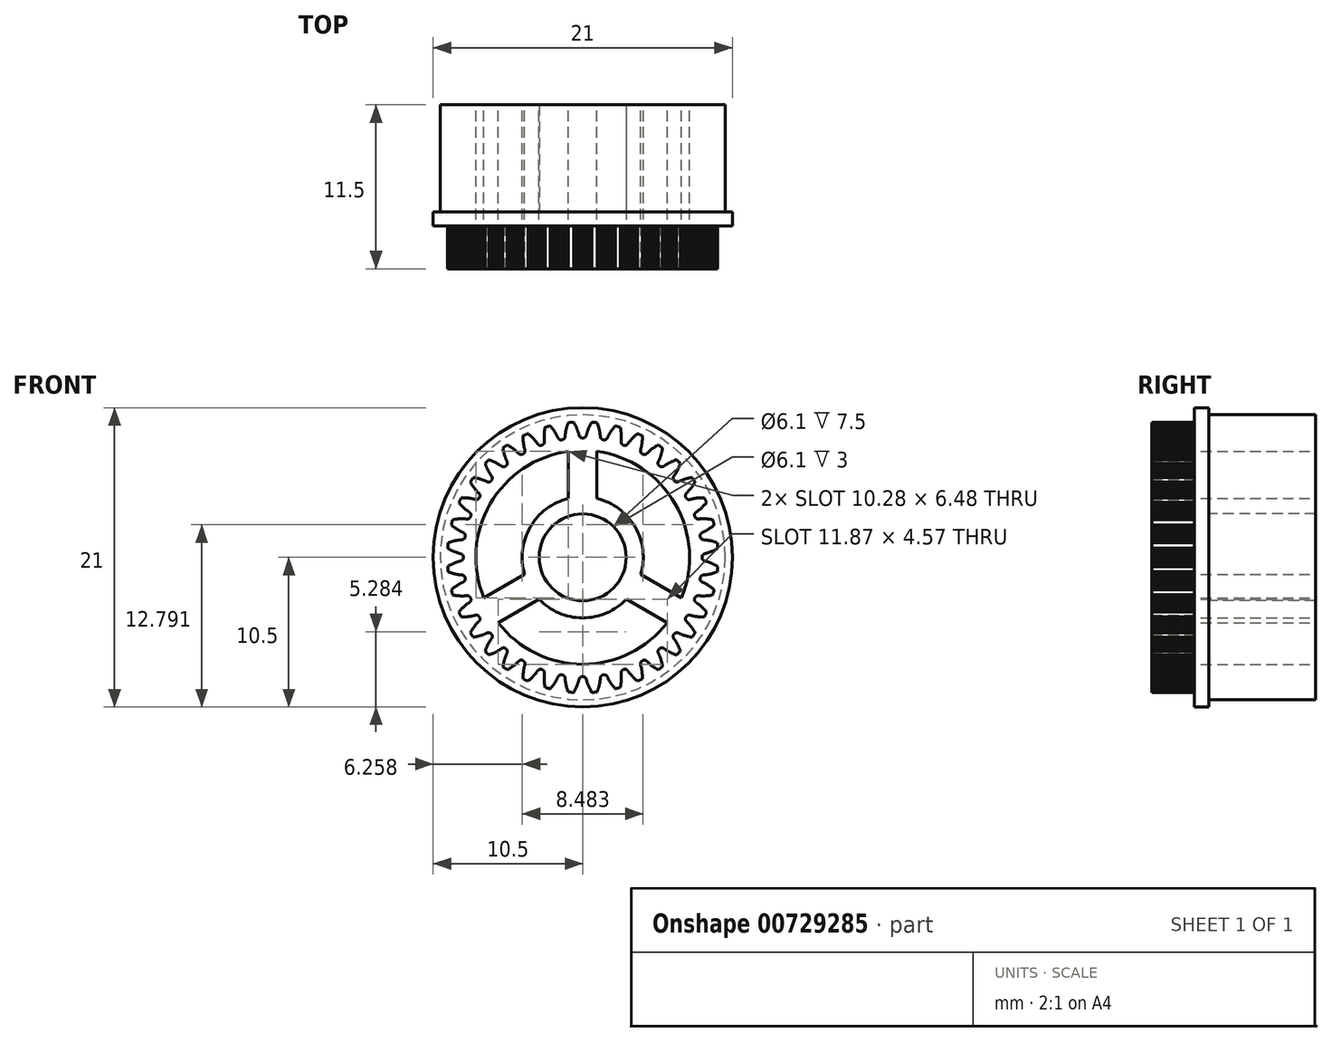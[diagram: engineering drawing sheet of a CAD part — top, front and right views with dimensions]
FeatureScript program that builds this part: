
annotation { "Feature Type Name" : "Feature", "Feature Type Description" : "" }
export const myFeature = defineFeature(function(context is Context, id is Id, definition is map)
    precondition{}
    {
        {
            var Q0;
            Q0=qCreatedBy(makeId("Front.planeOp"),FACE);
            var sketch = newSketch(context, id + "F0", { "sketchPlane" : qUnion([Q0])});
            skLineSegment(sketch, "E0", {"start": v(8.38, 0) * mm, "end": v(8.37, 0) * mm});
            skLineSegment(sketch, "E1", {"start": v(8.37, 0) * mm, "end": v(8.37, 0.01) * mm});
            skLineSegment(sketch, "E2", {"start": v(8.37, 0.01) * mm, "end": v(8.37, 0.02) * mm});
            skLineSegment(sketch, "E3", {"start": v(8.37, 0.02) * mm, "end": v(8.37, 0.02) * mm});
            skLineSegment(sketch, "E4", {"start": v(8.37, 0.02) * mm, "end": v(8.37, 0.03) * mm});
            skLineSegment(sketch, "E5", {"start": v(8.37, 0.03) * mm, "end": v(8.38, 0.06) * mm});
            skLineSegment(sketch, "E6", {"start": v(8.38, 0.06) * mm, "end": v(8.38, 0.08) * mm});
            skLineSegment(sketch, "E7", {"start": v(8.38, 0.08) * mm, "end": v(8.39, 0.1) * mm});
            skLineSegment(sketch, "E8", {"start": v(8.39, 0.1) * mm, "end": v(8.4, 0.11) * mm});
            skLineSegment(sketch, "E9", {"start": v(8.4, 0.11) * mm, "end": v(8.4, 0.13) * mm});
            skLineSegment(sketch, "E10", {"start": v(8.4, 0.13) * mm, "end": v(8.4, 0.14) * mm});
            skLineSegment(sketch, "E11", {"start": v(8.4, 0.14) * mm, "end": v(8.42, 0.16) * mm});
            skLineSegment(sketch, "E12", {"start": v(8.42, 0.16) * mm, "end": v(8.43, 0.17) * mm});
            skLineSegment(sketch, "E13", {"start": v(8.43, 0.17) * mm, "end": v(8.44, 0.18) * mm});
            skLineSegment(sketch, "E14", {"start": v(8.44, 0.18) * mm, "end": v(8.45, 0.2) * mm});
            skLineSegment(sketch, "E15", {"start": v(8.45, 0.2) * mm, "end": v(8.46, 0.2) * mm});
            skLineSegment(sketch, "E16", {"start": v(8.46, 0.2) * mm, "end": v(8.48, 0.21) * mm});
            skLineSegment(sketch, "E17", {"start": v(8.48, 0.21) * mm, "end": v(8.5, 0.22) * mm});
            skLineSegment(sketch, "E18", {"start": v(8.5, 0.22) * mm, "end": v(8.5, 0.23) * mm});
            skLineSegment(sketch, "E19", {"start": v(8.5, 0.23) * mm, "end": v(8.52, 0.24) * mm});
            skLineSegment(sketch, "E20", {"start": v(8.52, 0.24) * mm, "end": v(8.54, 0.25) * mm});
            skLineSegment(sketch, "E21", {"start": v(8.54, 0.25) * mm, "end": v(8.55, 0.25) * mm});
            skLineSegment(sketch, "E22", {"start": v(8.55, 0.25) * mm, "end": v(8.57, 0.26) * mm});
            skLineSegment(sketch, "E23", {"start": v(8.57, 0.26) * mm, "end": v(8.59, 0.26) * mm});
            skLineSegment(sketch, "E24", {"start": v(8.59, 0.26) * mm, "end": v(8.6, 0.27) * mm});
            skLineSegment(sketch, "E25", {"start": v(8.6, 0.27) * mm, "end": v(8.65, 0.28) * mm});
            skLineSegment(sketch, "E26", {"start": v(8.65, 0.28) * mm, "end": v(8.7, 0.29) * mm});
            skLineSegment(sketch, "E27", {"start": v(8.7, 0.29) * mm, "end": v(8.74, 0.3) * mm});
            skLineSegment(sketch, "E28", {"start": v(8.74, 0.3) * mm, "end": v(8.78, 0.32) * mm});
            skLineSegment(sketch, "E29", {"start": v(8.78, 0.32) * mm, "end": v(8.83, 0.33) * mm});
            skLineSegment(sketch, "E30", {"start": v(8.83, 0.33) * mm, "end": v(8.87, 0.35) * mm});
            skLineSegment(sketch, "E31", {"start": v(8.87, 0.35) * mm, "end": v(8.91, 0.36) * mm});
            skLineSegment(sketch, "E32", {"start": v(8.91, 0.36) * mm, "end": v(8.96, 0.38) * mm});
            skLineSegment(sketch, "E33", {"start": v(8.96, 0.38) * mm, "end": v(9, 0.4) * mm});
            skLineSegment(sketch, "E34", {"start": v(9, 0.4) * mm, "end": v(9.05, 0.42) * mm});
            skLineSegment(sketch, "E35", {"start": v(9.05, 0.42) * mm, "end": v(9.09, 0.44) * mm});
            skLineSegment(sketch, "E36", {"start": v(9.09, 0.44) * mm, "end": v(9.13, 0.46) * mm});
            skLineSegment(sketch, "E37", {"start": v(9.13, 0.46) * mm, "end": v(9.18, 0.48) * mm});
            skLineSegment(sketch, "E38", {"start": v(9.18, 0.48) * mm, "end": v(9.22, 0.5) * mm});
            skLineSegment(sketch, "E39", {"start": v(9.22, 0.5) * mm, "end": v(9.26, 0.52) * mm});
            skLineSegment(sketch, "E40", {"start": v(9.26, 0.52) * mm, "end": v(9.3, 0.54) * mm});
            skLineSegment(sketch, "E41", {"start": v(9.3, 0.54) * mm, "end": v(9.35, 0.57) * mm});
            skLineSegment(sketch, "E42", {"start": v(9.35, 0.57) * mm, "end": v(9.4, 0.6) * mm});
            skLineSegment(sketch, "E43", {"start": v(9.4, 0.6) * mm, "end": v(9.44, 0.61) * mm});
            skLineSegment(sketch, "E44", {"start": v(9.44, 0.61) * mm, "end": v(9.48, 0.64) * mm});
            skLineSegment(sketch, "E45", {"start": v(9.48, 0.64) * mm, "end": v(9.48, 0.68) * mm});
            skLineSegment(sketch, "E46", {"start": v(9.48, 0.68) * mm, "end": v(9.47, 0.72) * mm});
            skLineSegment(sketch, "E47", {"start": v(9.47, 0.72) * mm, "end": v(9.47, 0.75) * mm});
            skLineSegment(sketch, "E48", {"start": v(9.47, 0.75) * mm, "end": v(9.47, 0.8) * mm});
            skLineSegment(sketch, "E49", {"start": v(9.47, 0.8) * mm, "end": v(9.46, 0.83) * mm});
            skLineSegment(sketch, "E50.MirrorCS", {"start": v(8.37, -0.02) * mm, "end": v(8.37, -0.03) * mm});
            skLineSegment(sketch, "E51.MirrorCS", {"start": v(8.37, 0) * mm, "end": v(8.37, -0.01) * mm});
            skLineSegment(sketch, "E52.MirrorCS", {"start": v(8.37, -0.02) * mm, "end": v(8.37, -0.02) * mm});
            skLineSegment(sketch, "E53.MirrorCS", {"start": v(8.37, -0.03) * mm, "end": v(8.38, -0.06) * mm});
            skLineSegment(sketch, "E54.MirrorCS", {"start": v(8.37, -0.01) * mm, "end": v(8.37, -0.02) * mm});
            skLineSegment(sketch, "E55.MirrorCS", {"start": v(8.38, -0.06) * mm, "end": v(8.38, -0.08) * mm});
            skLineSegment(sketch, "E56.MirrorCS", {"start": v(8.43, -0.17) * mm, "end": v(8.44, -0.18) * mm});
            skLineSegment(sketch, "E57.MirrorCS", {"start": v(8.52, -0.24) * mm, "end": v(8.54, -0.25) * mm});
            skLineSegment(sketch, "E58.MirrorCS", {"start": v(8.42, -0.16) * mm, "end": v(8.43, -0.17) * mm});
            skLineSegment(sketch, "E59.MirrorCS", {"start": v(8.5, -0.23) * mm, "end": v(8.52, -0.24) * mm});
            skLineSegment(sketch, "E60.MirrorCS", {"start": v(8.5, -0.22) * mm, "end": v(8.5, -0.23) * mm});
            skLineSegment(sketch, "E61.MirrorCS", {"start": v(9.47, -0.72) * mm, "end": v(9.47, -0.75) * mm});
            skLineSegment(sketch, "E62.MirrorCS", {"start": v(9.48, -0.68) * mm, "end": v(9.47, -0.72) * mm});
            skLineSegment(sketch, "E63.MirrorCS", {"start": v(8.46, -0.2) * mm, "end": v(8.48, -0.21) * mm});
            skLineSegment(sketch, "E64.MirrorCS", {"start": v(8.48, -0.21) * mm, "end": v(8.5, -0.22) * mm});
            skLineSegment(sketch, "E65.MirrorCS", {"start": v(8.4, -0.14) * mm, "end": v(8.42, -0.16) * mm});
            skLineSegment(sketch, "E66.MirrorCS", {"start": v(8.4, -0.13) * mm, "end": v(8.4, -0.14) * mm});
            skLineSegment(sketch, "E67.MirrorCS", {"start": v(8.4, -0.11) * mm, "end": v(8.4, -0.13) * mm});
            skLineSegment(sketch, "E68.MirrorCS", {"start": v(8.45, -0.2) * mm, "end": v(8.46, -0.2) * mm});
            skLineSegment(sketch, "E69.MirrorCS", {"start": v(8.44, -0.18) * mm, "end": v(8.45, -0.2) * mm});
            skLineSegment(sketch, "E70.MirrorCS", {"start": v(8.54, -0.25) * mm, "end": v(8.55, -0.25) * mm});
            skLineSegment(sketch, "E71.MirrorCS", {"start": v(8.55, -0.25) * mm, "end": v(8.57, -0.26) * mm});
            skLineSegment(sketch, "E72.MirrorCS", {"start": v(9.47, -0.75) * mm, "end": v(9.47, -0.8) * mm});
            skLineSegment(sketch, "E73.MirrorCS", {"start": v(8.57, -0.26) * mm, "end": v(8.59, -0.26) * mm});
            skLineSegment(sketch, "E74.MirrorCS", {"start": v(9.48, -0.64) * mm, "end": v(9.48, -0.68) * mm});
            skLineSegment(sketch, "E75.MirrorCS", {"start": v(8.38, -0.08) * mm, "end": v(8.39, -0.1) * mm});
            skLineSegment(sketch, "E76.MirrorCS", {"start": v(9.26, -0.52) * mm, "end": v(9.3, -0.54) * mm});
            skLineSegment(sketch, "E77.MirrorCS", {"start": v(8.74, -0.3) * mm, "end": v(8.78, -0.32) * mm});
            skLineSegment(sketch, "E78.MirrorCS", {"start": v(9.44, -0.61) * mm, "end": v(9.48, -0.64) * mm});
            skLineSegment(sketch, "E79.MirrorCS", {"start": v(8.78, -0.32) * mm, "end": v(8.83, -0.33) * mm});
            skLineSegment(sketch, "E80.MirrorCS", {"start": v(8.65, -0.28) * mm, "end": v(8.7, -0.29) * mm});
            skLineSegment(sketch, "E81.MirrorCS", {"start": v(9.13, -0.46) * mm, "end": v(9.18, -0.48) * mm});
            skLineSegment(sketch, "E82.MirrorCS", {"start": v(8.83, -0.33) * mm, "end": v(8.87, -0.35) * mm});
            skLineSegment(sketch, "E83.MirrorCS", {"start": v(8.91, -0.36) * mm, "end": v(8.96, -0.38) * mm});
            skLineSegment(sketch, "E84.MirrorCS", {"start": v(9.09, -0.44) * mm, "end": v(9.13, -0.46) * mm});
            skLineSegment(sketch, "E85.MirrorCS", {"start": v(9.22, -0.5) * mm, "end": v(9.26, -0.52) * mm});
            skLineSegment(sketch, "E86.MirrorCS", {"start": v(9.4, -0.6) * mm, "end": v(9.44, -0.61) * mm});
            skLineSegment(sketch, "E87.MirrorCS", {"start": v(8.96, -0.38) * mm, "end": v(9, -0.4) * mm});
            skLineSegment(sketch, "E88.MirrorCS", {"start": v(9.47, -0.8) * mm, "end": v(9.46, -0.83) * mm});
            skLineSegment(sketch, "E89.MirrorCS", {"start": v(9.05, -0.42) * mm, "end": v(9.09, -0.44) * mm});
            skLineSegment(sketch, "E90.MirrorCS", {"start": v(9, -0.4) * mm, "end": v(9.05, -0.42) * mm});
            skLineSegment(sketch, "E91.MirrorCS", {"start": v(9.35, -0.57) * mm, "end": v(9.4, -0.6) * mm});
            skLineSegment(sketch, "E92.MirrorCS", {"start": v(8.87, -0.35) * mm, "end": v(8.91, -0.36) * mm});
            skLineSegment(sketch, "E93.MirrorCS", {"start": v(9.18, -0.48) * mm, "end": v(9.22, -0.5) * mm});
            skLineSegment(sketch, "E94.MirrorCS", {"start": v(8.6, -0.27) * mm, "end": v(8.65, -0.28) * mm});
            skLineSegment(sketch, "E95.MirrorCS", {"start": v(8.7, -0.29) * mm, "end": v(8.74, -0.3) * mm});
            skLineSegment(sketch, "E96.MirrorCS", {"start": v(9.3, -0.54) * mm, "end": v(9.35, -0.57) * mm});
            skLineSegment(sketch, "E97.MirrorCS", {"start": v(8.39, -0.1) * mm, "end": v(8.4, -0.11) * mm});
            skLineSegment(sketch, "E98.MirrorCS", {"start": v(8.59, -0.26) * mm, "end": v(8.6, -0.27) * mm});
            skLineSegment(sketch, "E99.1.0", {"start": v(9.26, 1.08) * mm, "end": v(9.3, 1.07) * mm});
            skLineSegment(sketch, "E99.1.1", {"start": v(9.07, 2.15) * mm, "end": v(9.1, 2.18) * mm});
            skLineSegment(sketch, "E99.1.2", {"start": v(9.46, 0.87) * mm, "end": v(9.46, 0.83) * mm});
            skLineSegment(sketch, "E99.1.3", {"start": v(9.46, 0.9) * mm, "end": v(9.46, 0.87) * mm});
            skLineSegment(sketch, "E99.1.4", {"start": v(9.07, 1.14) * mm, "end": v(9.12, 1.12) * mm});
            skLineSegment(sketch, "E99.1.5", {"start": v(8.72, 1.9) * mm, "end": v(8.76, 1.93) * mm});
            skLineSegment(sketch, "E99.1.6", {"start": v(8.98, 1.16) * mm, "end": v(9.03, 1.15) * mm});
            skLineSegment(sketch, "E99.1.7", {"start": v(8.66, 1.22) * mm, "end": v(8.7, 1.21) * mm});
            skLineSegment(sketch, "E99.1.8", {"start": v(9.03, 1.15) * mm, "end": v(9.07, 1.14) * mm});
            skLineSegment(sketch, "E99.1.9", {"start": v(8.75, 1.2) * mm, "end": v(8.8, 1.2) * mm});
            skLineSegment(sketch, "E99.1.10", {"start": v(8.8, 1.95) * mm, "end": v(8.84, 1.98) * mm});
            skLineSegment(sketch, "E99.1.11", {"start": v(8.6, 1.84) * mm, "end": v(8.64, 1.86) * mm});
            skLineSegment(sketch, "E99.1.12", {"start": v(8.88, 2) * mm, "end": v(8.92, 2.03) * mm});
            skLineSegment(sketch, "E99.1.13", {"start": v(8.89, 1.18) * mm, "end": v(8.93, 1.17) * mm});
            skLineSegment(sketch, "E99.1.14", {"start": v(9.3, 1.07) * mm, "end": v(9.35, 1.05) * mm});
            skLineSegment(sketch, "E99.1.15", {"start": v(8.84, 1.2) * mm, "end": v(8.89, 1.18) * mm});
            skLineSegment(sketch, "E99.1.16", {"start": v(9.21, 1.1) * mm, "end": v(9.26, 1.08) * mm});
            skLineSegment(sketch, "E99.1.17", {"start": v(8.93, 1.17) * mm, "end": v(8.98, 1.16) * mm});
            skLineSegment(sketch, "E99.1.18", {"start": v(9.03, 2.12) * mm, "end": v(9.07, 2.15) * mm});
            skLineSegment(sketch, "E99.1.19", {"start": v(9.35, 1.05) * mm, "end": v(9.4, 1.03) * mm});
            skLineSegment(sketch, "E99.1.20", {"start": v(9.45, 0.94) * mm, "end": v(9.46, 0.9) * mm});
            skLineSegment(sketch, "E99.1.21", {"start": v(8.55, 1.81) * mm, "end": v(8.6, 1.84) * mm});
            skLineSegment(sketch, "E99.1.22", {"start": v(8.68, 1.88) * mm, "end": v(8.72, 1.9) * mm});
            skLineSegment(sketch, "E99.1.23", {"start": v(8.95, 2.06) * mm, "end": v(9, 2.1) * mm});
            skLineSegment(sketch, "E99.1.24", {"start": v(9.12, 1.12) * mm, "end": v(9.17, 1.11) * mm});
            skLineSegment(sketch, "E99.1.25", {"start": v(8.7, 1.21) * mm, "end": v(8.75, 1.2) * mm});
            skLineSegment(sketch, "E99.1.26", {"start": v(9.4, 1.03) * mm, "end": v(9.45, 1.02) * mm});
            skLineSegment(sketch, "E99.1.27", {"start": v(9.45, 0.98) * mm, "end": v(9.45, 0.94) * mm});
            skLineSegment(sketch, "E99.1.28", {"start": v(9.17, 1.11) * mm, "end": v(9.21, 1.1) * mm});
            skLineSegment(sketch, "E99.1.29", {"start": v(8.76, 1.93) * mm, "end": v(8.8, 1.95) * mm});
            skLineSegment(sketch, "E99.1.30", {"start": v(9, 2.1) * mm, "end": v(9.03, 2.12) * mm});
            skLineSegment(sketch, "E99.1.31", {"start": v(8.8, 1.2) * mm, "end": v(8.84, 1.2) * mm});
            skLineSegment(sketch, "E99.1.32", {"start": v(8.92, 2.03) * mm, "end": v(8.95, 2.06) * mm});
            skLineSegment(sketch, "E99.1.33", {"start": v(8.64, 1.86) * mm, "end": v(8.68, 1.88) * mm});
            skLineSegment(sketch, "E99.1.34", {"start": v(9.1, 2.18) * mm, "end": v(9.15, 2.21) * mm});
            skLineSegment(sketch, "E99.1.35", {"start": v(9.19, 2.42) * mm, "end": v(9.18, 2.46) * mm});
            skLineSegment(sketch, "E99.1.36", {"start": v(8.84, 1.98) * mm, "end": v(8.88, 2) * mm});
            skLineSegment(sketch, "E99.1.37", {"start": v(9.2, 2.39) * mm, "end": v(9.19, 2.42) * mm});
            skLineSegment(sketch, "E99.1.38", {"start": v(9.15, 2.21) * mm, "end": v(9.19, 2.24) * mm});
            skLineSegment(sketch, "E99.1.39", {"start": v(9.45, 1.02) * mm, "end": v(9.45, 0.98) * mm});
            skLineSegment(sketch, "E99.1.40", {"start": v(9.19, 2.24) * mm, "end": v(9.22, 2.28) * mm});
            skLineSegment(sketch, "E99.1.41", {"start": v(9.2, 2.35) * mm, "end": v(9.2, 2.39) * mm});
            skLineSegment(sketch, "E99.1.42", {"start": v(9.21, 2.31) * mm, "end": v(9.2, 2.35) * mm});
            skLineSegment(sketch, "E99.1.43", {"start": v(8.51, 1.8) * mm, "end": v(8.55, 1.81) * mm});
            skLineSegment(sketch, "E99.1.44", {"start": v(9.22, 2.28) * mm, "end": v(9.21, 2.31) * mm});
            skLineSegment(sketch, "E99.1.45", {"start": v(8.61, 1.23) * mm, "end": v(8.66, 1.22) * mm});
            skLineSegment(sketch, "E99.1.46", {"start": v(8.32, 1.7) * mm, "end": v(8.34, 1.7) * mm});
            skLineSegment(sketch, "E99.1.47", {"start": v(8.43, 1.76) * mm, "end": v(8.47, 1.78) * mm});
            skLineSegment(sketch, "E99.1.48", {"start": v(8.47, 1.78) * mm, "end": v(8.51, 1.8) * mm});
            skLineSegment(sketch, "E99.1.49", {"start": v(8.43, 1.24) * mm, "end": v(8.45, 1.24) * mm});
            skLineSegment(sketch, "E99.1.50", {"start": v(8.35, 1.71) * mm, "end": v(8.36, 1.72) * mm});
            skLineSegment(sketch, "E99.1.51", {"start": v(8.38, 1.26) * mm, "end": v(8.4, 1.25) * mm});
            skLineSegment(sketch, "E99.1.52", {"start": v(8.57, 1.23) * mm, "end": v(8.61, 1.23) * mm});
            skLineSegment(sketch, "E99.1.53", {"start": v(8.47, 1.24) * mm, "end": v(8.48, 1.23) * mm});
            skLineSegment(sketch, "E99.1.54", {"start": v(8.5, 1.23) * mm, "end": v(8.52, 1.23) * mm});
            skLineSegment(sketch, "E99.1.55", {"start": v(8.36, 1.72) * mm, "end": v(8.38, 1.73) * mm});
            skLineSegment(sketch, "E99.1.56", {"start": v(8.41, 1.75) * mm, "end": v(8.43, 1.76) * mm});
            skLineSegment(sketch, "E99.1.57", {"start": v(8.45, 1.24) * mm, "end": v(8.47, 1.24) * mm});
            skLineSegment(sketch, "E99.1.58", {"start": v(8.31, 1.68) * mm, "end": v(8.32, 1.7) * mm});
            skLineSegment(sketch, "E99.1.59", {"start": v(8.52, 1.23) * mm, "end": v(8.57, 1.23) * mm});
            skLineSegment(sketch, "E99.1.60", {"start": v(8.4, 1.74) * mm, "end": v(8.41, 1.75) * mm});
            skLineSegment(sketch, "E99.1.61", {"start": v(8.34, 1.7) * mm, "end": v(8.35, 1.71) * mm});
            skLineSegment(sketch, "E99.1.62", {"start": v(8.48, 1.23) * mm, "end": v(8.5, 1.23) * mm});
            skLineSegment(sketch, "E99.1.63", {"start": v(8.38, 1.73) * mm, "end": v(8.4, 1.74) * mm});
            skLineSegment(sketch, "E99.1.64", {"start": v(8.3, 1.67) * mm, "end": v(8.31, 1.68) * mm});
            skLineSegment(sketch, "E99.1.65", {"start": v(8.37, 1.27) * mm, "end": v(8.38, 1.26) * mm});
            skLineSegment(sketch, "E99.1.66", {"start": v(8.4, 1.25) * mm, "end": v(8.42, 1.25) * mm});
            skLineSegment(sketch, "E99.1.67", {"start": v(8.29, 1.66) * mm, "end": v(8.3, 1.67) * mm});
            skLineSegment(sketch, "E99.1.68", {"start": v(8.42, 1.25) * mm, "end": v(8.43, 1.24) * mm});
            skLineSegment(sketch, "E99.1.69", {"start": v(8.36, 1.28) * mm, "end": v(8.37, 1.27) * mm});
            skLineSegment(sketch, "E99.1.70", {"start": v(8.32, 1.3) * mm, "end": v(8.33, 1.3) * mm});
            skLineSegment(sketch, "E99.1.71", {"start": v(8.34, 1.29) * mm, "end": v(8.36, 1.28) * mm});
            skLineSegment(sketch, "E99.1.72", {"start": v(8.33, 1.3) * mm, "end": v(8.34, 1.29) * mm});
            skLineSegment(sketch, "E99.1.73", {"start": v(8.3, 1.33) * mm, "end": v(8.3, 1.32) * mm});
            skLineSegment(sketch, "E99.1.74", {"start": v(8.28, 1.65) * mm, "end": v(8.29, 1.66) * mm});
            skLineSegment(sketch, "E99.1.75", {"start": v(8.3, 1.32) * mm, "end": v(8.32, 1.3) * mm});
            skLineSegment(sketch, "E99.1.76", {"start": v(8.25, 1.45) * mm, "end": v(8.25, 1.45) * mm});
            skLineSegment(sketch, "E99.1.77", {"start": v(8.26, 1.4) * mm, "end": v(8.27, 1.38) * mm});
            skLineSegment(sketch, "E99.1.78", {"start": v(8.25, 1.42) * mm, "end": v(8.26, 1.4) * mm});
            skLineSegment(sketch, "E99.1.79", {"start": v(8.24, 1.48) * mm, "end": v(8.24, 1.51) * mm});
            skLineSegment(sketch, "E99.1.80", {"start": v(8.25, 1.59) * mm, "end": v(8.26, 1.6) * mm});
            skLineSegment(sketch, "E99.1.81", {"start": v(8.26, 1.62) * mm, "end": v(8.27, 1.63) * mm});
            skLineSegment(sketch, "E99.1.82", {"start": v(8.28, 1.34) * mm, "end": v(8.3, 1.33) * mm});
            skLineSegment(sketch, "E99.1.83", {"start": v(8.24, 1.53) * mm, "end": v(8.24, 1.55) * mm});
            skLineSegment(sketch, "E99.1.84", {"start": v(8.27, 1.63) * mm, "end": v(8.28, 1.65) * mm});
            skLineSegment(sketch, "E99.1.85", {"start": v(8.27, 1.38) * mm, "end": v(8.28, 1.36) * mm});
            skLineSegment(sketch, "E99.1.86", {"start": v(8.26, 1.6) * mm, "end": v(8.26, 1.62) * mm});
            skLineSegment(sketch, "E99.1.87", {"start": v(8.24, 1.51) * mm, "end": v(8.24, 1.53) * mm});
            skLineSegment(sketch, "E99.1.88", {"start": v(8.24, 1.57) * mm, "end": v(8.25, 1.59) * mm});
            skLineSegment(sketch, "E99.1.89", {"start": v(8.25, 1.44) * mm, "end": v(8.25, 1.44) * mm});
            skLineSegment(sketch, "E99.1.90", {"start": v(8.25, 1.43) * mm, "end": v(8.25, 1.42) * mm});
            skLineSegment(sketch, "E99.1.91", {"start": v(8.28, 1.36) * mm, "end": v(8.28, 1.34) * mm});
            skLineSegment(sketch, "E99.1.92", {"start": v(8.24, 1.55) * mm, "end": v(8.24, 1.57) * mm});
            skLineSegment(sketch, "E99.1.93", {"start": v(8.24, 1.48) * mm, "end": v(8.24, 1.48) * mm});
            skLineSegment(sketch, "E99.1.94", {"start": v(8.24, 1.47) * mm, "end": v(8.24, 1.48) * mm});
            skLineSegment(sketch, "E99.1.95", {"start": v(8.25, 1.47) * mm, "end": v(8.24, 1.47) * mm});
            skLineSegment(sketch, "E99.1.96", {"start": v(8.25, 1.46) * mm, "end": v(8.25, 1.47) * mm});
            skLineSegment(sketch, "E99.1.97", {"start": v(8.25, 1.45) * mm, "end": v(8.25, 1.46) * mm});
            skLineSegment(sketch, "E99.1.98", {"start": v(8.25, 1.44) * mm, "end": v(8.25, 1.43) * mm});
            skLineSegment(sketch, "E99.1.99", {"start": v(8.25, 1.45) * mm, "end": v(8.25, 1.44) * mm});
            skLineSegment(sketch, "E99.2.0", {"start": v(8.93, 2.67) * mm, "end": v(8.98, 2.67) * mm});
            skLineSegment(sketch, "E99.2.1", {"start": v(8.56, 3.7) * mm, "end": v(8.6, 3.73) * mm});
            skLineSegment(sketch, "E99.2.2", {"start": v(9.17, 2.5) * mm, "end": v(9.18, 2.46) * mm});
            skLineSegment(sketch, "E99.2.3", {"start": v(9.16, 2.53) * mm, "end": v(9.17, 2.5) * mm});
            skLineSegment(sketch, "E99.2.4", {"start": v(8.74, 2.7) * mm, "end": v(8.79, 2.7) * mm});
            skLineSegment(sketch, "E99.2.5", {"start": v(8.25, 3.39) * mm, "end": v(8.29, 3.42) * mm});
            skLineSegment(sketch, "E99.2.6", {"start": v(8.64, 2.7) * mm, "end": v(8.69, 2.7) * mm});
            skLineSegment(sketch, "E99.2.7", {"start": v(8.31, 2.7) * mm, "end": v(8.36, 2.7) * mm});
            skLineSegment(sketch, "E99.2.8", {"start": v(8.69, 2.7) * mm, "end": v(8.74, 2.7) * mm});
            skLineSegment(sketch, "E99.2.9", {"start": v(8.4, 2.7) * mm, "end": v(8.45, 2.7) * mm});
            skLineSegment(sketch, "E99.2.10", {"start": v(8.32, 3.45) * mm, "end": v(8.36, 3.48) * mm});
            skLineSegment(sketch, "E99.2.11", {"start": v(8.15, 3.3) * mm, "end": v(8.18, 3.33) * mm});
            skLineSegment(sketch, "E99.2.12", {"start": v(8.4, 3.52) * mm, "end": v(8.43, 3.55) * mm});
            skLineSegment(sketch, "E99.2.13", {"start": v(8.55, 2.7) * mm, "end": v(8.6, 2.7) * mm});
            skLineSegment(sketch, "E99.2.14", {"start": v(8.98, 2.67) * mm, "end": v(9.03, 2.66) * mm});
            skLineSegment(sketch, "E99.2.15", {"start": v(8.5, 2.7) * mm, "end": v(8.55, 2.7) * mm});
            skLineSegment(sketch, "E99.2.16", {"start": v(8.88, 2.68) * mm, "end": v(8.93, 2.67) * mm});
            skLineSegment(sketch, "E99.2.17", {"start": v(8.6, 2.7) * mm, "end": v(8.64, 2.7) * mm});
            skLineSegment(sketch, "E99.2.18", {"start": v(8.53, 3.66) * mm, "end": v(8.56, 3.7) * mm});
            skLineSegment(sketch, "E99.2.19", {"start": v(9.03, 2.66) * mm, "end": v(9.08, 2.65) * mm});
            skLineSegment(sketch, "E99.2.20", {"start": v(9.15, 2.57) * mm, "end": v(9.16, 2.53) * mm});
            skLineSegment(sketch, "E99.2.21", {"start": v(8.1, 3.27) * mm, "end": v(8.15, 3.3) * mm});
            skLineSegment(sketch, "E99.2.22", {"start": v(8.22, 3.36) * mm, "end": v(8.25, 3.39) * mm});
            skLineSegment(sketch, "E99.2.23", {"start": v(8.46, 3.59) * mm, "end": v(8.5, 3.62) * mm});
            skLineSegment(sketch, "E99.2.24", {"start": v(8.79, 2.7) * mm, "end": v(8.83, 2.69) * mm});
            skLineSegment(sketch, "E99.2.25", {"start": v(8.36, 2.7) * mm, "end": v(8.4, 2.7) * mm});
            skLineSegment(sketch, "E99.2.26", {"start": v(9.08, 2.65) * mm, "end": v(9.13, 2.64) * mm});
            skLineSegment(sketch, "E99.2.27", {"start": v(9.14, 2.6) * mm, "end": v(9.15, 2.57) * mm});
            skLineSegment(sketch, "E99.2.28", {"start": v(8.83, 2.69) * mm, "end": v(8.88, 2.68) * mm});
            skLineSegment(sketch, "E99.2.29", {"start": v(8.29, 3.42) * mm, "end": v(8.32, 3.45) * mm});
            skLineSegment(sketch, "E99.2.30", {"start": v(8.5, 3.62) * mm, "end": v(8.53, 3.66) * mm});
            skLineSegment(sketch, "E99.2.31", {"start": v(8.45, 2.7) * mm, "end": v(8.5, 2.7) * mm});
            skLineSegment(sketch, "E99.2.32", {"start": v(8.43, 3.55) * mm, "end": v(8.46, 3.59) * mm});
            skLineSegment(sketch, "E99.2.33", {"start": v(8.18, 3.33) * mm, "end": v(8.22, 3.36) * mm});
            skLineSegment(sketch, "E99.2.34", {"start": v(8.6, 3.73) * mm, "end": v(8.62, 3.77) * mm});
            skLineSegment(sketch, "E99.2.35", {"start": v(8.63, 3.98) * mm, "end": v(8.6, 4.01) * mm});
            skLineSegment(sketch, "E99.2.36", {"start": v(8.36, 3.48) * mm, "end": v(8.4, 3.52) * mm});
            skLineSegment(sketch, "E99.2.37", {"start": v(8.64, 3.95) * mm, "end": v(8.63, 3.98) * mm});
            skLineSegment(sketch, "E99.2.38", {"start": v(8.62, 3.77) * mm, "end": v(8.66, 3.8) * mm});
            skLineSegment(sketch, "E99.2.39", {"start": v(9.13, 2.64) * mm, "end": v(9.14, 2.6) * mm});
            skLineSegment(sketch, "E99.2.40", {"start": v(8.66, 3.8) * mm, "end": v(8.69, 3.84) * mm});
            skLineSegment(sketch, "E99.2.41", {"start": v(8.66, 3.91) * mm, "end": v(8.64, 3.95) * mm});
            skLineSegment(sketch, "E99.2.42", {"start": v(8.67, 3.88) * mm, "end": v(8.66, 3.91) * mm});
            skLineSegment(sketch, "E99.2.43", {"start": v(8.07, 3.25) * mm, "end": v(8.1, 3.27) * mm});
            skLineSegment(sketch, "E99.2.44", {"start": v(8.69, 3.84) * mm, "end": v(8.67, 3.88) * mm});
            skLineSegment(sketch, "E99.2.45", {"start": v(8.27, 2.7) * mm, "end": v(8.31, 2.7) * mm});
            skLineSegment(sketch, "E99.2.46", {"start": v(7.9, 3.11) * mm, "end": v(7.91, 3.13) * mm});
            skLineSegment(sketch, "E99.2.47", {"start": v(8, 3.2) * mm, "end": v(8.03, 3.22) * mm});
            skLineSegment(sketch, "E99.2.48", {"start": v(8.03, 3.22) * mm, "end": v(8.07, 3.25) * mm});
            skLineSegment(sketch, "E99.2.49", {"start": v(8.09, 2.69) * mm, "end": v(8.1, 2.69) * mm});
            skLineSegment(sketch, "E99.2.50", {"start": v(7.92, 3.14) * mm, "end": v(7.94, 3.15) * mm});
            skLineSegment(sketch, "E99.2.51", {"start": v(8.04, 2.7) * mm, "end": v(8.05, 2.7) * mm});
            skLineSegment(sketch, "E99.2.52", {"start": v(8.22, 2.7) * mm, "end": v(8.27, 2.7) * mm});
            skLineSegment(sketch, "E99.2.53", {"start": v(8.12, 2.69) * mm, "end": v(8.14, 2.69) * mm});
            skLineSegment(sketch, "E99.2.54", {"start": v(8.16, 2.7) * mm, "end": v(8.18, 2.7) * mm});
            skLineSegment(sketch, "E99.2.55", {"start": v(7.94, 3.15) * mm, "end": v(7.95, 3.16) * mm});
            skLineSegment(sketch, "E99.2.56", {"start": v(7.98, 3.18) * mm, "end": v(8, 3.2) * mm});
            skLineSegment(sketch, "E99.2.57", {"start": v(8.1, 2.69) * mm, "end": v(8.12, 2.69) * mm});
            skLineSegment(sketch, "E99.2.58", {"start": v(7.9, 3.1) * mm, "end": v(7.9, 3.11) * mm});
            skLineSegment(sketch, "E99.2.59", {"start": v(8.18, 2.7) * mm, "end": v(8.22, 2.7) * mm});
            skLineSegment(sketch, "E99.2.60", {"start": v(7.97, 3.17) * mm, "end": v(7.98, 3.18) * mm});
            skLineSegment(sketch, "E99.2.61", {"start": v(7.91, 3.13) * mm, "end": v(7.92, 3.14) * mm});
            skLineSegment(sketch, "E99.2.62", {"start": v(8.14, 2.69) * mm, "end": v(8.16, 2.7) * mm});
            skLineSegment(sketch, "E99.2.63", {"start": v(7.95, 3.16) * mm, "end": v(7.97, 3.17) * mm});
            skLineSegment(sketch, "E99.2.64", {"start": v(7.88, 3.09) * mm, "end": v(7.9, 3.1) * mm});
            skLineSegment(sketch, "E99.2.65", {"start": v(8.02, 2.7) * mm, "end": v(8.04, 2.7) * mm});
            skLineSegment(sketch, "E99.2.66", {"start": v(8.05, 2.7) * mm, "end": v(8.07, 2.7) * mm});
            skLineSegment(sketch, "E99.2.67", {"start": v(7.87, 3.07) * mm, "end": v(7.88, 3.09) * mm});
            skLineSegment(sketch, "E99.2.68", {"start": v(8.07, 2.7) * mm, "end": v(8.09, 2.69) * mm});
            skLineSegment(sketch, "E99.2.69", {"start": v(8, 2.7) * mm, "end": v(8.02, 2.7) * mm});
            skLineSegment(sketch, "E99.2.70", {"start": v(7.96, 2.73) * mm, "end": v(7.98, 2.72) * mm});
            skLineSegment(sketch, "E99.2.71", {"start": v(8, 2.71) * mm, "end": v(8, 2.7) * mm});
            skLineSegment(sketch, "E99.2.72", {"start": v(7.98, 2.72) * mm, "end": v(8, 2.71) * mm});
            skLineSegment(sketch, "E99.2.73", {"start": v(7.94, 2.75) * mm, "end": v(7.95, 2.74) * mm});
            skLineSegment(sketch, "E99.2.74", {"start": v(7.87, 3.06) * mm, "end": v(7.87, 3.07) * mm});
            skLineSegment(sketch, "E99.2.75", {"start": v(7.95, 2.74) * mm, "end": v(7.96, 2.73) * mm});
            skLineSegment(sketch, "E99.2.76", {"start": v(7.87, 2.86) * mm, "end": v(7.87, 2.86) * mm});
            skLineSegment(sketch, "E99.2.77", {"start": v(7.9, 2.81) * mm, "end": v(7.9, 2.8) * mm});
            skLineSegment(sketch, "E99.2.78", {"start": v(7.88, 2.84) * mm, "end": v(7.9, 2.81) * mm});
            skLineSegment(sketch, "E99.2.79", {"start": v(7.86, 2.9) * mm, "end": v(7.85, 2.92) * mm});
            skLineSegment(sketch, "E99.2.80", {"start": v(7.85, 3) * mm, "end": v(7.85, 3.01) * mm});
            skLineSegment(sketch, "E99.2.81", {"start": v(7.86, 3.03) * mm, "end": v(7.86, 3.04) * mm});
            skLineSegment(sketch, "E99.2.82", {"start": v(7.93, 2.76) * mm, "end": v(7.94, 2.75) * mm});
            skLineSegment(sketch, "E99.2.83", {"start": v(7.85, 2.94) * mm, "end": v(7.85, 2.96) * mm});
            skLineSegment(sketch, "E99.2.84", {"start": v(7.86, 3.04) * mm, "end": v(7.87, 3.06) * mm});
            skLineSegment(sketch, "E99.2.85", {"start": v(7.9, 2.8) * mm, "end": v(7.91, 2.78) * mm});
            skLineSegment(sketch, "E99.2.86", {"start": v(7.85, 3.01) * mm, "end": v(7.86, 3.03) * mm});
            skLineSegment(sketch, "E99.2.87", {"start": v(7.85, 2.92) * mm, "end": v(7.85, 2.94) * mm});
            skLineSegment(sketch, "E99.2.88", {"start": v(7.85, 2.98) * mm, "end": v(7.85, 3) * mm});
            skLineSegment(sketch, "E99.2.89", {"start": v(7.87, 2.85) * mm, "end": v(7.88, 2.85) * mm});
            skLineSegment(sketch, "E99.2.90", {"start": v(7.88, 2.84) * mm, "end": v(7.88, 2.84) * mm});
            skLineSegment(sketch, "E99.2.91", {"start": v(7.91, 2.78) * mm, "end": v(7.93, 2.76) * mm});
            skLineSegment(sketch, "E99.2.92", {"start": v(7.85, 2.96) * mm, "end": v(7.85, 2.98) * mm});
            skLineSegment(sketch, "E99.2.93", {"start": v(7.86, 2.89) * mm, "end": v(7.86, 2.9) * mm});
            skLineSegment(sketch, "E99.2.94", {"start": v(7.86, 2.88) * mm, "end": v(7.86, 2.89) * mm});
            skLineSegment(sketch, "E99.2.95", {"start": v(7.87, 2.88) * mm, "end": v(7.86, 2.88) * mm});
            skLineSegment(sketch, "E99.2.96", {"start": v(7.87, 2.87) * mm, "end": v(7.87, 2.88) * mm});
            skLineSegment(sketch, "E99.2.97", {"start": v(7.87, 2.86) * mm, "end": v(7.87, 2.87) * mm});
            skLineSegment(sketch, "E99.2.98", {"start": v(7.88, 2.85) * mm, "end": v(7.88, 2.84) * mm});
            skLineSegment(sketch, "E99.2.99", {"start": v(7.87, 2.86) * mm, "end": v(7.87, 2.85) * mm});
            skLineSegment(sketch, "E99.3.0", {"start": v(8.33, 4.18) * mm, "end": v(8.38, 4.18) * mm});
            skLineSegment(sketch, "E99.3.1", {"start": v(7.79, 5.12) * mm, "end": v(7.81, 5.16) * mm});
            skLineSegment(sketch, "E99.3.2", {"start": v(8.6, 4.05) * mm, "end": v(8.6, 4.01) * mm});
            skLineSegment(sketch, "E99.3.3", {"start": v(8.58, 4.08) * mm, "end": v(8.6, 4.05) * mm});
            skLineSegment(sketch, "E99.3.4", {"start": v(8.14, 4.17) * mm, "end": v(8.18, 4.18) * mm});
            skLineSegment(sketch, "E99.3.5", {"start": v(7.54, 4.77) * mm, "end": v(7.57, 4.8) * mm});
            skLineSegment(sketch, "E99.3.6", {"start": v(8.04, 4.16) * mm, "end": v(8.09, 4.17) * mm});
            skLineSegment(sketch, "E99.3.7", {"start": v(7.72, 4.1) * mm, "end": v(7.76, 4.12) * mm});
            skLineSegment(sketch, "E99.3.8", {"start": v(8.09, 4.17) * mm, "end": v(8.14, 4.17) * mm});
            skLineSegment(sketch, "E99.3.9", {"start": v(7.8, 4.13) * mm, "end": v(7.85, 4.14) * mm});
            skLineSegment(sketch, "E99.3.10", {"start": v(7.6, 4.84) * mm, "end": v(7.63, 4.88) * mm});
            skLineSegment(sketch, "E99.3.11", {"start": v(7.45, 4.66) * mm, "end": v(7.48, 4.7) * mm});
            skLineSegment(sketch, "E99.3.12", {"start": v(7.65, 4.92) * mm, "end": v(7.68, 4.96) * mm});
            skLineSegment(sketch, "E99.3.13", {"start": v(7.95, 4.15) * mm, "end": v(8, 4.16) * mm});
            skLineSegment(sketch, "E99.3.14", {"start": v(8.38, 4.18) * mm, "end": v(8.43, 4.19) * mm});
            skLineSegment(sketch, "E99.3.15", {"start": v(7.9, 4.14) * mm, "end": v(7.95, 4.15) * mm});
            skLineSegment(sketch, "E99.3.16", {"start": v(8.28, 4.18) * mm, "end": v(8.33, 4.18) * mm});
            skLineSegment(sketch, "E99.3.17", {"start": v(8, 4.16) * mm, "end": v(8.04, 4.16) * mm});
            skLineSegment(sketch, "E99.3.18", {"start": v(7.76, 5.08) * mm, "end": v(7.79, 5.12) * mm});
            skLineSegment(sketch, "E99.3.19", {"start": v(8.43, 4.19) * mm, "end": v(8.48, 4.19) * mm});
            skLineSegment(sketch, "E99.3.20", {"start": v(8.56, 4.12) * mm, "end": v(8.58, 4.08) * mm});
            skLineSegment(sketch, "E99.3.21", {"start": v(7.42, 4.63) * mm, "end": v(7.45, 4.66) * mm});
            skLineSegment(sketch, "E99.3.22", {"start": v(7.5, 4.73) * mm, "end": v(7.54, 4.77) * mm});
            skLineSegment(sketch, "E99.3.23", {"start": v(7.7, 5) * mm, "end": v(7.74, 5.04) * mm});
            skLineSegment(sketch, "E99.3.24", {"start": v(8.18, 4.18) * mm, "end": v(8.23, 4.18) * mm});
            skLineSegment(sketch, "E99.3.25", {"start": v(7.76, 4.12) * mm, "end": v(7.8, 4.13) * mm});
            skLineSegment(sketch, "E99.3.26", {"start": v(8.48, 4.19) * mm, "end": v(8.53, 4.18) * mm});
            skLineSegment(sketch, "E99.3.27", {"start": v(8.55, 4.15) * mm, "end": v(8.56, 4.12) * mm});
            skLineSegment(sketch, "E99.3.28", {"start": v(8.23, 4.18) * mm, "end": v(8.28, 4.18) * mm});
            skLineSegment(sketch, "E99.3.29", {"start": v(7.57, 4.8) * mm, "end": v(7.6, 4.84) * mm});
            skLineSegment(sketch, "E99.3.30", {"start": v(7.74, 5.04) * mm, "end": v(7.76, 5.08) * mm});
            skLineSegment(sketch, "E99.3.31", {"start": v(7.85, 4.14) * mm, "end": v(7.9, 4.14) * mm});
            skLineSegment(sketch, "E99.3.32", {"start": v(7.68, 4.96) * mm, "end": v(7.7, 5) * mm});
            skLineSegment(sketch, "E99.3.33", {"start": v(7.48, 4.7) * mm, "end": v(7.5, 4.73) * mm});
            skLineSegment(sketch, "E99.3.34", {"start": v(7.81, 5.16) * mm, "end": v(7.84, 5.2) * mm});
            skLineSegment(sketch, "E99.3.35", {"start": v(7.8, 5.42) * mm, "end": v(7.78, 5.45) * mm});
            skLineSegment(sketch, "E99.3.36", {"start": v(7.63, 4.88) * mm, "end": v(7.65, 4.92) * mm});
            skLineSegment(sketch, "E99.3.37", {"start": v(7.82, 5.39) * mm, "end": v(7.8, 5.42) * mm});
            skLineSegment(sketch, "E99.3.38", {"start": v(7.84, 5.2) * mm, "end": v(7.86, 5.25) * mm});
            skLineSegment(sketch, "E99.3.39", {"start": v(8.53, 4.18) * mm, "end": v(8.55, 4.15) * mm});
            skLineSegment(sketch, "E99.3.40", {"start": v(7.86, 5.25) * mm, "end": v(7.89, 5.3) * mm});
            skLineSegment(sketch, "E99.3.41", {"start": v(7.85, 5.36) * mm, "end": v(7.82, 5.39) * mm});
            skLineSegment(sketch, "E99.3.42", {"start": v(7.87, 5.32) * mm, "end": v(7.85, 5.36) * mm});
            skLineSegment(sketch, "E99.3.43", {"start": v(7.39, 4.6) * mm, "end": v(7.42, 4.63) * mm});
            skLineSegment(sketch, "E99.3.44", {"start": v(7.89, 5.3) * mm, "end": v(7.87, 5.32) * mm});
            skLineSegment(sketch, "E99.3.45", {"start": v(7.67, 4.1) * mm, "end": v(7.72, 4.1) * mm});
            skLineSegment(sketch, "E99.3.46", {"start": v(7.24, 4.44) * mm, "end": v(7.25, 4.45) * mm});
            skLineSegment(sketch, "E99.3.47", {"start": v(7.32, 4.53) * mm, "end": v(7.35, 4.57) * mm});
            skLineSegment(sketch, "E99.3.48", {"start": v(7.35, 4.57) * mm, "end": v(7.39, 4.6) * mm});
            skLineSegment(sketch, "E99.3.49", {"start": v(7.5, 4.05) * mm, "end": v(7.52, 4.06) * mm});
            skLineSegment(sketch, "E99.3.50", {"start": v(7.26, 4.47) * mm, "end": v(7.27, 4.48) * mm});
            skLineSegment(sketch, "E99.3.51", {"start": v(7.45, 4.05) * mm, "end": v(7.46, 4.05) * mm});
            skLineSegment(sketch, "E99.3.52", {"start": v(7.63, 4.08) * mm, "end": v(7.67, 4.1) * mm});
            skLineSegment(sketch, "E99.3.53", {"start": v(7.53, 4.06) * mm, "end": v(7.55, 4.06) * mm});
            skLineSegment(sketch, "E99.3.54", {"start": v(7.57, 4.07) * mm, "end": v(7.59, 4.07) * mm});
            skLineSegment(sketch, "E99.3.55", {"start": v(7.27, 4.48) * mm, "end": v(7.28, 4.5) * mm});
            skLineSegment(sketch, "E99.3.56", {"start": v(7.3, 4.52) * mm, "end": v(7.32, 4.53) * mm});
            skLineSegment(sketch, "E99.3.57", {"start": v(7.52, 4.06) * mm, "end": v(7.53, 4.06) * mm});
            skLineSegment(sketch, "E99.3.58", {"start": v(7.23, 4.42) * mm, "end": v(7.24, 4.44) * mm});
            skLineSegment(sketch, "E99.3.59", {"start": v(7.59, 4.07) * mm, "end": v(7.63, 4.08) * mm});
            skLineSegment(sketch, "E99.3.60", {"start": v(7.3, 4.5) * mm, "end": v(7.3, 4.52) * mm});
            skLineSegment(sketch, "E99.3.61", {"start": v(7.25, 4.45) * mm, "end": v(7.26, 4.47) * mm});
            skLineSegment(sketch, "E99.3.62", {"start": v(7.55, 4.06) * mm, "end": v(7.57, 4.07) * mm});
            skLineSegment(sketch, "E99.3.63", {"start": v(7.28, 4.5) * mm, "end": v(7.3, 4.5) * mm});
            skLineSegment(sketch, "E99.3.64", {"start": v(7.23, 4.4) * mm, "end": v(7.23, 4.42) * mm});
            skLineSegment(sketch, "E99.3.65", {"start": v(7.43, 4.05) * mm, "end": v(7.45, 4.05) * mm});
            skLineSegment(sketch, "E99.3.66", {"start": v(7.46, 4.05) * mm, "end": v(7.48, 4.05) * mm});
            skLineSegment(sketch, "E99.3.67", {"start": v(7.22, 4.4) * mm, "end": v(7.23, 4.4) * mm});
            skLineSegment(sketch, "E99.3.68", {"start": v(7.48, 4.05) * mm, "end": v(7.5, 4.05) * mm});
            skLineSegment(sketch, "E99.3.69", {"start": v(7.42, 4.06) * mm, "end": v(7.43, 4.05) * mm});
            skLineSegment(sketch, "E99.3.70", {"start": v(7.37, 4.07) * mm, "end": v(7.38, 4.07) * mm});
            skLineSegment(sketch, "E99.3.71", {"start": v(7.4, 4.06) * mm, "end": v(7.42, 4.06) * mm});
            skLineSegment(sketch, "E99.3.72", {"start": v(7.38, 4.07) * mm, "end": v(7.4, 4.06) * mm});
            skLineSegment(sketch, "E99.3.73", {"start": v(7.34, 4.09) * mm, "end": v(7.35, 4.08) * mm});
            skLineSegment(sketch, "E99.3.74", {"start": v(7.22, 4.38) * mm, "end": v(7.22, 4.4) * mm});
            skLineSegment(sketch, "E99.3.75", {"start": v(7.35, 4.08) * mm, "end": v(7.37, 4.07) * mm});
            skLineSegment(sketch, "E99.3.76", {"start": v(7.25, 4.19) * mm, "end": v(7.26, 4.18) * mm});
            skLineSegment(sketch, "E99.3.77", {"start": v(7.28, 4.14) * mm, "end": v(7.3, 4.12) * mm});
            skLineSegment(sketch, "E99.3.78", {"start": v(7.27, 4.16) * mm, "end": v(7.28, 4.14) * mm});
            skLineSegment(sketch, "E99.3.79", {"start": v(7.24, 4.21) * mm, "end": v(7.23, 4.24) * mm});
            skLineSegment(sketch, "E99.3.80", {"start": v(7.2, 4.31) * mm, "end": v(7.2, 4.33) * mm});
            skLineSegment(sketch, "E99.3.81", {"start": v(7.21, 4.35) * mm, "end": v(7.21, 4.36) * mm});
            skLineSegment(sketch, "E99.3.82", {"start": v(7.32, 4.1) * mm, "end": v(7.34, 4.09) * mm});
            skLineSegment(sketch, "E99.3.83", {"start": v(7.22, 4.26) * mm, "end": v(7.21, 4.28) * mm});
            skLineSegment(sketch, "E99.3.84", {"start": v(7.21, 4.36) * mm, "end": v(7.22, 4.38) * mm});
            skLineSegment(sketch, "E99.3.85", {"start": v(7.3, 4.12) * mm, "end": v(7.31, 4.1) * mm});
            skLineSegment(sketch, "E99.3.86", {"start": v(7.2, 4.33) * mm, "end": v(7.21, 4.35) * mm});
            skLineSegment(sketch, "E99.3.87", {"start": v(7.23, 4.24) * mm, "end": v(7.22, 4.26) * mm});
            skLineSegment(sketch, "E99.3.88", {"start": v(7.21, 4.3) * mm, "end": v(7.2, 4.31) * mm});
            skLineSegment(sketch, "E99.3.89", {"start": v(7.26, 4.18) * mm, "end": v(7.26, 4.17) * mm});
            skLineSegment(sketch, "E99.3.90", {"start": v(7.26, 4.17) * mm, "end": v(7.27, 4.16) * mm});
            skLineSegment(sketch, "E99.3.91", {"start": v(7.31, 4.1) * mm, "end": v(7.32, 4.1) * mm});
            skLineSegment(sketch, "E99.3.92", {"start": v(7.21, 4.28) * mm, "end": v(7.21, 4.3) * mm});
            skLineSegment(sketch, "E99.3.93", {"start": v(7.24, 4.2) * mm, "end": v(7.24, 4.21) * mm});
            skLineSegment(sketch, "E99.3.94", {"start": v(7.24, 4.2) * mm, "end": v(7.24, 4.2) * mm});
            skLineSegment(sketch, "E99.3.95", {"start": v(7.25, 4.2) * mm, "end": v(7.24, 4.2) * mm});
            skLineSegment(sketch, "E99.3.96", {"start": v(7.25, 4.2) * mm, "end": v(7.25, 4.2) * mm});
            skLineSegment(sketch, "E99.3.97", {"start": v(7.25, 4.19) * mm, "end": v(7.25, 4.2) * mm});
            skLineSegment(sketch, "E99.3.98", {"start": v(7.26, 4.17) * mm, "end": v(7.26, 4.17) * mm});
            skLineSegment(sketch, "E99.3.99", {"start": v(7.26, 4.18) * mm, "end": v(7.26, 4.18) * mm});
            skLineSegment(sketch, "E99.4.0", {"start": v(7.48, 5.57) * mm, "end": v(7.53, 5.58) * mm});
            skLineSegment(sketch, "E99.4.1", {"start": v(6.78, 6.4) * mm, "end": v(6.8, 6.44) * mm});
            skLineSegment(sketch, "E99.4.2", {"start": v(7.76, 5.48) * mm, "end": v(7.78, 5.45) * mm});
            skLineSegment(sketch, "E99.4.3", {"start": v(7.74, 5.51) * mm, "end": v(7.76, 5.48) * mm});
            skLineSegment(sketch, "E99.4.4", {"start": v(7.29, 5.52) * mm, "end": v(7.34, 5.53) * mm});
            skLineSegment(sketch, "E99.4.5", {"start": v(6.6, 6) * mm, "end": v(6.62, 6.05) * mm});
            skLineSegment(sketch, "E99.4.6", {"start": v(7.2, 5.5) * mm, "end": v(7.24, 5.5) * mm});
            skLineSegment(sketch, "E99.4.7", {"start": v(6.89, 5.39) * mm, "end": v(6.93, 5.4) * mm});
            skLineSegment(sketch, "E99.4.8", {"start": v(7.24, 5.5) * mm, "end": v(7.29, 5.52) * mm});
            skLineSegment(sketch, "E99.4.9", {"start": v(6.97, 5.42) * mm, "end": v(7.02, 5.44) * mm});
            skLineSegment(sketch, "E99.4.10", {"start": v(6.64, 6.1) * mm, "end": v(6.66, 6.13) * mm});
            skLineSegment(sketch, "E99.4.11", {"start": v(6.53, 5.89) * mm, "end": v(6.55, 5.93) * mm});
            skLineSegment(sketch, "E99.4.12", {"start": v(6.68, 6.18) * mm, "end": v(6.7, 6.22) * mm});
            skLineSegment(sketch, "E99.4.13", {"start": v(7.1, 5.47) * mm, "end": v(7.15, 5.48) * mm});
            skLineSegment(sketch, "E99.4.14", {"start": v(7.53, 5.58) * mm, "end": v(7.57, 5.59) * mm});
            skLineSegment(sketch, "E99.4.15", {"start": v(7.06, 5.45) * mm, "end": v(7.1, 5.47) * mm});
            skLineSegment(sketch, "E99.4.16", {"start": v(7.43, 5.56) * mm, "end": v(7.48, 5.57) * mm});
            skLineSegment(sketch, "E99.4.17", {"start": v(7.15, 5.48) * mm, "end": v(7.2, 5.5) * mm});
            skLineSegment(sketch, "E99.4.18", {"start": v(6.76, 6.35) * mm, "end": v(6.78, 6.4) * mm});
            skLineSegment(sketch, "E99.4.19", {"start": v(7.57, 5.59) * mm, "end": v(7.62, 5.6) * mm});
            skLineSegment(sketch, "E99.4.20", {"start": v(7.72, 5.54) * mm, "end": v(7.74, 5.51) * mm});
            skLineSegment(sketch, "E99.4.21", {"start": v(6.5, 5.85) * mm, "end": v(6.53, 5.89) * mm});
            skLineSegment(sketch, "E99.4.22", {"start": v(6.57, 5.97) * mm, "end": v(6.6, 6) * mm});
            skLineSegment(sketch, "E99.4.23", {"start": v(6.72, 6.26) * mm, "end": v(6.74, 6.3) * mm});
            skLineSegment(sketch, "E99.4.24", {"start": v(7.34, 5.53) * mm, "end": v(7.38, 5.55) * mm});
            skLineSegment(sketch, "E99.4.25", {"start": v(6.93, 5.4) * mm, "end": v(6.97, 5.42) * mm});
            skLineSegment(sketch, "E99.4.26", {"start": v(7.62, 5.6) * mm, "end": v(7.67, 5.6) * mm});
            skLineSegment(sketch, "E99.4.27", {"start": v(7.7, 5.57) * mm, "end": v(7.72, 5.54) * mm});
            skLineSegment(sketch, "E99.4.28", {"start": v(7.38, 5.55) * mm, "end": v(7.43, 5.56) * mm});
            skLineSegment(sketch, "E99.4.29", {"start": v(6.62, 6.05) * mm, "end": v(6.64, 6.1) * mm});
            skLineSegment(sketch, "E99.4.30", {"start": v(6.74, 6.3) * mm, "end": v(6.76, 6.35) * mm});
            skLineSegment(sketch, "E99.4.31", {"start": v(7.02, 5.44) * mm, "end": v(7.06, 5.45) * mm});
            skLineSegment(sketch, "E99.4.32", {"start": v(6.7, 6.22) * mm, "end": v(6.72, 6.26) * mm});
            skLineSegment(sketch, "E99.4.33", {"start": v(6.55, 5.93) * mm, "end": v(6.57, 5.97) * mm});
            skLineSegment(sketch, "E99.4.34", {"start": v(6.8, 6.44) * mm, "end": v(6.82, 6.49) * mm});
            skLineSegment(sketch, "E99.4.35", {"start": v(6.74, 6.7) * mm, "end": v(6.72, 6.72) * mm});
            skLineSegment(sketch, "E99.4.36", {"start": v(6.66, 6.13) * mm, "end": v(6.68, 6.18) * mm});
            skLineSegment(sketch, "E99.4.37", {"start": v(6.77, 6.66) * mm, "end": v(6.74, 6.7) * mm});
            skLineSegment(sketch, "E99.4.38", {"start": v(6.82, 6.49) * mm, "end": v(6.83, 6.54) * mm});
            skLineSegment(sketch, "E99.4.39", {"start": v(7.67, 5.6) * mm, "end": v(7.7, 5.57) * mm});
            skLineSegment(sketch, "E99.4.40", {"start": v(6.83, 6.54) * mm, "end": v(6.85, 6.58) * mm});
            skLineSegment(sketch, "E99.4.41", {"start": v(6.8, 6.64) * mm, "end": v(6.77, 6.66) * mm});
            skLineSegment(sketch, "E99.4.42", {"start": v(6.82, 6.61) * mm, "end": v(6.8, 6.64) * mm});
            skLineSegment(sketch, "E99.4.43", {"start": v(6.47, 5.81) * mm, "end": v(6.5, 5.85) * mm});
            skLineSegment(sketch, "E99.4.44", {"start": v(6.85, 6.58) * mm, "end": v(6.82, 6.61) * mm});
            skLineSegment(sketch, "E99.4.45", {"start": v(6.85, 5.37) * mm, "end": v(6.89, 5.39) * mm});
            skLineSegment(sketch, "E99.4.46", {"start": v(6.36, 5.63) * mm, "end": v(6.37, 5.64) * mm});
            skLineSegment(sketch, "E99.4.47", {"start": v(6.42, 5.74) * mm, "end": v(6.45, 5.77) * mm});
            skLineSegment(sketch, "E99.4.48", {"start": v(6.45, 5.77) * mm, "end": v(6.47, 5.81) * mm});
            skLineSegment(sketch, "E99.4.49", {"start": v(6.68, 5.3) * mm, "end": v(6.7, 5.3) * mm});
            skLineSegment(sketch, "E99.4.50", {"start": v(6.37, 5.66) * mm, "end": v(6.38, 5.68) * mm});
            skLineSegment(sketch, "E99.4.51", {"start": v(6.63, 5.28) * mm, "end": v(6.65, 5.29) * mm});
            skLineSegment(sketch, "E99.4.52", {"start": v(6.8, 5.35) * mm, "end": v(6.85, 5.37) * mm});
            skLineSegment(sketch, "E99.4.53", {"start": v(6.71, 5.3) * mm, "end": v(6.73, 5.31) * mm});
            skLineSegment(sketch, "E99.4.54", {"start": v(6.75, 5.32) * mm, "end": v(6.76, 5.33) * mm});
            skLineSegment(sketch, "E99.4.55", {"start": v(6.38, 5.68) * mm, "end": v(6.39, 5.7) * mm});
            skLineSegment(sketch, "E99.4.56", {"start": v(6.4, 5.72) * mm, "end": v(6.42, 5.74) * mm});
            skLineSegment(sketch, "E99.4.57", {"start": v(6.7, 5.3) * mm, "end": v(6.71, 5.3) * mm});
            skLineSegment(sketch, "E99.4.58", {"start": v(6.36, 5.61) * mm, "end": v(6.36, 5.63) * mm});
            skLineSegment(sketch, "E99.4.59", {"start": v(6.76, 5.33) * mm, "end": v(6.8, 5.35) * mm});
            skLineSegment(sketch, "E99.4.60", {"start": v(6.4, 5.7) * mm, "end": v(6.4, 5.72) * mm});
            skLineSegment(sketch, "E99.4.61", {"start": v(6.37, 5.64) * mm, "end": v(6.37, 5.66) * mm});
            skLineSegment(sketch, "E99.4.62", {"start": v(6.73, 5.31) * mm, "end": v(6.75, 5.32) * mm});
            skLineSegment(sketch, "E99.4.63", {"start": v(6.39, 5.7) * mm, "end": v(6.4, 5.7) * mm});
            skLineSegment(sketch, "E99.4.64", {"start": v(6.35, 5.6) * mm, "end": v(6.36, 5.61) * mm});
            skLineSegment(sketch, "E99.4.65", {"start": v(6.61, 5.28) * mm, "end": v(6.63, 5.28) * mm});
            skLineSegment(sketch, "E99.4.66", {"start": v(6.65, 5.29) * mm, "end": v(6.66, 5.29) * mm});
            skLineSegment(sketch, "E99.4.67", {"start": v(6.35, 5.58) * mm, "end": v(6.35, 5.6) * mm});
            skLineSegment(sketch, "E99.4.68", {"start": v(6.66, 5.29) * mm, "end": v(6.68, 5.3) * mm});
            skLineSegment(sketch, "E99.4.69", {"start": v(6.6, 5.28) * mm, "end": v(6.61, 5.28) * mm});
            skLineSegment(sketch, "E99.4.70", {"start": v(6.55, 5.29) * mm, "end": v(6.57, 5.29) * mm});
            skLineSegment(sketch, "E99.4.71", {"start": v(6.58, 5.28) * mm, "end": v(6.6, 5.28) * mm});
            skLineSegment(sketch, "E99.4.72", {"start": v(6.57, 5.29) * mm, "end": v(6.58, 5.28) * mm});
            skLineSegment(sketch, "E99.4.73", {"start": v(6.52, 5.3) * mm, "end": v(6.53, 5.3) * mm});
            skLineSegment(sketch, "E99.4.74", {"start": v(6.35, 5.56) * mm, "end": v(6.35, 5.58) * mm});
            skLineSegment(sketch, "E99.4.75", {"start": v(6.53, 5.3) * mm, "end": v(6.55, 5.29) * mm});
            skLineSegment(sketch, "E99.4.76", {"start": v(6.42, 5.38) * mm, "end": v(6.42, 5.38) * mm});
            skLineSegment(sketch, "E99.4.77", {"start": v(6.45, 5.34) * mm, "end": v(6.47, 5.33) * mm});
            skLineSegment(sketch, "E99.4.78", {"start": v(6.43, 5.36) * mm, "end": v(6.45, 5.34) * mm});
            skLineSegment(sketch, "E99.4.79", {"start": v(6.4, 5.4) * mm, "end": v(6.38, 5.43) * mm});
            skLineSegment(sketch, "E99.4.80", {"start": v(6.35, 5.5) * mm, "end": v(6.35, 5.52) * mm});
            skLineSegment(sketch, "E99.4.81", {"start": v(6.35, 5.53) * mm, "end": v(6.35, 5.55) * mm});
            skLineSegment(sketch, "E99.4.82", {"start": v(6.5, 5.3) * mm, "end": v(6.52, 5.3) * mm});
            skLineSegment(sketch, "E99.4.83", {"start": v(6.37, 5.45) * mm, "end": v(6.36, 5.46) * mm});
            skLineSegment(sketch, "E99.4.84", {"start": v(6.35, 5.55) * mm, "end": v(6.35, 5.56) * mm});
            skLineSegment(sketch, "E99.4.85", {"start": v(6.47, 5.33) * mm, "end": v(6.49, 5.32) * mm});
            skLineSegment(sketch, "E99.4.86", {"start": v(6.35, 5.52) * mm, "end": v(6.35, 5.53) * mm});
            skLineSegment(sketch, "E99.4.87", {"start": v(6.38, 5.43) * mm, "end": v(6.37, 5.45) * mm});
            skLineSegment(sketch, "E99.4.88", {"start": v(6.36, 5.48) * mm, "end": v(6.35, 5.5) * mm});
            skLineSegment(sketch, "E99.4.89", {"start": v(6.42, 5.37) * mm, "end": v(6.43, 5.37) * mm});
            skLineSegment(sketch, "E99.4.90", {"start": v(6.43, 5.36) * mm, "end": v(6.43, 5.36) * mm});
            skLineSegment(sketch, "E99.4.91", {"start": v(6.49, 5.32) * mm, "end": v(6.5, 5.3) * mm});
            skLineSegment(sketch, "E99.4.92", {"start": v(6.36, 5.46) * mm, "end": v(6.36, 5.48) * mm});
            skLineSegment(sketch, "E99.4.93", {"start": v(6.4, 5.4) * mm, "end": v(6.4, 5.4) * mm});
            skLineSegment(sketch, "E99.4.94", {"start": v(6.4, 5.4) * mm, "end": v(6.4, 5.4) * mm});
            skLineSegment(sketch, "E99.4.95", {"start": v(6.4, 5.4) * mm, "end": v(6.4, 5.4) * mm});
            skLineSegment(sketch, "E99.4.96", {"start": v(6.41, 5.39) * mm, "end": v(6.4, 5.4) * mm});
            skLineSegment(sketch, "E99.4.97", {"start": v(6.42, 5.38) * mm, "end": v(6.41, 5.39) * mm});
            skLineSegment(sketch, "E99.4.98", {"start": v(6.43, 5.37) * mm, "end": v(6.43, 5.36) * mm});
            skLineSegment(sketch, "E99.4.99", {"start": v(6.42, 5.38) * mm, "end": v(6.42, 5.37) * mm});
            skLineSegment(sketch, "E99.5.0", {"start": v(6.4, 6.78) * mm, "end": v(6.44, 6.8) * mm});
            skLineSegment(sketch, "E99.5.1", {"start": v(5.57, 7.48) * mm, "end": v(5.58, 7.53) * mm});
            skLineSegment(sketch, "E99.5.2", {"start": v(6.7, 6.74) * mm, "end": v(6.72, 6.72) * mm});
            skLineSegment(sketch, "E99.5.3", {"start": v(6.66, 6.77) * mm, "end": v(6.7, 6.74) * mm});
            skLineSegment(sketch, "E99.5.4", {"start": v(6.22, 6.7) * mm, "end": v(6.26, 6.72) * mm});
            skLineSegment(sketch, "E99.5.5", {"start": v(5.45, 7.06) * mm, "end": v(5.47, 7.1) * mm});
            skLineSegment(sketch, "E99.5.6", {"start": v(6.13, 6.66) * mm, "end": v(6.18, 6.68) * mm});
            skLineSegment(sketch, "E99.5.7", {"start": v(5.85, 6.5) * mm, "end": v(5.89, 6.53) * mm});
            skLineSegment(sketch, "E99.5.8", {"start": v(6.18, 6.68) * mm, "end": v(6.22, 6.7) * mm});
            skLineSegment(sketch, "E99.5.9", {"start": v(5.93, 6.55) * mm, "end": v(5.97, 6.57) * mm});
            skLineSegment(sketch, "E99.5.10", {"start": v(5.48, 7.15) * mm, "end": v(5.5, 7.2) * mm});
            skLineSegment(sketch, "E99.5.11", {"start": v(5.4, 6.93) * mm, "end": v(5.42, 6.97) * mm});
            skLineSegment(sketch, "E99.5.12", {"start": v(5.5, 7.24) * mm, "end": v(5.52, 7.29) * mm});
            skLineSegment(sketch, "E99.5.13", {"start": v(6.05, 6.62) * mm, "end": v(6.1, 6.64) * mm});
            skLineSegment(sketch, "E99.5.14", {"start": v(6.44, 6.8) * mm, "end": v(6.49, 6.82) * mm});
            skLineSegment(sketch, "E99.5.15", {"start": v(6, 6.6) * mm, "end": v(6.05, 6.62) * mm});
            skLineSegment(sketch, "E99.5.16", {"start": v(6.35, 6.76) * mm, "end": v(6.4, 6.78) * mm});
            skLineSegment(sketch, "E99.5.17", {"start": v(6.1, 6.64) * mm, "end": v(6.13, 6.66) * mm});
            skLineSegment(sketch, "E99.5.18", {"start": v(5.56, 7.43) * mm, "end": v(5.57, 7.48) * mm});
            skLineSegment(sketch, "E99.5.19", {"start": v(6.49, 6.82) * mm, "end": v(6.54, 6.83) * mm});
            skLineSegment(sketch, "E99.5.20", {"start": v(6.64, 6.8) * mm, "end": v(6.66, 6.77) * mm});
            skLineSegment(sketch, "E99.5.21", {"start": v(5.39, 6.89) * mm, "end": v(5.4, 6.93) * mm});
            skLineSegment(sketch, "E99.5.22", {"start": v(5.44, 7.02) * mm, "end": v(5.45, 7.06) * mm});
            skLineSegment(sketch, "E99.5.23", {"start": v(5.53, 7.34) * mm, "end": v(5.55, 7.38) * mm});
            skLineSegment(sketch, "E99.5.24", {"start": v(6.26, 6.72) * mm, "end": v(6.3, 6.74) * mm});
            skLineSegment(sketch, "E99.5.25", {"start": v(5.89, 6.53) * mm, "end": v(5.93, 6.55) * mm});
            skLineSegment(sketch, "E99.5.26", {"start": v(6.54, 6.83) * mm, "end": v(6.58, 6.85) * mm});
            skLineSegment(sketch, "E99.5.27", {"start": v(6.61, 6.82) * mm, "end": v(6.64, 6.8) * mm});
            skLineSegment(sketch, "E99.5.28", {"start": v(6.3, 6.74) * mm, "end": v(6.35, 6.76) * mm});
            skLineSegment(sketch, "E99.5.29", {"start": v(5.47, 7.1) * mm, "end": v(5.48, 7.15) * mm});
            skLineSegment(sketch, "E99.5.30", {"start": v(5.55, 7.38) * mm, "end": v(5.56, 7.43) * mm});
            skLineSegment(sketch, "E99.5.31", {"start": v(5.97, 6.57) * mm, "end": v(6, 6.6) * mm});
            skLineSegment(sketch, "E99.5.32", {"start": v(5.52, 7.29) * mm, "end": v(5.53, 7.34) * mm});
            skLineSegment(sketch, "E99.5.33", {"start": v(5.42, 6.97) * mm, "end": v(5.44, 7.02) * mm});
            skLineSegment(sketch, "E99.5.34", {"start": v(5.58, 7.53) * mm, "end": v(5.59, 7.57) * mm});
            skLineSegment(sketch, "E99.5.35", {"start": v(5.48, 7.76) * mm, "end": v(5.45, 7.78) * mm});
            skLineSegment(sketch, "E99.5.36", {"start": v(5.5, 7.2) * mm, "end": v(5.5, 7.24) * mm});
            skLineSegment(sketch, "E99.5.37", {"start": v(5.51, 7.74) * mm, "end": v(5.48, 7.76) * mm});
            skLineSegment(sketch, "E99.5.38", {"start": v(5.59, 7.57) * mm, "end": v(5.6, 7.62) * mm});
            skLineSegment(sketch, "E99.5.39", {"start": v(6.58, 6.85) * mm, "end": v(6.61, 6.82) * mm});
            skLineSegment(sketch, "E99.5.40", {"start": v(5.6, 7.62) * mm, "end": v(5.6, 7.67) * mm});
            skLineSegment(sketch, "E99.5.41", {"start": v(5.54, 7.72) * mm, "end": v(5.51, 7.74) * mm});
            skLineSegment(sketch, "E99.5.42", {"start": v(5.57, 7.7) * mm, "end": v(5.54, 7.72) * mm});
            skLineSegment(sketch, "E99.5.43", {"start": v(5.37, 6.85) * mm, "end": v(5.39, 6.89) * mm});
            skLineSegment(sketch, "E99.5.44", {"start": v(5.6, 7.67) * mm, "end": v(5.57, 7.7) * mm});
            skLineSegment(sketch, "E99.5.45", {"start": v(5.81, 6.47) * mm, "end": v(5.85, 6.5) * mm});
            skLineSegment(sketch, "E99.5.46", {"start": v(5.29, 6.65) * mm, "end": v(5.29, 6.66) * mm});
            skLineSegment(sketch, "E99.5.47", {"start": v(5.33, 6.76) * mm, "end": v(5.35, 6.8) * mm});
            skLineSegment(sketch, "E99.5.48", {"start": v(5.35, 6.8) * mm, "end": v(5.37, 6.85) * mm});
            skLineSegment(sketch, "E99.5.49", {"start": v(5.66, 6.37) * mm, "end": v(5.68, 6.38) * mm});
            skLineSegment(sketch, "E99.5.50", {"start": v(5.3, 6.68) * mm, "end": v(5.3, 6.7) * mm});
            skLineSegment(sketch, "E99.5.51", {"start": v(5.61, 6.36) * mm, "end": v(5.63, 6.36) * mm});
            skLineSegment(sketch, "E99.5.52", {"start": v(5.77, 6.45) * mm, "end": v(5.81, 6.47) * mm});
            skLineSegment(sketch, "E99.5.53", {"start": v(5.7, 6.39) * mm, "end": v(5.7, 6.4) * mm});
            skLineSegment(sketch, "E99.5.54", {"start": v(5.72, 6.4) * mm, "end": v(5.74, 6.42) * mm});
            skLineSegment(sketch, "E99.5.55", {"start": v(5.3, 6.7) * mm, "end": v(5.3, 6.71) * mm});
            skLineSegment(sketch, "E99.5.56", {"start": v(5.32, 6.75) * mm, "end": v(5.33, 6.76) * mm});
            skLineSegment(sketch, "E99.5.57", {"start": v(5.68, 6.38) * mm, "end": v(5.7, 6.39) * mm});
            skLineSegment(sketch, "E99.5.58", {"start": v(5.28, 6.63) * mm, "end": v(5.29, 6.65) * mm});
            skLineSegment(sketch, "E99.5.59", {"start": v(5.74, 6.42) * mm, "end": v(5.77, 6.45) * mm});
            skLineSegment(sketch, "E99.5.60", {"start": v(5.31, 6.73) * mm, "end": v(5.32, 6.75) * mm});
            skLineSegment(sketch, "E99.5.61", {"start": v(5.29, 6.66) * mm, "end": v(5.3, 6.68) * mm});
            skLineSegment(sketch, "E99.5.62", {"start": v(5.7, 6.4) * mm, "end": v(5.72, 6.4) * mm});
            skLineSegment(sketch, "E99.5.63", {"start": v(5.3, 6.71) * mm, "end": v(5.31, 6.73) * mm});
            skLineSegment(sketch, "E99.5.64", {"start": v(5.28, 6.61) * mm, "end": v(5.28, 6.63) * mm});
            skLineSegment(sketch, "E99.5.65", {"start": v(5.6, 6.35) * mm, "end": v(5.61, 6.36) * mm});
            skLineSegment(sketch, "E99.5.66", {"start": v(5.63, 6.36) * mm, "end": v(5.64, 6.37) * mm});
            skLineSegment(sketch, "E99.5.67", {"start": v(5.28, 6.6) * mm, "end": v(5.28, 6.61) * mm});
            skLineSegment(sketch, "E99.5.68", {"start": v(5.64, 6.37) * mm, "end": v(5.66, 6.37) * mm});
            skLineSegment(sketch, "E99.5.69", {"start": v(5.58, 6.35) * mm, "end": v(5.6, 6.35) * mm});
            skLineSegment(sketch, "E99.5.70", {"start": v(5.53, 6.35) * mm, "end": v(5.55, 6.35) * mm});
            skLineSegment(sketch, "E99.5.71", {"start": v(5.56, 6.35) * mm, "end": v(5.58, 6.35) * mm});
            skLineSegment(sketch, "E99.5.72", {"start": v(5.55, 6.35) * mm, "end": v(5.56, 6.35) * mm});
            skLineSegment(sketch, "E99.5.73", {"start": v(5.5, 6.35) * mm, "end": v(5.52, 6.35) * mm});
            skLineSegment(sketch, "E99.5.74", {"start": v(5.28, 6.58) * mm, "end": v(5.28, 6.6) * mm});
            skLineSegment(sketch, "E99.5.75", {"start": v(5.52, 6.35) * mm, "end": v(5.53, 6.35) * mm});
            skLineSegment(sketch, "E99.5.76", {"start": v(5.38, 6.42) * mm, "end": v(5.39, 6.41) * mm});
            skLineSegment(sketch, "E99.5.77", {"start": v(5.43, 6.38) * mm, "end": v(5.45, 6.37) * mm});
            skLineSegment(sketch, "E99.5.78", {"start": v(5.4, 6.4) * mm, "end": v(5.43, 6.38) * mm});
            skLineSegment(sketch, "E99.5.79", {"start": v(5.36, 6.43) * mm, "end": v(5.34, 6.45) * mm});
            skLineSegment(sketch, "E99.5.80", {"start": v(5.3, 6.52) * mm, "end": v(5.3, 6.53) * mm});
            skLineSegment(sketch, "E99.5.81", {"start": v(5.29, 6.55) * mm, "end": v(5.29, 6.57) * mm});
            skLineSegment(sketch, "E99.5.82", {"start": v(5.48, 6.36) * mm, "end": v(5.5, 6.35) * mm});
            skLineSegment(sketch, "E99.5.83", {"start": v(5.33, 6.47) * mm, "end": v(5.32, 6.49) * mm});
            skLineSegment(sketch, "E99.5.84", {"start": v(5.29, 6.57) * mm, "end": v(5.28, 6.58) * mm});
            skLineSegment(sketch, "E99.5.85", {"start": v(5.45, 6.37) * mm, "end": v(5.46, 6.36) * mm});
            skLineSegment(sketch, "E99.5.86", {"start": v(5.3, 6.53) * mm, "end": v(5.29, 6.55) * mm});
            skLineSegment(sketch, "E99.5.87", {"start": v(5.34, 6.45) * mm, "end": v(5.33, 6.47) * mm});
            skLineSegment(sketch, "E99.5.88", {"start": v(5.3, 6.5) * mm, "end": v(5.3, 6.52) * mm});
            skLineSegment(sketch, "E99.5.89", {"start": v(5.4, 6.4) * mm, "end": v(5.4, 6.4) * mm});
            skLineSegment(sketch, "E99.5.90", {"start": v(5.4, 6.4) * mm, "end": v(5.4, 6.4) * mm});
            skLineSegment(sketch, "E99.5.91", {"start": v(5.46, 6.36) * mm, "end": v(5.48, 6.36) * mm});
            skLineSegment(sketch, "E99.5.92", {"start": v(5.32, 6.49) * mm, "end": v(5.3, 6.5) * mm});
            skLineSegment(sketch, "E99.5.93", {"start": v(5.36, 6.43) * mm, "end": v(5.36, 6.43) * mm});
            skLineSegment(sketch, "E99.5.94", {"start": v(5.37, 6.43) * mm, "end": v(5.36, 6.43) * mm});
            skLineSegment(sketch, "E99.5.95", {"start": v(5.37, 6.42) * mm, "end": v(5.37, 6.43) * mm});
            skLineSegment(sketch, "E99.5.96", {"start": v(5.38, 6.42) * mm, "end": v(5.37, 6.42) * mm});
            skLineSegment(sketch, "E99.5.97", {"start": v(5.38, 6.42) * mm, "end": v(5.38, 6.42) * mm});
            skLineSegment(sketch, "E99.5.98", {"start": v(5.4, 6.4) * mm, "end": v(5.4, 6.4) * mm});
            skLineSegment(sketch, "E99.5.99", {"start": v(5.39, 6.41) * mm, "end": v(5.4, 6.4) * mm});
            skLineSegment(sketch, "E99.6.0", {"start": v(5.12, 7.79) * mm, "end": v(5.16, 7.81) * mm});
            skLineSegment(sketch, "E99.6.1", {"start": v(4.18, 8.33) * mm, "end": v(4.18, 8.38) * mm});
            skLineSegment(sketch, "E99.6.2", {"start": v(5.42, 7.8) * mm, "end": v(5.45, 7.78) * mm});
            skLineSegment(sketch, "E99.6.3", {"start": v(5.39, 7.82) * mm, "end": v(5.42, 7.8) * mm});
            skLineSegment(sketch, "E99.6.4", {"start": v(4.96, 7.68) * mm, "end": v(5, 7.7) * mm});
            skLineSegment(sketch, "E99.6.5", {"start": v(4.14, 7.9) * mm, "end": v(4.15, 7.95) * mm});
            skLineSegment(sketch, "E99.6.6", {"start": v(4.88, 7.63) * mm, "end": v(4.92, 7.65) * mm});
            skLineSegment(sketch, "E99.6.7", {"start": v(4.63, 7.42) * mm, "end": v(4.66, 7.45) * mm});
            skLineSegment(sketch, "E99.6.8", {"start": v(4.92, 7.65) * mm, "end": v(4.96, 7.68) * mm});
            skLineSegment(sketch, "E99.6.9", {"start": v(4.7, 7.48) * mm, "end": v(4.73, 7.5) * mm});
            skLineSegment(sketch, "E99.6.10", {"start": v(4.16, 8) * mm, "end": v(4.16, 8.04) * mm});
            skLineSegment(sketch, "E99.6.11", {"start": v(4.12, 7.76) * mm, "end": v(4.13, 7.8) * mm});
            skLineSegment(sketch, "E99.6.12", {"start": v(4.17, 8.09) * mm, "end": v(4.17, 8.14) * mm});
            skLineSegment(sketch, "E99.6.13", {"start": v(4.8, 7.57) * mm, "end": v(4.84, 7.6) * mm});
            skLineSegment(sketch, "E99.6.14", {"start": v(5.16, 7.81) * mm, "end": v(5.2, 7.84) * mm});
            skLineSegment(sketch, "E99.6.15", {"start": v(4.77, 7.54) * mm, "end": v(4.8, 7.57) * mm});
            skLineSegment(sketch, "E99.6.16", {"start": v(5.08, 7.76) * mm, "end": v(5.12, 7.79) * mm});
            skLineSegment(sketch, "E99.6.17", {"start": v(4.84, 7.6) * mm, "end": v(4.88, 7.63) * mm});
            skLineSegment(sketch, "E99.6.18", {"start": v(4.18, 8.28) * mm, "end": v(4.18, 8.33) * mm});
            skLineSegment(sketch, "E99.6.19", {"start": v(5.2, 7.84) * mm, "end": v(5.25, 7.86) * mm});
            skLineSegment(sketch, "E99.6.20", {"start": v(5.36, 7.85) * mm, "end": v(5.39, 7.82) * mm});
            skLineSegment(sketch, "E99.6.21", {"start": v(4.1, 7.72) * mm, "end": v(4.12, 7.76) * mm});
            skLineSegment(sketch, "E99.6.22", {"start": v(4.14, 7.85) * mm, "end": v(4.14, 7.9) * mm});
            skLineSegment(sketch, "E99.6.23", {"start": v(4.18, 8.18) * mm, "end": v(4.18, 8.23) * mm});
            skLineSegment(sketch, "E99.6.24", {"start": v(5, 7.7) * mm, "end": v(5.04, 7.74) * mm});
            skLineSegment(sketch, "E99.6.25", {"start": v(4.66, 7.45) * mm, "end": v(4.7, 7.48) * mm});
            skLineSegment(sketch, "E99.6.26", {"start": v(5.25, 7.86) * mm, "end": v(5.3, 7.89) * mm});
            skLineSegment(sketch, "E99.6.27", {"start": v(5.32, 7.87) * mm, "end": v(5.36, 7.85) * mm});
            skLineSegment(sketch, "E99.6.28", {"start": v(5.04, 7.74) * mm, "end": v(5.08, 7.76) * mm});
            skLineSegment(sketch, "E99.6.29", {"start": v(4.15, 7.95) * mm, "end": v(4.16, 8) * mm});
            skLineSegment(sketch, "E99.6.30", {"start": v(4.18, 8.23) * mm, "end": v(4.18, 8.28) * mm});
            skLineSegment(sketch, "E99.6.31", {"start": v(4.73, 7.5) * mm, "end": v(4.77, 7.54) * mm});
            skLineSegment(sketch, "E99.6.32", {"start": v(4.17, 8.14) * mm, "end": v(4.18, 8.18) * mm});
            skLineSegment(sketch, "E99.6.33", {"start": v(4.13, 7.8) * mm, "end": v(4.14, 7.85) * mm});
            skLineSegment(sketch, "E99.6.34", {"start": v(4.18, 8.38) * mm, "end": v(4.19, 8.43) * mm});
            skLineSegment(sketch, "E99.6.35", {"start": v(4.05, 8.6) * mm, "end": v(4.01, 8.6) * mm});
            skLineSegment(sketch, "E99.6.36", {"start": v(4.16, 8.04) * mm, "end": v(4.17, 8.09) * mm});
            skLineSegment(sketch, "E99.6.37", {"start": v(4.08, 8.58) * mm, "end": v(4.05, 8.6) * mm});
            skLineSegment(sketch, "E99.6.38", {"start": v(4.19, 8.43) * mm, "end": v(4.19, 8.48) * mm});
            skLineSegment(sketch, "E99.6.39", {"start": v(5.3, 7.89) * mm, "end": v(5.32, 7.87) * mm});
            skLineSegment(sketch, "E99.6.40", {"start": v(4.19, 8.48) * mm, "end": v(4.18, 8.53) * mm});
            skLineSegment(sketch, "E99.6.41", {"start": v(4.12, 8.56) * mm, "end": v(4.08, 8.58) * mm});
            skLineSegment(sketch, "E99.6.42", {"start": v(4.15, 8.55) * mm, "end": v(4.12, 8.56) * mm});
            skLineSegment(sketch, "E99.6.43", {"start": v(4.1, 7.67) * mm, "end": v(4.1, 7.72) * mm});
            skLineSegment(sketch, "E99.6.44", {"start": v(4.18, 8.53) * mm, "end": v(4.15, 8.55) * mm});
            skLineSegment(sketch, "E99.6.45", {"start": v(4.6, 7.39) * mm, "end": v(4.63, 7.42) * mm});
            skLineSegment(sketch, "E99.6.46", {"start": v(4.05, 7.46) * mm, "end": v(4.05, 7.48) * mm});
            skLineSegment(sketch, "E99.6.47", {"start": v(4.07, 7.59) * mm, "end": v(4.08, 7.63) * mm});
            skLineSegment(sketch, "E99.6.48", {"start": v(4.08, 7.63) * mm, "end": v(4.1, 7.67) * mm});
            skLineSegment(sketch, "E99.6.49", {"start": v(4.47, 7.26) * mm, "end": v(4.48, 7.27) * mm});
            skLineSegment(sketch, "E99.6.50", {"start": v(4.05, 7.5) * mm, "end": v(4.06, 7.52) * mm});
            skLineSegment(sketch, "E99.6.51", {"start": v(4.42, 7.23) * mm, "end": v(4.44, 7.24) * mm});
            skLineSegment(sketch, "E99.6.52", {"start": v(4.57, 7.35) * mm, "end": v(4.6, 7.39) * mm});
            skLineSegment(sketch, "E99.6.53", {"start": v(4.5, 7.28) * mm, "end": v(4.5, 7.3) * mm});
            skLineSegment(sketch, "E99.6.54", {"start": v(4.52, 7.3) * mm, "end": v(4.53, 7.32) * mm});
            skLineSegment(sketch, "E99.6.55", {"start": v(4.06, 7.52) * mm, "end": v(4.06, 7.53) * mm});
            skLineSegment(sketch, "E99.6.56", {"start": v(4.07, 7.57) * mm, "end": v(4.07, 7.59) * mm});
            skLineSegment(sketch, "E99.6.57", {"start": v(4.48, 7.27) * mm, "end": v(4.5, 7.28) * mm});
            skLineSegment(sketch, "E99.6.58", {"start": v(4.05, 7.45) * mm, "end": v(4.05, 7.46) * mm});
            skLineSegment(sketch, "E99.6.59", {"start": v(4.53, 7.32) * mm, "end": v(4.57, 7.35) * mm});
            skLineSegment(sketch, "E99.6.60", {"start": v(4.06, 7.55) * mm, "end": v(4.07, 7.57) * mm});
            skLineSegment(sketch, "E99.6.61", {"start": v(4.05, 7.48) * mm, "end": v(4.05, 7.5) * mm});
            skLineSegment(sketch, "E99.6.62", {"start": v(4.5, 7.3) * mm, "end": v(4.52, 7.3) * mm});
            skLineSegment(sketch, "E99.6.63", {"start": v(4.06, 7.53) * mm, "end": v(4.06, 7.55) * mm});
            skLineSegment(sketch, "E99.6.64", {"start": v(4.05, 7.43) * mm, "end": v(4.05, 7.45) * mm});
            skLineSegment(sketch, "E99.6.65", {"start": v(4.4, 7.23) * mm, "end": v(4.42, 7.23) * mm});
            skLineSegment(sketch, "E99.6.66", {"start": v(4.44, 7.24) * mm, "end": v(4.45, 7.25) * mm});
            skLineSegment(sketch, "E99.6.67", {"start": v(4.06, 7.42) * mm, "end": v(4.05, 7.43) * mm});
            skLineSegment(sketch, "E99.6.68", {"start": v(4.45, 7.25) * mm, "end": v(4.47, 7.26) * mm});
            skLineSegment(sketch, "E99.6.69", {"start": v(4.4, 7.22) * mm, "end": v(4.4, 7.23) * mm});
            skLineSegment(sketch, "E99.6.70", {"start": v(4.35, 7.21) * mm, "end": v(4.36, 7.21) * mm});
            skLineSegment(sketch, "E99.6.71", {"start": v(4.38, 7.22) * mm, "end": v(4.4, 7.22) * mm});
            skLineSegment(sketch, "E99.6.72", {"start": v(4.36, 7.21) * mm, "end": v(4.38, 7.22) * mm});
            skLineSegment(sketch, "E99.6.73", {"start": v(4.31, 7.2) * mm, "end": v(4.33, 7.2) * mm});
            skLineSegment(sketch, "E99.6.74", {"start": v(4.06, 7.4) * mm, "end": v(4.06, 7.42) * mm});
            skLineSegment(sketch, "E99.6.75", {"start": v(4.33, 7.2) * mm, "end": v(4.35, 7.21) * mm});
            skLineSegment(sketch, "E99.6.76", {"start": v(4.19, 7.25) * mm, "end": v(4.2, 7.25) * mm});
            skLineSegment(sketch, "E99.6.77", {"start": v(4.24, 7.23) * mm, "end": v(4.26, 7.22) * mm});
            skLineSegment(sketch, "E99.6.78", {"start": v(4.21, 7.24) * mm, "end": v(4.24, 7.23) * mm});
            skLineSegment(sketch, "E99.6.79", {"start": v(4.16, 7.27) * mm, "end": v(4.14, 7.28) * mm});
            skLineSegment(sketch, "E99.6.80", {"start": v(4.09, 7.34) * mm, "end": v(4.08, 7.35) * mm});
            skLineSegment(sketch, "E99.6.81", {"start": v(4.07, 7.37) * mm, "end": v(4.07, 7.38) * mm});
            skLineSegment(sketch, "E99.6.82", {"start": v(4.3, 7.21) * mm, "end": v(4.31, 7.2) * mm});
            skLineSegment(sketch, "E99.6.83", {"start": v(4.12, 7.3) * mm, "end": v(4.1, 7.31) * mm});
            skLineSegment(sketch, "E99.6.84", {"start": v(4.07, 7.38) * mm, "end": v(4.06, 7.4) * mm});
            skLineSegment(sketch, "E99.6.85", {"start": v(4.26, 7.22) * mm, "end": v(4.28, 7.21) * mm});
            skLineSegment(sketch, "E99.6.86", {"start": v(4.08, 7.35) * mm, "end": v(4.07, 7.37) * mm});
            skLineSegment(sketch, "E99.6.87", {"start": v(4.14, 7.28) * mm, "end": v(4.12, 7.3) * mm});
            skLineSegment(sketch, "E99.6.88", {"start": v(4.1, 7.32) * mm, "end": v(4.09, 7.34) * mm});
            skLineSegment(sketch, "E99.6.89", {"start": v(4.2, 7.25) * mm, "end": v(4.2, 7.24) * mm});
            skLineSegment(sketch, "E99.6.90", {"start": v(4.2, 7.24) * mm, "end": v(4.21, 7.24) * mm});
            skLineSegment(sketch, "E99.6.91", {"start": v(4.28, 7.21) * mm, "end": v(4.3, 7.21) * mm});
            skLineSegment(sketch, "E99.6.92", {"start": v(4.1, 7.31) * mm, "end": v(4.1, 7.32) * mm});
            skLineSegment(sketch, "E99.6.93", {"start": v(4.17, 7.26) * mm, "end": v(4.16, 7.27) * mm});
            skLineSegment(sketch, "E99.6.94", {"start": v(4.17, 7.26) * mm, "end": v(4.17, 7.26) * mm});
            skLineSegment(sketch, "E99.6.95", {"start": v(4.18, 7.26) * mm, "end": v(4.17, 7.26) * mm});
            skLineSegment(sketch, "E99.6.96", {"start": v(4.18, 7.26) * mm, "end": v(4.18, 7.26) * mm});
            skLineSegment(sketch, "E99.6.97", {"start": v(4.19, 7.25) * mm, "end": v(4.18, 7.26) * mm});
            skLineSegment(sketch, "E99.6.98", {"start": v(4.2, 7.24) * mm, "end": v(4.2, 7.24) * mm});
            skLineSegment(sketch, "E99.6.99", {"start": v(4.2, 7.25) * mm, "end": v(4.2, 7.25) * mm});
            skLineSegment(sketch, "E99.7.0", {"start": v(3.7, 8.56) * mm, "end": v(3.73, 8.6) * mm});
            skLineSegment(sketch, "E99.7.1", {"start": v(2.67, 8.93) * mm, "end": v(2.67, 8.98) * mm});
            skLineSegment(sketch, "E99.7.2", {"start": v(3.98, 8.63) * mm, "end": v(4.01, 8.6) * mm});
            skLineSegment(sketch, "E99.7.3", {"start": v(3.95, 8.64) * mm, "end": v(3.98, 8.63) * mm});
            skLineSegment(sketch, "E99.7.4", {"start": v(3.55, 8.43) * mm, "end": v(3.59, 8.46) * mm});
            skLineSegment(sketch, "E99.7.5", {"start": v(2.7, 8.5) * mm, "end": v(2.7, 8.55) * mm});
            skLineSegment(sketch, "E99.7.6", {"start": v(3.48, 8.36) * mm, "end": v(3.52, 8.4) * mm});
            skLineSegment(sketch, "E99.7.7", {"start": v(3.27, 8.1) * mm, "end": v(3.3, 8.15) * mm});
            skLineSegment(sketch, "E99.7.8", {"start": v(3.52, 8.4) * mm, "end": v(3.55, 8.43) * mm});
            skLineSegment(sketch, "E99.7.9", {"start": v(3.33, 8.18) * mm, "end": v(3.36, 8.22) * mm});
            skLineSegment(sketch, "E99.7.10", {"start": v(2.7, 8.6) * mm, "end": v(2.7, 8.64) * mm});
            skLineSegment(sketch, "E99.7.11", {"start": v(2.7, 8.36) * mm, "end": v(2.7, 8.4) * mm});
            skLineSegment(sketch, "E99.7.12", {"start": v(2.7, 8.69) * mm, "end": v(2.7, 8.74) * mm});
            skLineSegment(sketch, "E99.7.13", {"start": v(3.42, 8.29) * mm, "end": v(3.45, 8.32) * mm});
            skLineSegment(sketch, "E99.7.14", {"start": v(3.73, 8.6) * mm, "end": v(3.77, 8.62) * mm});
            skLineSegment(sketch, "E99.7.15", {"start": v(3.39, 8.25) * mm, "end": v(3.42, 8.29) * mm});
            skLineSegment(sketch, "E99.7.16", {"start": v(3.66, 8.53) * mm, "end": v(3.7, 8.56) * mm});
            skLineSegment(sketch, "E99.7.17", {"start": v(3.45, 8.32) * mm, "end": v(3.48, 8.36) * mm});
            skLineSegment(sketch, "E99.7.18", {"start": v(2.68, 8.88) * mm, "end": v(2.67, 8.93) * mm});
            skLineSegment(sketch, "E99.7.19", {"start": v(3.77, 8.62) * mm, "end": v(3.8, 8.66) * mm});
            skLineSegment(sketch, "E99.7.20", {"start": v(3.91, 8.66) * mm, "end": v(3.95, 8.64) * mm});
            skLineSegment(sketch, "E99.7.21", {"start": v(2.7, 8.31) * mm, "end": v(2.7, 8.36) * mm});
            skLineSegment(sketch, "E99.7.22", {"start": v(2.7, 8.45) * mm, "end": v(2.7, 8.5) * mm});
            skLineSegment(sketch, "E99.7.23", {"start": v(2.7, 8.79) * mm, "end": v(2.69, 8.83) * mm});
            skLineSegment(sketch, "E99.7.24", {"start": v(3.59, 8.46) * mm, "end": v(3.62, 8.5) * mm});
            skLineSegment(sketch, "E99.7.25", {"start": v(3.3, 8.15) * mm, "end": v(3.33, 8.18) * mm});
            skLineSegment(sketch, "E99.7.26", {"start": v(3.8, 8.66) * mm, "end": v(3.84, 8.69) * mm});
            skLineSegment(sketch, "E99.7.27", {"start": v(3.88, 8.67) * mm, "end": v(3.91, 8.66) * mm});
            skLineSegment(sketch, "E99.7.28", {"start": v(3.62, 8.5) * mm, "end": v(3.66, 8.53) * mm});
            skLineSegment(sketch, "E99.7.29", {"start": v(2.7, 8.55) * mm, "end": v(2.7, 8.6) * mm});
            skLineSegment(sketch, "E99.7.30", {"start": v(2.69, 8.83) * mm, "end": v(2.68, 8.88) * mm});
            skLineSegment(sketch, "E99.7.31", {"start": v(3.36, 8.22) * mm, "end": v(3.39, 8.25) * mm});
            skLineSegment(sketch, "E99.7.32", {"start": v(2.7, 8.74) * mm, "end": v(2.7, 8.79) * mm});
            skLineSegment(sketch, "E99.7.33", {"start": v(2.7, 8.4) * mm, "end": v(2.7, 8.45) * mm});
            skLineSegment(sketch, "E99.7.34", {"start": v(2.67, 8.98) * mm, "end": v(2.66, 9.03) * mm});
            skLineSegment(sketch, "E99.7.35", {"start": v(2.5, 9.17) * mm, "end": v(2.46, 9.18) * mm});
            skLineSegment(sketch, "E99.7.36", {"start": v(2.7, 8.64) * mm, "end": v(2.7, 8.69) * mm});
            skLineSegment(sketch, "E99.7.37", {"start": v(2.53, 9.16) * mm, "end": v(2.5, 9.17) * mm});
            skLineSegment(sketch, "E99.7.38", {"start": v(2.66, 9.03) * mm, "end": v(2.65, 9.08) * mm});
            skLineSegment(sketch, "E99.7.39", {"start": v(3.84, 8.69) * mm, "end": v(3.88, 8.67) * mm});
            skLineSegment(sketch, "E99.7.40", {"start": v(2.65, 9.08) * mm, "end": v(2.64, 9.13) * mm});
            skLineSegment(sketch, "E99.7.41", {"start": v(2.57, 9.15) * mm, "end": v(2.53, 9.16) * mm});
            skLineSegment(sketch, "E99.7.42", {"start": v(2.6, 9.14) * mm, "end": v(2.57, 9.15) * mm});
            skLineSegment(sketch, "E99.7.43", {"start": v(2.7, 8.27) * mm, "end": v(2.7, 8.31) * mm});
            skLineSegment(sketch, "E99.7.44", {"start": v(2.64, 9.13) * mm, "end": v(2.6, 9.14) * mm});
            skLineSegment(sketch, "E99.7.45", {"start": v(3.25, 8.07) * mm, "end": v(3.27, 8.1) * mm});
            skLineSegment(sketch, "E99.7.46", {"start": v(2.7, 8.05) * mm, "end": v(2.7, 8.07) * mm});
            skLineSegment(sketch, "E99.7.47", {"start": v(2.7, 8.18) * mm, "end": v(2.7, 8.22) * mm});
            skLineSegment(sketch, "E99.7.48", {"start": v(2.7, 8.22) * mm, "end": v(2.7, 8.27) * mm});
            skLineSegment(sketch, "E99.7.49", {"start": v(3.14, 7.92) * mm, "end": v(3.15, 7.94) * mm});
            skLineSegment(sketch, "E99.7.50", {"start": v(2.69, 8.09) * mm, "end": v(2.69, 8.1) * mm});
            skLineSegment(sketch, "E99.7.51", {"start": v(3.1, 7.9) * mm, "end": v(3.11, 7.9) * mm});
            skLineSegment(sketch, "E99.7.52", {"start": v(3.22, 8.03) * mm, "end": v(3.25, 8.07) * mm});
            skLineSegment(sketch, "E99.7.53", {"start": v(3.16, 7.95) * mm, "end": v(3.17, 7.97) * mm});
            skLineSegment(sketch, "E99.7.54", {"start": v(3.18, 7.98) * mm, "end": v(3.2, 8) * mm});
            skLineSegment(sketch, "E99.7.55", {"start": v(2.69, 8.1) * mm, "end": v(2.69, 8.12) * mm});
            skLineSegment(sketch, "E99.7.56", {"start": v(2.7, 8.16) * mm, "end": v(2.7, 8.18) * mm});
            skLineSegment(sketch, "E99.7.57", {"start": v(3.15, 7.94) * mm, "end": v(3.16, 7.95) * mm});
            skLineSegment(sketch, "E99.7.58", {"start": v(2.7, 8.04) * mm, "end": v(2.7, 8.05) * mm});
            skLineSegment(sketch, "E99.7.59", {"start": v(3.2, 8) * mm, "end": v(3.22, 8.03) * mm});
            skLineSegment(sketch, "E99.7.60", {"start": v(2.69, 8.14) * mm, "end": v(2.7, 8.16) * mm});
            skLineSegment(sketch, "E99.7.61", {"start": v(2.7, 8.07) * mm, "end": v(2.69, 8.09) * mm});
            skLineSegment(sketch, "E99.7.62", {"start": v(3.17, 7.97) * mm, "end": v(3.18, 7.98) * mm});
            skLineSegment(sketch, "E99.7.63", {"start": v(2.69, 8.12) * mm, "end": v(2.69, 8.14) * mm});
            skLineSegment(sketch, "E99.7.64", {"start": v(2.7, 8.02) * mm, "end": v(2.7, 8.04) * mm});
            skLineSegment(sketch, "E99.7.65", {"start": v(3.09, 7.88) * mm, "end": v(3.1, 7.9) * mm});
            skLineSegment(sketch, "E99.7.66", {"start": v(3.11, 7.9) * mm, "end": v(3.13, 7.91) * mm});
            skLineSegment(sketch, "E99.7.67", {"start": v(2.7, 8) * mm, "end": v(2.7, 8.02) * mm});
            skLineSegment(sketch, "E99.7.68", {"start": v(3.13, 7.91) * mm, "end": v(3.14, 7.92) * mm});
            skLineSegment(sketch, "E99.7.69", {"start": v(3.07, 7.87) * mm, "end": v(3.09, 7.88) * mm});
            skLineSegment(sketch, "E99.7.70", {"start": v(3.03, 7.86) * mm, "end": v(3.04, 7.86) * mm});
            skLineSegment(sketch, "E99.7.71", {"start": v(3.06, 7.87) * mm, "end": v(3.07, 7.87) * mm});
            skLineSegment(sketch, "E99.7.72", {"start": v(3.04, 7.86) * mm, "end": v(3.06, 7.87) * mm});
            skLineSegment(sketch, "E99.7.73", {"start": v(3, 7.85) * mm, "end": v(3.01, 7.85) * mm});
            skLineSegment(sketch, "E99.7.74", {"start": v(2.71, 8) * mm, "end": v(2.7, 8) * mm});
            skLineSegment(sketch, "E99.7.75", {"start": v(3.01, 7.85) * mm, "end": v(3.03, 7.86) * mm});
            skLineSegment(sketch, "E99.7.76", {"start": v(2.86, 7.87) * mm, "end": v(2.87, 7.87) * mm});
            skLineSegment(sketch, "E99.7.77", {"start": v(2.92, 7.85) * mm, "end": v(2.94, 7.85) * mm});
            skLineSegment(sketch, "E99.7.78", {"start": v(2.9, 7.86) * mm, "end": v(2.92, 7.85) * mm});
            skLineSegment(sketch, "E99.7.79", {"start": v(2.84, 7.88) * mm, "end": v(2.81, 7.9) * mm});
            skLineSegment(sketch, "E99.7.80", {"start": v(2.75, 7.94) * mm, "end": v(2.74, 7.95) * mm});
            skLineSegment(sketch, "E99.7.81", {"start": v(2.73, 7.96) * mm, "end": v(2.72, 7.98) * mm});
            skLineSegment(sketch, "E99.7.82", {"start": v(2.98, 7.85) * mm, "end": v(3, 7.85) * mm});
            skLineSegment(sketch, "E99.7.83", {"start": v(2.8, 7.9) * mm, "end": v(2.78, 7.91) * mm});
            skLineSegment(sketch, "E99.7.84", {"start": v(2.72, 7.98) * mm, "end": v(2.71, 8) * mm});
            skLineSegment(sketch, "E99.7.85", {"start": v(2.94, 7.85) * mm, "end": v(2.96, 7.85) * mm});
            skLineSegment(sketch, "E99.7.86", {"start": v(2.74, 7.95) * mm, "end": v(2.73, 7.96) * mm});
            skLineSegment(sketch, "E99.7.87", {"start": v(2.81, 7.9) * mm, "end": v(2.8, 7.9) * mm});
            skLineSegment(sketch, "E99.7.88", {"start": v(2.76, 7.93) * mm, "end": v(2.75, 7.94) * mm});
            skLineSegment(sketch, "E99.7.89", {"start": v(2.88, 7.87) * mm, "end": v(2.88, 7.86) * mm});
            skLineSegment(sketch, "E99.7.90", {"start": v(2.89, 7.86) * mm, "end": v(2.9, 7.86) * mm});
            skLineSegment(sketch, "E99.7.91", {"start": v(2.96, 7.85) * mm, "end": v(2.98, 7.85) * mm});
            skLineSegment(sketch, "E99.7.92", {"start": v(2.78, 7.91) * mm, "end": v(2.76, 7.93) * mm});
            skLineSegment(sketch, "E99.7.93", {"start": v(2.84, 7.88) * mm, "end": v(2.84, 7.88) * mm});
            skLineSegment(sketch, "E99.7.94", {"start": v(2.85, 7.88) * mm, "end": v(2.84, 7.88) * mm});
            skLineSegment(sketch, "E99.7.95", {"start": v(2.85, 7.87) * mm, "end": v(2.85, 7.88) * mm});
            skLineSegment(sketch, "E99.7.96", {"start": v(2.86, 7.87) * mm, "end": v(2.85, 7.87) * mm});
            skLineSegment(sketch, "E99.7.97", {"start": v(2.86, 7.87) * mm, "end": v(2.86, 7.87) * mm});
            skLineSegment(sketch, "E99.7.98", {"start": v(2.88, 7.86) * mm, "end": v(2.89, 7.86) * mm});
            skLineSegment(sketch, "E99.7.99", {"start": v(2.87, 7.87) * mm, "end": v(2.88, 7.87) * mm});
            skLineSegment(sketch, "E99.8.0", {"start": v(2.15, 9.07) * mm, "end": v(2.18, 9.1) * mm});
            skLineSegment(sketch, "E99.8.1", {"start": v(1.08, 9.26) * mm, "end": v(1.07, 9.3) * mm});
            skLineSegment(sketch, "E99.8.2", {"start": v(2.42, 9.19) * mm, "end": v(2.46, 9.18) * mm});
            skLineSegment(sketch, "E99.8.3", {"start": v(2.39, 9.2) * mm, "end": v(2.42, 9.19) * mm});
            skLineSegment(sketch, "E99.8.4", {"start": v(2.03, 8.92) * mm, "end": v(2.06, 8.95) * mm});
            skLineSegment(sketch, "E99.8.5", {"start": v(1.2, 8.84) * mm, "end": v(1.18, 8.89) * mm});
            skLineSegment(sketch, "E99.8.6", {"start": v(1.98, 8.84) * mm, "end": v(2, 8.88) * mm});
            skLineSegment(sketch, "E99.8.7", {"start": v(1.81, 8.55) * mm, "end": v(1.84, 8.6) * mm});
            skLineSegment(sketch, "E99.8.8", {"start": v(2, 8.88) * mm, "end": v(2.03, 8.92) * mm});
            skLineSegment(sketch, "E99.8.9", {"start": v(1.86, 8.64) * mm, "end": v(1.88, 8.68) * mm});
            skLineSegment(sketch, "E99.8.10", {"start": v(1.17, 8.93) * mm, "end": v(1.16, 8.98) * mm});
            skLineSegment(sketch, "E99.8.11", {"start": v(1.21, 8.7) * mm, "end": v(1.2, 8.75) * mm});
            skLineSegment(sketch, "E99.8.12", {"start": v(1.15, 9.03) * mm, "end": v(1.14, 9.07) * mm});
            skLineSegment(sketch, "E99.8.13", {"start": v(1.93, 8.76) * mm, "end": v(1.95, 8.8) * mm});
            skLineSegment(sketch, "E99.8.14", {"start": v(2.18, 9.1) * mm, "end": v(2.21, 9.15) * mm});
            skLineSegment(sketch, "E99.8.15", {"start": v(1.9, 8.72) * mm, "end": v(1.93, 8.76) * mm});
            skLineSegment(sketch, "E99.8.16", {"start": v(2.12, 9.03) * mm, "end": v(2.15, 9.07) * mm});
            skLineSegment(sketch, "E99.8.17", {"start": v(1.95, 8.8) * mm, "end": v(1.98, 8.84) * mm});
            skLineSegment(sketch, "E99.8.18", {"start": v(1.1, 9.21) * mm, "end": v(1.08, 9.26) * mm});
            skLineSegment(sketch, "E99.8.19", {"start": v(2.21, 9.15) * mm, "end": v(2.24, 9.19) * mm});
            skLineSegment(sketch, "E99.8.20", {"start": v(2.35, 9.2) * mm, "end": v(2.39, 9.2) * mm});
            skLineSegment(sketch, "E99.8.21", {"start": v(1.22, 8.66) * mm, "end": v(1.21, 8.7) * mm});
            skLineSegment(sketch, "E99.8.22", {"start": v(1.2, 8.8) * mm, "end": v(1.2, 8.84) * mm});
            skLineSegment(sketch, "E99.8.23", {"start": v(1.12, 9.12) * mm, "end": v(1.11, 9.17) * mm});
            skLineSegment(sketch, "E99.8.24", {"start": v(2.06, 8.95) * mm, "end": v(2.1, 9) * mm});
            skLineSegment(sketch, "E99.8.25", {"start": v(1.84, 8.6) * mm, "end": v(1.86, 8.64) * mm});
            skLineSegment(sketch, "E99.8.26", {"start": v(2.24, 9.19) * mm, "end": v(2.28, 9.22) * mm});
            skLineSegment(sketch, "E99.8.27", {"start": v(2.31, 9.21) * mm, "end": v(2.35, 9.2) * mm});
            skLineSegment(sketch, "E99.8.28", {"start": v(2.1, 9) * mm, "end": v(2.12, 9.03) * mm});
            skLineSegment(sketch, "E99.8.29", {"start": v(1.18, 8.89) * mm, "end": v(1.17, 8.93) * mm});
            skLineSegment(sketch, "E99.8.30", {"start": v(1.11, 9.17) * mm, "end": v(1.1, 9.21) * mm});
            skLineSegment(sketch, "E99.8.31", {"start": v(1.88, 8.68) * mm, "end": v(1.9, 8.72) * mm});
            skLineSegment(sketch, "E99.8.32", {"start": v(1.14, 9.07) * mm, "end": v(1.12, 9.12) * mm});
            skLineSegment(sketch, "E99.8.33", {"start": v(1.2, 8.75) * mm, "end": v(1.2, 8.8) * mm});
            skLineSegment(sketch, "E99.8.34", {"start": v(1.07, 9.3) * mm, "end": v(1.05, 9.35) * mm});
            skLineSegment(sketch, "E99.8.35", {"start": v(0.87, 9.46) * mm, "end": v(0.83, 9.46) * mm});
            skLineSegment(sketch, "E99.8.36", {"start": v(1.16, 8.98) * mm, "end": v(1.15, 9.03) * mm});
            skLineSegment(sketch, "E99.8.37", {"start": v(0.9, 9.46) * mm, "end": v(0.87, 9.46) * mm});
            skLineSegment(sketch, "E99.8.38", {"start": v(1.05, 9.35) * mm, "end": v(1.03, 9.4) * mm});
            skLineSegment(sketch, "E99.8.39", {"start": v(2.28, 9.22) * mm, "end": v(2.31, 9.21) * mm});
            skLineSegment(sketch, "E99.8.40", {"start": v(1.03, 9.4) * mm, "end": v(1.02, 9.45) * mm});
            skLineSegment(sketch, "E99.8.41", {"start": v(0.94, 9.45) * mm, "end": v(0.9, 9.46) * mm});
            skLineSegment(sketch, "E99.8.42", {"start": v(0.98, 9.45) * mm, "end": v(0.94, 9.45) * mm});
            skLineSegment(sketch, "E99.8.43", {"start": v(1.23, 8.61) * mm, "end": v(1.22, 8.66) * mm});
            skLineSegment(sketch, "E99.8.44", {"start": v(1.02, 9.45) * mm, "end": v(0.98, 9.45) * mm});
            skLineSegment(sketch, "E99.8.45", {"start": v(1.8, 8.51) * mm, "end": v(1.81, 8.55) * mm});
            skLineSegment(sketch, "E99.8.46", {"start": v(1.25, 8.4) * mm, "end": v(1.25, 8.42) * mm});
            skLineSegment(sketch, "E99.8.47", {"start": v(1.23, 8.52) * mm, "end": v(1.23, 8.57) * mm});
            skLineSegment(sketch, "E99.8.48", {"start": v(1.23, 8.57) * mm, "end": v(1.23, 8.61) * mm});
            skLineSegment(sketch, "E99.8.49", {"start": v(1.71, 8.35) * mm, "end": v(1.72, 8.36) * mm});
            skLineSegment(sketch, "E99.8.50", {"start": v(1.24, 8.43) * mm, "end": v(1.24, 8.45) * mm});
            skLineSegment(sketch, "E99.8.51", {"start": v(1.68, 8.31) * mm, "end": v(1.7, 8.32) * mm});
            skLineSegment(sketch, "E99.8.52", {"start": v(1.78, 8.47) * mm, "end": v(1.8, 8.51) * mm});
            skLineSegment(sketch, "E99.8.53", {"start": v(1.73, 8.38) * mm, "end": v(1.74, 8.4) * mm});
            skLineSegment(sketch, "E99.8.54", {"start": v(1.75, 8.41) * mm, "end": v(1.76, 8.43) * mm});
            skLineSegment(sketch, "E99.8.55", {"start": v(1.24, 8.45) * mm, "end": v(1.24, 8.47) * mm});
            skLineSegment(sketch, "E99.8.56", {"start": v(1.23, 8.5) * mm, "end": v(1.23, 8.52) * mm});
            skLineSegment(sketch, "E99.8.57", {"start": v(1.72, 8.36) * mm, "end": v(1.73, 8.38) * mm});
            skLineSegment(sketch, "E99.8.58", {"start": v(1.26, 8.38) * mm, "end": v(1.25, 8.4) * mm});
            skLineSegment(sketch, "E99.8.59", {"start": v(1.76, 8.43) * mm, "end": v(1.78, 8.47) * mm});
            skLineSegment(sketch, "E99.8.60", {"start": v(1.23, 8.48) * mm, "end": v(1.23, 8.5) * mm});
            skLineSegment(sketch, "E99.8.61", {"start": v(1.25, 8.42) * mm, "end": v(1.24, 8.43) * mm});
            skLineSegment(sketch, "E99.8.62", {"start": v(1.74, 8.4) * mm, "end": v(1.75, 8.41) * mm});
            skLineSegment(sketch, "E99.8.63", {"start": v(1.24, 8.47) * mm, "end": v(1.23, 8.48) * mm});
            skLineSegment(sketch, "E99.8.64", {"start": v(1.27, 8.37) * mm, "end": v(1.26, 8.38) * mm});
            skLineSegment(sketch, "E99.8.65", {"start": v(1.67, 8.3) * mm, "end": v(1.68, 8.31) * mm});
            skLineSegment(sketch, "E99.8.66", {"start": v(1.7, 8.32) * mm, "end": v(1.7, 8.34) * mm});
            skLineSegment(sketch, "E99.8.67", {"start": v(1.28, 8.36) * mm, "end": v(1.27, 8.37) * mm});
            skLineSegment(sketch, "E99.8.68", {"start": v(1.7, 8.34) * mm, "end": v(1.71, 8.35) * mm});
            skLineSegment(sketch, "E99.8.69", {"start": v(1.66, 8.29) * mm, "end": v(1.67, 8.3) * mm});
            skLineSegment(sketch, "E99.8.70", {"start": v(1.62, 8.26) * mm, "end": v(1.63, 8.27) * mm});
            skLineSegment(sketch, "E99.8.71", {"start": v(1.65, 8.28) * mm, "end": v(1.66, 8.29) * mm});
            skLineSegment(sketch, "E99.8.72", {"start": v(1.63, 8.27) * mm, "end": v(1.65, 8.28) * mm});
            skLineSegment(sketch, "E99.8.73", {"start": v(1.59, 8.25) * mm, "end": v(1.6, 8.26) * mm});
            skLineSegment(sketch, "E99.8.74", {"start": v(1.29, 8.34) * mm, "end": v(1.28, 8.36) * mm});
            skLineSegment(sketch, "E99.8.75", {"start": v(1.6, 8.26) * mm, "end": v(1.62, 8.26) * mm});
            skLineSegment(sketch, "E99.8.76", {"start": v(1.45, 8.25) * mm, "end": v(1.46, 8.25) * mm});
            skLineSegment(sketch, "E99.8.77", {"start": v(1.51, 8.24) * mm, "end": v(1.53, 8.24) * mm});
            skLineSegment(sketch, "E99.8.78", {"start": v(1.48, 8.24) * mm, "end": v(1.51, 8.24) * mm});
            skLineSegment(sketch, "E99.8.79", {"start": v(1.42, 8.25) * mm, "end": v(1.4, 8.26) * mm});
            skLineSegment(sketch, "E99.8.80", {"start": v(1.33, 8.3) * mm, "end": v(1.32, 8.3) * mm});
            skLineSegment(sketch, "E99.8.81", {"start": v(1.3, 8.32) * mm, "end": v(1.3, 8.33) * mm});
            skLineSegment(sketch, "E99.8.82", {"start": v(1.57, 8.24) * mm, "end": v(1.59, 8.25) * mm});
            skLineSegment(sketch, "E99.8.83", {"start": v(1.38, 8.27) * mm, "end": v(1.36, 8.28) * mm});
            skLineSegment(sketch, "E99.8.84", {"start": v(1.3, 8.33) * mm, "end": v(1.29, 8.34) * mm});
            skLineSegment(sketch, "E99.8.85", {"start": v(1.53, 8.24) * mm, "end": v(1.55, 8.24) * mm});
            skLineSegment(sketch, "E99.8.86", {"start": v(1.32, 8.3) * mm, "end": v(1.3, 8.32) * mm});
            skLineSegment(sketch, "E99.8.87", {"start": v(1.4, 8.26) * mm, "end": v(1.38, 8.27) * mm});
            skLineSegment(sketch, "E99.8.88", {"start": v(1.34, 8.28) * mm, "end": v(1.33, 8.3) * mm});
            skLineSegment(sketch, "E99.8.89", {"start": v(1.47, 8.25) * mm, "end": v(1.47, 8.24) * mm});
            skLineSegment(sketch, "E99.8.90", {"start": v(1.48, 8.24) * mm, "end": v(1.48, 8.24) * mm});
            skLineSegment(sketch, "E99.8.91", {"start": v(1.55, 8.24) * mm, "end": v(1.57, 8.24) * mm});
            skLineSegment(sketch, "E99.8.92", {"start": v(1.36, 8.28) * mm, "end": v(1.34, 8.28) * mm});
            skLineSegment(sketch, "E99.8.93", {"start": v(1.43, 8.25) * mm, "end": v(1.42, 8.25) * mm});
            skLineSegment(sketch, "E99.8.94", {"start": v(1.44, 8.25) * mm, "end": v(1.43, 8.25) * mm});
            skLineSegment(sketch, "E99.8.95", {"start": v(1.44, 8.25) * mm, "end": v(1.44, 8.25) * mm});
            skLineSegment(sketch, "E99.8.96", {"start": v(1.45, 8.25) * mm, "end": v(1.44, 8.25) * mm});
            skLineSegment(sketch, "E99.8.97", {"start": v(1.45, 8.25) * mm, "end": v(1.45, 8.25) * mm});
            skLineSegment(sketch, "E99.8.98", {"start": v(1.47, 8.24) * mm, "end": v(1.48, 8.24) * mm});
            skLineSegment(sketch, "E99.8.99", {"start": v(1.46, 8.25) * mm, "end": v(1.47, 8.25) * mm});
            skLineSegment(sketch, "E99.9.0", {"start": v(0.54, 9.3) * mm, "end": v(0.57, 9.35) * mm});
            skLineSegment(sketch, "E99.9.1", {"start": v(-0.54, 9.3) * mm, "end": v(-0.57, 9.35) * mm});
            skLineSegment(sketch, "E99.9.2", {"start": v(0.8, 9.47) * mm, "end": v(0.83, 9.46) * mm});
            skLineSegment(sketch, "E99.9.3", {"start": v(0.75, 9.47) * mm, "end": v(0.8, 9.47) * mm});
            skLineSegment(sketch, "E99.9.4", {"start": v(0.46, 9.13) * mm, "end": v(0.48, 9.18) * mm});
            skLineSegment(sketch, "E99.9.5", {"start": v(-0.36, 8.91) * mm, "end": v(-0.38, 8.96) * mm});
            skLineSegment(sketch, "E99.9.6", {"start": v(0.42, 9.05) * mm, "end": v(0.44, 9.09) * mm});
            skLineSegment(sketch, "E99.9.7", {"start": v(0.3, 8.74) * mm, "end": v(0.32, 8.78) * mm});
            skLineSegment(sketch, "E99.9.8", {"start": v(0.44, 9.09) * mm, "end": v(0.46, 9.13) * mm});
            skLineSegment(sketch, "E99.9.9", {"start": v(0.33, 8.83) * mm, "end": v(0.35, 8.87) * mm});
            skLineSegment(sketch, "E99.9.10", {"start": v(-0.4, 9) * mm, "end": v(-0.42, 9.05) * mm});
            skLineSegment(sketch, "E99.9.11", {"start": v(-0.32, 8.78) * mm, "end": v(-0.33, 8.83) * mm});
            skLineSegment(sketch, "E99.9.12", {"start": v(-0.44, 9.09) * mm, "end": v(-0.46, 9.13) * mm});
            skLineSegment(sketch, "E99.9.13", {"start": v(0.38, 8.96) * mm, "end": v(0.4, 9) * mm});
            skLineSegment(sketch, "E99.9.14", {"start": v(0.57, 9.35) * mm, "end": v(0.6, 9.4) * mm});
            skLineSegment(sketch, "E99.9.15", {"start": v(0.36, 8.91) * mm, "end": v(0.38, 8.96) * mm});
            skLineSegment(sketch, "E99.9.16", {"start": v(0.52, 9.26) * mm, "end": v(0.54, 9.3) * mm});
            skLineSegment(sketch, "E99.9.17", {"start": v(0.4, 9) * mm, "end": v(0.42, 9.05) * mm});
            skLineSegment(sketch, "E99.9.18", {"start": v(-0.52, 9.26) * mm, "end": v(-0.54, 9.3) * mm});
            skLineSegment(sketch, "E99.9.19", {"start": v(0.6, 9.4) * mm, "end": v(0.61, 9.44) * mm});
            skLineSegment(sketch, "E99.9.20", {"start": v(0.72, 9.47) * mm, "end": v(0.75, 9.47) * mm});
            skLineSegment(sketch, "E99.9.21", {"start": v(-0.3, 8.74) * mm, "end": v(-0.32, 8.78) * mm});
            skLineSegment(sketch, "E99.9.22", {"start": v(-0.35, 8.87) * mm, "end": v(-0.36, 8.91) * mm});
            skLineSegment(sketch, "E99.9.23", {"start": v(-0.48, 9.18) * mm, "end": v(-0.5, 9.22) * mm});
            skLineSegment(sketch, "E99.9.24", {"start": v(0.48, 9.18) * mm, "end": v(0.5, 9.22) * mm});
            skLineSegment(sketch, "E99.9.25", {"start": v(0.32, 8.78) * mm, "end": v(0.33, 8.83) * mm});
            skLineSegment(sketch, "E99.9.26", {"start": v(0.61, 9.44) * mm, "end": v(0.64, 9.48) * mm});
            skLineSegment(sketch, "E99.9.27", {"start": v(0.68, 9.48) * mm, "end": v(0.72, 9.47) * mm});
            skLineSegment(sketch, "E99.9.28", {"start": v(0.5, 9.22) * mm, "end": v(0.52, 9.26) * mm});
            skLineSegment(sketch, "E99.9.29", {"start": v(-0.38, 8.96) * mm, "end": v(-0.4, 9) * mm});
            skLineSegment(sketch, "E99.9.30", {"start": v(-0.5, 9.22) * mm, "end": v(-0.52, 9.26) * mm});
            skLineSegment(sketch, "E99.9.31", {"start": v(0.35, 8.87) * mm, "end": v(0.36, 8.91) * mm});
            skLineSegment(sketch, "E99.9.32", {"start": v(-0.46, 9.13) * mm, "end": v(-0.48, 9.18) * mm});
            skLineSegment(sketch, "E99.9.33", {"start": v(-0.33, 8.83) * mm, "end": v(-0.35, 8.87) * mm});
            skLineSegment(sketch, "E99.9.34", {"start": v(-0.57, 9.35) * mm, "end": v(-0.6, 9.4) * mm});
            skLineSegment(sketch, "E99.9.35", {"start": v(-0.8, 9.47) * mm, "end": v(-0.83, 9.46) * mm});
            skLineSegment(sketch, "E99.9.36", {"start": v(-0.42, 9.05) * mm, "end": v(-0.44, 9.09) * mm});
            skLineSegment(sketch, "E99.9.37", {"start": v(-0.75, 9.47) * mm, "end": v(-0.8, 9.47) * mm});
            skLineSegment(sketch, "E99.9.38", {"start": v(-0.6, 9.4) * mm, "end": v(-0.61, 9.44) * mm});
            skLineSegment(sketch, "E99.9.39", {"start": v(0.64, 9.48) * mm, "end": v(0.68, 9.48) * mm});
            skLineSegment(sketch, "E99.9.40", {"start": v(-0.61, 9.44) * mm, "end": v(-0.64, 9.48) * mm});
            skLineSegment(sketch, "E99.9.41", {"start": v(-0.72, 9.47) * mm, "end": v(-0.75, 9.47) * mm});
            skLineSegment(sketch, "E99.9.42", {"start": v(-0.68, 9.48) * mm, "end": v(-0.72, 9.47) * mm});
            skLineSegment(sketch, "E99.9.43", {"start": v(-0.29, 8.7) * mm, "end": v(-0.3, 8.74) * mm});
            skLineSegment(sketch, "E99.9.44", {"start": v(-0.64, 9.48) * mm, "end": v(-0.68, 9.48) * mm});
            skLineSegment(sketch, "E99.9.45", {"start": v(0.29, 8.7) * mm, "end": v(0.3, 8.74) * mm});
            skLineSegment(sketch, "E99.9.46", {"start": v(-0.22, 8.5) * mm, "end": v(-0.23, 8.5) * mm});
            skLineSegment(sketch, "E99.9.47", {"start": v(-0.27, 8.6) * mm, "end": v(-0.28, 8.65) * mm});
            skLineSegment(sketch, "E99.9.48", {"start": v(-0.28, 8.65) * mm, "end": v(-0.29, 8.7) * mm});
            skLineSegment(sketch, "E99.9.49", {"start": v(0.24, 8.52) * mm, "end": v(0.25, 8.54) * mm});
            skLineSegment(sketch, "E99.9.50", {"start": v(-0.24, 8.52) * mm, "end": v(-0.25, 8.54) * mm});
            skLineSegment(sketch, "E99.9.51", {"start": v(0.21, 8.48) * mm, "end": v(0.22, 8.5) * mm});
            skLineSegment(sketch, "E99.9.52", {"start": v(0.28, 8.65) * mm, "end": v(0.29, 8.7) * mm});
            skLineSegment(sketch, "E99.9.53", {"start": v(0.25, 8.55) * mm, "end": v(0.26, 8.57) * mm});
            skLineSegment(sketch, "E99.9.54", {"start": v(0.26, 8.59) * mm, "end": v(0.27, 8.6) * mm});
            skLineSegment(sketch, "E99.9.55", {"start": v(-0.25, 8.54) * mm, "end": v(-0.25, 8.55) * mm});
            skLineSegment(sketch, "E99.9.56", {"start": v(-0.26, 8.59) * mm, "end": v(-0.27, 8.6) * mm});
            skLineSegment(sketch, "E99.9.57", {"start": v(0.25, 8.54) * mm, "end": v(0.25, 8.55) * mm});
            skLineSegment(sketch, "E99.9.58", {"start": v(-0.21, 8.48) * mm, "end": v(-0.22, 8.5) * mm});
            skLineSegment(sketch, "E99.9.59", {"start": v(0.27, 8.6) * mm, "end": v(0.28, 8.65) * mm});
            skLineSegment(sketch, "E99.9.60", {"start": v(-0.26, 8.57) * mm, "end": v(-0.26, 8.59) * mm});
            skLineSegment(sketch, "E99.9.61", {"start": v(-0.23, 8.5) * mm, "end": v(-0.24, 8.52) * mm});
            skLineSegment(sketch, "E99.9.62", {"start": v(0.26, 8.57) * mm, "end": v(0.26, 8.59) * mm});
            skLineSegment(sketch, "E99.9.63", {"start": v(-0.25, 8.55) * mm, "end": v(-0.26, 8.57) * mm});
            skLineSegment(sketch, "E99.9.64", {"start": v(-0.2, 8.46) * mm, "end": v(-0.21, 8.48) * mm});
            skLineSegment(sketch, "E99.9.65", {"start": v(0.2, 8.46) * mm, "end": v(0.21, 8.48) * mm});
            skLineSegment(sketch, "E99.9.66", {"start": v(0.22, 8.5) * mm, "end": v(0.23, 8.5) * mm});
            skLineSegment(sketch, "E99.9.67", {"start": v(-0.2, 8.45) * mm, "end": v(-0.2, 8.46) * mm});
            skLineSegment(sketch, "E99.9.68", {"start": v(0.23, 8.5) * mm, "end": v(0.24, 8.52) * mm});
            skLineSegment(sketch, "E99.9.69", {"start": v(0.2, 8.45) * mm, "end": v(0.2, 8.46) * mm});
            skLineSegment(sketch, "E99.9.70", {"start": v(0.16, 8.42) * mm, "end": v(0.17, 8.43) * mm});
            skLineSegment(sketch, "E99.9.71", {"start": v(0.18, 8.44) * mm, "end": v(0.2, 8.45) * mm});
            skLineSegment(sketch, "E99.9.72", {"start": v(0.17, 8.43) * mm, "end": v(0.18, 8.44) * mm});
            skLineSegment(sketch, "E99.9.73", {"start": v(0.13, 8.4) * mm, "end": v(0.14, 8.4) * mm});
            skLineSegment(sketch, "E99.9.74", {"start": v(-0.18, 8.44) * mm, "end": v(-0.2, 8.45) * mm});
            skLineSegment(sketch, "E99.9.75", {"start": v(0.14, 8.4) * mm, "end": v(0.16, 8.42) * mm});
            skLineSegment(sketch, "E99.9.76", {"start": v(0, 8.38) * mm, "end": v(0, 8.37) * mm});
            skLineSegment(sketch, "E99.9.77", {"start": v(0.06, 8.38) * mm, "end": v(0.08, 8.38) * mm});
            skLineSegment(sketch, "E99.9.78", {"start": v(0.03, 8.37) * mm, "end": v(0.06, 8.38) * mm});
            skLineSegment(sketch, "E99.9.79", {"start": v(-0.03, 8.37) * mm, "end": v(-0.06, 8.38) * mm});
            skLineSegment(sketch, "E99.9.80", {"start": v(-0.13, 8.4) * mm, "end": v(-0.14, 8.4) * mm});
            skLineSegment(sketch, "E99.9.81", {"start": v(-0.16, 8.42) * mm, "end": v(-0.17, 8.43) * mm});
            skLineSegment(sketch, "E99.9.82", {"start": v(0.11, 8.4) * mm, "end": v(0.13, 8.4) * mm});
            skLineSegment(sketch, "E99.9.83", {"start": v(-0.08, 8.38) * mm, "end": v(-0.1, 8.39) * mm});
            skLineSegment(sketch, "E99.9.84", {"start": v(-0.17, 8.43) * mm, "end": v(-0.18, 8.44) * mm});
            skLineSegment(sketch, "E99.9.85", {"start": v(0.08, 8.38) * mm, "end": v(0.1, 8.39) * mm});
            skLineSegment(sketch, "E99.9.86", {"start": v(-0.14, 8.4) * mm, "end": v(-0.16, 8.42) * mm});
            skLineSegment(sketch, "E99.9.87", {"start": v(-0.06, 8.38) * mm, "end": v(-0.08, 8.38) * mm});
            skLineSegment(sketch, "E99.9.88", {"start": v(-0.11, 8.4) * mm, "end": v(-0.13, 8.4) * mm});
            skLineSegment(sketch, "E99.9.89", {"start": v(0.01, 8.37) * mm, "end": v(0.02, 8.37) * mm});
            skLineSegment(sketch, "E99.9.90", {"start": v(0.02, 8.37) * mm, "end": v(0.03, 8.37) * mm});
            skLineSegment(sketch, "E99.9.91", {"start": v(0.1, 8.39) * mm, "end": v(0.11, 8.4) * mm});
            skLineSegment(sketch, "E99.9.92", {"start": v(-0.1, 8.39) * mm, "end": v(-0.11, 8.4) * mm});
            skLineSegment(sketch, "E99.9.93", {"start": v(-0.02, 8.37) * mm, "end": v(-0.03, 8.37) * mm});
            skLineSegment(sketch, "E99.9.94", {"start": v(-0.02, 8.37) * mm, "end": v(-0.02, 8.37) * mm});
            skLineSegment(sketch, "E99.9.95", {"start": v(-0.01, 8.37) * mm, "end": v(-0.02, 8.37) * mm});
            skLineSegment(sketch, "E99.9.96", {"start": v(0, 8.37) * mm, "end": v(-0.01, 8.37) * mm});
            skLineSegment(sketch, "E99.9.97", {"start": v(0, 8.38) * mm, "end": v(0, 8.37) * mm});
            skLineSegment(sketch, "E99.9.98", {"start": v(0.02, 8.37) * mm, "end": v(0.02, 8.37) * mm});
            skLineSegment(sketch, "E99.9.99", {"start": v(0, 8.37) * mm, "end": v(0.01, 8.37) * mm});
            skLineSegment(sketch, "E99.10.0", {"start": v(-1.08, 9.26) * mm, "end": v(-1.07, 9.3) * mm});
            skLineSegment(sketch, "E99.10.1", {"start": v(-2.15, 9.07) * mm, "end": v(-2.18, 9.1) * mm});
            skLineSegment(sketch, "E99.10.2", {"start": v(-0.87, 9.46) * mm, "end": v(-0.83, 9.46) * mm});
            skLineSegment(sketch, "E99.10.3", {"start": v(-0.9, 9.46) * mm, "end": v(-0.87, 9.46) * mm});
            skLineSegment(sketch, "E99.10.4", {"start": v(-1.14, 9.07) * mm, "end": v(-1.12, 9.12) * mm});
            skLineSegment(sketch, "E99.10.5", {"start": v(-1.9, 8.72) * mm, "end": v(-1.93, 8.76) * mm});
            skLineSegment(sketch, "E99.10.6", {"start": v(-1.16, 8.98) * mm, "end": v(-1.15, 9.03) * mm});
            skLineSegment(sketch, "E99.10.7", {"start": v(-1.22, 8.66) * mm, "end": v(-1.21, 8.7) * mm});
            skLineSegment(sketch, "E99.10.8", {"start": v(-1.15, 9.03) * mm, "end": v(-1.14, 9.07) * mm});
            skLineSegment(sketch, "E99.10.9", {"start": v(-1.2, 8.75) * mm, "end": v(-1.2, 8.8) * mm});
            skLineSegment(sketch, "E99.10.10", {"start": v(-1.95, 8.8) * mm, "end": v(-1.98, 8.84) * mm});
            skLineSegment(sketch, "E99.10.11", {"start": v(-1.84, 8.6) * mm, "end": v(-1.86, 8.64) * mm});
            skLineSegment(sketch, "E99.10.12", {"start": v(-2, 8.88) * mm, "end": v(-2.03, 8.92) * mm});
            skLineSegment(sketch, "E99.10.13", {"start": v(-1.18, 8.89) * mm, "end": v(-1.17, 8.93) * mm});
            skLineSegment(sketch, "E99.10.14", {"start": v(-1.07, 9.3) * mm, "end": v(-1.05, 9.35) * mm});
            skLineSegment(sketch, "E99.10.15", {"start": v(-1.2, 8.84) * mm, "end": v(-1.18, 8.89) * mm});
            skLineSegment(sketch, "E99.10.16", {"start": v(-1.1, 9.21) * mm, "end": v(-1.08, 9.26) * mm});
            skLineSegment(sketch, "E99.10.17", {"start": v(-1.17, 8.93) * mm, "end": v(-1.16, 8.98) * mm});
            skLineSegment(sketch, "E99.10.18", {"start": v(-2.12, 9.03) * mm, "end": v(-2.15, 9.07) * mm});
            skLineSegment(sketch, "E99.10.19", {"start": v(-1.05, 9.35) * mm, "end": v(-1.03, 9.4) * mm});
            skLineSegment(sketch, "E99.10.20", {"start": v(-0.94, 9.45) * mm, "end": v(-0.9, 9.46) * mm});
            skLineSegment(sketch, "E99.10.21", {"start": v(-1.81, 8.55) * mm, "end": v(-1.84, 8.6) * mm});
            skLineSegment(sketch, "E99.10.22", {"start": v(-1.88, 8.68) * mm, "end": v(-1.9, 8.72) * mm});
            skLineSegment(sketch, "E99.10.23", {"start": v(-2.06, 8.95) * mm, "end": v(-2.1, 9) * mm});
            skLineSegment(sketch, "E99.10.24", {"start": v(-1.12, 9.12) * mm, "end": v(-1.11, 9.17) * mm});
            skLineSegment(sketch, "E99.10.25", {"start": v(-1.21, 8.7) * mm, "end": v(-1.2, 8.75) * mm});
            skLineSegment(sketch, "E99.10.26", {"start": v(-1.03, 9.4) * mm, "end": v(-1.02, 9.45) * mm});
            skLineSegment(sketch, "E99.10.27", {"start": v(-0.98, 9.45) * mm, "end": v(-0.94, 9.45) * mm});
            skLineSegment(sketch, "E99.10.28", {"start": v(-1.11, 9.17) * mm, "end": v(-1.1, 9.21) * mm});
            skLineSegment(sketch, "E99.10.29", {"start": v(-1.93, 8.76) * mm, "end": v(-1.95, 8.8) * mm});
            skLineSegment(sketch, "E99.10.30", {"start": v(-2.1, 9) * mm, "end": v(-2.12, 9.03) * mm});
            skLineSegment(sketch, "E99.10.31", {"start": v(-1.2, 8.8) * mm, "end": v(-1.2, 8.84) * mm});
            skLineSegment(sketch, "E99.10.32", {"start": v(-2.03, 8.92) * mm, "end": v(-2.06, 8.95) * mm});
            skLineSegment(sketch, "E99.10.33", {"start": v(-1.86, 8.64) * mm, "end": v(-1.88, 8.68) * mm});
            skLineSegment(sketch, "E99.10.34", {"start": v(-2.18, 9.1) * mm, "end": v(-2.21, 9.15) * mm});
            skLineSegment(sketch, "E99.10.35", {"start": v(-2.42, 9.19) * mm, "end": v(-2.46, 9.18) * mm});
            skLineSegment(sketch, "E99.10.36", {"start": v(-1.98, 8.84) * mm, "end": v(-2, 8.88) * mm});
            skLineSegment(sketch, "E99.10.37", {"start": v(-2.39, 9.2) * mm, "end": v(-2.42, 9.19) * mm});
            skLineSegment(sketch, "E99.10.38", {"start": v(-2.21, 9.15) * mm, "end": v(-2.24, 9.19) * mm});
            skLineSegment(sketch, "E99.10.39", {"start": v(-1.02, 9.45) * mm, "end": v(-0.98, 9.45) * mm});
            skLineSegment(sketch, "E99.10.40", {"start": v(-2.24, 9.19) * mm, "end": v(-2.28, 9.22) * mm});
            skLineSegment(sketch, "E99.10.41", {"start": v(-2.35, 9.2) * mm, "end": v(-2.39, 9.2) * mm});
            skLineSegment(sketch, "E99.10.42", {"start": v(-2.31, 9.21) * mm, "end": v(-2.35, 9.2) * mm});
            skLineSegment(sketch, "E99.10.43", {"start": v(-1.8, 8.51) * mm, "end": v(-1.81, 8.55) * mm});
            skLineSegment(sketch, "E99.10.44", {"start": v(-2.28, 9.22) * mm, "end": v(-2.31, 9.21) * mm});
            skLineSegment(sketch, "E99.10.45", {"start": v(-1.23, 8.61) * mm, "end": v(-1.22, 8.66) * mm});
            skLineSegment(sketch, "E99.10.46", {"start": v(-1.7, 8.32) * mm, "end": v(-1.7, 8.34) * mm});
            skLineSegment(sketch, "E99.10.47", {"start": v(-1.76, 8.43) * mm, "end": v(-1.78, 8.47) * mm});
            skLineSegment(sketch, "E99.10.48", {"start": v(-1.78, 8.47) * mm, "end": v(-1.8, 8.51) * mm});
            skLineSegment(sketch, "E99.10.49", {"start": v(-1.24, 8.43) * mm, "end": v(-1.24, 8.45) * mm});
            skLineSegment(sketch, "E99.10.50", {"start": v(-1.71, 8.35) * mm, "end": v(-1.72, 8.36) * mm});
            skLineSegment(sketch, "E99.10.51", {"start": v(-1.26, 8.38) * mm, "end": v(-1.25, 8.4) * mm});
            skLineSegment(sketch, "E99.10.52", {"start": v(-1.23, 8.57) * mm, "end": v(-1.23, 8.61) * mm});
            skLineSegment(sketch, "E99.10.53", {"start": v(-1.24, 8.47) * mm, "end": v(-1.23, 8.48) * mm});
            skLineSegment(sketch, "E99.10.54", {"start": v(-1.23, 8.5) * mm, "end": v(-1.23, 8.52) * mm});
            skLineSegment(sketch, "E99.10.55", {"start": v(-1.72, 8.36) * mm, "end": v(-1.73, 8.38) * mm});
            skLineSegment(sketch, "E99.10.56", {"start": v(-1.75, 8.41) * mm, "end": v(-1.76, 8.43) * mm});
            skLineSegment(sketch, "E99.10.57", {"start": v(-1.24, 8.45) * mm, "end": v(-1.24, 8.47) * mm});
            skLineSegment(sketch, "E99.10.58", {"start": v(-1.68, 8.31) * mm, "end": v(-1.7, 8.32) * mm});
            skLineSegment(sketch, "E99.10.59", {"start": v(-1.23, 8.52) * mm, "end": v(-1.23, 8.57) * mm});
            skLineSegment(sketch, "E99.10.60", {"start": v(-1.74, 8.4) * mm, "end": v(-1.75, 8.41) * mm});
            skLineSegment(sketch, "E99.10.61", {"start": v(-1.7, 8.34) * mm, "end": v(-1.71, 8.35) * mm});
            skLineSegment(sketch, "E99.10.62", {"start": v(-1.23, 8.48) * mm, "end": v(-1.23, 8.5) * mm});
            skLineSegment(sketch, "E99.10.63", {"start": v(-1.73, 8.38) * mm, "end": v(-1.74, 8.4) * mm});
            skLineSegment(sketch, "E99.10.64", {"start": v(-1.67, 8.3) * mm, "end": v(-1.68, 8.31) * mm});
            skLineSegment(sketch, "E99.10.65", {"start": v(-1.27, 8.37) * mm, "end": v(-1.26, 8.38) * mm});
            skLineSegment(sketch, "E99.10.66", {"start": v(-1.25, 8.4) * mm, "end": v(-1.25, 8.42) * mm});
            skLineSegment(sketch, "E99.10.67", {"start": v(-1.66, 8.29) * mm, "end": v(-1.67, 8.3) * mm});
            skLineSegment(sketch, "E99.10.68", {"start": v(-1.25, 8.42) * mm, "end": v(-1.24, 8.43) * mm});
            skLineSegment(sketch, "E99.10.69", {"start": v(-1.28, 8.36) * mm, "end": v(-1.27, 8.37) * mm});
            skLineSegment(sketch, "E99.10.70", {"start": v(-1.3, 8.32) * mm, "end": v(-1.3, 8.33) * mm});
            skLineSegment(sketch, "E99.10.71", {"start": v(-1.29, 8.34) * mm, "end": v(-1.28, 8.36) * mm});
            skLineSegment(sketch, "E99.10.72", {"start": v(-1.3, 8.33) * mm, "end": v(-1.29, 8.34) * mm});
            skLineSegment(sketch, "E99.10.73", {"start": v(-1.33, 8.3) * mm, "end": v(-1.32, 8.3) * mm});
            skLineSegment(sketch, "E99.10.74", {"start": v(-1.65, 8.28) * mm, "end": v(-1.66, 8.29) * mm});
            skLineSegment(sketch, "E99.10.75", {"start": v(-1.32, 8.3) * mm, "end": v(-1.3, 8.32) * mm});
            skLineSegment(sketch, "E99.10.76", {"start": v(-1.45, 8.25) * mm, "end": v(-1.45, 8.25) * mm});
            skLineSegment(sketch, "E99.10.77", {"start": v(-1.4, 8.26) * mm, "end": v(-1.38, 8.27) * mm});
            skLineSegment(sketch, "E99.10.78", {"start": v(-1.42, 8.25) * mm, "end": v(-1.4, 8.26) * mm});
            skLineSegment(sketch, "E99.10.79", {"start": v(-1.48, 8.24) * mm, "end": v(-1.51, 8.24) * mm});
            skLineSegment(sketch, "E99.10.80", {"start": v(-1.59, 8.25) * mm, "end": v(-1.6, 8.26) * mm});
            skLineSegment(sketch, "E99.10.81", {"start": v(-1.62, 8.26) * mm, "end": v(-1.63, 8.27) * mm});
            skLineSegment(sketch, "E99.10.82", {"start": v(-1.34, 8.28) * mm, "end": v(-1.33, 8.3) * mm});
            skLineSegment(sketch, "E99.10.83", {"start": v(-1.53, 8.24) * mm, "end": v(-1.55, 8.24) * mm});
            skLineSegment(sketch, "E99.10.84", {"start": v(-1.63, 8.27) * mm, "end": v(-1.65, 8.28) * mm});
            skLineSegment(sketch, "E99.10.85", {"start": v(-1.38, 8.27) * mm, "end": v(-1.36, 8.28) * mm});
            skLineSegment(sketch, "E99.10.86", {"start": v(-1.6, 8.26) * mm, "end": v(-1.62, 8.26) * mm});
            skLineSegment(sketch, "E99.10.87", {"start": v(-1.51, 8.24) * mm, "end": v(-1.53, 8.24) * mm});
            skLineSegment(sketch, "E99.10.88", {"start": v(-1.57, 8.24) * mm, "end": v(-1.59, 8.25) * mm});
            skLineSegment(sketch, "E99.10.89", {"start": v(-1.44, 8.25) * mm, "end": v(-1.44, 8.25) * mm});
            skLineSegment(sketch, "E99.10.90", {"start": v(-1.43, 8.25) * mm, "end": v(-1.42, 8.25) * mm});
            skLineSegment(sketch, "E99.10.91", {"start": v(-1.36, 8.28) * mm, "end": v(-1.34, 8.28) * mm});
            skLineSegment(sketch, "E99.10.92", {"start": v(-1.55, 8.24) * mm, "end": v(-1.57, 8.24) * mm});
            skLineSegment(sketch, "E99.10.93", {"start": v(-1.48, 8.24) * mm, "end": v(-1.48, 8.24) * mm});
            skLineSegment(sketch, "E99.10.94", {"start": v(-1.47, 8.24) * mm, "end": v(-1.48, 8.24) * mm});
            skLineSegment(sketch, "E99.10.95", {"start": v(-1.47, 8.25) * mm, "end": v(-1.47, 8.24) * mm});
            skLineSegment(sketch, "E99.10.96", {"start": v(-1.46, 8.25) * mm, "end": v(-1.47, 8.25) * mm});
            skLineSegment(sketch, "E99.10.97", {"start": v(-1.45, 8.25) * mm, "end": v(-1.46, 8.25) * mm});
            skLineSegment(sketch, "E99.10.98", {"start": v(-1.44, 8.25) * mm, "end": v(-1.43, 8.25) * mm});
            skLineSegment(sketch, "E99.10.99", {"start": v(-1.45, 8.25) * mm, "end": v(-1.44, 8.25) * mm});
            skLineSegment(sketch, "E99.11.0", {"start": v(-2.67, 8.93) * mm, "end": v(-2.67, 8.98) * mm});
            skLineSegment(sketch, "E99.11.1", {"start": v(-3.7, 8.56) * mm, "end": v(-3.73, 8.6) * mm});
            skLineSegment(sketch, "E99.11.2", {"start": v(-2.5, 9.17) * mm, "end": v(-2.46, 9.18) * mm});
            skLineSegment(sketch, "E99.11.3", {"start": v(-2.53, 9.16) * mm, "end": v(-2.5, 9.17) * mm});
            skLineSegment(sketch, "E99.11.4", {"start": v(-2.7, 8.74) * mm, "end": v(-2.7, 8.79) * mm});
            skLineSegment(sketch, "E99.11.5", {"start": v(-3.39, 8.25) * mm, "end": v(-3.42, 8.29) * mm});
            skLineSegment(sketch, "E99.11.6", {"start": v(-2.7, 8.64) * mm, "end": v(-2.7, 8.69) * mm});
            skLineSegment(sketch, "E99.11.7", {"start": v(-2.7, 8.31) * mm, "end": v(-2.7, 8.36) * mm});
            skLineSegment(sketch, "E99.11.8", {"start": v(-2.7, 8.69) * mm, "end": v(-2.7, 8.74) * mm});
            skLineSegment(sketch, "E99.11.9", {"start": v(-2.7, 8.4) * mm, "end": v(-2.7, 8.45) * mm});
            skLineSegment(sketch, "E99.11.10", {"start": v(-3.45, 8.32) * mm, "end": v(-3.48, 8.36) * mm});
            skLineSegment(sketch, "E99.11.11", {"start": v(-3.3, 8.15) * mm, "end": v(-3.33, 8.18) * mm});
            skLineSegment(sketch, "E99.11.12", {"start": v(-3.52, 8.4) * mm, "end": v(-3.55, 8.43) * mm});
            skLineSegment(sketch, "E99.11.13", {"start": v(-2.7, 8.55) * mm, "end": v(-2.7, 8.6) * mm});
            skLineSegment(sketch, "E99.11.14", {"start": v(-2.67, 8.98) * mm, "end": v(-2.66, 9.03) * mm});
            skLineSegment(sketch, "E99.11.15", {"start": v(-2.7, 8.5) * mm, "end": v(-2.7, 8.55) * mm});
            skLineSegment(sketch, "E99.11.16", {"start": v(-2.68, 8.88) * mm, "end": v(-2.67, 8.93) * mm});
            skLineSegment(sketch, "E99.11.17", {"start": v(-2.7, 8.6) * mm, "end": v(-2.7, 8.64) * mm});
            skLineSegment(sketch, "E99.11.18", {"start": v(-3.66, 8.53) * mm, "end": v(-3.7, 8.56) * mm});
            skLineSegment(sketch, "E99.11.19", {"start": v(-2.66, 9.03) * mm, "end": v(-2.65, 9.08) * mm});
            skLineSegment(sketch, "E99.11.20", {"start": v(-2.57, 9.15) * mm, "end": v(-2.53, 9.16) * mm});
            skLineSegment(sketch, "E99.11.21", {"start": v(-3.27, 8.1) * mm, "end": v(-3.3, 8.15) * mm});
            skLineSegment(sketch, "E99.11.22", {"start": v(-3.36, 8.22) * mm, "end": v(-3.39, 8.25) * mm});
            skLineSegment(sketch, "E99.11.23", {"start": v(-3.59, 8.46) * mm, "end": v(-3.62, 8.5) * mm});
            skLineSegment(sketch, "E99.11.24", {"start": v(-2.7, 8.79) * mm, "end": v(-2.69, 8.83) * mm});
            skLineSegment(sketch, "E99.11.25", {"start": v(-2.7, 8.36) * mm, "end": v(-2.7, 8.4) * mm});
            skLineSegment(sketch, "E99.11.26", {"start": v(-2.65, 9.08) * mm, "end": v(-2.64, 9.13) * mm});
            skLineSegment(sketch, "E99.11.27", {"start": v(-2.6, 9.14) * mm, "end": v(-2.57, 9.15) * mm});
            skLineSegment(sketch, "E99.11.28", {"start": v(-2.69, 8.83) * mm, "end": v(-2.68, 8.88) * mm});
            skLineSegment(sketch, "E99.11.29", {"start": v(-3.42, 8.29) * mm, "end": v(-3.45, 8.32) * mm});
            skLineSegment(sketch, "E99.11.30", {"start": v(-3.62, 8.5) * mm, "end": v(-3.66, 8.53) * mm});
            skLineSegment(sketch, "E99.11.31", {"start": v(-2.7, 8.45) * mm, "end": v(-2.7, 8.5) * mm});
            skLineSegment(sketch, "E99.11.32", {"start": v(-3.55, 8.43) * mm, "end": v(-3.59, 8.46) * mm});
            skLineSegment(sketch, "E99.11.33", {"start": v(-3.33, 8.18) * mm, "end": v(-3.36, 8.22) * mm});
            skLineSegment(sketch, "E99.11.34", {"start": v(-3.73, 8.6) * mm, "end": v(-3.77, 8.62) * mm});
            skLineSegment(sketch, "E99.11.35", {"start": v(-3.98, 8.63) * mm, "end": v(-4.01, 8.6) * mm});
            skLineSegment(sketch, "E99.11.36", {"start": v(-3.48, 8.36) * mm, "end": v(-3.52, 8.4) * mm});
            skLineSegment(sketch, "E99.11.37", {"start": v(-3.95, 8.64) * mm, "end": v(-3.98, 8.63) * mm});
            skLineSegment(sketch, "E99.11.38", {"start": v(-3.77, 8.62) * mm, "end": v(-3.8, 8.66) * mm});
            skLineSegment(sketch, "E99.11.39", {"start": v(-2.64, 9.13) * mm, "end": v(-2.6, 9.14) * mm});
            skLineSegment(sketch, "E99.11.40", {"start": v(-3.8, 8.66) * mm, "end": v(-3.84, 8.69) * mm});
            skLineSegment(sketch, "E99.11.41", {"start": v(-3.91, 8.66) * mm, "end": v(-3.95, 8.64) * mm});
            skLineSegment(sketch, "E99.11.42", {"start": v(-3.88, 8.67) * mm, "end": v(-3.91, 8.66) * mm});
            skLineSegment(sketch, "E99.11.43", {"start": v(-3.25, 8.07) * mm, "end": v(-3.27, 8.1) * mm});
            skLineSegment(sketch, "E99.11.44", {"start": v(-3.84, 8.69) * mm, "end": v(-3.88, 8.67) * mm});
            skLineSegment(sketch, "E99.11.45", {"start": v(-2.7, 8.27) * mm, "end": v(-2.7, 8.31) * mm});
            skLineSegment(sketch, "E99.11.46", {"start": v(-3.11, 7.9) * mm, "end": v(-3.13, 7.91) * mm});
            skLineSegment(sketch, "E99.11.47", {"start": v(-3.2, 8) * mm, "end": v(-3.22, 8.03) * mm});
            skLineSegment(sketch, "E99.11.48", {"start": v(-3.22, 8.03) * mm, "end": v(-3.25, 8.07) * mm});
            skLineSegment(sketch, "E99.11.49", {"start": v(-2.69, 8.09) * mm, "end": v(-2.69, 8.1) * mm});
            skLineSegment(sketch, "E99.11.50", {"start": v(-3.14, 7.92) * mm, "end": v(-3.15, 7.94) * mm});
            skLineSegment(sketch, "E99.11.51", {"start": v(-2.7, 8.04) * mm, "end": v(-2.7, 8.05) * mm});
            skLineSegment(sketch, "E99.11.52", {"start": v(-2.7, 8.22) * mm, "end": v(-2.7, 8.27) * mm});
            skLineSegment(sketch, "E99.11.53", {"start": v(-2.69, 8.12) * mm, "end": v(-2.69, 8.14) * mm});
            skLineSegment(sketch, "E99.11.54", {"start": v(-2.7, 8.16) * mm, "end": v(-2.7, 8.18) * mm});
            skLineSegment(sketch, "E99.11.55", {"start": v(-3.15, 7.94) * mm, "end": v(-3.16, 7.95) * mm});
            skLineSegment(sketch, "E99.11.56", {"start": v(-3.18, 7.98) * mm, "end": v(-3.2, 8) * mm});
            skLineSegment(sketch, "E99.11.57", {"start": v(-2.69, 8.1) * mm, "end": v(-2.69, 8.12) * mm});
            skLineSegment(sketch, "E99.11.58", {"start": v(-3.1, 7.9) * mm, "end": v(-3.11, 7.9) * mm});
            skLineSegment(sketch, "E99.11.59", {"start": v(-2.7, 8.18) * mm, "end": v(-2.7, 8.22) * mm});
            skLineSegment(sketch, "E99.11.60", {"start": v(-3.17, 7.97) * mm, "end": v(-3.18, 7.98) * mm});
            skLineSegment(sketch, "E99.11.61", {"start": v(-3.13, 7.91) * mm, "end": v(-3.14, 7.92) * mm});
            skLineSegment(sketch, "E99.11.62", {"start": v(-2.69, 8.14) * mm, "end": v(-2.7, 8.16) * mm});
            skLineSegment(sketch, "E99.11.63", {"start": v(-3.16, 7.95) * mm, "end": v(-3.17, 7.97) * mm});
            skLineSegment(sketch, "E99.11.64", {"start": v(-3.09, 7.88) * mm, "end": v(-3.1, 7.9) * mm});
            skLineSegment(sketch, "E99.11.65", {"start": v(-2.7, 8.02) * mm, "end": v(-2.7, 8.04) * mm});
            skLineSegment(sketch, "E99.11.66", {"start": v(-2.7, 8.05) * mm, "end": v(-2.7, 8.07) * mm});
            skLineSegment(sketch, "E99.11.67", {"start": v(-3.07, 7.87) * mm, "end": v(-3.09, 7.88) * mm});
            skLineSegment(sketch, "E99.11.68", {"start": v(-2.7, 8.07) * mm, "end": v(-2.69, 8.09) * mm});
            skLineSegment(sketch, "E99.11.69", {"start": v(-2.7, 8) * mm, "end": v(-2.7, 8.02) * mm});
            skLineSegment(sketch, "E99.11.70", {"start": v(-2.73, 7.96) * mm, "end": v(-2.72, 7.98) * mm});
            skLineSegment(sketch, "E99.11.71", {"start": v(-2.71, 8) * mm, "end": v(-2.7, 8) * mm});
            skLineSegment(sketch, "E99.11.72", {"start": v(-2.72, 7.98) * mm, "end": v(-2.71, 8) * mm});
            skLineSegment(sketch, "E99.11.73", {"start": v(-2.75, 7.94) * mm, "end": v(-2.74, 7.95) * mm});
            skLineSegment(sketch, "E99.11.74", {"start": v(-3.06, 7.87) * mm, "end": v(-3.07, 7.87) * mm});
            skLineSegment(sketch, "E99.11.75", {"start": v(-2.74, 7.95) * mm, "end": v(-2.73, 7.96) * mm});
            skLineSegment(sketch, "E99.11.76", {"start": v(-2.86, 7.87) * mm, "end": v(-2.86, 7.87) * mm});
            skLineSegment(sketch, "E99.11.77", {"start": v(-2.81, 7.9) * mm, "end": v(-2.8, 7.9) * mm});
            skLineSegment(sketch, "E99.11.78", {"start": v(-2.84, 7.88) * mm, "end": v(-2.81, 7.9) * mm});
            skLineSegment(sketch, "E99.11.79", {"start": v(-2.9, 7.86) * mm, "end": v(-2.92, 7.85) * mm});
            skLineSegment(sketch, "E99.11.80", {"start": v(-3, 7.85) * mm, "end": v(-3.01, 7.85) * mm});
            skLineSegment(sketch, "E99.11.81", {"start": v(-3.03, 7.86) * mm, "end": v(-3.04, 7.86) * mm});
            skLineSegment(sketch, "E99.11.82", {"start": v(-2.76, 7.93) * mm, "end": v(-2.75, 7.94) * mm});
            skLineSegment(sketch, "E99.11.83", {"start": v(-2.94, 7.85) * mm, "end": v(-2.96, 7.85) * mm});
            skLineSegment(sketch, "E99.11.84", {"start": v(-3.04, 7.86) * mm, "end": v(-3.06, 7.87) * mm});
            skLineSegment(sketch, "E99.11.85", {"start": v(-2.8, 7.9) * mm, "end": v(-2.78, 7.91) * mm});
            skLineSegment(sketch, "E99.11.86", {"start": v(-3.01, 7.85) * mm, "end": v(-3.03, 7.86) * mm});
            skLineSegment(sketch, "E99.11.87", {"start": v(-2.92, 7.85) * mm, "end": v(-2.94, 7.85) * mm});
            skLineSegment(sketch, "E99.11.88", {"start": v(-2.98, 7.85) * mm, "end": v(-3, 7.85) * mm});
            skLineSegment(sketch, "E99.11.89", {"start": v(-2.85, 7.87) * mm, "end": v(-2.85, 7.88) * mm});
            skLineSegment(sketch, "E99.11.90", {"start": v(-2.84, 7.88) * mm, "end": v(-2.84, 7.88) * mm});
            skLineSegment(sketch, "E99.11.91", {"start": v(-2.78, 7.91) * mm, "end": v(-2.76, 7.93) * mm});
            skLineSegment(sketch, "E99.11.92", {"start": v(-2.96, 7.85) * mm, "end": v(-2.98, 7.85) * mm});
            skLineSegment(sketch, "E99.11.93", {"start": v(-2.89, 7.86) * mm, "end": v(-2.9, 7.86) * mm});
            skLineSegment(sketch, "E99.11.94", {"start": v(-2.88, 7.86) * mm, "end": v(-2.89, 7.86) * mm});
            skLineSegment(sketch, "E99.11.95", {"start": v(-2.88, 7.87) * mm, "end": v(-2.88, 7.86) * mm});
            skLineSegment(sketch, "E99.11.96", {"start": v(-2.87, 7.87) * mm, "end": v(-2.88, 7.87) * mm});
            skLineSegment(sketch, "E99.11.97", {"start": v(-2.86, 7.87) * mm, "end": v(-2.87, 7.87) * mm});
            skLineSegment(sketch, "E99.11.98", {"start": v(-2.85, 7.88) * mm, "end": v(-2.84, 7.88) * mm});
            skLineSegment(sketch, "E99.11.99", {"start": v(-2.86, 7.87) * mm, "end": v(-2.85, 7.87) * mm});
            skLineSegment(sketch, "E99.12.0", {"start": v(-4.18, 8.33) * mm, "end": v(-4.18, 8.38) * mm});
            skLineSegment(sketch, "E99.12.1", {"start": v(-5.12, 7.79) * mm, "end": v(-5.16, 7.81) * mm});
            skLineSegment(sketch, "E99.12.2", {"start": v(-4.05, 8.6) * mm, "end": v(-4.01, 8.6) * mm});
            skLineSegment(sketch, "E99.12.3", {"start": v(-4.08, 8.58) * mm, "end": v(-4.05, 8.6) * mm});
            skLineSegment(sketch, "E99.12.4", {"start": v(-4.17, 8.14) * mm, "end": v(-4.18, 8.18) * mm});
            skLineSegment(sketch, "E99.12.5", {"start": v(-4.77, 7.54) * mm, "end": v(-4.8, 7.57) * mm});
            skLineSegment(sketch, "E99.12.6", {"start": v(-4.16, 8.04) * mm, "end": v(-4.17, 8.09) * mm});
            skLineSegment(sketch, "E99.12.7", {"start": v(-4.1, 7.72) * mm, "end": v(-4.12, 7.76) * mm});
            skLineSegment(sketch, "E99.12.8", {"start": v(-4.17, 8.09) * mm, "end": v(-4.17, 8.14) * mm});
            skLineSegment(sketch, "E99.12.9", {"start": v(-4.13, 7.8) * mm, "end": v(-4.14, 7.85) * mm});
            skLineSegment(sketch, "E99.12.10", {"start": v(-4.84, 7.6) * mm, "end": v(-4.88, 7.63) * mm});
            skLineSegment(sketch, "E99.12.11", {"start": v(-4.66, 7.45) * mm, "end": v(-4.7, 7.48) * mm});
            skLineSegment(sketch, "E99.12.12", {"start": v(-4.92, 7.65) * mm, "end": v(-4.96, 7.68) * mm});
            skLineSegment(sketch, "E99.12.13", {"start": v(-4.15, 7.95) * mm, "end": v(-4.16, 8) * mm});
            skLineSegment(sketch, "E99.12.14", {"start": v(-4.18, 8.38) * mm, "end": v(-4.19, 8.43) * mm});
            skLineSegment(sketch, "E99.12.15", {"start": v(-4.14, 7.9) * mm, "end": v(-4.15, 7.95) * mm});
            skLineSegment(sketch, "E99.12.16", {"start": v(-4.18, 8.28) * mm, "end": v(-4.18, 8.33) * mm});
            skLineSegment(sketch, "E99.12.17", {"start": v(-4.16, 8) * mm, "end": v(-4.16, 8.04) * mm});
            skLineSegment(sketch, "E99.12.18", {"start": v(-5.08, 7.76) * mm, "end": v(-5.12, 7.79) * mm});
            skLineSegment(sketch, "E99.12.19", {"start": v(-4.19, 8.43) * mm, "end": v(-4.19, 8.48) * mm});
            skLineSegment(sketch, "E99.12.20", {"start": v(-4.12, 8.56) * mm, "end": v(-4.08, 8.58) * mm});
            skLineSegment(sketch, "E99.12.21", {"start": v(-4.63, 7.42) * mm, "end": v(-4.66, 7.45) * mm});
            skLineSegment(sketch, "E99.12.22", {"start": v(-4.73, 7.5) * mm, "end": v(-4.77, 7.54) * mm});
            skLineSegment(sketch, "E99.12.23", {"start": v(-5, 7.7) * mm, "end": v(-5.04, 7.74) * mm});
            skLineSegment(sketch, "E99.12.24", {"start": v(-4.18, 8.18) * mm, "end": v(-4.18, 8.23) * mm});
            skLineSegment(sketch, "E99.12.25", {"start": v(-4.12, 7.76) * mm, "end": v(-4.13, 7.8) * mm});
            skLineSegment(sketch, "E99.12.26", {"start": v(-4.19, 8.48) * mm, "end": v(-4.18, 8.53) * mm});
            skLineSegment(sketch, "E99.12.27", {"start": v(-4.15, 8.55) * mm, "end": v(-4.12, 8.56) * mm});
            skLineSegment(sketch, "E99.12.28", {"start": v(-4.18, 8.23) * mm, "end": v(-4.18, 8.28) * mm});
            skLineSegment(sketch, "E99.12.29", {"start": v(-4.8, 7.57) * mm, "end": v(-4.84, 7.6) * mm});
            skLineSegment(sketch, "E99.12.30", {"start": v(-5.04, 7.74) * mm, "end": v(-5.08, 7.76) * mm});
            skLineSegment(sketch, "E99.12.31", {"start": v(-4.14, 7.85) * mm, "end": v(-4.14, 7.9) * mm});
            skLineSegment(sketch, "E99.12.32", {"start": v(-4.96, 7.68) * mm, "end": v(-5, 7.7) * mm});
            skLineSegment(sketch, "E99.12.33", {"start": v(-4.7, 7.48) * mm, "end": v(-4.73, 7.5) * mm});
            skLineSegment(sketch, "E99.12.34", {"start": v(-5.16, 7.81) * mm, "end": v(-5.2, 7.84) * mm});
            skLineSegment(sketch, "E99.12.35", {"start": v(-5.42, 7.8) * mm, "end": v(-5.45, 7.78) * mm});
            skLineSegment(sketch, "E99.12.36", {"start": v(-4.88, 7.63) * mm, "end": v(-4.92, 7.65) * mm});
            skLineSegment(sketch, "E99.12.37", {"start": v(-5.39, 7.82) * mm, "end": v(-5.42, 7.8) * mm});
            skLineSegment(sketch, "E99.12.38", {"start": v(-5.2, 7.84) * mm, "end": v(-5.25, 7.86) * mm});
            skLineSegment(sketch, "E99.12.39", {"start": v(-4.18, 8.53) * mm, "end": v(-4.15, 8.55) * mm});
            skLineSegment(sketch, "E99.12.40", {"start": v(-5.25, 7.86) * mm, "end": v(-5.3, 7.89) * mm});
            skLineSegment(sketch, "E99.12.41", {"start": v(-5.36, 7.85) * mm, "end": v(-5.39, 7.82) * mm});
            skLineSegment(sketch, "E99.12.42", {"start": v(-5.32, 7.87) * mm, "end": v(-5.36, 7.85) * mm});
            skLineSegment(sketch, "E99.12.43", {"start": v(-4.6, 7.39) * mm, "end": v(-4.63, 7.42) * mm});
            skLineSegment(sketch, "E99.12.44", {"start": v(-5.3, 7.89) * mm, "end": v(-5.32, 7.87) * mm});
            skLineSegment(sketch, "E99.12.45", {"start": v(-4.1, 7.67) * mm, "end": v(-4.1, 7.72) * mm});
            skLineSegment(sketch, "E99.12.46", {"start": v(-4.44, 7.24) * mm, "end": v(-4.45, 7.25) * mm});
            skLineSegment(sketch, "E99.12.47", {"start": v(-4.53, 7.32) * mm, "end": v(-4.57, 7.35) * mm});
            skLineSegment(sketch, "E99.12.48", {"start": v(-4.57, 7.35) * mm, "end": v(-4.6, 7.39) * mm});
            skLineSegment(sketch, "E99.12.49", {"start": v(-4.05, 7.5) * mm, "end": v(-4.06, 7.52) * mm});
            skLineSegment(sketch, "E99.12.50", {"start": v(-4.47, 7.26) * mm, "end": v(-4.48, 7.27) * mm});
            skLineSegment(sketch, "E99.12.51", {"start": v(-4.05, 7.45) * mm, "end": v(-4.05, 7.46) * mm});
            skLineSegment(sketch, "E99.12.52", {"start": v(-4.08, 7.63) * mm, "end": v(-4.1, 7.67) * mm});
            skLineSegment(sketch, "E99.12.53", {"start": v(-4.06, 7.53) * mm, "end": v(-4.06, 7.55) * mm});
            skLineSegment(sketch, "E99.12.54", {"start": v(-4.07, 7.57) * mm, "end": v(-4.07, 7.59) * mm});
            skLineSegment(sketch, "E99.12.55", {"start": v(-4.48, 7.27) * mm, "end": v(-4.5, 7.28) * mm});
            skLineSegment(sketch, "E99.12.56", {"start": v(-4.52, 7.3) * mm, "end": v(-4.53, 7.32) * mm});
            skLineSegment(sketch, "E99.12.57", {"start": v(-4.06, 7.52) * mm, "end": v(-4.06, 7.53) * mm});
            skLineSegment(sketch, "E99.12.58", {"start": v(-4.42, 7.23) * mm, "end": v(-4.44, 7.24) * mm});
            skLineSegment(sketch, "E99.12.59", {"start": v(-4.07, 7.59) * mm, "end": v(-4.08, 7.63) * mm});
            skLineSegment(sketch, "E99.12.60", {"start": v(-4.5, 7.3) * mm, "end": v(-4.52, 7.3) * mm});
            skLineSegment(sketch, "E99.12.61", {"start": v(-4.45, 7.25) * mm, "end": v(-4.47, 7.26) * mm});
            skLineSegment(sketch, "E99.12.62", {"start": v(-4.06, 7.55) * mm, "end": v(-4.07, 7.57) * mm});
            skLineSegment(sketch, "E99.12.63", {"start": v(-4.5, 7.28) * mm, "end": v(-4.5, 7.3) * mm});
            skLineSegment(sketch, "E99.12.64", {"start": v(-4.4, 7.23) * mm, "end": v(-4.42, 7.23) * mm});
            skLineSegment(sketch, "E99.12.65", {"start": v(-4.05, 7.43) * mm, "end": v(-4.05, 7.45) * mm});
            skLineSegment(sketch, "E99.12.66", {"start": v(-4.05, 7.46) * mm, "end": v(-4.05, 7.48) * mm});
            skLineSegment(sketch, "E99.12.67", {"start": v(-4.4, 7.22) * mm, "end": v(-4.4, 7.23) * mm});
            skLineSegment(sketch, "E99.12.68", {"start": v(-4.05, 7.48) * mm, "end": v(-4.05, 7.5) * mm});
            skLineSegment(sketch, "E99.12.69", {"start": v(-4.06, 7.42) * mm, "end": v(-4.05, 7.43) * mm});
            skLineSegment(sketch, "E99.12.70", {"start": v(-4.07, 7.37) * mm, "end": v(-4.07, 7.38) * mm});
            skLineSegment(sketch, "E99.12.71", {"start": v(-4.06, 7.4) * mm, "end": v(-4.06, 7.42) * mm});
            skLineSegment(sketch, "E99.12.72", {"start": v(-4.07, 7.38) * mm, "end": v(-4.06, 7.4) * mm});
            skLineSegment(sketch, "E99.12.73", {"start": v(-4.09, 7.34) * mm, "end": v(-4.08, 7.35) * mm});
            skLineSegment(sketch, "E99.12.74", {"start": v(-4.38, 7.22) * mm, "end": v(-4.4, 7.22) * mm});
            skLineSegment(sketch, "E99.12.75", {"start": v(-4.08, 7.35) * mm, "end": v(-4.07, 7.37) * mm});
            skLineSegment(sketch, "E99.12.76", {"start": v(-4.19, 7.25) * mm, "end": v(-4.18, 7.26) * mm});
            skLineSegment(sketch, "E99.12.77", {"start": v(-4.14, 7.28) * mm, "end": v(-4.12, 7.3) * mm});
            skLineSegment(sketch, "E99.12.78", {"start": v(-4.16, 7.27) * mm, "end": v(-4.14, 7.28) * mm});
            skLineSegment(sketch, "E99.12.79", {"start": v(-4.21, 7.24) * mm, "end": v(-4.24, 7.23) * mm});
            skLineSegment(sketch, "E99.12.80", {"start": v(-4.31, 7.2) * mm, "end": v(-4.33, 7.2) * mm});
            skLineSegment(sketch, "E99.12.81", {"start": v(-4.35, 7.21) * mm, "end": v(-4.36, 7.21) * mm});
            skLineSegment(sketch, "E99.12.82", {"start": v(-4.1, 7.32) * mm, "end": v(-4.09, 7.34) * mm});
            skLineSegment(sketch, "E99.12.83", {"start": v(-4.26, 7.22) * mm, "end": v(-4.28, 7.21) * mm});
            skLineSegment(sketch, "E99.12.84", {"start": v(-4.36, 7.21) * mm, "end": v(-4.38, 7.22) * mm});
            skLineSegment(sketch, "E99.12.85", {"start": v(-4.12, 7.3) * mm, "end": v(-4.1, 7.31) * mm});
            skLineSegment(sketch, "E99.12.86", {"start": v(-4.33, 7.2) * mm, "end": v(-4.35, 7.21) * mm});
            skLineSegment(sketch, "E99.12.87", {"start": v(-4.24, 7.23) * mm, "end": v(-4.26, 7.22) * mm});
            skLineSegment(sketch, "E99.12.88", {"start": v(-4.3, 7.21) * mm, "end": v(-4.31, 7.2) * mm});
            skLineSegment(sketch, "E99.12.89", {"start": v(-4.18, 7.26) * mm, "end": v(-4.17, 7.26) * mm});
            skLineSegment(sketch, "E99.12.90", {"start": v(-4.17, 7.26) * mm, "end": v(-4.16, 7.27) * mm});
            skLineSegment(sketch, "E99.12.91", {"start": v(-4.1, 7.31) * mm, "end": v(-4.1, 7.32) * mm});
            skLineSegment(sketch, "E99.12.92", {"start": v(-4.28, 7.21) * mm, "end": v(-4.3, 7.21) * mm});
            skLineSegment(sketch, "E99.12.93", {"start": v(-4.2, 7.24) * mm, "end": v(-4.21, 7.24) * mm});
            skLineSegment(sketch, "E99.12.94", {"start": v(-4.2, 7.24) * mm, "end": v(-4.2, 7.24) * mm});
            skLineSegment(sketch, "E99.12.95", {"start": v(-4.2, 7.25) * mm, "end": v(-4.2, 7.24) * mm});
            skLineSegment(sketch, "E99.12.96", {"start": v(-4.2, 7.25) * mm, "end": v(-4.2, 7.25) * mm});
            skLineSegment(sketch, "E99.12.97", {"start": v(-4.19, 7.25) * mm, "end": v(-4.2, 7.25) * mm});
            skLineSegment(sketch, "E99.12.98", {"start": v(-4.17, 7.26) * mm, "end": v(-4.17, 7.26) * mm});
            skLineSegment(sketch, "E99.12.99", {"start": v(-4.18, 7.26) * mm, "end": v(-4.18, 7.26) * mm});
            skLineSegment(sketch, "E99.13.0", {"start": v(-5.57, 7.48) * mm, "end": v(-5.58, 7.53) * mm});
            skLineSegment(sketch, "E99.13.1", {"start": v(-6.4, 6.78) * mm, "end": v(-6.44, 6.8) * mm});
            skLineSegment(sketch, "E99.13.2", {"start": v(-5.48, 7.76) * mm, "end": v(-5.45, 7.78) * mm});
            skLineSegment(sketch, "E99.13.3", {"start": v(-5.51, 7.74) * mm, "end": v(-5.48, 7.76) * mm});
            skLineSegment(sketch, "E99.13.4", {"start": v(-5.52, 7.29) * mm, "end": v(-5.53, 7.34) * mm});
            skLineSegment(sketch, "E99.13.5", {"start": v(-6, 6.6) * mm, "end": v(-6.05, 6.62) * mm});
            skLineSegment(sketch, "E99.13.6", {"start": v(-5.5, 7.2) * mm, "end": v(-5.5, 7.24) * mm});
            skLineSegment(sketch, "E99.13.7", {"start": v(-5.39, 6.89) * mm, "end": v(-5.4, 6.93) * mm});
            skLineSegment(sketch, "E99.13.8", {"start": v(-5.5, 7.24) * mm, "end": v(-5.52, 7.29) * mm});
            skLineSegment(sketch, "E99.13.9", {"start": v(-5.42, 6.97) * mm, "end": v(-5.44, 7.02) * mm});
            skLineSegment(sketch, "E99.13.10", {"start": v(-6.1, 6.64) * mm, "end": v(-6.13, 6.66) * mm});
            skLineSegment(sketch, "E99.13.11", {"start": v(-5.89, 6.53) * mm, "end": v(-5.93, 6.55) * mm});
            skLineSegment(sketch, "E99.13.12", {"start": v(-6.18, 6.68) * mm, "end": v(-6.22, 6.7) * mm});
            skLineSegment(sketch, "E99.13.13", {"start": v(-5.47, 7.1) * mm, "end": v(-5.48, 7.15) * mm});
            skLineSegment(sketch, "E99.13.14", {"start": v(-5.58, 7.53) * mm, "end": v(-5.59, 7.57) * mm});
            skLineSegment(sketch, "E99.13.15", {"start": v(-5.45, 7.06) * mm, "end": v(-5.47, 7.1) * mm});
            skLineSegment(sketch, "E99.13.16", {"start": v(-5.56, 7.43) * mm, "end": v(-5.57, 7.48) * mm});
            skLineSegment(sketch, "E99.13.17", {"start": v(-5.48, 7.15) * mm, "end": v(-5.5, 7.2) * mm});
            skLineSegment(sketch, "E99.13.18", {"start": v(-6.35, 6.76) * mm, "end": v(-6.4, 6.78) * mm});
            skLineSegment(sketch, "E99.13.19", {"start": v(-5.59, 7.57) * mm, "end": v(-5.6, 7.62) * mm});
            skLineSegment(sketch, "E99.13.20", {"start": v(-5.54, 7.72) * mm, "end": v(-5.51, 7.74) * mm});
            skLineSegment(sketch, "E99.13.21", {"start": v(-5.85, 6.5) * mm, "end": v(-5.89, 6.53) * mm});
            skLineSegment(sketch, "E99.13.22", {"start": v(-5.97, 6.57) * mm, "end": v(-6, 6.6) * mm});
            skLineSegment(sketch, "E99.13.23", {"start": v(-6.26, 6.72) * mm, "end": v(-6.3, 6.74) * mm});
            skLineSegment(sketch, "E99.13.24", {"start": v(-5.53, 7.34) * mm, "end": v(-5.55, 7.38) * mm});
            skLineSegment(sketch, "E99.13.25", {"start": v(-5.4, 6.93) * mm, "end": v(-5.42, 6.97) * mm});
            skLineSegment(sketch, "E99.13.26", {"start": v(-5.6, 7.62) * mm, "end": v(-5.6, 7.67) * mm});
            skLineSegment(sketch, "E99.13.27", {"start": v(-5.57, 7.7) * mm, "end": v(-5.54, 7.72) * mm});
            skLineSegment(sketch, "E99.13.28", {"start": v(-5.55, 7.38) * mm, "end": v(-5.56, 7.43) * mm});
            skLineSegment(sketch, "E99.13.29", {"start": v(-6.05, 6.62) * mm, "end": v(-6.1, 6.64) * mm});
            skLineSegment(sketch, "E99.13.30", {"start": v(-6.3, 6.74) * mm, "end": v(-6.35, 6.76) * mm});
            skLineSegment(sketch, "E99.13.31", {"start": v(-5.44, 7.02) * mm, "end": v(-5.45, 7.06) * mm});
            skLineSegment(sketch, "E99.13.32", {"start": v(-6.22, 6.7) * mm, "end": v(-6.26, 6.72) * mm});
            skLineSegment(sketch, "E99.13.33", {"start": v(-5.93, 6.55) * mm, "end": v(-5.97, 6.57) * mm});
            skLineSegment(sketch, "E99.13.34", {"start": v(-6.44, 6.8) * mm, "end": v(-6.49, 6.82) * mm});
            skLineSegment(sketch, "E99.13.35", {"start": v(-6.7, 6.74) * mm, "end": v(-6.72, 6.72) * mm});
            skLineSegment(sketch, "E99.13.36", {"start": v(-6.13, 6.66) * mm, "end": v(-6.18, 6.68) * mm});
            skLineSegment(sketch, "E99.13.37", {"start": v(-6.66, 6.77) * mm, "end": v(-6.7, 6.74) * mm});
            skLineSegment(sketch, "E99.13.38", {"start": v(-6.49, 6.82) * mm, "end": v(-6.54, 6.83) * mm});
            skLineSegment(sketch, "E99.13.39", {"start": v(-5.6, 7.67) * mm, "end": v(-5.57, 7.7) * mm});
            skLineSegment(sketch, "E99.13.40", {"start": v(-6.54, 6.83) * mm, "end": v(-6.58, 6.85) * mm});
            skLineSegment(sketch, "E99.13.41", {"start": v(-6.64, 6.8) * mm, "end": v(-6.66, 6.77) * mm});
            skLineSegment(sketch, "E99.13.42", {"start": v(-6.61, 6.82) * mm, "end": v(-6.64, 6.8) * mm});
            skLineSegment(sketch, "E99.13.43", {"start": v(-5.81, 6.47) * mm, "end": v(-5.85, 6.5) * mm});
            skLineSegment(sketch, "E99.13.44", {"start": v(-6.58, 6.85) * mm, "end": v(-6.61, 6.82) * mm});
            skLineSegment(sketch, "E99.13.45", {"start": v(-5.37, 6.85) * mm, "end": v(-5.39, 6.89) * mm});
            skLineSegment(sketch, "E99.13.46", {"start": v(-5.63, 6.36) * mm, "end": v(-5.64, 6.37) * mm});
            skLineSegment(sketch, "E99.13.47", {"start": v(-5.74, 6.42) * mm, "end": v(-5.77, 6.45) * mm});
            skLineSegment(sketch, "E99.13.48", {"start": v(-5.77, 6.45) * mm, "end": v(-5.81, 6.47) * mm});
            skLineSegment(sketch, "E99.13.49", {"start": v(-5.3, 6.68) * mm, "end": v(-5.3, 6.7) * mm});
            skLineSegment(sketch, "E99.13.50", {"start": v(-5.66, 6.37) * mm, "end": v(-5.68, 6.38) * mm});
            skLineSegment(sketch, "E99.13.51", {"start": v(-5.28, 6.63) * mm, "end": v(-5.29, 6.65) * mm});
            skLineSegment(sketch, "E99.13.52", {"start": v(-5.35, 6.8) * mm, "end": v(-5.37, 6.85) * mm});
            skLineSegment(sketch, "E99.13.53", {"start": v(-5.3, 6.71) * mm, "end": v(-5.31, 6.73) * mm});
            skLineSegment(sketch, "E99.13.54", {"start": v(-5.32, 6.75) * mm, "end": v(-5.33, 6.76) * mm});
            skLineSegment(sketch, "E99.13.55", {"start": v(-5.68, 6.38) * mm, "end": v(-5.7, 6.39) * mm});
            skLineSegment(sketch, "E99.13.56", {"start": v(-5.72, 6.4) * mm, "end": v(-5.74, 6.42) * mm});
            skLineSegment(sketch, "E99.13.57", {"start": v(-5.3, 6.7) * mm, "end": v(-5.3, 6.71) * mm});
            skLineSegment(sketch, "E99.13.58", {"start": v(-5.61, 6.36) * mm, "end": v(-5.63, 6.36) * mm});
            skLineSegment(sketch, "E99.13.59", {"start": v(-5.33, 6.76) * mm, "end": v(-5.35, 6.8) * mm});
            skLineSegment(sketch, "E99.13.60", {"start": v(-5.7, 6.4) * mm, "end": v(-5.72, 6.4) * mm});
            skLineSegment(sketch, "E99.13.61", {"start": v(-5.64, 6.37) * mm, "end": v(-5.66, 6.37) * mm});
            skLineSegment(sketch, "E99.13.62", {"start": v(-5.31, 6.73) * mm, "end": v(-5.32, 6.75) * mm});
            skLineSegment(sketch, "E99.13.63", {"start": v(-5.7, 6.39) * mm, "end": v(-5.7, 6.4) * mm});
            skLineSegment(sketch, "E99.13.64", {"start": v(-5.6, 6.35) * mm, "end": v(-5.61, 6.36) * mm});
            skLineSegment(sketch, "E99.13.65", {"start": v(-5.28, 6.61) * mm, "end": v(-5.28, 6.63) * mm});
            skLineSegment(sketch, "E99.13.66", {"start": v(-5.29, 6.65) * mm, "end": v(-5.29, 6.66) * mm});
            skLineSegment(sketch, "E99.13.67", {"start": v(-5.58, 6.35) * mm, "end": v(-5.6, 6.35) * mm});
            skLineSegment(sketch, "E99.13.68", {"start": v(-5.29, 6.66) * mm, "end": v(-5.3, 6.68) * mm});
            skLineSegment(sketch, "E99.13.69", {"start": v(-5.28, 6.6) * mm, "end": v(-5.28, 6.61) * mm});
            skLineSegment(sketch, "E99.13.70", {"start": v(-5.29, 6.55) * mm, "end": v(-5.29, 6.57) * mm});
            skLineSegment(sketch, "E99.13.71", {"start": v(-5.28, 6.58) * mm, "end": v(-5.28, 6.6) * mm});
            skLineSegment(sketch, "E99.13.72", {"start": v(-5.29, 6.57) * mm, "end": v(-5.28, 6.58) * mm});
            skLineSegment(sketch, "E99.13.73", {"start": v(-5.3, 6.52) * mm, "end": v(-5.3, 6.53) * mm});
            skLineSegment(sketch, "E99.13.74", {"start": v(-5.56, 6.35) * mm, "end": v(-5.58, 6.35) * mm});
            skLineSegment(sketch, "E99.13.75", {"start": v(-5.3, 6.53) * mm, "end": v(-5.29, 6.55) * mm});
            skLineSegment(sketch, "E99.13.76", {"start": v(-5.38, 6.42) * mm, "end": v(-5.38, 6.42) * mm});
            skLineSegment(sketch, "E99.13.77", {"start": v(-5.34, 6.45) * mm, "end": v(-5.33, 6.47) * mm});
            skLineSegment(sketch, "E99.13.78", {"start": v(-5.36, 6.43) * mm, "end": v(-5.34, 6.45) * mm});
            skLineSegment(sketch, "E99.13.79", {"start": v(-5.4, 6.4) * mm, "end": v(-5.43, 6.38) * mm});
            skLineSegment(sketch, "E99.13.80", {"start": v(-5.5, 6.35) * mm, "end": v(-5.52, 6.35) * mm});
            skLineSegment(sketch, "E99.13.81", {"start": v(-5.53, 6.35) * mm, "end": v(-5.55, 6.35) * mm});
            skLineSegment(sketch, "E99.13.82", {"start": v(-5.3, 6.5) * mm, "end": v(-5.3, 6.52) * mm});
            skLineSegment(sketch, "E99.13.83", {"start": v(-5.45, 6.37) * mm, "end": v(-5.46, 6.36) * mm});
            skLineSegment(sketch, "E99.13.84", {"start": v(-5.55, 6.35) * mm, "end": v(-5.56, 6.35) * mm});
            skLineSegment(sketch, "E99.13.85", {"start": v(-5.33, 6.47) * mm, "end": v(-5.32, 6.49) * mm});
            skLineSegment(sketch, "E99.13.86", {"start": v(-5.52, 6.35) * mm, "end": v(-5.53, 6.35) * mm});
            skLineSegment(sketch, "E99.13.87", {"start": v(-5.43, 6.38) * mm, "end": v(-5.45, 6.37) * mm});
            skLineSegment(sketch, "E99.13.88", {"start": v(-5.48, 6.36) * mm, "end": v(-5.5, 6.35) * mm});
            skLineSegment(sketch, "E99.13.89", {"start": v(-5.37, 6.42) * mm, "end": v(-5.37, 6.43) * mm});
            skLineSegment(sketch, "E99.13.90", {"start": v(-5.36, 6.43) * mm, "end": v(-5.36, 6.43) * mm});
            skLineSegment(sketch, "E99.13.91", {"start": v(-5.32, 6.49) * mm, "end": v(-5.3, 6.5) * mm});
            skLineSegment(sketch, "E99.13.92", {"start": v(-5.46, 6.36) * mm, "end": v(-5.48, 6.36) * mm});
            skLineSegment(sketch, "E99.13.93", {"start": v(-5.4, 6.4) * mm, "end": v(-5.4, 6.4) * mm});
            skLineSegment(sketch, "E99.13.94", {"start": v(-5.4, 6.4) * mm, "end": v(-5.4, 6.4) * mm});
            skLineSegment(sketch, "E99.13.95", {"start": v(-5.4, 6.4) * mm, "end": v(-5.4, 6.4) * mm});
            skLineSegment(sketch, "E99.13.96", {"start": v(-5.39, 6.41) * mm, "end": v(-5.4, 6.4) * mm});
            skLineSegment(sketch, "E99.13.97", {"start": v(-5.38, 6.42) * mm, "end": v(-5.39, 6.41) * mm});
            skLineSegment(sketch, "E99.13.98", {"start": v(-5.37, 6.43) * mm, "end": v(-5.36, 6.43) * mm});
            skLineSegment(sketch, "E99.13.99", {"start": v(-5.38, 6.42) * mm, "end": v(-5.37, 6.42) * mm});
            skLineSegment(sketch, "E99.14.0", {"start": v(-6.78, 6.4) * mm, "end": v(-6.8, 6.44) * mm});
            skLineSegment(sketch, "E99.14.1", {"start": v(-7.48, 5.57) * mm, "end": v(-7.53, 5.58) * mm});
            skLineSegment(sketch, "E99.14.2", {"start": v(-6.74, 6.7) * mm, "end": v(-6.72, 6.72) * mm});
            skLineSegment(sketch, "E99.14.3", {"start": v(-6.77, 6.66) * mm, "end": v(-6.74, 6.7) * mm});
            skLineSegment(sketch, "E99.14.4", {"start": v(-6.7, 6.22) * mm, "end": v(-6.72, 6.26) * mm});
            skLineSegment(sketch, "E99.14.5", {"start": v(-7.06, 5.45) * mm, "end": v(-7.1, 5.47) * mm});
            skLineSegment(sketch, "E99.14.6", {"start": v(-6.66, 6.13) * mm, "end": v(-6.68, 6.18) * mm});
            skLineSegment(sketch, "E99.14.7", {"start": v(-6.5, 5.85) * mm, "end": v(-6.53, 5.89) * mm});
            skLineSegment(sketch, "E99.14.8", {"start": v(-6.68, 6.18) * mm, "end": v(-6.7, 6.22) * mm});
            skLineSegment(sketch, "E99.14.9", {"start": v(-6.55, 5.93) * mm, "end": v(-6.57, 5.97) * mm});
            skLineSegment(sketch, "E99.14.10", {"start": v(-7.15, 5.48) * mm, "end": v(-7.2, 5.5) * mm});
            skLineSegment(sketch, "E99.14.11", {"start": v(-6.93, 5.4) * mm, "end": v(-6.97, 5.42) * mm});
            skLineSegment(sketch, "E99.14.12", {"start": v(-7.24, 5.5) * mm, "end": v(-7.29, 5.52) * mm});
            skLineSegment(sketch, "E99.14.13", {"start": v(-6.62, 6.05) * mm, "end": v(-6.64, 6.1) * mm});
            skLineSegment(sketch, "E99.14.14", {"start": v(-6.8, 6.44) * mm, "end": v(-6.82, 6.49) * mm});
            skLineSegment(sketch, "E99.14.15", {"start": v(-6.6, 6) * mm, "end": v(-6.62, 6.05) * mm});
            skLineSegment(sketch, "E99.14.16", {"start": v(-6.76, 6.35) * mm, "end": v(-6.78, 6.4) * mm});
            skLineSegment(sketch, "E99.14.17", {"start": v(-6.64, 6.1) * mm, "end": v(-6.66, 6.13) * mm});
            skLineSegment(sketch, "E99.14.18", {"start": v(-7.43, 5.56) * mm, "end": v(-7.48, 5.57) * mm});
            skLineSegment(sketch, "E99.14.19", {"start": v(-6.82, 6.49) * mm, "end": v(-6.83, 6.54) * mm});
            skLineSegment(sketch, "E99.14.20", {"start": v(-6.8, 6.64) * mm, "end": v(-6.77, 6.66) * mm});
            skLineSegment(sketch, "E99.14.21", {"start": v(-6.89, 5.39) * mm, "end": v(-6.93, 5.4) * mm});
            skLineSegment(sketch, "E99.14.22", {"start": v(-7.02, 5.44) * mm, "end": v(-7.06, 5.45) * mm});
            skLineSegment(sketch, "E99.14.23", {"start": v(-7.34, 5.53) * mm, "end": v(-7.38, 5.55) * mm});
            skLineSegment(sketch, "E99.14.24", {"start": v(-6.72, 6.26) * mm, "end": v(-6.74, 6.3) * mm});
            skLineSegment(sketch, "E99.14.25", {"start": v(-6.53, 5.89) * mm, "end": v(-6.55, 5.93) * mm});
            skLineSegment(sketch, "E99.14.26", {"start": v(-6.83, 6.54) * mm, "end": v(-6.85, 6.58) * mm});
            skLineSegment(sketch, "E99.14.27", {"start": v(-6.82, 6.61) * mm, "end": v(-6.8, 6.64) * mm});
            skLineSegment(sketch, "E99.14.28", {"start": v(-6.74, 6.3) * mm, "end": v(-6.76, 6.35) * mm});
            skLineSegment(sketch, "E99.14.29", {"start": v(-7.1, 5.47) * mm, "end": v(-7.15, 5.48) * mm});
            skLineSegment(sketch, "E99.14.30", {"start": v(-7.38, 5.55) * mm, "end": v(-7.43, 5.56) * mm});
            skLineSegment(sketch, "E99.14.31", {"start": v(-6.57, 5.97) * mm, "end": v(-6.6, 6) * mm});
            skLineSegment(sketch, "E99.14.32", {"start": v(-7.29, 5.52) * mm, "end": v(-7.34, 5.53) * mm});
            skLineSegment(sketch, "E99.14.33", {"start": v(-6.97, 5.42) * mm, "end": v(-7.02, 5.44) * mm});
            skLineSegment(sketch, "E99.14.34", {"start": v(-7.53, 5.58) * mm, "end": v(-7.57, 5.59) * mm});
            skLineSegment(sketch, "E99.14.35", {"start": v(-7.76, 5.48) * mm, "end": v(-7.78, 5.45) * mm});
            skLineSegment(sketch, "E99.14.36", {"start": v(-7.2, 5.5) * mm, "end": v(-7.24, 5.5) * mm});
            skLineSegment(sketch, "E99.14.37", {"start": v(-7.74, 5.51) * mm, "end": v(-7.76, 5.48) * mm});
            skLineSegment(sketch, "E99.14.38", {"start": v(-7.57, 5.59) * mm, "end": v(-7.62, 5.6) * mm});
            skLineSegment(sketch, "E99.14.39", {"start": v(-6.85, 6.58) * mm, "end": v(-6.82, 6.61) * mm});
            skLineSegment(sketch, "E99.14.40", {"start": v(-7.62, 5.6) * mm, "end": v(-7.67, 5.6) * mm});
            skLineSegment(sketch, "E99.14.41", {"start": v(-7.72, 5.54) * mm, "end": v(-7.74, 5.51) * mm});
            skLineSegment(sketch, "E99.14.42", {"start": v(-7.7, 5.57) * mm, "end": v(-7.72, 5.54) * mm});
            skLineSegment(sketch, "E99.14.43", {"start": v(-6.85, 5.37) * mm, "end": v(-6.89, 5.39) * mm});
            skLineSegment(sketch, "E99.14.44", {"start": v(-7.67, 5.6) * mm, "end": v(-7.7, 5.57) * mm});
            skLineSegment(sketch, "E99.14.45", {"start": v(-6.47, 5.81) * mm, "end": v(-6.5, 5.85) * mm});
            skLineSegment(sketch, "E99.14.46", {"start": v(-6.65, 5.29) * mm, "end": v(-6.66, 5.29) * mm});
            skLineSegment(sketch, "E99.14.47", {"start": v(-6.76, 5.33) * mm, "end": v(-6.8, 5.35) * mm});
            skLineSegment(sketch, "E99.14.48", {"start": v(-6.8, 5.35) * mm, "end": v(-6.85, 5.37) * mm});
            skLineSegment(sketch, "E99.14.49", {"start": v(-6.37, 5.66) * mm, "end": v(-6.38, 5.68) * mm});
            skLineSegment(sketch, "E99.14.50", {"start": v(-6.68, 5.3) * mm, "end": v(-6.7, 5.3) * mm});
            skLineSegment(sketch, "E99.14.51", {"start": v(-6.36, 5.61) * mm, "end": v(-6.36, 5.63) * mm});
            skLineSegment(sketch, "E99.14.52", {"start": v(-6.45, 5.77) * mm, "end": v(-6.47, 5.81) * mm});
            skLineSegment(sketch, "E99.14.53", {"start": v(-6.39, 5.7) * mm, "end": v(-6.4, 5.7) * mm});
            skLineSegment(sketch, "E99.14.54", {"start": v(-6.4, 5.72) * mm, "end": v(-6.42, 5.74) * mm});
            skLineSegment(sketch, "E99.14.55", {"start": v(-6.7, 5.3) * mm, "end": v(-6.71, 5.3) * mm});
            skLineSegment(sketch, "E99.14.56", {"start": v(-6.75, 5.32) * mm, "end": v(-6.76, 5.33) * mm});
            skLineSegment(sketch, "E99.14.57", {"start": v(-6.38, 5.68) * mm, "end": v(-6.39, 5.7) * mm});
            skLineSegment(sketch, "E99.14.58", {"start": v(-6.63, 5.28) * mm, "end": v(-6.65, 5.29) * mm});
            skLineSegment(sketch, "E99.14.59", {"start": v(-6.42, 5.74) * mm, "end": v(-6.45, 5.77) * mm});
            skLineSegment(sketch, "E99.14.60", {"start": v(-6.73, 5.31) * mm, "end": v(-6.75, 5.32) * mm});
            skLineSegment(sketch, "E99.14.61", {"start": v(-6.66, 5.29) * mm, "end": v(-6.68, 5.3) * mm});
            skLineSegment(sketch, "E99.14.62", {"start": v(-6.4, 5.7) * mm, "end": v(-6.4, 5.72) * mm});
            skLineSegment(sketch, "E99.14.63", {"start": v(-6.71, 5.3) * mm, "end": v(-6.73, 5.31) * mm});
            skLineSegment(sketch, "E99.14.64", {"start": v(-6.61, 5.28) * mm, "end": v(-6.63, 5.28) * mm});
            skLineSegment(sketch, "E99.14.65", {"start": v(-6.35, 5.6) * mm, "end": v(-6.36, 5.61) * mm});
            skLineSegment(sketch, "E99.14.66", {"start": v(-6.36, 5.63) * mm, "end": v(-6.37, 5.64) * mm});
            skLineSegment(sketch, "E99.14.67", {"start": v(-6.6, 5.28) * mm, "end": v(-6.61, 5.28) * mm});
            skLineSegment(sketch, "E99.14.68", {"start": v(-6.37, 5.64) * mm, "end": v(-6.37, 5.66) * mm});
            skLineSegment(sketch, "E99.14.69", {"start": v(-6.35, 5.58) * mm, "end": v(-6.35, 5.6) * mm});
            skLineSegment(sketch, "E99.14.70", {"start": v(-6.35, 5.53) * mm, "end": v(-6.35, 5.55) * mm});
            skLineSegment(sketch, "E99.14.71", {"start": v(-6.35, 5.56) * mm, "end": v(-6.35, 5.58) * mm});
            skLineSegment(sketch, "E99.14.72", {"start": v(-6.35, 5.55) * mm, "end": v(-6.35, 5.56) * mm});
            skLineSegment(sketch, "E99.14.73", {"start": v(-6.35, 5.5) * mm, "end": v(-6.35, 5.52) * mm});
            skLineSegment(sketch, "E99.14.74", {"start": v(-6.58, 5.28) * mm, "end": v(-6.6, 5.28) * mm});
            skLineSegment(sketch, "E99.14.75", {"start": v(-6.35, 5.52) * mm, "end": v(-6.35, 5.53) * mm});
            skLineSegment(sketch, "E99.14.76", {"start": v(-6.42, 5.38) * mm, "end": v(-6.41, 5.39) * mm});
            skLineSegment(sketch, "E99.14.77", {"start": v(-6.38, 5.43) * mm, "end": v(-6.37, 5.45) * mm});
            skLineSegment(sketch, "E99.14.78", {"start": v(-6.4, 5.4) * mm, "end": v(-6.38, 5.43) * mm});
            skLineSegment(sketch, "E99.14.79", {"start": v(-6.43, 5.36) * mm, "end": v(-6.45, 5.34) * mm});
            skLineSegment(sketch, "E99.14.80", {"start": v(-6.52, 5.3) * mm, "end": v(-6.53, 5.3) * mm});
            skLineSegment(sketch, "E99.14.81", {"start": v(-6.55, 5.29) * mm, "end": v(-6.57, 5.29) * mm});
            skLineSegment(sketch, "E99.14.82", {"start": v(-6.36, 5.48) * mm, "end": v(-6.35, 5.5) * mm});
            skLineSegment(sketch, "E99.14.83", {"start": v(-6.47, 5.33) * mm, "end": v(-6.49, 5.32) * mm});
            skLineSegment(sketch, "E99.14.84", {"start": v(-6.57, 5.29) * mm, "end": v(-6.58, 5.28) * mm});
            skLineSegment(sketch, "E99.14.85", {"start": v(-6.37, 5.45) * mm, "end": v(-6.36, 5.46) * mm});
            skLineSegment(sketch, "E99.14.86", {"start": v(-6.53, 5.3) * mm, "end": v(-6.55, 5.29) * mm});
            skLineSegment(sketch, "E99.14.87", {"start": v(-6.45, 5.34) * mm, "end": v(-6.47, 5.33) * mm});
            skLineSegment(sketch, "E99.14.88", {"start": v(-6.5, 5.3) * mm, "end": v(-6.52, 5.3) * mm});
            skLineSegment(sketch, "E99.14.89", {"start": v(-6.4, 5.4) * mm, "end": v(-6.4, 5.4) * mm});
            skLineSegment(sketch, "E99.14.90", {"start": v(-6.4, 5.4) * mm, "end": v(-6.4, 5.4) * mm});
            skLineSegment(sketch, "E99.14.91", {"start": v(-6.36, 5.46) * mm, "end": v(-6.36, 5.48) * mm});
            skLineSegment(sketch, "E99.14.92", {"start": v(-6.49, 5.32) * mm, "end": v(-6.5, 5.3) * mm});
            skLineSegment(sketch, "E99.14.93", {"start": v(-6.43, 5.36) * mm, "end": v(-6.43, 5.36) * mm});
            skLineSegment(sketch, "E99.14.94", {"start": v(-6.43, 5.37) * mm, "end": v(-6.43, 5.36) * mm});
            skLineSegment(sketch, "E99.14.95", {"start": v(-6.42, 5.37) * mm, "end": v(-6.43, 5.37) * mm});
            skLineSegment(sketch, "E99.14.96", {"start": v(-6.42, 5.38) * mm, "end": v(-6.42, 5.37) * mm});
            skLineSegment(sketch, "E99.14.97", {"start": v(-6.42, 5.38) * mm, "end": v(-6.42, 5.38) * mm});
            skLineSegment(sketch, "E99.14.98", {"start": v(-6.4, 5.4) * mm, "end": v(-6.4, 5.4) * mm});
            skLineSegment(sketch, "E99.14.99", {"start": v(-6.41, 5.39) * mm, "end": v(-6.4, 5.4) * mm});
            skLineSegment(sketch, "E99.15.0", {"start": v(-7.79, 5.12) * mm, "end": v(-7.81, 5.16) * mm});
            skLineSegment(sketch, "E99.15.1", {"start": v(-8.33, 4.18) * mm, "end": v(-8.38, 4.18) * mm});
            skLineSegment(sketch, "E99.15.2", {"start": v(-7.8, 5.42) * mm, "end": v(-7.78, 5.45) * mm});
            skLineSegment(sketch, "E99.15.3", {"start": v(-7.82, 5.39) * mm, "end": v(-7.8, 5.42) * mm});
            skLineSegment(sketch, "E99.15.4", {"start": v(-7.68, 4.96) * mm, "end": v(-7.7, 5) * mm});
            skLineSegment(sketch, "E99.15.5", {"start": v(-7.9, 4.14) * mm, "end": v(-7.95, 4.15) * mm});
            skLineSegment(sketch, "E99.15.6", {"start": v(-7.63, 4.88) * mm, "end": v(-7.65, 4.92) * mm});
            skLineSegment(sketch, "E99.15.7", {"start": v(-7.42, 4.63) * mm, "end": v(-7.45, 4.66) * mm});
            skLineSegment(sketch, "E99.15.8", {"start": v(-7.65, 4.92) * mm, "end": v(-7.68, 4.96) * mm});
            skLineSegment(sketch, "E99.15.9", {"start": v(-7.48, 4.7) * mm, "end": v(-7.5, 4.73) * mm});
            skLineSegment(sketch, "E99.15.10", {"start": v(-8, 4.16) * mm, "end": v(-8.04, 4.16) * mm});
            skLineSegment(sketch, "E99.15.11", {"start": v(-7.76, 4.12) * mm, "end": v(-7.8, 4.13) * mm});
            skLineSegment(sketch, "E99.15.12", {"start": v(-8.09, 4.17) * mm, "end": v(-8.14, 4.17) * mm});
            skLineSegment(sketch, "E99.15.13", {"start": v(-7.57, 4.8) * mm, "end": v(-7.6, 4.84) * mm});
            skLineSegment(sketch, "E99.15.14", {"start": v(-7.81, 5.16) * mm, "end": v(-7.84, 5.2) * mm});
            skLineSegment(sketch, "E99.15.15", {"start": v(-7.54, 4.77) * mm, "end": v(-7.57, 4.8) * mm});
            skLineSegment(sketch, "E99.15.16", {"start": v(-7.76, 5.08) * mm, "end": v(-7.79, 5.12) * mm});
            skLineSegment(sketch, "E99.15.17", {"start": v(-7.6, 4.84) * mm, "end": v(-7.63, 4.88) * mm});
            skLineSegment(sketch, "E99.15.18", {"start": v(-8.28, 4.18) * mm, "end": v(-8.33, 4.18) * mm});
            skLineSegment(sketch, "E99.15.19", {"start": v(-7.84, 5.2) * mm, "end": v(-7.86, 5.25) * mm});
            skLineSegment(sketch, "E99.15.20", {"start": v(-7.85, 5.36) * mm, "end": v(-7.82, 5.39) * mm});
            skLineSegment(sketch, "E99.15.21", {"start": v(-7.72, 4.1) * mm, "end": v(-7.76, 4.12) * mm});
            skLineSegment(sketch, "E99.15.22", {"start": v(-7.85, 4.14) * mm, "end": v(-7.9, 4.14) * mm});
            skLineSegment(sketch, "E99.15.23", {"start": v(-8.18, 4.18) * mm, "end": v(-8.23, 4.18) * mm});
            skLineSegment(sketch, "E99.15.24", {"start": v(-7.7, 5) * mm, "end": v(-7.74, 5.04) * mm});
            skLineSegment(sketch, "E99.15.25", {"start": v(-7.45, 4.66) * mm, "end": v(-7.48, 4.7) * mm});
            skLineSegment(sketch, "E99.15.26", {"start": v(-7.86, 5.25) * mm, "end": v(-7.89, 5.3) * mm});
            skLineSegment(sketch, "E99.15.27", {"start": v(-7.87, 5.32) * mm, "end": v(-7.85, 5.36) * mm});
            skLineSegment(sketch, "E99.15.28", {"start": v(-7.74, 5.04) * mm, "end": v(-7.76, 5.08) * mm});
            skLineSegment(sketch, "E99.15.29", {"start": v(-7.95, 4.15) * mm, "end": v(-8, 4.16) * mm});
            skLineSegment(sketch, "E99.15.30", {"start": v(-8.23, 4.18) * mm, "end": v(-8.28, 4.18) * mm});
            skLineSegment(sketch, "E99.15.31", {"start": v(-7.5, 4.73) * mm, "end": v(-7.54, 4.77) * mm});
            skLineSegment(sketch, "E99.15.32", {"start": v(-8.14, 4.17) * mm, "end": v(-8.18, 4.18) * mm});
            skLineSegment(sketch, "E99.15.33", {"start": v(-7.8, 4.13) * mm, "end": v(-7.85, 4.14) * mm});
            skLineSegment(sketch, "E99.15.34", {"start": v(-8.38, 4.18) * mm, "end": v(-8.43, 4.19) * mm});
            skLineSegment(sketch, "E99.15.35", {"start": v(-8.6, 4.05) * mm, "end": v(-8.6, 4.01) * mm});
            skLineSegment(sketch, "E99.15.36", {"start": v(-8.04, 4.16) * mm, "end": v(-8.09, 4.17) * mm});
            skLineSegment(sketch, "E99.15.37", {"start": v(-8.58, 4.08) * mm, "end": v(-8.6, 4.05) * mm});
            skLineSegment(sketch, "E99.15.38", {"start": v(-8.43, 4.19) * mm, "end": v(-8.48, 4.19) * mm});
            skLineSegment(sketch, "E99.15.39", {"start": v(-7.89, 5.3) * mm, "end": v(-7.87, 5.32) * mm});
            skLineSegment(sketch, "E99.15.40", {"start": v(-8.48, 4.19) * mm, "end": v(-8.53, 4.18) * mm});
            skLineSegment(sketch, "E99.15.41", {"start": v(-8.56, 4.12) * mm, "end": v(-8.58, 4.08) * mm});
            skLineSegment(sketch, "E99.15.42", {"start": v(-8.55, 4.15) * mm, "end": v(-8.56, 4.12) * mm});
            skLineSegment(sketch, "E99.15.43", {"start": v(-7.67, 4.1) * mm, "end": v(-7.72, 4.1) * mm});
            skLineSegment(sketch, "E99.15.44", {"start": v(-8.53, 4.18) * mm, "end": v(-8.55, 4.15) * mm});
            skLineSegment(sketch, "E99.15.45", {"start": v(-7.39, 4.6) * mm, "end": v(-7.42, 4.63) * mm});
            skLineSegment(sketch, "E99.15.46", {"start": v(-7.46, 4.05) * mm, "end": v(-7.48, 4.05) * mm});
            skLineSegment(sketch, "E99.15.47", {"start": v(-7.59, 4.07) * mm, "end": v(-7.63, 4.08) * mm});
            skLineSegment(sketch, "E99.15.48", {"start": v(-7.63, 4.08) * mm, "end": v(-7.67, 4.1) * mm});
            skLineSegment(sketch, "E99.15.49", {"start": v(-7.26, 4.47) * mm, "end": v(-7.27, 4.48) * mm});
            skLineSegment(sketch, "E99.15.50", {"start": v(-7.5, 4.05) * mm, "end": v(-7.52, 4.06) * mm});
            skLineSegment(sketch, "E99.15.51", {"start": v(-7.23, 4.42) * mm, "end": v(-7.24, 4.44) * mm});
            skLineSegment(sketch, "E99.15.52", {"start": v(-7.35, 4.57) * mm, "end": v(-7.39, 4.6) * mm});
            skLineSegment(sketch, "E99.15.53", {"start": v(-7.28, 4.5) * mm, "end": v(-7.3, 4.5) * mm});
            skLineSegment(sketch, "E99.15.54", {"start": v(-7.3, 4.52) * mm, "end": v(-7.32, 4.53) * mm});
            skLineSegment(sketch, "E99.15.55", {"start": v(-7.52, 4.06) * mm, "end": v(-7.53, 4.06) * mm});
            skLineSegment(sketch, "E99.15.56", {"start": v(-7.57, 4.07) * mm, "end": v(-7.59, 4.07) * mm});
            skLineSegment(sketch, "E99.15.57", {"start": v(-7.27, 4.48) * mm, "end": v(-7.28, 4.5) * mm});
            skLineSegment(sketch, "E99.15.58", {"start": v(-7.45, 4.05) * mm, "end": v(-7.46, 4.05) * mm});
            skLineSegment(sketch, "E99.15.59", {"start": v(-7.32, 4.53) * mm, "end": v(-7.35, 4.57) * mm});
            skLineSegment(sketch, "E99.15.60", {"start": v(-7.55, 4.06) * mm, "end": v(-7.57, 4.07) * mm});
            skLineSegment(sketch, "E99.15.61", {"start": v(-7.48, 4.05) * mm, "end": v(-7.5, 4.05) * mm});
            skLineSegment(sketch, "E99.15.62", {"start": v(-7.3, 4.5) * mm, "end": v(-7.3, 4.52) * mm});
            skLineSegment(sketch, "E99.15.63", {"start": v(-7.53, 4.06) * mm, "end": v(-7.55, 4.06) * mm});
            skLineSegment(sketch, "E99.15.64", {"start": v(-7.43, 4.05) * mm, "end": v(-7.45, 4.05) * mm});
            skLineSegment(sketch, "E99.15.65", {"start": v(-7.23, 4.4) * mm, "end": v(-7.23, 4.42) * mm});
            skLineSegment(sketch, "E99.15.66", {"start": v(-7.24, 4.44) * mm, "end": v(-7.25, 4.45) * mm});
            skLineSegment(sketch, "E99.15.67", {"start": v(-7.42, 4.06) * mm, "end": v(-7.43, 4.05) * mm});
            skLineSegment(sketch, "E99.15.68", {"start": v(-7.25, 4.45) * mm, "end": v(-7.26, 4.47) * mm});
            skLineSegment(sketch, "E99.15.69", {"start": v(-7.22, 4.4) * mm, "end": v(-7.23, 4.4) * mm});
            skLineSegment(sketch, "E99.15.70", {"start": v(-7.21, 4.35) * mm, "end": v(-7.21, 4.36) * mm});
            skLineSegment(sketch, "E99.15.71", {"start": v(-7.22, 4.38) * mm, "end": v(-7.22, 4.4) * mm});
            skLineSegment(sketch, "E99.15.72", {"start": v(-7.21, 4.36) * mm, "end": v(-7.22, 4.38) * mm});
            skLineSegment(sketch, "E99.15.73", {"start": v(-7.2, 4.31) * mm, "end": v(-7.2, 4.33) * mm});
            skLineSegment(sketch, "E99.15.74", {"start": v(-7.4, 4.06) * mm, "end": v(-7.42, 4.06) * mm});
            skLineSegment(sketch, "E99.15.75", {"start": v(-7.2, 4.33) * mm, "end": v(-7.21, 4.35) * mm});
            skLineSegment(sketch, "E99.15.76", {"start": v(-7.25, 4.19) * mm, "end": v(-7.25, 4.2) * mm});
            skLineSegment(sketch, "E99.15.77", {"start": v(-7.23, 4.24) * mm, "end": v(-7.22, 4.26) * mm});
            skLineSegment(sketch, "E99.15.78", {"start": v(-7.24, 4.21) * mm, "end": v(-7.23, 4.24) * mm});
            skLineSegment(sketch, "E99.15.79", {"start": v(-7.27, 4.16) * mm, "end": v(-7.28, 4.14) * mm});
            skLineSegment(sketch, "E99.15.80", {"start": v(-7.34, 4.09) * mm, "end": v(-7.35, 4.08) * mm});
            skLineSegment(sketch, "E99.15.81", {"start": v(-7.37, 4.07) * mm, "end": v(-7.38, 4.07) * mm});
            skLineSegment(sketch, "E99.15.82", {"start": v(-7.21, 4.3) * mm, "end": v(-7.2, 4.31) * mm});
            skLineSegment(sketch, "E99.15.83", {"start": v(-7.3, 4.12) * mm, "end": v(-7.31, 4.1) * mm});
            skLineSegment(sketch, "E99.15.84", {"start": v(-7.38, 4.07) * mm, "end": v(-7.4, 4.06) * mm});
            skLineSegment(sketch, "E99.15.85", {"start": v(-7.22, 4.26) * mm, "end": v(-7.21, 4.28) * mm});
            skLineSegment(sketch, "E99.15.86", {"start": v(-7.35, 4.08) * mm, "end": v(-7.37, 4.07) * mm});
            skLineSegment(sketch, "E99.15.87", {"start": v(-7.28, 4.14) * mm, "end": v(-7.3, 4.12) * mm});
            skLineSegment(sketch, "E99.15.88", {"start": v(-7.32, 4.1) * mm, "end": v(-7.34, 4.09) * mm});
            skLineSegment(sketch, "E99.15.89", {"start": v(-7.25, 4.2) * mm, "end": v(-7.24, 4.2) * mm});
            skLineSegment(sketch, "E99.15.90", {"start": v(-7.24, 4.2) * mm, "end": v(-7.24, 4.21) * mm});
            skLineSegment(sketch, "E99.15.91", {"start": v(-7.21, 4.28) * mm, "end": v(-7.21, 4.3) * mm});
            skLineSegment(sketch, "E99.15.92", {"start": v(-7.31, 4.1) * mm, "end": v(-7.32, 4.1) * mm});
            skLineSegment(sketch, "E99.15.93", {"start": v(-7.26, 4.17) * mm, "end": v(-7.27, 4.16) * mm});
            skLineSegment(sketch, "E99.15.94", {"start": v(-7.26, 4.17) * mm, "end": v(-7.26, 4.17) * mm});
            skLineSegment(sketch, "E99.15.95", {"start": v(-7.26, 4.18) * mm, "end": v(-7.26, 4.17) * mm});
            skLineSegment(sketch, "E99.15.96", {"start": v(-7.26, 4.18) * mm, "end": v(-7.26, 4.18) * mm});
            skLineSegment(sketch, "E99.15.97", {"start": v(-7.25, 4.19) * mm, "end": v(-7.26, 4.18) * mm});
            skLineSegment(sketch, "E99.15.98", {"start": v(-7.24, 4.2) * mm, "end": v(-7.24, 4.2) * mm});
            skLineSegment(sketch, "E99.15.99", {"start": v(-7.25, 4.2) * mm, "end": v(-7.25, 4.2) * mm});
            skLineSegment(sketch, "E99.16.0", {"start": v(-8.56, 3.7) * mm, "end": v(-8.6, 3.73) * mm});
            skLineSegment(sketch, "E99.16.1", {"start": v(-8.93, 2.67) * mm, "end": v(-8.98, 2.67) * mm});
            skLineSegment(sketch, "E99.16.2", {"start": v(-8.63, 3.98) * mm, "end": v(-8.6, 4.01) * mm});
            skLineSegment(sketch, "E99.16.3", {"start": v(-8.64, 3.95) * mm, "end": v(-8.63, 3.98) * mm});
            skLineSegment(sketch, "E99.16.4", {"start": v(-8.43, 3.55) * mm, "end": v(-8.46, 3.59) * mm});
            skLineSegment(sketch, "E99.16.5", {"start": v(-8.5, 2.7) * mm, "end": v(-8.55, 2.7) * mm});
            skLineSegment(sketch, "E99.16.6", {"start": v(-8.36, 3.48) * mm, "end": v(-8.4, 3.52) * mm});
            skLineSegment(sketch, "E99.16.7", {"start": v(-8.1, 3.27) * mm, "end": v(-8.15, 3.3) * mm});
            skLineSegment(sketch, "E99.16.8", {"start": v(-8.4, 3.52) * mm, "end": v(-8.43, 3.55) * mm});
            skLineSegment(sketch, "E99.16.9", {"start": v(-8.18, 3.33) * mm, "end": v(-8.22, 3.36) * mm});
            skLineSegment(sketch, "E99.16.10", {"start": v(-8.6, 2.7) * mm, "end": v(-8.64, 2.7) * mm});
            skLineSegment(sketch, "E99.16.11", {"start": v(-8.36, 2.7) * mm, "end": v(-8.4, 2.7) * mm});
            skLineSegment(sketch, "E99.16.12", {"start": v(-8.69, 2.7) * mm, "end": v(-8.74, 2.7) * mm});
            skLineSegment(sketch, "E99.16.13", {"start": v(-8.29, 3.42) * mm, "end": v(-8.32, 3.45) * mm});
            skLineSegment(sketch, "E99.16.14", {"start": v(-8.6, 3.73) * mm, "end": v(-8.62, 3.77) * mm});
            skLineSegment(sketch, "E99.16.15", {"start": v(-8.25, 3.39) * mm, "end": v(-8.29, 3.42) * mm});
            skLineSegment(sketch, "E99.16.16", {"start": v(-8.53, 3.66) * mm, "end": v(-8.56, 3.7) * mm});
            skLineSegment(sketch, "E99.16.17", {"start": v(-8.32, 3.45) * mm, "end": v(-8.36, 3.48) * mm});
            skLineSegment(sketch, "E99.16.18", {"start": v(-8.88, 2.68) * mm, "end": v(-8.93, 2.67) * mm});
            skLineSegment(sketch, "E99.16.19", {"start": v(-8.62, 3.77) * mm, "end": v(-8.66, 3.8) * mm});
            skLineSegment(sketch, "E99.16.20", {"start": v(-8.66, 3.91) * mm, "end": v(-8.64, 3.95) * mm});
            skLineSegment(sketch, "E99.16.21", {"start": v(-8.31, 2.7) * mm, "end": v(-8.36, 2.7) * mm});
            skLineSegment(sketch, "E99.16.22", {"start": v(-8.45, 2.7) * mm, "end": v(-8.5, 2.7) * mm});
            skLineSegment(sketch, "E99.16.23", {"start": v(-8.79, 2.7) * mm, "end": v(-8.83, 2.69) * mm});
            skLineSegment(sketch, "E99.16.24", {"start": v(-8.46, 3.59) * mm, "end": v(-8.5, 3.62) * mm});
            skLineSegment(sketch, "E99.16.25", {"start": v(-8.15, 3.3) * mm, "end": v(-8.18, 3.33) * mm});
            skLineSegment(sketch, "E99.16.26", {"start": v(-8.66, 3.8) * mm, "end": v(-8.69, 3.84) * mm});
            skLineSegment(sketch, "E99.16.27", {"start": v(-8.67, 3.88) * mm, "end": v(-8.66, 3.91) * mm});
            skLineSegment(sketch, "E99.16.28", {"start": v(-8.5, 3.62) * mm, "end": v(-8.53, 3.66) * mm});
            skLineSegment(sketch, "E99.16.29", {"start": v(-8.55, 2.7) * mm, "end": v(-8.6, 2.7) * mm});
            skLineSegment(sketch, "E99.16.30", {"start": v(-8.83, 2.69) * mm, "end": v(-8.88, 2.68) * mm});
            skLineSegment(sketch, "E99.16.31", {"start": v(-8.22, 3.36) * mm, "end": v(-8.25, 3.39) * mm});
            skLineSegment(sketch, "E99.16.32", {"start": v(-8.74, 2.7) * mm, "end": v(-8.79, 2.7) * mm});
            skLineSegment(sketch, "E99.16.33", {"start": v(-8.4, 2.7) * mm, "end": v(-8.45, 2.7) * mm});
            skLineSegment(sketch, "E99.16.34", {"start": v(-8.98, 2.67) * mm, "end": v(-9.03, 2.66) * mm});
            skLineSegment(sketch, "E99.16.35", {"start": v(-9.17, 2.5) * mm, "end": v(-9.18, 2.46) * mm});
            skLineSegment(sketch, "E99.16.36", {"start": v(-8.64, 2.7) * mm, "end": v(-8.69, 2.7) * mm});
            skLineSegment(sketch, "E99.16.37", {"start": v(-9.16, 2.53) * mm, "end": v(-9.17, 2.5) * mm});
            skLineSegment(sketch, "E99.16.38", {"start": v(-9.03, 2.66) * mm, "end": v(-9.08, 2.65) * mm});
            skLineSegment(sketch, "E99.16.39", {"start": v(-8.69, 3.84) * mm, "end": v(-8.67, 3.88) * mm});
            skLineSegment(sketch, "E99.16.40", {"start": v(-9.08, 2.65) * mm, "end": v(-9.13, 2.64) * mm});
            skLineSegment(sketch, "E99.16.41", {"start": v(-9.15, 2.57) * mm, "end": v(-9.16, 2.53) * mm});
            skLineSegment(sketch, "E99.16.42", {"start": v(-9.14, 2.6) * mm, "end": v(-9.15, 2.57) * mm});
            skLineSegment(sketch, "E99.16.43", {"start": v(-8.27, 2.7) * mm, "end": v(-8.31, 2.7) * mm});
            skLineSegment(sketch, "E99.16.44", {"start": v(-9.13, 2.64) * mm, "end": v(-9.14, 2.6) * mm});
            skLineSegment(sketch, "E99.16.45", {"start": v(-8.07, 3.25) * mm, "end": v(-8.1, 3.27) * mm});
            skLineSegment(sketch, "E99.16.46", {"start": v(-8.05, 2.7) * mm, "end": v(-8.07, 2.7) * mm});
            skLineSegment(sketch, "E99.16.47", {"start": v(-8.18, 2.7) * mm, "end": v(-8.22, 2.7) * mm});
            skLineSegment(sketch, "E99.16.48", {"start": v(-8.22, 2.7) * mm, "end": v(-8.27, 2.7) * mm});
            skLineSegment(sketch, "E99.16.49", {"start": v(-7.92, 3.14) * mm, "end": v(-7.94, 3.15) * mm});
            skLineSegment(sketch, "E99.16.50", {"start": v(-8.09, 2.69) * mm, "end": v(-8.1, 2.69) * mm});
            skLineSegment(sketch, "E99.16.51", {"start": v(-7.9, 3.1) * mm, "end": v(-7.9, 3.11) * mm});
            skLineSegment(sketch, "E99.16.52", {"start": v(-8.03, 3.22) * mm, "end": v(-8.07, 3.25) * mm});
            skLineSegment(sketch, "E99.16.53", {"start": v(-7.95, 3.16) * mm, "end": v(-7.97, 3.17) * mm});
            skLineSegment(sketch, "E99.16.54", {"start": v(-7.98, 3.18) * mm, "end": v(-8, 3.2) * mm});
            skLineSegment(sketch, "E99.16.55", {"start": v(-8.1, 2.69) * mm, "end": v(-8.12, 2.69) * mm});
            skLineSegment(sketch, "E99.16.56", {"start": v(-8.16, 2.7) * mm, "end": v(-8.18, 2.7) * mm});
            skLineSegment(sketch, "E99.16.57", {"start": v(-7.94, 3.15) * mm, "end": v(-7.95, 3.16) * mm});
            skLineSegment(sketch, "E99.16.58", {"start": v(-8.04, 2.7) * mm, "end": v(-8.05, 2.7) * mm});
            skLineSegment(sketch, "E99.16.59", {"start": v(-8, 3.2) * mm, "end": v(-8.03, 3.22) * mm});
            skLineSegment(sketch, "E99.16.60", {"start": v(-8.14, 2.69) * mm, "end": v(-8.16, 2.7) * mm});
            skLineSegment(sketch, "E99.16.61", {"start": v(-8.07, 2.7) * mm, "end": v(-8.09, 2.69) * mm});
            skLineSegment(sketch, "E99.16.62", {"start": v(-7.97, 3.17) * mm, "end": v(-7.98, 3.18) * mm});
            skLineSegment(sketch, "E99.16.63", {"start": v(-8.12, 2.69) * mm, "end": v(-8.14, 2.69) * mm});
            skLineSegment(sketch, "E99.16.64", {"start": v(-8.02, 2.7) * mm, "end": v(-8.04, 2.7) * mm});
            skLineSegment(sketch, "E99.16.65", {"start": v(-7.88, 3.09) * mm, "end": v(-7.9, 3.1) * mm});
            skLineSegment(sketch, "E99.16.66", {"start": v(-7.9, 3.11) * mm, "end": v(-7.91, 3.13) * mm});
            skLineSegment(sketch, "E99.16.67", {"start": v(-8, 2.7) * mm, "end": v(-8.02, 2.7) * mm});
            skLineSegment(sketch, "E99.16.68", {"start": v(-7.91, 3.13) * mm, "end": v(-7.92, 3.14) * mm});
            skLineSegment(sketch, "E99.16.69", {"start": v(-7.87, 3.07) * mm, "end": v(-7.88, 3.09) * mm});
            skLineSegment(sketch, "E99.16.70", {"start": v(-7.86, 3.03) * mm, "end": v(-7.86, 3.04) * mm});
            skLineSegment(sketch, "E99.16.71", {"start": v(-7.87, 3.06) * mm, "end": v(-7.87, 3.07) * mm});
            skLineSegment(sketch, "E99.16.72", {"start": v(-7.86, 3.04) * mm, "end": v(-7.87, 3.06) * mm});
            skLineSegment(sketch, "E99.16.73", {"start": v(-7.85, 3) * mm, "end": v(-7.85, 3.01) * mm});
            skLineSegment(sketch, "E99.16.74", {"start": v(-8, 2.71) * mm, "end": v(-8, 2.7) * mm});
            skLineSegment(sketch, "E99.16.75", {"start": v(-7.85, 3.01) * mm, "end": v(-7.86, 3.03) * mm});
            skLineSegment(sketch, "E99.16.76", {"start": v(-7.87, 2.86) * mm, "end": v(-7.87, 2.87) * mm});
            skLineSegment(sketch, "E99.16.77", {"start": v(-7.85, 2.92) * mm, "end": v(-7.85, 2.94) * mm});
            skLineSegment(sketch, "E99.16.78", {"start": v(-7.86, 2.9) * mm, "end": v(-7.85, 2.92) * mm});
            skLineSegment(sketch, "E99.16.79", {"start": v(-7.88, 2.84) * mm, "end": v(-7.9, 2.81) * mm});
            skLineSegment(sketch, "E99.16.80", {"start": v(-7.94, 2.75) * mm, "end": v(-7.95, 2.74) * mm});
            skLineSegment(sketch, "E99.16.81", {"start": v(-7.96, 2.73) * mm, "end": v(-7.98, 2.72) * mm});
            skLineSegment(sketch, "E99.16.82", {"start": v(-7.85, 2.98) * mm, "end": v(-7.85, 3) * mm});
            skLineSegment(sketch, "E99.16.83", {"start": v(-7.9, 2.8) * mm, "end": v(-7.91, 2.78) * mm});
            skLineSegment(sketch, "E99.16.84", {"start": v(-7.98, 2.72) * mm, "end": v(-8, 2.71) * mm});
            skLineSegment(sketch, "E99.16.85", {"start": v(-7.85, 2.94) * mm, "end": v(-7.85, 2.96) * mm});
            skLineSegment(sketch, "E99.16.86", {"start": v(-7.95, 2.74) * mm, "end": v(-7.96, 2.73) * mm});
            skLineSegment(sketch, "E99.16.87", {"start": v(-7.9, 2.81) * mm, "end": v(-7.9, 2.8) * mm});
            skLineSegment(sketch, "E99.16.88", {"start": v(-7.93, 2.76) * mm, "end": v(-7.94, 2.75) * mm});
            skLineSegment(sketch, "E99.16.89", {"start": v(-7.87, 2.88) * mm, "end": v(-7.86, 2.88) * mm});
            skLineSegment(sketch, "E99.16.90", {"start": v(-7.86, 2.89) * mm, "end": v(-7.86, 2.9) * mm});
            skLineSegment(sketch, "E99.16.91", {"start": v(-7.85, 2.96) * mm, "end": v(-7.85, 2.98) * mm});
            skLineSegment(sketch, "E99.16.92", {"start": v(-7.91, 2.78) * mm, "end": v(-7.93, 2.76) * mm});
            skLineSegment(sketch, "E99.16.93", {"start": v(-7.88, 2.84) * mm, "end": v(-7.88, 2.84) * mm});
            skLineSegment(sketch, "E99.16.94", {"start": v(-7.88, 2.85) * mm, "end": v(-7.88, 2.84) * mm});
            skLineSegment(sketch, "E99.16.95", {"start": v(-7.87, 2.85) * mm, "end": v(-7.88, 2.85) * mm});
            skLineSegment(sketch, "E99.16.96", {"start": v(-7.87, 2.86) * mm, "end": v(-7.87, 2.85) * mm});
            skLineSegment(sketch, "E99.16.97", {"start": v(-7.87, 2.86) * mm, "end": v(-7.87, 2.86) * mm});
            skLineSegment(sketch, "E99.16.98", {"start": v(-7.86, 2.88) * mm, "end": v(-7.86, 2.89) * mm});
            skLineSegment(sketch, "E99.16.99", {"start": v(-7.87, 2.87) * mm, "end": v(-7.87, 2.88) * mm});
            skLineSegment(sketch, "E99.17.0", {"start": v(-9.07, 2.15) * mm, "end": v(-9.1, 2.18) * mm});
            skLineSegment(sketch, "E99.17.1", {"start": v(-9.26, 1.08) * mm, "end": v(-9.3, 1.07) * mm});
            skLineSegment(sketch, "E99.17.2", {"start": v(-9.19, 2.42) * mm, "end": v(-9.18, 2.46) * mm});
            skLineSegment(sketch, "E99.17.3", {"start": v(-9.2, 2.39) * mm, "end": v(-9.19, 2.42) * mm});
            skLineSegment(sketch, "E99.17.4", {"start": v(-8.92, 2.03) * mm, "end": v(-8.95, 2.06) * mm});
            skLineSegment(sketch, "E99.17.5", {"start": v(-8.84, 1.2) * mm, "end": v(-8.89, 1.18) * mm});
            skLineSegment(sketch, "E99.17.6", {"start": v(-8.84, 1.98) * mm, "end": v(-8.88, 2) * mm});
            skLineSegment(sketch, "E99.17.7", {"start": v(-8.55, 1.81) * mm, "end": v(-8.6, 1.84) * mm});
            skLineSegment(sketch, "E99.17.8", {"start": v(-8.88, 2) * mm, "end": v(-8.92, 2.03) * mm});
            skLineSegment(sketch, "E99.17.9", {"start": v(-8.64, 1.86) * mm, "end": v(-8.68, 1.88) * mm});
            skLineSegment(sketch, "E99.17.10", {"start": v(-8.93, 1.17) * mm, "end": v(-8.98, 1.16) * mm});
            skLineSegment(sketch, "E99.17.11", {"start": v(-8.7, 1.21) * mm, "end": v(-8.75, 1.2) * mm});
            skLineSegment(sketch, "E99.17.12", {"start": v(-9.03, 1.15) * mm, "end": v(-9.07, 1.14) * mm});
            skLineSegment(sketch, "E99.17.13", {"start": v(-8.76, 1.93) * mm, "end": v(-8.8, 1.95) * mm});
            skLineSegment(sketch, "E99.17.14", {"start": v(-9.1, 2.18) * mm, "end": v(-9.15, 2.21) * mm});
            skLineSegment(sketch, "E99.17.15", {"start": v(-8.72, 1.9) * mm, "end": v(-8.76, 1.93) * mm});
            skLineSegment(sketch, "E99.17.16", {"start": v(-9.03, 2.12) * mm, "end": v(-9.07, 2.15) * mm});
            skLineSegment(sketch, "E99.17.17", {"start": v(-8.8, 1.95) * mm, "end": v(-8.84, 1.98) * mm});
            skLineSegment(sketch, "E99.17.18", {"start": v(-9.21, 1.1) * mm, "end": v(-9.26, 1.08) * mm});
            skLineSegment(sketch, "E99.17.19", {"start": v(-9.15, 2.21) * mm, "end": v(-9.19, 2.24) * mm});
            skLineSegment(sketch, "E99.17.20", {"start": v(-9.2, 2.35) * mm, "end": v(-9.2, 2.39) * mm});
            skLineSegment(sketch, "E99.17.21", {"start": v(-8.66, 1.22) * mm, "end": v(-8.7, 1.21) * mm});
            skLineSegment(sketch, "E99.17.22", {"start": v(-8.8, 1.2) * mm, "end": v(-8.84, 1.2) * mm});
            skLineSegment(sketch, "E99.17.23", {"start": v(-9.12, 1.12) * mm, "end": v(-9.17, 1.11) * mm});
            skLineSegment(sketch, "E99.17.24", {"start": v(-8.95, 2.06) * mm, "end": v(-9, 2.1) * mm});
            skLineSegment(sketch, "E99.17.25", {"start": v(-8.6, 1.84) * mm, "end": v(-8.64, 1.86) * mm});
            skLineSegment(sketch, "E99.17.26", {"start": v(-9.19, 2.24) * mm, "end": v(-9.22, 2.28) * mm});
            skLineSegment(sketch, "E99.17.27", {"start": v(-9.21, 2.31) * mm, "end": v(-9.2, 2.35) * mm});
            skLineSegment(sketch, "E99.17.28", {"start": v(-9, 2.1) * mm, "end": v(-9.03, 2.12) * mm});
            skLineSegment(sketch, "E99.17.29", {"start": v(-8.89, 1.18) * mm, "end": v(-8.93, 1.17) * mm});
            skLineSegment(sketch, "E99.17.30", {"start": v(-9.17, 1.11) * mm, "end": v(-9.21, 1.1) * mm});
            skLineSegment(sketch, "E99.17.31", {"start": v(-8.68, 1.88) * mm, "end": v(-8.72, 1.9) * mm});
            skLineSegment(sketch, "E99.17.32", {"start": v(-9.07, 1.14) * mm, "end": v(-9.12, 1.12) * mm});
            skLineSegment(sketch, "E99.17.33", {"start": v(-8.75, 1.2) * mm, "end": v(-8.8, 1.2) * mm});
            skLineSegment(sketch, "E99.17.34", {"start": v(-9.3, 1.07) * mm, "end": v(-9.35, 1.05) * mm});
            skLineSegment(sketch, "E99.17.35", {"start": v(-9.46, 0.87) * mm, "end": v(-9.46, 0.83) * mm});
            skLineSegment(sketch, "E99.17.36", {"start": v(-8.98, 1.16) * mm, "end": v(-9.03, 1.15) * mm});
            skLineSegment(sketch, "E99.17.37", {"start": v(-9.46, 0.9) * mm, "end": v(-9.46, 0.87) * mm});
            skLineSegment(sketch, "E99.17.38", {"start": v(-9.35, 1.05) * mm, "end": v(-9.4, 1.03) * mm});
            skLineSegment(sketch, "E99.17.39", {"start": v(-9.22, 2.28) * mm, "end": v(-9.21, 2.31) * mm});
            skLineSegment(sketch, "E99.17.40", {"start": v(-9.4, 1.03) * mm, "end": v(-9.45, 1.02) * mm});
            skLineSegment(sketch, "E99.17.41", {"start": v(-9.45, 0.94) * mm, "end": v(-9.46, 0.9) * mm});
            skLineSegment(sketch, "E99.17.42", {"start": v(-9.45, 0.98) * mm, "end": v(-9.45, 0.94) * mm});
            skLineSegment(sketch, "E99.17.43", {"start": v(-8.61, 1.23) * mm, "end": v(-8.66, 1.22) * mm});
            skLineSegment(sketch, "E99.17.44", {"start": v(-9.45, 1.02) * mm, "end": v(-9.45, 0.98) * mm});
            skLineSegment(sketch, "E99.17.45", {"start": v(-8.51, 1.8) * mm, "end": v(-8.55, 1.81) * mm});
            skLineSegment(sketch, "E99.17.46", {"start": v(-8.4, 1.25) * mm, "end": v(-8.42, 1.25) * mm});
            skLineSegment(sketch, "E99.17.47", {"start": v(-8.52, 1.23) * mm, "end": v(-8.57, 1.23) * mm});
            skLineSegment(sketch, "E99.17.48", {"start": v(-8.57, 1.23) * mm, "end": v(-8.61, 1.23) * mm});
            skLineSegment(sketch, "E99.17.49", {"start": v(-8.35, 1.71) * mm, "end": v(-8.36, 1.72) * mm});
            skLineSegment(sketch, "E99.17.50", {"start": v(-8.43, 1.24) * mm, "end": v(-8.45, 1.24) * mm});
            skLineSegment(sketch, "E99.17.51", {"start": v(-8.31, 1.68) * mm, "end": v(-8.32, 1.7) * mm});
            skLineSegment(sketch, "E99.17.52", {"start": v(-8.47, 1.78) * mm, "end": v(-8.51, 1.8) * mm});
            skLineSegment(sketch, "E99.17.53", {"start": v(-8.38, 1.73) * mm, "end": v(-8.4, 1.74) * mm});
            skLineSegment(sketch, "E99.17.54", {"start": v(-8.41, 1.75) * mm, "end": v(-8.43, 1.76) * mm});
            skLineSegment(sketch, "E99.17.55", {"start": v(-8.45, 1.24) * mm, "end": v(-8.47, 1.24) * mm});
            skLineSegment(sketch, "E99.17.56", {"start": v(-8.5, 1.23) * mm, "end": v(-8.52, 1.23) * mm});
            skLineSegment(sketch, "E99.17.57", {"start": v(-8.36, 1.72) * mm, "end": v(-8.38, 1.73) * mm});
            skLineSegment(sketch, "E99.17.58", {"start": v(-8.38, 1.26) * mm, "end": v(-8.4, 1.25) * mm});
            skLineSegment(sketch, "E99.17.59", {"start": v(-8.43, 1.76) * mm, "end": v(-8.47, 1.78) * mm});
            skLineSegment(sketch, "E99.17.60", {"start": v(-8.48, 1.23) * mm, "end": v(-8.5, 1.23) * mm});
            skLineSegment(sketch, "E99.17.61", {"start": v(-8.42, 1.25) * mm, "end": v(-8.43, 1.24) * mm});
            skLineSegment(sketch, "E99.17.62", {"start": v(-8.4, 1.74) * mm, "end": v(-8.41, 1.75) * mm});
            skLineSegment(sketch, "E99.17.63", {"start": v(-8.47, 1.24) * mm, "end": v(-8.48, 1.23) * mm});
            skLineSegment(sketch, "E99.17.64", {"start": v(-8.37, 1.27) * mm, "end": v(-8.38, 1.26) * mm});
            skLineSegment(sketch, "E99.17.65", {"start": v(-8.3, 1.67) * mm, "end": v(-8.31, 1.68) * mm});
            skLineSegment(sketch, "E99.17.66", {"start": v(-8.32, 1.7) * mm, "end": v(-8.34, 1.7) * mm});
            skLineSegment(sketch, "E99.17.67", {"start": v(-8.36, 1.28) * mm, "end": v(-8.37, 1.27) * mm});
            skLineSegment(sketch, "E99.17.68", {"start": v(-8.34, 1.7) * mm, "end": v(-8.35, 1.71) * mm});
            skLineSegment(sketch, "E99.17.69", {"start": v(-8.29, 1.66) * mm, "end": v(-8.3, 1.67) * mm});
            skLineSegment(sketch, "E99.17.70", {"start": v(-8.26, 1.62) * mm, "end": v(-8.27, 1.63) * mm});
            skLineSegment(sketch, "E99.17.71", {"start": v(-8.28, 1.65) * mm, "end": v(-8.29, 1.66) * mm});
            skLineSegment(sketch, "E99.17.72", {"start": v(-8.27, 1.63) * mm, "end": v(-8.28, 1.65) * mm});
            skLineSegment(sketch, "E99.17.73", {"start": v(-8.25, 1.59) * mm, "end": v(-8.26, 1.6) * mm});
            skLineSegment(sketch, "E99.17.74", {"start": v(-8.34, 1.29) * mm, "end": v(-8.36, 1.28) * mm});
            skLineSegment(sketch, "E99.17.75", {"start": v(-8.26, 1.6) * mm, "end": v(-8.26, 1.62) * mm});
            skLineSegment(sketch, "E99.17.76", {"start": v(-8.25, 1.45) * mm, "end": v(-8.25, 1.46) * mm});
            skLineSegment(sketch, "E99.17.77", {"start": v(-8.24, 1.51) * mm, "end": v(-8.24, 1.53) * mm});
            skLineSegment(sketch, "E99.17.78", {"start": v(-8.24, 1.48) * mm, "end": v(-8.24, 1.51) * mm});
            skLineSegment(sketch, "E99.17.79", {"start": v(-8.25, 1.42) * mm, "end": v(-8.26, 1.4) * mm});
            skLineSegment(sketch, "E99.17.80", {"start": v(-8.3, 1.33) * mm, "end": v(-8.3, 1.32) * mm});
            skLineSegment(sketch, "E99.17.81", {"start": v(-8.32, 1.3) * mm, "end": v(-8.33, 1.3) * mm});
            skLineSegment(sketch, "E99.17.82", {"start": v(-8.24, 1.57) * mm, "end": v(-8.25, 1.59) * mm});
            skLineSegment(sketch, "E99.17.83", {"start": v(-8.27, 1.38) * mm, "end": v(-8.28, 1.36) * mm});
            skLineSegment(sketch, "E99.17.84", {"start": v(-8.33, 1.3) * mm, "end": v(-8.34, 1.29) * mm});
            skLineSegment(sketch, "E99.17.85", {"start": v(-8.24, 1.53) * mm, "end": v(-8.24, 1.55) * mm});
            skLineSegment(sketch, "E99.17.86", {"start": v(-8.3, 1.32) * mm, "end": v(-8.32, 1.3) * mm});
            skLineSegment(sketch, "E99.17.87", {"start": v(-8.26, 1.4) * mm, "end": v(-8.27, 1.38) * mm});
            skLineSegment(sketch, "E99.17.88", {"start": v(-8.28, 1.34) * mm, "end": v(-8.3, 1.33) * mm});
            skLineSegment(sketch, "E99.17.89", {"start": v(-8.25, 1.47) * mm, "end": v(-8.24, 1.47) * mm});
            skLineSegment(sketch, "E99.17.90", {"start": v(-8.24, 1.48) * mm, "end": v(-8.24, 1.48) * mm});
            skLineSegment(sketch, "E99.17.91", {"start": v(-8.24, 1.55) * mm, "end": v(-8.24, 1.57) * mm});
            skLineSegment(sketch, "E99.17.92", {"start": v(-8.28, 1.36) * mm, "end": v(-8.28, 1.34) * mm});
            skLineSegment(sketch, "E99.17.93", {"start": v(-8.25, 1.43) * mm, "end": v(-8.25, 1.42) * mm});
            skLineSegment(sketch, "E99.17.94", {"start": v(-8.25, 1.44) * mm, "end": v(-8.25, 1.43) * mm});
            skLineSegment(sketch, "E99.17.95", {"start": v(-8.25, 1.44) * mm, "end": v(-8.25, 1.44) * mm});
            skLineSegment(sketch, "E99.17.96", {"start": v(-8.25, 1.45) * mm, "end": v(-8.25, 1.44) * mm});
            skLineSegment(sketch, "E99.17.97", {"start": v(-8.25, 1.45) * mm, "end": v(-8.25, 1.45) * mm});
            skLineSegment(sketch, "E99.17.98", {"start": v(-8.24, 1.47) * mm, "end": v(-8.24, 1.48) * mm});
            skLineSegment(sketch, "E99.17.99", {"start": v(-8.25, 1.46) * mm, "end": v(-8.25, 1.47) * mm});
            skLineSegment(sketch, "E99.18.0", {"start": v(-9.3, 0.54) * mm, "end": v(-9.35, 0.57) * mm});
            skLineSegment(sketch, "E99.18.1", {"start": v(-9.3, -0.54) * mm, "end": v(-9.35, -0.57) * mm});
            skLineSegment(sketch, "E99.18.2", {"start": v(-9.47, 0.8) * mm, "end": v(-9.46, 0.83) * mm});
            skLineSegment(sketch, "E99.18.3", {"start": v(-9.47, 0.75) * mm, "end": v(-9.47, 0.8) * mm});
            skLineSegment(sketch, "E99.18.4", {"start": v(-9.13, 0.46) * mm, "end": v(-9.18, 0.48) * mm});
            skLineSegment(sketch, "E99.18.5", {"start": v(-8.91, -0.36) * mm, "end": v(-8.96, -0.38) * mm});
            skLineSegment(sketch, "E99.18.6", {"start": v(-9.05, 0.42) * mm, "end": v(-9.09, 0.44) * mm});
            skLineSegment(sketch, "E99.18.7", {"start": v(-8.74, 0.3) * mm, "end": v(-8.78, 0.32) * mm});
            skLineSegment(sketch, "E99.18.8", {"start": v(-9.09, 0.44) * mm, "end": v(-9.13, 0.46) * mm});
            skLineSegment(sketch, "E99.18.9", {"start": v(-8.83, 0.33) * mm, "end": v(-8.87, 0.35) * mm});
            skLineSegment(sketch, "E99.18.10", {"start": v(-9, -0.4) * mm, "end": v(-9.05, -0.42) * mm});
            skLineSegment(sketch, "E99.18.11", {"start": v(-8.78, -0.32) * mm, "end": v(-8.83, -0.33) * mm});
            skLineSegment(sketch, "E99.18.12", {"start": v(-9.09, -0.44) * mm, "end": v(-9.13, -0.46) * mm});
            skLineSegment(sketch, "E99.18.13", {"start": v(-8.96, 0.38) * mm, "end": v(-9, 0.4) * mm});
            skLineSegment(sketch, "E99.18.14", {"start": v(-9.35, 0.57) * mm, "end": v(-9.4, 0.6) * mm});
            skLineSegment(sketch, "E99.18.15", {"start": v(-8.91, 0.36) * mm, "end": v(-8.96, 0.38) * mm});
            skLineSegment(sketch, "E99.18.16", {"start": v(-9.26, 0.52) * mm, "end": v(-9.3, 0.54) * mm});
            skLineSegment(sketch, "E99.18.17", {"start": v(-9, 0.4) * mm, "end": v(-9.05, 0.42) * mm});
            skLineSegment(sketch, "E99.18.18", {"start": v(-9.26, -0.52) * mm, "end": v(-9.3, -0.54) * mm});
            skLineSegment(sketch, "E99.18.19", {"start": v(-9.4, 0.6) * mm, "end": v(-9.44, 0.61) * mm});
            skLineSegment(sketch, "E99.18.20", {"start": v(-9.47, 0.72) * mm, "end": v(-9.47, 0.75) * mm});
            skLineSegment(sketch, "E99.18.21", {"start": v(-8.74, -0.3) * mm, "end": v(-8.78, -0.32) * mm});
            skLineSegment(sketch, "E99.18.22", {"start": v(-8.87, -0.35) * mm, "end": v(-8.91, -0.36) * mm});
            skLineSegment(sketch, "E99.18.23", {"start": v(-9.18, -0.48) * mm, "end": v(-9.22, -0.5) * mm});
            skLineSegment(sketch, "E99.18.24", {"start": v(-9.18, 0.48) * mm, "end": v(-9.22, 0.5) * mm});
            skLineSegment(sketch, "E99.18.25", {"start": v(-8.78, 0.32) * mm, "end": v(-8.83, 0.33) * mm});
            skLineSegment(sketch, "E99.18.26", {"start": v(-9.44, 0.61) * mm, "end": v(-9.48, 0.64) * mm});
            skLineSegment(sketch, "E99.18.27", {"start": v(-9.48, 0.68) * mm, "end": v(-9.47, 0.72) * mm});
            skLineSegment(sketch, "E99.18.28", {"start": v(-9.22, 0.5) * mm, "end": v(-9.26, 0.52) * mm});
            skLineSegment(sketch, "E99.18.29", {"start": v(-8.96, -0.38) * mm, "end": v(-9, -0.4) * mm});
            skLineSegment(sketch, "E99.18.30", {"start": v(-9.22, -0.5) * mm, "end": v(-9.26, -0.52) * mm});
            skLineSegment(sketch, "E99.18.31", {"start": v(-8.87, 0.35) * mm, "end": v(-8.91, 0.36) * mm});
            skLineSegment(sketch, "E99.18.32", {"start": v(-9.13, -0.46) * mm, "end": v(-9.18, -0.48) * mm});
            skLineSegment(sketch, "E99.18.33", {"start": v(-8.83, -0.33) * mm, "end": v(-8.87, -0.35) * mm});
            skLineSegment(sketch, "E99.18.34", {"start": v(-9.35, -0.57) * mm, "end": v(-9.4, -0.6) * mm});
            skLineSegment(sketch, "E99.18.35", {"start": v(-9.47, -0.8) * mm, "end": v(-9.46, -0.83) * mm});
            skLineSegment(sketch, "E99.18.36", {"start": v(-9.05, -0.42) * mm, "end": v(-9.09, -0.44) * mm});
            skLineSegment(sketch, "E99.18.37", {"start": v(-9.47, -0.75) * mm, "end": v(-9.47, -0.8) * mm});
            skLineSegment(sketch, "E99.18.38", {"start": v(-9.4, -0.6) * mm, "end": v(-9.44, -0.61) * mm});
            skLineSegment(sketch, "E99.18.39", {"start": v(-9.48, 0.64) * mm, "end": v(-9.48, 0.68) * mm});
            skLineSegment(sketch, "E99.18.40", {"start": v(-9.44, -0.61) * mm, "end": v(-9.48, -0.64) * mm});
            skLineSegment(sketch, "E99.18.41", {"start": v(-9.47, -0.72) * mm, "end": v(-9.47, -0.75) * mm});
            skLineSegment(sketch, "E99.18.42", {"start": v(-9.48, -0.68) * mm, "end": v(-9.47, -0.72) * mm});
            skLineSegment(sketch, "E99.18.43", {"start": v(-8.7, -0.29) * mm, "end": v(-8.74, -0.3) * mm});
            skLineSegment(sketch, "E99.18.44", {"start": v(-9.48, -0.64) * mm, "end": v(-9.48, -0.68) * mm});
            skLineSegment(sketch, "E99.18.45", {"start": v(-8.7, 0.29) * mm, "end": v(-8.74, 0.3) * mm});
            skLineSegment(sketch, "E99.18.46", {"start": v(-8.5, -0.22) * mm, "end": v(-8.5, -0.23) * mm});
            skLineSegment(sketch, "E99.18.47", {"start": v(-8.6, -0.27) * mm, "end": v(-8.65, -0.28) * mm});
            skLineSegment(sketch, "E99.18.48", {"start": v(-8.65, -0.28) * mm, "end": v(-8.7, -0.29) * mm});
            skLineSegment(sketch, "E99.18.49", {"start": v(-8.52, 0.24) * mm, "end": v(-8.54, 0.25) * mm});
            skLineSegment(sketch, "E99.18.50", {"start": v(-8.52, -0.24) * mm, "end": v(-8.54, -0.25) * mm});
            skLineSegment(sketch, "E99.18.51", {"start": v(-8.48, 0.21) * mm, "end": v(-8.5, 0.22) * mm});
            skLineSegment(sketch, "E99.18.52", {"start": v(-8.65, 0.28) * mm, "end": v(-8.7, 0.29) * mm});
            skLineSegment(sketch, "E99.18.53", {"start": v(-8.55, 0.25) * mm, "end": v(-8.57, 0.26) * mm});
            skLineSegment(sketch, "E99.18.54", {"start": v(-8.59, 0.26) * mm, "end": v(-8.6, 0.27) * mm});
            skLineSegment(sketch, "E99.18.55", {"start": v(-8.54, -0.25) * mm, "end": v(-8.55, -0.25) * mm});
            skLineSegment(sketch, "E99.18.56", {"start": v(-8.59, -0.26) * mm, "end": v(-8.6, -0.27) * mm});
            skLineSegment(sketch, "E99.18.57", {"start": v(-8.54, 0.25) * mm, "end": v(-8.55, 0.25) * mm});
            skLineSegment(sketch, "E99.18.58", {"start": v(-8.48, -0.21) * mm, "end": v(-8.5, -0.22) * mm});
            skLineSegment(sketch, "E99.18.59", {"start": v(-8.6, 0.27) * mm, "end": v(-8.65, 0.28) * mm});
            skLineSegment(sketch, "E99.18.60", {"start": v(-8.57, -0.26) * mm, "end": v(-8.59, -0.26) * mm});
            skLineSegment(sketch, "E99.18.61", {"start": v(-8.5, -0.23) * mm, "end": v(-8.52, -0.24) * mm});
            skLineSegment(sketch, "E99.18.62", {"start": v(-8.57, 0.26) * mm, "end": v(-8.59, 0.26) * mm});
            skLineSegment(sketch, "E99.18.63", {"start": v(-8.55, -0.25) * mm, "end": v(-8.57, -0.26) * mm});
            skLineSegment(sketch, "E99.18.64", {"start": v(-8.46, -0.2) * mm, "end": v(-8.48, -0.21) * mm});
            skLineSegment(sketch, "E99.18.65", {"start": v(-8.46, 0.2) * mm, "end": v(-8.48, 0.21) * mm});
            skLineSegment(sketch, "E99.18.66", {"start": v(-8.5, 0.22) * mm, "end": v(-8.5, 0.23) * mm});
            skLineSegment(sketch, "E99.18.67", {"start": v(-8.45, -0.2) * mm, "end": v(-8.46, -0.2) * mm});
            skLineSegment(sketch, "E99.18.68", {"start": v(-8.5, 0.23) * mm, "end": v(-8.52, 0.24) * mm});
            skLineSegment(sketch, "E99.18.69", {"start": v(-8.45, 0.2) * mm, "end": v(-8.46, 0.2) * mm});
            skLineSegment(sketch, "E99.18.70", {"start": v(-8.42, 0.16) * mm, "end": v(-8.43, 0.17) * mm});
            skLineSegment(sketch, "E99.18.71", {"start": v(-8.44, 0.18) * mm, "end": v(-8.45, 0.2) * mm});
            skLineSegment(sketch, "E99.18.72", {"start": v(-8.43, 0.17) * mm, "end": v(-8.44, 0.18) * mm});
            skLineSegment(sketch, "E99.18.73", {"start": v(-8.4, 0.13) * mm, "end": v(-8.4, 0.14) * mm});
            skLineSegment(sketch, "E99.18.74", {"start": v(-8.44, -0.18) * mm, "end": v(-8.45, -0.2) * mm});
            skLineSegment(sketch, "E99.18.75", {"start": v(-8.4, 0.14) * mm, "end": v(-8.42, 0.16) * mm});
            skLineSegment(sketch, "E99.18.76", {"start": v(-8.38, 0) * mm, "end": v(-8.37, 0) * mm});
            skLineSegment(sketch, "E99.18.77", {"start": v(-8.38, 0.06) * mm, "end": v(-8.38, 0.08) * mm});
            skLineSegment(sketch, "E99.18.78", {"start": v(-8.37, 0.03) * mm, "end": v(-8.38, 0.06) * mm});
            skLineSegment(sketch, "E99.18.79", {"start": v(-8.37, -0.03) * mm, "end": v(-8.38, -0.06) * mm});
            skLineSegment(sketch, "E99.18.80", {"start": v(-8.4, -0.13) * mm, "end": v(-8.4, -0.14) * mm});
            skLineSegment(sketch, "E99.18.81", {"start": v(-8.42, -0.16) * mm, "end": v(-8.43, -0.17) * mm});
            skLineSegment(sketch, "E99.18.82", {"start": v(-8.4, 0.11) * mm, "end": v(-8.4, 0.13) * mm});
            skLineSegment(sketch, "E99.18.83", {"start": v(-8.38, -0.08) * mm, "end": v(-8.39, -0.1) * mm});
            skLineSegment(sketch, "E99.18.84", {"start": v(-8.43, -0.17) * mm, "end": v(-8.44, -0.18) * mm});
            skLineSegment(sketch, "E99.18.85", {"start": v(-8.38, 0.08) * mm, "end": v(-8.39, 0.1) * mm});
            skLineSegment(sketch, "E99.18.86", {"start": v(-8.4, -0.14) * mm, "end": v(-8.42, -0.16) * mm});
            skLineSegment(sketch, "E99.18.87", {"start": v(-8.38, -0.06) * mm, "end": v(-8.38, -0.08) * mm});
            skLineSegment(sketch, "E99.18.88", {"start": v(-8.4, -0.11) * mm, "end": v(-8.4, -0.13) * mm});
            skLineSegment(sketch, "E99.18.89", {"start": v(-8.37, 0.01) * mm, "end": v(-8.37, 0.02) * mm});
            skLineSegment(sketch, "E99.18.90", {"start": v(-8.37, 0.02) * mm, "end": v(-8.37, 0.03) * mm});
            skLineSegment(sketch, "E99.18.91", {"start": v(-8.39, 0.1) * mm, "end": v(-8.4, 0.11) * mm});
            skLineSegment(sketch, "E99.18.92", {"start": v(-8.39, -0.1) * mm, "end": v(-8.4, -0.11) * mm});
            skLineSegment(sketch, "E99.18.93", {"start": v(-8.37, -0.02) * mm, "end": v(-8.37, -0.03) * mm});
            skLineSegment(sketch, "E99.18.94", {"start": v(-8.37, -0.02) * mm, "end": v(-8.37, -0.02) * mm});
            skLineSegment(sketch, "E99.18.95", {"start": v(-8.37, -0.01) * mm, "end": v(-8.37, -0.02) * mm});
            skLineSegment(sketch, "E99.18.96", {"start": v(-8.37, 0) * mm, "end": v(-8.37, -0.01) * mm});
            skLineSegment(sketch, "E99.18.97", {"start": v(-8.38, 0) * mm, "end": v(-8.37, 0) * mm});
            skLineSegment(sketch, "E99.18.98", {"start": v(-8.37, 0.02) * mm, "end": v(-8.37, 0.02) * mm});
            skLineSegment(sketch, "E99.18.99", {"start": v(-8.37, 0) * mm, "end": v(-8.37, 0.01) * mm});
            skLineSegment(sketch, "E99.19.0", {"start": v(-9.26, -1.08) * mm, "end": v(-9.3, -1.07) * mm});
            skLineSegment(sketch, "E99.19.1", {"start": v(-9.07, -2.15) * mm, "end": v(-9.1, -2.18) * mm});
            skLineSegment(sketch, "E99.19.2", {"start": v(-9.46, -0.87) * mm, "end": v(-9.46, -0.83) * mm});
            skLineSegment(sketch, "E99.19.3", {"start": v(-9.46, -0.9) * mm, "end": v(-9.46, -0.87) * mm});
            skLineSegment(sketch, "E99.19.4", {"start": v(-9.07, -1.14) * mm, "end": v(-9.12, -1.12) * mm});
            skLineSegment(sketch, "E99.19.5", {"start": v(-8.72, -1.9) * mm, "end": v(-8.76, -1.93) * mm});
            skLineSegment(sketch, "E99.19.6", {"start": v(-8.98, -1.16) * mm, "end": v(-9.03, -1.15) * mm});
            skLineSegment(sketch, "E99.19.7", {"start": v(-8.66, -1.22) * mm, "end": v(-8.7, -1.21) * mm});
            skLineSegment(sketch, "E99.19.8", {"start": v(-9.03, -1.15) * mm, "end": v(-9.07, -1.14) * mm});
            skLineSegment(sketch, "E99.19.9", {"start": v(-8.75, -1.2) * mm, "end": v(-8.8, -1.2) * mm});
            skLineSegment(sketch, "E99.19.10", {"start": v(-8.8, -1.95) * mm, "end": v(-8.84, -1.98) * mm});
            skLineSegment(sketch, "E99.19.11", {"start": v(-8.6, -1.84) * mm, "end": v(-8.64, -1.86) * mm});
            skLineSegment(sketch, "E99.19.12", {"start": v(-8.88, -2) * mm, "end": v(-8.92, -2.03) * mm});
            skLineSegment(sketch, "E99.19.13", {"start": v(-8.89, -1.18) * mm, "end": v(-8.93, -1.17) * mm});
            skLineSegment(sketch, "E99.19.14", {"start": v(-9.3, -1.07) * mm, "end": v(-9.35, -1.05) * mm});
            skLineSegment(sketch, "E99.19.15", {"start": v(-8.84, -1.2) * mm, "end": v(-8.89, -1.18) * mm});
            skLineSegment(sketch, "E99.19.16", {"start": v(-9.21, -1.1) * mm, "end": v(-9.26, -1.08) * mm});
            skLineSegment(sketch, "E99.19.17", {"start": v(-8.93, -1.17) * mm, "end": v(-8.98, -1.16) * mm});
            skLineSegment(sketch, "E99.19.18", {"start": v(-9.03, -2.12) * mm, "end": v(-9.07, -2.15) * mm});
            skLineSegment(sketch, "E99.19.19", {"start": v(-9.35, -1.05) * mm, "end": v(-9.4, -1.03) * mm});
            skLineSegment(sketch, "E99.19.20", {"start": v(-9.45, -0.94) * mm, "end": v(-9.46, -0.9) * mm});
            skLineSegment(sketch, "E99.19.21", {"start": v(-8.55, -1.81) * mm, "end": v(-8.6, -1.84) * mm});
            skLineSegment(sketch, "E99.19.22", {"start": v(-8.68, -1.88) * mm, "end": v(-8.72, -1.9) * mm});
            skLineSegment(sketch, "E99.19.23", {"start": v(-8.95, -2.06) * mm, "end": v(-9, -2.1) * mm});
            skLineSegment(sketch, "E99.19.24", {"start": v(-9.12, -1.12) * mm, "end": v(-9.17, -1.11) * mm});
            skLineSegment(sketch, "E99.19.25", {"start": v(-8.7, -1.21) * mm, "end": v(-8.75, -1.2) * mm});
            skLineSegment(sketch, "E99.19.26", {"start": v(-9.4, -1.03) * mm, "end": v(-9.45, -1.02) * mm});
            skLineSegment(sketch, "E99.19.27", {"start": v(-9.45, -0.98) * mm, "end": v(-9.45, -0.94) * mm});
            skLineSegment(sketch, "E99.19.28", {"start": v(-9.17, -1.11) * mm, "end": v(-9.21, -1.1) * mm});
            skLineSegment(sketch, "E99.19.29", {"start": v(-8.76, -1.93) * mm, "end": v(-8.8, -1.95) * mm});
            skLineSegment(sketch, "E99.19.30", {"start": v(-9, -2.1) * mm, "end": v(-9.03, -2.12) * mm});
            skLineSegment(sketch, "E99.19.31", {"start": v(-8.8, -1.2) * mm, "end": v(-8.84, -1.2) * mm});
            skLineSegment(sketch, "E99.19.32", {"start": v(-8.92, -2.03) * mm, "end": v(-8.95, -2.06) * mm});
            skLineSegment(sketch, "E99.19.33", {"start": v(-8.64, -1.86) * mm, "end": v(-8.68, -1.88) * mm});
            skLineSegment(sketch, "E99.19.34", {"start": v(-9.1, -2.18) * mm, "end": v(-9.15, -2.21) * mm});
            skLineSegment(sketch, "E99.19.35", {"start": v(-9.19, -2.42) * mm, "end": v(-9.18, -2.46) * mm});
            skLineSegment(sketch, "E99.19.36", {"start": v(-8.84, -1.98) * mm, "end": v(-8.88, -2) * mm});
            skLineSegment(sketch, "E99.19.37", {"start": v(-9.2, -2.39) * mm, "end": v(-9.19, -2.42) * mm});
            skLineSegment(sketch, "E99.19.38", {"start": v(-9.15, -2.21) * mm, "end": v(-9.19, -2.24) * mm});
            skLineSegment(sketch, "E99.19.39", {"start": v(-9.45, -1.02) * mm, "end": v(-9.45, -0.98) * mm});
            skLineSegment(sketch, "E99.19.40", {"start": v(-9.19, -2.24) * mm, "end": v(-9.22, -2.28) * mm});
            skLineSegment(sketch, "E99.19.41", {"start": v(-9.2, -2.35) * mm, "end": v(-9.2, -2.39) * mm});
            skLineSegment(sketch, "E99.19.42", {"start": v(-9.21, -2.31) * mm, "end": v(-9.2, -2.35) * mm});
            skLineSegment(sketch, "E99.19.43", {"start": v(-8.51, -1.8) * mm, "end": v(-8.55, -1.81) * mm});
            skLineSegment(sketch, "E99.19.44", {"start": v(-9.22, -2.28) * mm, "end": v(-9.21, -2.31) * mm});
            skLineSegment(sketch, "E99.19.45", {"start": v(-8.61, -1.23) * mm, "end": v(-8.66, -1.22) * mm});
            skLineSegment(sketch, "E99.19.46", {"start": v(-8.32, -1.7) * mm, "end": v(-8.34, -1.7) * mm});
            skLineSegment(sketch, "E99.19.47", {"start": v(-8.43, -1.76) * mm, "end": v(-8.47, -1.78) * mm});
            skLineSegment(sketch, "E99.19.48", {"start": v(-8.47, -1.78) * mm, "end": v(-8.51, -1.8) * mm});
            skLineSegment(sketch, "E99.19.49", {"start": v(-8.43, -1.24) * mm, "end": v(-8.45, -1.24) * mm});
            skLineSegment(sketch, "E99.19.50", {"start": v(-8.35, -1.71) * mm, "end": v(-8.36, -1.72) * mm});
            skLineSegment(sketch, "E99.19.51", {"start": v(-8.38, -1.26) * mm, "end": v(-8.4, -1.25) * mm});
            skLineSegment(sketch, "E99.19.52", {"start": v(-8.57, -1.23) * mm, "end": v(-8.61, -1.23) * mm});
            skLineSegment(sketch, "E99.19.53", {"start": v(-8.47, -1.24) * mm, "end": v(-8.48, -1.23) * mm});
            skLineSegment(sketch, "E99.19.54", {"start": v(-8.5, -1.23) * mm, "end": v(-8.52, -1.23) * mm});
            skLineSegment(sketch, "E99.19.55", {"start": v(-8.36, -1.72) * mm, "end": v(-8.38, -1.73) * mm});
            skLineSegment(sketch, "E99.19.56", {"start": v(-8.41, -1.75) * mm, "end": v(-8.43, -1.76) * mm});
            skLineSegment(sketch, "E99.19.57", {"start": v(-8.45, -1.24) * mm, "end": v(-8.47, -1.24) * mm});
            skLineSegment(sketch, "E99.19.58", {"start": v(-8.31, -1.68) * mm, "end": v(-8.32, -1.7) * mm});
            skLineSegment(sketch, "E99.19.59", {"start": v(-8.52, -1.23) * mm, "end": v(-8.57, -1.23) * mm});
            skLineSegment(sketch, "E99.19.60", {"start": v(-8.4, -1.74) * mm, "end": v(-8.41, -1.75) * mm});
            skLineSegment(sketch, "E99.19.61", {"start": v(-8.34, -1.7) * mm, "end": v(-8.35, -1.71) * mm});
            skLineSegment(sketch, "E99.19.62", {"start": v(-8.48, -1.23) * mm, "end": v(-8.5, -1.23) * mm});
            skLineSegment(sketch, "E99.19.63", {"start": v(-8.38, -1.73) * mm, "end": v(-8.4, -1.74) * mm});
            skLineSegment(sketch, "E99.19.64", {"start": v(-8.3, -1.67) * mm, "end": v(-8.31, -1.68) * mm});
            skLineSegment(sketch, "E99.19.65", {"start": v(-8.37, -1.27) * mm, "end": v(-8.38, -1.26) * mm});
            skLineSegment(sketch, "E99.19.66", {"start": v(-8.4, -1.25) * mm, "end": v(-8.42, -1.25) * mm});
            skLineSegment(sketch, "E99.19.67", {"start": v(-8.29, -1.66) * mm, "end": v(-8.3, -1.67) * mm});
            skLineSegment(sketch, "E99.19.68", {"start": v(-8.42, -1.25) * mm, "end": v(-8.43, -1.24) * mm});
            skLineSegment(sketch, "E99.19.69", {"start": v(-8.36, -1.28) * mm, "end": v(-8.37, -1.27) * mm});
            skLineSegment(sketch, "E99.19.70", {"start": v(-8.32, -1.3) * mm, "end": v(-8.33, -1.3) * mm});
            skLineSegment(sketch, "E99.19.71", {"start": v(-8.34, -1.29) * mm, "end": v(-8.36, -1.28) * mm});
            skLineSegment(sketch, "E99.19.72", {"start": v(-8.33, -1.3) * mm, "end": v(-8.34, -1.29) * mm});
            skLineSegment(sketch, "E99.19.73", {"start": v(-8.3, -1.33) * mm, "end": v(-8.3, -1.32) * mm});
            skLineSegment(sketch, "E99.19.74", {"start": v(-8.28, -1.65) * mm, "end": v(-8.29, -1.66) * mm});
            skLineSegment(sketch, "E99.19.75", {"start": v(-8.3, -1.32) * mm, "end": v(-8.32, -1.3) * mm});
            skLineSegment(sketch, "E99.19.76", {"start": v(-8.25, -1.45) * mm, "end": v(-8.25, -1.45) * mm});
            skLineSegment(sketch, "E99.19.77", {"start": v(-8.26, -1.4) * mm, "end": v(-8.27, -1.38) * mm});
            skLineSegment(sketch, "E99.19.78", {"start": v(-8.25, -1.42) * mm, "end": v(-8.26, -1.4) * mm});
            skLineSegment(sketch, "E99.19.79", {"start": v(-8.24, -1.48) * mm, "end": v(-8.24, -1.51) * mm});
            skLineSegment(sketch, "E99.19.80", {"start": v(-8.25, -1.59) * mm, "end": v(-8.26, -1.6) * mm});
            skLineSegment(sketch, "E99.19.81", {"start": v(-8.26, -1.62) * mm, "end": v(-8.27, -1.63) * mm});
            skLineSegment(sketch, "E99.19.82", {"start": v(-8.28, -1.34) * mm, "end": v(-8.3, -1.33) * mm});
            skLineSegment(sketch, "E99.19.83", {"start": v(-8.24, -1.53) * mm, "end": v(-8.24, -1.55) * mm});
            skLineSegment(sketch, "E99.19.84", {"start": v(-8.27, -1.63) * mm, "end": v(-8.28, -1.65) * mm});
            skLineSegment(sketch, "E99.19.85", {"start": v(-8.27, -1.38) * mm, "end": v(-8.28, -1.36) * mm});
            skLineSegment(sketch, "E99.19.86", {"start": v(-8.26, -1.6) * mm, "end": v(-8.26, -1.62) * mm});
            skLineSegment(sketch, "E99.19.87", {"start": v(-8.24, -1.51) * mm, "end": v(-8.24, -1.53) * mm});
            skLineSegment(sketch, "E99.19.88", {"start": v(-8.24, -1.57) * mm, "end": v(-8.25, -1.59) * mm});
            skLineSegment(sketch, "E99.19.89", {"start": v(-8.25, -1.44) * mm, "end": v(-8.25, -1.44) * mm});
            skLineSegment(sketch, "E99.19.90", {"start": v(-8.25, -1.43) * mm, "end": v(-8.25, -1.42) * mm});
            skLineSegment(sketch, "E99.19.91", {"start": v(-8.28, -1.36) * mm, "end": v(-8.28, -1.34) * mm});
            skLineSegment(sketch, "E99.19.92", {"start": v(-8.24, -1.55) * mm, "end": v(-8.24, -1.57) * mm});
            skLineSegment(sketch, "E99.19.93", {"start": v(-8.24, -1.48) * mm, "end": v(-8.24, -1.48) * mm});
            skLineSegment(sketch, "E99.19.94", {"start": v(-8.24, -1.47) * mm, "end": v(-8.24, -1.48) * mm});
            skLineSegment(sketch, "E99.19.95", {"start": v(-8.25, -1.47) * mm, "end": v(-8.24, -1.47) * mm});
            skLineSegment(sketch, "E99.19.96", {"start": v(-8.25, -1.46) * mm, "end": v(-8.25, -1.47) * mm});
            skLineSegment(sketch, "E99.19.97", {"start": v(-8.25, -1.45) * mm, "end": v(-8.25, -1.46) * mm});
            skLineSegment(sketch, "E99.19.98", {"start": v(-8.25, -1.44) * mm, "end": v(-8.25, -1.43) * mm});
            skLineSegment(sketch, "E99.19.99", {"start": v(-8.25, -1.45) * mm, "end": v(-8.25, -1.44) * mm});
            skLineSegment(sketch, "E99.20.0", {"start": v(-8.93, -2.67) * mm, "end": v(-8.98, -2.67) * mm});
            skLineSegment(sketch, "E99.20.1", {"start": v(-8.56, -3.7) * mm, "end": v(-8.6, -3.73) * mm});
            skLineSegment(sketch, "E99.20.2", {"start": v(-9.17, -2.5) * mm, "end": v(-9.18, -2.46) * mm});
            skLineSegment(sketch, "E99.20.3", {"start": v(-9.16, -2.53) * mm, "end": v(-9.17, -2.5) * mm});
            skLineSegment(sketch, "E99.20.4", {"start": v(-8.74, -2.7) * mm, "end": v(-8.79, -2.7) * mm});
            skLineSegment(sketch, "E99.20.5", {"start": v(-8.25, -3.39) * mm, "end": v(-8.29, -3.42) * mm});
            skLineSegment(sketch, "E99.20.6", {"start": v(-8.64, -2.7) * mm, "end": v(-8.69, -2.7) * mm});
            skLineSegment(sketch, "E99.20.7", {"start": v(-8.31, -2.7) * mm, "end": v(-8.36, -2.7) * mm});
            skLineSegment(sketch, "E99.20.8", {"start": v(-8.69, -2.7) * mm, "end": v(-8.74, -2.7) * mm});
            skLineSegment(sketch, "E99.20.9", {"start": v(-8.4, -2.7) * mm, "end": v(-8.45, -2.7) * mm});
            skLineSegment(sketch, "E99.20.10", {"start": v(-8.32, -3.45) * mm, "end": v(-8.36, -3.48) * mm});
            skLineSegment(sketch, "E99.20.11", {"start": v(-8.15, -3.3) * mm, "end": v(-8.18, -3.33) * mm});
            skLineSegment(sketch, "E99.20.12", {"start": v(-8.4, -3.52) * mm, "end": v(-8.43, -3.55) * mm});
            skLineSegment(sketch, "E99.20.13", {"start": v(-8.55, -2.7) * mm, "end": v(-8.6, -2.7) * mm});
            skLineSegment(sketch, "E99.20.14", {"start": v(-8.98, -2.67) * mm, "end": v(-9.03, -2.66) * mm});
            skLineSegment(sketch, "E99.20.15", {"start": v(-8.5, -2.7) * mm, "end": v(-8.55, -2.7) * mm});
            skLineSegment(sketch, "E99.20.16", {"start": v(-8.88, -2.68) * mm, "end": v(-8.93, -2.67) * mm});
            skLineSegment(sketch, "E99.20.17", {"start": v(-8.6, -2.7) * mm, "end": v(-8.64, -2.7) * mm});
            skLineSegment(sketch, "E99.20.18", {"start": v(-8.53, -3.66) * mm, "end": v(-8.56, -3.7) * mm});
            skLineSegment(sketch, "E99.20.19", {"start": v(-9.03, -2.66) * mm, "end": v(-9.08, -2.65) * mm});
            skLineSegment(sketch, "E99.20.20", {"start": v(-9.15, -2.57) * mm, "end": v(-9.16, -2.53) * mm});
            skLineSegment(sketch, "E99.20.21", {"start": v(-8.1, -3.27) * mm, "end": v(-8.15, -3.3) * mm});
            skLineSegment(sketch, "E99.20.22", {"start": v(-8.22, -3.36) * mm, "end": v(-8.25, -3.39) * mm});
            skLineSegment(sketch, "E99.20.23", {"start": v(-8.46, -3.59) * mm, "end": v(-8.5, -3.62) * mm});
            skLineSegment(sketch, "E99.20.24", {"start": v(-8.79, -2.7) * mm, "end": v(-8.83, -2.69) * mm});
            skLineSegment(sketch, "E99.20.25", {"start": v(-8.36, -2.7) * mm, "end": v(-8.4, -2.7) * mm});
            skLineSegment(sketch, "E99.20.26", {"start": v(-9.08, -2.65) * mm, "end": v(-9.13, -2.64) * mm});
            skLineSegment(sketch, "E99.20.27", {"start": v(-9.14, -2.6) * mm, "end": v(-9.15, -2.57) * mm});
            skLineSegment(sketch, "E99.20.28", {"start": v(-8.83, -2.69) * mm, "end": v(-8.88, -2.68) * mm});
            skLineSegment(sketch, "E99.20.29", {"start": v(-8.29, -3.42) * mm, "end": v(-8.32, -3.45) * mm});
            skLineSegment(sketch, "E99.20.30", {"start": v(-8.5, -3.62) * mm, "end": v(-8.53, -3.66) * mm});
            skLineSegment(sketch, "E99.20.31", {"start": v(-8.45, -2.7) * mm, "end": v(-8.5, -2.7) * mm});
            skLineSegment(sketch, "E99.20.32", {"start": v(-8.43, -3.55) * mm, "end": v(-8.46, -3.59) * mm});
            skLineSegment(sketch, "E99.20.33", {"start": v(-8.18, -3.33) * mm, "end": v(-8.22, -3.36) * mm});
            skLineSegment(sketch, "E99.20.34", {"start": v(-8.6, -3.73) * mm, "end": v(-8.62, -3.77) * mm});
            skLineSegment(sketch, "E99.20.35", {"start": v(-8.63, -3.98) * mm, "end": v(-8.6, -4.01) * mm});
            skLineSegment(sketch, "E99.20.36", {"start": v(-8.36, -3.48) * mm, "end": v(-8.4, -3.52) * mm});
            skLineSegment(sketch, "E99.20.37", {"start": v(-8.64, -3.95) * mm, "end": v(-8.63, -3.98) * mm});
            skLineSegment(sketch, "E99.20.38", {"start": v(-8.62, -3.77) * mm, "end": v(-8.66, -3.8) * mm});
            skLineSegment(sketch, "E99.20.39", {"start": v(-9.13, -2.64) * mm, "end": v(-9.14, -2.6) * mm});
            skLineSegment(sketch, "E99.20.40", {"start": v(-8.66, -3.8) * mm, "end": v(-8.69, -3.84) * mm});
            skLineSegment(sketch, "E99.20.41", {"start": v(-8.66, -3.91) * mm, "end": v(-8.64, -3.95) * mm});
            skLineSegment(sketch, "E99.20.42", {"start": v(-8.67, -3.88) * mm, "end": v(-8.66, -3.91) * mm});
            skLineSegment(sketch, "E99.20.43", {"start": v(-8.07, -3.25) * mm, "end": v(-8.1, -3.27) * mm});
            skLineSegment(sketch, "E99.20.44", {"start": v(-8.69, -3.84) * mm, "end": v(-8.67, -3.88) * mm});
            skLineSegment(sketch, "E99.20.45", {"start": v(-8.27, -2.7) * mm, "end": v(-8.31, -2.7) * mm});
            skLineSegment(sketch, "E99.20.46", {"start": v(-7.9, -3.11) * mm, "end": v(-7.91, -3.13) * mm});
            skLineSegment(sketch, "E99.20.47", {"start": v(-8, -3.2) * mm, "end": v(-8.03, -3.22) * mm});
            skLineSegment(sketch, "E99.20.48", {"start": v(-8.03, -3.22) * mm, "end": v(-8.07, -3.25) * mm});
            skLineSegment(sketch, "E99.20.49", {"start": v(-8.09, -2.69) * mm, "end": v(-8.1, -2.69) * mm});
            skLineSegment(sketch, "E99.20.50", {"start": v(-7.92, -3.14) * mm, "end": v(-7.94, -3.15) * mm});
            skLineSegment(sketch, "E99.20.51", {"start": v(-8.04, -2.7) * mm, "end": v(-8.05, -2.7) * mm});
            skLineSegment(sketch, "E99.20.52", {"start": v(-8.22, -2.7) * mm, "end": v(-8.27, -2.7) * mm});
            skLineSegment(sketch, "E99.20.53", {"start": v(-8.12, -2.69) * mm, "end": v(-8.14, -2.69) * mm});
            skLineSegment(sketch, "E99.20.54", {"start": v(-8.16, -2.7) * mm, "end": v(-8.18, -2.7) * mm});
            skLineSegment(sketch, "E99.20.55", {"start": v(-7.94, -3.15) * mm, "end": v(-7.95, -3.16) * mm});
            skLineSegment(sketch, "E99.20.56", {"start": v(-7.98, -3.18) * mm, "end": v(-8, -3.2) * mm});
            skLineSegment(sketch, "E99.20.57", {"start": v(-8.1, -2.69) * mm, "end": v(-8.12, -2.69) * mm});
            skLineSegment(sketch, "E99.20.58", {"start": v(-7.9, -3.1) * mm, "end": v(-7.9, -3.11) * mm});
            skLineSegment(sketch, "E99.20.59", {"start": v(-8.18, -2.7) * mm, "end": v(-8.22, -2.7) * mm});
            skLineSegment(sketch, "E99.20.60", {"start": v(-7.97, -3.17) * mm, "end": v(-7.98, -3.18) * mm});
            skLineSegment(sketch, "E99.20.61", {"start": v(-7.91, -3.13) * mm, "end": v(-7.92, -3.14) * mm});
            skLineSegment(sketch, "E99.20.62", {"start": v(-8.14, -2.69) * mm, "end": v(-8.16, -2.7) * mm});
            skLineSegment(sketch, "E99.20.63", {"start": v(-7.95, -3.16) * mm, "end": v(-7.97, -3.17) * mm});
            skLineSegment(sketch, "E99.20.64", {"start": v(-7.88, -3.09) * mm, "end": v(-7.9, -3.1) * mm});
            skLineSegment(sketch, "E99.20.65", {"start": v(-8.02, -2.7) * mm, "end": v(-8.04, -2.7) * mm});
            skLineSegment(sketch, "E99.20.66", {"start": v(-8.05, -2.7) * mm, "end": v(-8.07, -2.7) * mm});
            skLineSegment(sketch, "E99.20.67", {"start": v(-7.87, -3.07) * mm, "end": v(-7.88, -3.09) * mm});
            skLineSegment(sketch, "E99.20.68", {"start": v(-8.07, -2.7) * mm, "end": v(-8.09, -2.69) * mm});
            skLineSegment(sketch, "E99.20.69", {"start": v(-8, -2.7) * mm, "end": v(-8.02, -2.7) * mm});
            skLineSegment(sketch, "E99.20.70", {"start": v(-7.96, -2.73) * mm, "end": v(-7.98, -2.72) * mm});
            skLineSegment(sketch, "E99.20.71", {"start": v(-8, -2.71) * mm, "end": v(-8, -2.7) * mm});
            skLineSegment(sketch, "E99.20.72", {"start": v(-7.98, -2.72) * mm, "end": v(-8, -2.71) * mm});
            skLineSegment(sketch, "E99.20.73", {"start": v(-7.94, -2.75) * mm, "end": v(-7.95, -2.74) * mm});
            skLineSegment(sketch, "E99.20.74", {"start": v(-7.87, -3.06) * mm, "end": v(-7.87, -3.07) * mm});
            skLineSegment(sketch, "E99.20.75", {"start": v(-7.95, -2.74) * mm, "end": v(-7.96, -2.73) * mm});
            skLineSegment(sketch, "E99.20.76", {"start": v(-7.87, -2.86) * mm, "end": v(-7.87, -2.86) * mm});
            skLineSegment(sketch, "E99.20.77", {"start": v(-7.9, -2.81) * mm, "end": v(-7.9, -2.8) * mm});
            skLineSegment(sketch, "E99.20.78", {"start": v(-7.88, -2.84) * mm, "end": v(-7.9, -2.81) * mm});
            skLineSegment(sketch, "E99.20.79", {"start": v(-7.86, -2.9) * mm, "end": v(-7.85, -2.92) * mm});
            skLineSegment(sketch, "E99.20.80", {"start": v(-7.85, -3) * mm, "end": v(-7.85, -3.01) * mm});
            skLineSegment(sketch, "E99.20.81", {"start": v(-7.86, -3.03) * mm, "end": v(-7.86, -3.04) * mm});
            skLineSegment(sketch, "E99.20.82", {"start": v(-7.93, -2.76) * mm, "end": v(-7.94, -2.75) * mm});
            skLineSegment(sketch, "E99.20.83", {"start": v(-7.85, -2.94) * mm, "end": v(-7.85, -2.96) * mm});
            skLineSegment(sketch, "E99.20.84", {"start": v(-7.86, -3.04) * mm, "end": v(-7.87, -3.06) * mm});
            skLineSegment(sketch, "E99.20.85", {"start": v(-7.9, -2.8) * mm, "end": v(-7.91, -2.78) * mm});
            skLineSegment(sketch, "E99.20.86", {"start": v(-7.85, -3.01) * mm, "end": v(-7.86, -3.03) * mm});
            skLineSegment(sketch, "E99.20.87", {"start": v(-7.85, -2.92) * mm, "end": v(-7.85, -2.94) * mm});
            skLineSegment(sketch, "E99.20.88", {"start": v(-7.85, -2.98) * mm, "end": v(-7.85, -3) * mm});
            skLineSegment(sketch, "E99.20.89", {"start": v(-7.87, -2.85) * mm, "end": v(-7.88, -2.85) * mm});
            skLineSegment(sketch, "E99.20.90", {"start": v(-7.88, -2.84) * mm, "end": v(-7.88, -2.84) * mm});
            skLineSegment(sketch, "E99.20.91", {"start": v(-7.91, -2.78) * mm, "end": v(-7.93, -2.76) * mm});
            skLineSegment(sketch, "E99.20.92", {"start": v(-7.85, -2.96) * mm, "end": v(-7.85, -2.98) * mm});
            skLineSegment(sketch, "E99.20.93", {"start": v(-7.86, -2.89) * mm, "end": v(-7.86, -2.9) * mm});
            skLineSegment(sketch, "E99.20.94", {"start": v(-7.86, -2.88) * mm, "end": v(-7.86, -2.89) * mm});
            skLineSegment(sketch, "E99.20.95", {"start": v(-7.87, -2.88) * mm, "end": v(-7.86, -2.88) * mm});
            skLineSegment(sketch, "E99.20.96", {"start": v(-7.87, -2.87) * mm, "end": v(-7.87, -2.88) * mm});
            skLineSegment(sketch, "E99.20.97", {"start": v(-7.87, -2.86) * mm, "end": v(-7.87, -2.87) * mm});
            skLineSegment(sketch, "E99.20.98", {"start": v(-7.88, -2.85) * mm, "end": v(-7.88, -2.84) * mm});
            skLineSegment(sketch, "E99.20.99", {"start": v(-7.87, -2.86) * mm, "end": v(-7.87, -2.85) * mm});
            skLineSegment(sketch, "E99.21.0", {"start": v(-8.33, -4.18) * mm, "end": v(-8.38, -4.18) * mm});
            skLineSegment(sketch, "E99.21.1", {"start": v(-7.79, -5.12) * mm, "end": v(-7.81, -5.16) * mm});
            skLineSegment(sketch, "E99.21.2", {"start": v(-8.6, -4.05) * mm, "end": v(-8.6, -4.01) * mm});
            skLineSegment(sketch, "E99.21.3", {"start": v(-8.58, -4.08) * mm, "end": v(-8.6, -4.05) * mm});
            skLineSegment(sketch, "E99.21.4", {"start": v(-8.14, -4.17) * mm, "end": v(-8.18, -4.18) * mm});
            skLineSegment(sketch, "E99.21.5", {"start": v(-7.54, -4.77) * mm, "end": v(-7.57, -4.8) * mm});
            skLineSegment(sketch, "E99.21.6", {"start": v(-8.04, -4.16) * mm, "end": v(-8.09, -4.17) * mm});
            skLineSegment(sketch, "E99.21.7", {"start": v(-7.72, -4.1) * mm, "end": v(-7.76, -4.12) * mm});
            skLineSegment(sketch, "E99.21.8", {"start": v(-8.09, -4.17) * mm, "end": v(-8.14, -4.17) * mm});
            skLineSegment(sketch, "E99.21.9", {"start": v(-7.8, -4.13) * mm, "end": v(-7.85, -4.14) * mm});
            skLineSegment(sketch, "E99.21.10", {"start": v(-7.6, -4.84) * mm, "end": v(-7.63, -4.88) * mm});
            skLineSegment(sketch, "E99.21.11", {"start": v(-7.45, -4.66) * mm, "end": v(-7.48, -4.7) * mm});
            skLineSegment(sketch, "E99.21.12", {"start": v(-7.65, -4.92) * mm, "end": v(-7.68, -4.96) * mm});
            skLineSegment(sketch, "E99.21.13", {"start": v(-7.95, -4.15) * mm, "end": v(-8, -4.16) * mm});
            skLineSegment(sketch, "E99.21.14", {"start": v(-8.38, -4.18) * mm, "end": v(-8.43, -4.19) * mm});
            skLineSegment(sketch, "E99.21.15", {"start": v(-7.9, -4.14) * mm, "end": v(-7.95, -4.15) * mm});
            skLineSegment(sketch, "E99.21.16", {"start": v(-8.28, -4.18) * mm, "end": v(-8.33, -4.18) * mm});
            skLineSegment(sketch, "E99.21.17", {"start": v(-8, -4.16) * mm, "end": v(-8.04, -4.16) * mm});
            skLineSegment(sketch, "E99.21.18", {"start": v(-7.76, -5.08) * mm, "end": v(-7.79, -5.12) * mm});
            skLineSegment(sketch, "E99.21.19", {"start": v(-8.43, -4.19) * mm, "end": v(-8.48, -4.19) * mm});
            skLineSegment(sketch, "E99.21.20", {"start": v(-8.56, -4.12) * mm, "end": v(-8.58, -4.08) * mm});
            skLineSegment(sketch, "E99.21.21", {"start": v(-7.42, -4.63) * mm, "end": v(-7.45, -4.66) * mm});
            skLineSegment(sketch, "E99.21.22", {"start": v(-7.5, -4.73) * mm, "end": v(-7.54, -4.77) * mm});
            skLineSegment(sketch, "E99.21.23", {"start": v(-7.7, -5) * mm, "end": v(-7.74, -5.04) * mm});
            skLineSegment(sketch, "E99.21.24", {"start": v(-8.18, -4.18) * mm, "end": v(-8.23, -4.18) * mm});
            skLineSegment(sketch, "E99.21.25", {"start": v(-7.76, -4.12) * mm, "end": v(-7.8, -4.13) * mm});
            skLineSegment(sketch, "E99.21.26", {"start": v(-8.48, -4.19) * mm, "end": v(-8.53, -4.18) * mm});
            skLineSegment(sketch, "E99.21.27", {"start": v(-8.55, -4.15) * mm, "end": v(-8.56, -4.12) * mm});
            skLineSegment(sketch, "E99.21.28", {"start": v(-8.23, -4.18) * mm, "end": v(-8.28, -4.18) * mm});
            skLineSegment(sketch, "E99.21.29", {"start": v(-7.57, -4.8) * mm, "end": v(-7.6, -4.84) * mm});
            skLineSegment(sketch, "E99.21.30", {"start": v(-7.74, -5.04) * mm, "end": v(-7.76, -5.08) * mm});
            skLineSegment(sketch, "E99.21.31", {"start": v(-7.85, -4.14) * mm, "end": v(-7.9, -4.14) * mm});
            skLineSegment(sketch, "E99.21.32", {"start": v(-7.68, -4.96) * mm, "end": v(-7.7, -5) * mm});
            skLineSegment(sketch, "E99.21.33", {"start": v(-7.48, -4.7) * mm, "end": v(-7.5, -4.73) * mm});
            skLineSegment(sketch, "E99.21.34", {"start": v(-7.81, -5.16) * mm, "end": v(-7.84, -5.2) * mm});
            skLineSegment(sketch, "E99.21.35", {"start": v(-7.8, -5.42) * mm, "end": v(-7.78, -5.45) * mm});
            skLineSegment(sketch, "E99.21.36", {"start": v(-7.63, -4.88) * mm, "end": v(-7.65, -4.92) * mm});
            skLineSegment(sketch, "E99.21.37", {"start": v(-7.82, -5.39) * mm, "end": v(-7.8, -5.42) * mm});
            skLineSegment(sketch, "E99.21.38", {"start": v(-7.84, -5.2) * mm, "end": v(-7.86, -5.25) * mm});
            skLineSegment(sketch, "E99.21.39", {"start": v(-8.53, -4.18) * mm, "end": v(-8.55, -4.15) * mm});
            skLineSegment(sketch, "E99.21.40", {"start": v(-7.86, -5.25) * mm, "end": v(-7.89, -5.3) * mm});
            skLineSegment(sketch, "E99.21.41", {"start": v(-7.85, -5.36) * mm, "end": v(-7.82, -5.39) * mm});
            skLineSegment(sketch, "E99.21.42", {"start": v(-7.87, -5.32) * mm, "end": v(-7.85, -5.36) * mm});
            skLineSegment(sketch, "E99.21.43", {"start": v(-7.39, -4.6) * mm, "end": v(-7.42, -4.63) * mm});
            skLineSegment(sketch, "E99.21.44", {"start": v(-7.89, -5.3) * mm, "end": v(-7.87, -5.32) * mm});
            skLineSegment(sketch, "E99.21.45", {"start": v(-7.67, -4.1) * mm, "end": v(-7.72, -4.1) * mm});
            skLineSegment(sketch, "E99.21.46", {"start": v(-7.24, -4.44) * mm, "end": v(-7.25, -4.45) * mm});
            skLineSegment(sketch, "E99.21.47", {"start": v(-7.32, -4.53) * mm, "end": v(-7.35, -4.57) * mm});
            skLineSegment(sketch, "E99.21.48", {"start": v(-7.35, -4.57) * mm, "end": v(-7.39, -4.6) * mm});
            skLineSegment(sketch, "E99.21.49", {"start": v(-7.5, -4.05) * mm, "end": v(-7.52, -4.06) * mm});
            skLineSegment(sketch, "E99.21.50", {"start": v(-7.26, -4.47) * mm, "end": v(-7.27, -4.48) * mm});
            skLineSegment(sketch, "E99.21.51", {"start": v(-7.45, -4.05) * mm, "end": v(-7.46, -4.05) * mm});
            skLineSegment(sketch, "E99.21.52", {"start": v(-7.63, -4.08) * mm, "end": v(-7.67, -4.1) * mm});
            skLineSegment(sketch, "E99.21.53", {"start": v(-7.53, -4.06) * mm, "end": v(-7.55, -4.06) * mm});
            skLineSegment(sketch, "E99.21.54", {"start": v(-7.57, -4.07) * mm, "end": v(-7.59, -4.07) * mm});
            skLineSegment(sketch, "E99.21.55", {"start": v(-7.27, -4.48) * mm, "end": v(-7.28, -4.5) * mm});
            skLineSegment(sketch, "E99.21.56", {"start": v(-7.3, -4.52) * mm, "end": v(-7.32, -4.53) * mm});
            skLineSegment(sketch, "E99.21.57", {"start": v(-7.52, -4.06) * mm, "end": v(-7.53, -4.06) * mm});
            skLineSegment(sketch, "E99.21.58", {"start": v(-7.23, -4.42) * mm, "end": v(-7.24, -4.44) * mm});
            skLineSegment(sketch, "E99.21.59", {"start": v(-7.59, -4.07) * mm, "end": v(-7.63, -4.08) * mm});
            skLineSegment(sketch, "E99.21.60", {"start": v(-7.3, -4.5) * mm, "end": v(-7.3, -4.52) * mm});
            skLineSegment(sketch, "E99.21.61", {"start": v(-7.25, -4.45) * mm, "end": v(-7.26, -4.47) * mm});
            skLineSegment(sketch, "E99.21.62", {"start": v(-7.55, -4.06) * mm, "end": v(-7.57, -4.07) * mm});
            skLineSegment(sketch, "E99.21.63", {"start": v(-7.28, -4.5) * mm, "end": v(-7.3, -4.5) * mm});
            skLineSegment(sketch, "E99.21.64", {"start": v(-7.23, -4.4) * mm, "end": v(-7.23, -4.42) * mm});
            skLineSegment(sketch, "E99.21.65", {"start": v(-7.43, -4.05) * mm, "end": v(-7.45, -4.05) * mm});
            skLineSegment(sketch, "E99.21.66", {"start": v(-7.46, -4.05) * mm, "end": v(-7.48, -4.05) * mm});
            skLineSegment(sketch, "E99.21.67", {"start": v(-7.22, -4.4) * mm, "end": v(-7.23, -4.4) * mm});
            skLineSegment(sketch, "E99.21.68", {"start": v(-7.48, -4.05) * mm, "end": v(-7.5, -4.05) * mm});
            skLineSegment(sketch, "E99.21.69", {"start": v(-7.42, -4.06) * mm, "end": v(-7.43, -4.05) * mm});
            skLineSegment(sketch, "E99.21.70", {"start": v(-7.37, -4.07) * mm, "end": v(-7.38, -4.07) * mm});
            skLineSegment(sketch, "E99.21.71", {"start": v(-7.4, -4.06) * mm, "end": v(-7.42, -4.06) * mm});
            skLineSegment(sketch, "E99.21.72", {"start": v(-7.38, -4.07) * mm, "end": v(-7.4, -4.06) * mm});
            skLineSegment(sketch, "E99.21.73", {"start": v(-7.34, -4.09) * mm, "end": v(-7.35, -4.08) * mm});
            skLineSegment(sketch, "E99.21.74", {"start": v(-7.22, -4.38) * mm, "end": v(-7.22, -4.4) * mm});
            skLineSegment(sketch, "E99.21.75", {"start": v(-7.35, -4.08) * mm, "end": v(-7.37, -4.07) * mm});
            skLineSegment(sketch, "E99.21.76", {"start": v(-7.25, -4.19) * mm, "end": v(-7.26, -4.18) * mm});
            skLineSegment(sketch, "E99.21.77", {"start": v(-7.28, -4.14) * mm, "end": v(-7.3, -4.12) * mm});
            skLineSegment(sketch, "E99.21.78", {"start": v(-7.27, -4.16) * mm, "end": v(-7.28, -4.14) * mm});
            skLineSegment(sketch, "E99.21.79", {"start": v(-7.24, -4.21) * mm, "end": v(-7.23, -4.24) * mm});
            skLineSegment(sketch, "E99.21.80", {"start": v(-7.2, -4.31) * mm, "end": v(-7.2, -4.33) * mm});
            skLineSegment(sketch, "E99.21.81", {"start": v(-7.21, -4.35) * mm, "end": v(-7.21, -4.36) * mm});
            skLineSegment(sketch, "E99.21.82", {"start": v(-7.32, -4.1) * mm, "end": v(-7.34, -4.09) * mm});
            skLineSegment(sketch, "E99.21.83", {"start": v(-7.22, -4.26) * mm, "end": v(-7.21, -4.28) * mm});
            skLineSegment(sketch, "E99.21.84", {"start": v(-7.21, -4.36) * mm, "end": v(-7.22, -4.38) * mm});
            skLineSegment(sketch, "E99.21.85", {"start": v(-7.3, -4.12) * mm, "end": v(-7.31, -4.1) * mm});
            skLineSegment(sketch, "E99.21.86", {"start": v(-7.2, -4.33) * mm, "end": v(-7.21, -4.35) * mm});
            skLineSegment(sketch, "E99.21.87", {"start": v(-7.23, -4.24) * mm, "end": v(-7.22, -4.26) * mm});
            skLineSegment(sketch, "E99.21.88", {"start": v(-7.21, -4.3) * mm, "end": v(-7.2, -4.31) * mm});
            skLineSegment(sketch, "E99.21.89", {"start": v(-7.26, -4.18) * mm, "end": v(-7.26, -4.17) * mm});
            skLineSegment(sketch, "E99.21.90", {"start": v(-7.26, -4.17) * mm, "end": v(-7.27, -4.16) * mm});
            skLineSegment(sketch, "E99.21.91", {"start": v(-7.31, -4.1) * mm, "end": v(-7.32, -4.1) * mm});
            skLineSegment(sketch, "E99.21.92", {"start": v(-7.21, -4.28) * mm, "end": v(-7.21, -4.3) * mm});
            skLineSegment(sketch, "E99.21.93", {"start": v(-7.24, -4.2) * mm, "end": v(-7.24, -4.21) * mm});
            skLineSegment(sketch, "E99.21.94", {"start": v(-7.24, -4.2) * mm, "end": v(-7.24, -4.2) * mm});
            skLineSegment(sketch, "E99.21.95", {"start": v(-7.25, -4.2) * mm, "end": v(-7.24, -4.2) * mm});
            skLineSegment(sketch, "E99.21.96", {"start": v(-7.25, -4.2) * mm, "end": v(-7.25, -4.2) * mm});
            skLineSegment(sketch, "E99.21.97", {"start": v(-7.25, -4.19) * mm, "end": v(-7.25, -4.2) * mm});
            skLineSegment(sketch, "E99.21.98", {"start": v(-7.26, -4.17) * mm, "end": v(-7.26, -4.17) * mm});
            skLineSegment(sketch, "E99.21.99", {"start": v(-7.26, -4.18) * mm, "end": v(-7.26, -4.18) * mm});
            skLineSegment(sketch, "E99.22.0", {"start": v(-7.48, -5.57) * mm, "end": v(-7.53, -5.58) * mm});
            skLineSegment(sketch, "E99.22.1", {"start": v(-6.78, -6.4) * mm, "end": v(-6.8, -6.44) * mm});
            skLineSegment(sketch, "E99.22.2", {"start": v(-7.76, -5.48) * mm, "end": v(-7.78, -5.45) * mm});
            skLineSegment(sketch, "E99.22.3", {"start": v(-7.74, -5.51) * mm, "end": v(-7.76, -5.48) * mm});
            skLineSegment(sketch, "E99.22.4", {"start": v(-7.29, -5.52) * mm, "end": v(-7.34, -5.53) * mm});
            skLineSegment(sketch, "E99.22.5", {"start": v(-6.6, -6) * mm, "end": v(-6.62, -6.05) * mm});
            skLineSegment(sketch, "E99.22.6", {"start": v(-7.2, -5.5) * mm, "end": v(-7.24, -5.5) * mm});
            skLineSegment(sketch, "E99.22.7", {"start": v(-6.89, -5.39) * mm, "end": v(-6.93, -5.4) * mm});
            skLineSegment(sketch, "E99.22.8", {"start": v(-7.24, -5.5) * mm, "end": v(-7.29, -5.52) * mm});
            skLineSegment(sketch, "E99.22.9", {"start": v(-6.97, -5.42) * mm, "end": v(-7.02, -5.44) * mm});
            skLineSegment(sketch, "E99.22.10", {"start": v(-6.64, -6.1) * mm, "end": v(-6.66, -6.13) * mm});
            skLineSegment(sketch, "E99.22.11", {"start": v(-6.53, -5.89) * mm, "end": v(-6.55, -5.93) * mm});
            skLineSegment(sketch, "E99.22.12", {"start": v(-6.68, -6.18) * mm, "end": v(-6.7, -6.22) * mm});
            skLineSegment(sketch, "E99.22.13", {"start": v(-7.1, -5.47) * mm, "end": v(-7.15, -5.48) * mm});
            skLineSegment(sketch, "E99.22.14", {"start": v(-7.53, -5.58) * mm, "end": v(-7.57, -5.59) * mm});
            skLineSegment(sketch, "E99.22.15", {"start": v(-7.06, -5.45) * mm, "end": v(-7.1, -5.47) * mm});
            skLineSegment(sketch, "E99.22.16", {"start": v(-7.43, -5.56) * mm, "end": v(-7.48, -5.57) * mm});
            skLineSegment(sketch, "E99.22.17", {"start": v(-7.15, -5.48) * mm, "end": v(-7.2, -5.5) * mm});
            skLineSegment(sketch, "E99.22.18", {"start": v(-6.76, -6.35) * mm, "end": v(-6.78, -6.4) * mm});
            skLineSegment(sketch, "E99.22.19", {"start": v(-7.57, -5.59) * mm, "end": v(-7.62, -5.6) * mm});
            skLineSegment(sketch, "E99.22.20", {"start": v(-7.72, -5.54) * mm, "end": v(-7.74, -5.51) * mm});
            skLineSegment(sketch, "E99.22.21", {"start": v(-6.5, -5.85) * mm, "end": v(-6.53, -5.89) * mm});
            skLineSegment(sketch, "E99.22.22", {"start": v(-6.57, -5.97) * mm, "end": v(-6.6, -6) * mm});
            skLineSegment(sketch, "E99.22.23", {"start": v(-6.72, -6.26) * mm, "end": v(-6.74, -6.3) * mm});
            skLineSegment(sketch, "E99.22.24", {"start": v(-7.34, -5.53) * mm, "end": v(-7.38, -5.55) * mm});
            skLineSegment(sketch, "E99.22.25", {"start": v(-6.93, -5.4) * mm, "end": v(-6.97, -5.42) * mm});
            skLineSegment(sketch, "E99.22.26", {"start": v(-7.62, -5.6) * mm, "end": v(-7.67, -5.6) * mm});
            skLineSegment(sketch, "E99.22.27", {"start": v(-7.7, -5.57) * mm, "end": v(-7.72, -5.54) * mm});
            skLineSegment(sketch, "E99.22.28", {"start": v(-7.38, -5.55) * mm, "end": v(-7.43, -5.56) * mm});
            skLineSegment(sketch, "E99.22.29", {"start": v(-6.62, -6.05) * mm, "end": v(-6.64, -6.1) * mm});
            skLineSegment(sketch, "E99.22.30", {"start": v(-6.74, -6.3) * mm, "end": v(-6.76, -6.35) * mm});
            skLineSegment(sketch, "E99.22.31", {"start": v(-7.02, -5.44) * mm, "end": v(-7.06, -5.45) * mm});
            skLineSegment(sketch, "E99.22.32", {"start": v(-6.7, -6.22) * mm, "end": v(-6.72, -6.26) * mm});
            skLineSegment(sketch, "E99.22.33", {"start": v(-6.55, -5.93) * mm, "end": v(-6.57, -5.97) * mm});
            skLineSegment(sketch, "E99.22.34", {"start": v(-6.8, -6.44) * mm, "end": v(-6.82, -6.49) * mm});
            skLineSegment(sketch, "E99.22.35", {"start": v(-6.74, -6.7) * mm, "end": v(-6.72, -6.72) * mm});
            skLineSegment(sketch, "E99.22.36", {"start": v(-6.66, -6.13) * mm, "end": v(-6.68, -6.18) * mm});
            skLineSegment(sketch, "E99.22.37", {"start": v(-6.77, -6.66) * mm, "end": v(-6.74, -6.7) * mm});
            skLineSegment(sketch, "E99.22.38", {"start": v(-6.82, -6.49) * mm, "end": v(-6.83, -6.54) * mm});
            skLineSegment(sketch, "E99.22.39", {"start": v(-7.67, -5.6) * mm, "end": v(-7.7, -5.57) * mm});
            skLineSegment(sketch, "E99.22.40", {"start": v(-6.83, -6.54) * mm, "end": v(-6.85, -6.58) * mm});
            skLineSegment(sketch, "E99.22.41", {"start": v(-6.8, -6.64) * mm, "end": v(-6.77, -6.66) * mm});
            skLineSegment(sketch, "E99.22.42", {"start": v(-6.82, -6.61) * mm, "end": v(-6.8, -6.64) * mm});
            skLineSegment(sketch, "E99.22.43", {"start": v(-6.47, -5.81) * mm, "end": v(-6.5, -5.85) * mm});
            skLineSegment(sketch, "E99.22.44", {"start": v(-6.85, -6.58) * mm, "end": v(-6.82, -6.61) * mm});
            skLineSegment(sketch, "E99.22.45", {"start": v(-6.85, -5.37) * mm, "end": v(-6.89, -5.39) * mm});
            skLineSegment(sketch, "E99.22.46", {"start": v(-6.36, -5.63) * mm, "end": v(-6.37, -5.64) * mm});
            skLineSegment(sketch, "E99.22.47", {"start": v(-6.42, -5.74) * mm, "end": v(-6.45, -5.77) * mm});
            skLineSegment(sketch, "E99.22.48", {"start": v(-6.45, -5.77) * mm, "end": v(-6.47, -5.81) * mm});
            skLineSegment(sketch, "E99.22.49", {"start": v(-6.68, -5.3) * mm, "end": v(-6.7, -5.3) * mm});
            skLineSegment(sketch, "E99.22.50", {"start": v(-6.37, -5.66) * mm, "end": v(-6.38, -5.68) * mm});
            skLineSegment(sketch, "E99.22.51", {"start": v(-6.63, -5.28) * mm, "end": v(-6.65, -5.29) * mm});
            skLineSegment(sketch, "E99.22.52", {"start": v(-6.8, -5.35) * mm, "end": v(-6.85, -5.37) * mm});
            skLineSegment(sketch, "E99.22.53", {"start": v(-6.71, -5.3) * mm, "end": v(-6.73, -5.31) * mm});
            skLineSegment(sketch, "E99.22.54", {"start": v(-6.75, -5.32) * mm, "end": v(-6.76, -5.33) * mm});
            skLineSegment(sketch, "E99.22.55", {"start": v(-6.38, -5.68) * mm, "end": v(-6.39, -5.7) * mm});
            skLineSegment(sketch, "E99.22.56", {"start": v(-6.4, -5.72) * mm, "end": v(-6.42, -5.74) * mm});
            skLineSegment(sketch, "E99.22.57", {"start": v(-6.7, -5.3) * mm, "end": v(-6.71, -5.3) * mm});
            skLineSegment(sketch, "E99.22.58", {"start": v(-6.36, -5.61) * mm, "end": v(-6.36, -5.63) * mm});
            skLineSegment(sketch, "E99.22.59", {"start": v(-6.76, -5.33) * mm, "end": v(-6.8, -5.35) * mm});
            skLineSegment(sketch, "E99.22.60", {"start": v(-6.4, -5.7) * mm, "end": v(-6.4, -5.72) * mm});
            skLineSegment(sketch, "E99.22.61", {"start": v(-6.37, -5.64) * mm, "end": v(-6.37, -5.66) * mm});
            skLineSegment(sketch, "E99.22.62", {"start": v(-6.73, -5.31) * mm, "end": v(-6.75, -5.32) * mm});
            skLineSegment(sketch, "E99.22.63", {"start": v(-6.39, -5.7) * mm, "end": v(-6.4, -5.7) * mm});
            skLineSegment(sketch, "E99.22.64", {"start": v(-6.35, -5.6) * mm, "end": v(-6.36, -5.61) * mm});
            skLineSegment(sketch, "E99.22.65", {"start": v(-6.61, -5.28) * mm, "end": v(-6.63, -5.28) * mm});
            skLineSegment(sketch, "E99.22.66", {"start": v(-6.65, -5.29) * mm, "end": v(-6.66, -5.29) * mm});
            skLineSegment(sketch, "E99.22.67", {"start": v(-6.35, -5.58) * mm, "end": v(-6.35, -5.6) * mm});
            skLineSegment(sketch, "E99.22.68", {"start": v(-6.66, -5.29) * mm, "end": v(-6.68, -5.3) * mm});
            skLineSegment(sketch, "E99.22.69", {"start": v(-6.6, -5.28) * mm, "end": v(-6.61, -5.28) * mm});
            skLineSegment(sketch, "E99.22.70", {"start": v(-6.55, -5.29) * mm, "end": v(-6.57, -5.29) * mm});
            skLineSegment(sketch, "E99.22.71", {"start": v(-6.58, -5.28) * mm, "end": v(-6.6, -5.28) * mm});
            skLineSegment(sketch, "E99.22.72", {"start": v(-6.57, -5.29) * mm, "end": v(-6.58, -5.28) * mm});
            skLineSegment(sketch, "E99.22.73", {"start": v(-6.52, -5.3) * mm, "end": v(-6.53, -5.3) * mm});
            skLineSegment(sketch, "E99.22.74", {"start": v(-6.35, -5.56) * mm, "end": v(-6.35, -5.58) * mm});
            skLineSegment(sketch, "E99.22.75", {"start": v(-6.53, -5.3) * mm, "end": v(-6.55, -5.29) * mm});
            skLineSegment(sketch, "E99.22.76", {"start": v(-6.42, -5.38) * mm, "end": v(-6.42, -5.38) * mm});
            skLineSegment(sketch, "E99.22.77", {"start": v(-6.45, -5.34) * mm, "end": v(-6.47, -5.33) * mm});
            skLineSegment(sketch, "E99.22.78", {"start": v(-6.43, -5.36) * mm, "end": v(-6.45, -5.34) * mm});
            skLineSegment(sketch, "E99.22.79", {"start": v(-6.4, -5.4) * mm, "end": v(-6.38, -5.43) * mm});
            skLineSegment(sketch, "E99.22.80", {"start": v(-6.35, -5.5) * mm, "end": v(-6.35, -5.52) * mm});
            skLineSegment(sketch, "E99.22.81", {"start": v(-6.35, -5.53) * mm, "end": v(-6.35, -5.55) * mm});
            skLineSegment(sketch, "E99.22.82", {"start": v(-6.5, -5.3) * mm, "end": v(-6.52, -5.3) * mm});
            skLineSegment(sketch, "E99.22.83", {"start": v(-6.37, -5.45) * mm, "end": v(-6.36, -5.46) * mm});
            skLineSegment(sketch, "E99.22.84", {"start": v(-6.35, -5.55) * mm, "end": v(-6.35, -5.56) * mm});
            skLineSegment(sketch, "E99.22.85", {"start": v(-6.47, -5.33) * mm, "end": v(-6.49, -5.32) * mm});
            skLineSegment(sketch, "E99.22.86", {"start": v(-6.35, -5.52) * mm, "end": v(-6.35, -5.53) * mm});
            skLineSegment(sketch, "E99.22.87", {"start": v(-6.38, -5.43) * mm, "end": v(-6.37, -5.45) * mm});
            skLineSegment(sketch, "E99.22.88", {"start": v(-6.36, -5.48) * mm, "end": v(-6.35, -5.5) * mm});
            skLineSegment(sketch, "E99.22.89", {"start": v(-6.42, -5.37) * mm, "end": v(-6.43, -5.37) * mm});
            skLineSegment(sketch, "E99.22.90", {"start": v(-6.43, -5.36) * mm, "end": v(-6.43, -5.36) * mm});
            skLineSegment(sketch, "E99.22.91", {"start": v(-6.49, -5.32) * mm, "end": v(-6.5, -5.3) * mm});
            skLineSegment(sketch, "E99.22.92", {"start": v(-6.36, -5.46) * mm, "end": v(-6.36, -5.48) * mm});
            skLineSegment(sketch, "E99.22.93", {"start": v(-6.4, -5.4) * mm, "end": v(-6.4, -5.4) * mm});
            skLineSegment(sketch, "E99.22.94", {"start": v(-6.4, -5.4) * mm, "end": v(-6.4, -5.4) * mm});
            skLineSegment(sketch, "E99.22.95", {"start": v(-6.4, -5.4) * mm, "end": v(-6.4, -5.4) * mm});
            skLineSegment(sketch, "E99.22.96", {"start": v(-6.41, -5.39) * mm, "end": v(-6.4, -5.4) * mm});
            skLineSegment(sketch, "E99.22.97", {"start": v(-6.42, -5.38) * mm, "end": v(-6.41, -5.39) * mm});
            skLineSegment(sketch, "E99.22.98", {"start": v(-6.43, -5.37) * mm, "end": v(-6.43, -5.36) * mm});
            skLineSegment(sketch, "E99.22.99", {"start": v(-6.42, -5.38) * mm, "end": v(-6.42, -5.37) * mm});
            skLineSegment(sketch, "E99.23.0", {"start": v(-6.4, -6.78) * mm, "end": v(-6.44, -6.8) * mm});
            skLineSegment(sketch, "E99.23.1", {"start": v(-5.57, -7.48) * mm, "end": v(-5.58, -7.53) * mm});
            skLineSegment(sketch, "E99.23.2", {"start": v(-6.7, -6.74) * mm, "end": v(-6.72, -6.72) * mm});
            skLineSegment(sketch, "E99.23.3", {"start": v(-6.66, -6.77) * mm, "end": v(-6.7, -6.74) * mm});
            skLineSegment(sketch, "E99.23.4", {"start": v(-6.22, -6.7) * mm, "end": v(-6.26, -6.72) * mm});
            skLineSegment(sketch, "E99.23.5", {"start": v(-5.45, -7.06) * mm, "end": v(-5.47, -7.1) * mm});
            skLineSegment(sketch, "E99.23.6", {"start": v(-6.13, -6.66) * mm, "end": v(-6.18, -6.68) * mm});
            skLineSegment(sketch, "E99.23.7", {"start": v(-5.85, -6.5) * mm, "end": v(-5.89, -6.53) * mm});
            skLineSegment(sketch, "E99.23.8", {"start": v(-6.18, -6.68) * mm, "end": v(-6.22, -6.7) * mm});
            skLineSegment(sketch, "E99.23.9", {"start": v(-5.93, -6.55) * mm, "end": v(-5.97, -6.57) * mm});
            skLineSegment(sketch, "E99.23.10", {"start": v(-5.48, -7.15) * mm, "end": v(-5.5, -7.2) * mm});
            skLineSegment(sketch, "E99.23.11", {"start": v(-5.4, -6.93) * mm, "end": v(-5.42, -6.97) * mm});
            skLineSegment(sketch, "E99.23.12", {"start": v(-5.5, -7.24) * mm, "end": v(-5.52, -7.29) * mm});
            skLineSegment(sketch, "E99.23.13", {"start": v(-6.05, -6.62) * mm, "end": v(-6.1, -6.64) * mm});
            skLineSegment(sketch, "E99.23.14", {"start": v(-6.44, -6.8) * mm, "end": v(-6.49, -6.82) * mm});
            skLineSegment(sketch, "E99.23.15", {"start": v(-6, -6.6) * mm, "end": v(-6.05, -6.62) * mm});
            skLineSegment(sketch, "E99.23.16", {"start": v(-6.35, -6.76) * mm, "end": v(-6.4, -6.78) * mm});
            skLineSegment(sketch, "E99.23.17", {"start": v(-6.1, -6.64) * mm, "end": v(-6.13, -6.66) * mm});
            skLineSegment(sketch, "E99.23.18", {"start": v(-5.56, -7.43) * mm, "end": v(-5.57, -7.48) * mm});
            skLineSegment(sketch, "E99.23.19", {"start": v(-6.49, -6.82) * mm, "end": v(-6.54, -6.83) * mm});
            skLineSegment(sketch, "E99.23.20", {"start": v(-6.64, -6.8) * mm, "end": v(-6.66, -6.77) * mm});
            skLineSegment(sketch, "E99.23.21", {"start": v(-5.39, -6.89) * mm, "end": v(-5.4, -6.93) * mm});
            skLineSegment(sketch, "E99.23.22", {"start": v(-5.44, -7.02) * mm, "end": v(-5.45, -7.06) * mm});
            skLineSegment(sketch, "E99.23.23", {"start": v(-5.53, -7.34) * mm, "end": v(-5.55, -7.38) * mm});
            skLineSegment(sketch, "E99.23.24", {"start": v(-6.26, -6.72) * mm, "end": v(-6.3, -6.74) * mm});
            skLineSegment(sketch, "E99.23.25", {"start": v(-5.89, -6.53) * mm, "end": v(-5.93, -6.55) * mm});
            skLineSegment(sketch, "E99.23.26", {"start": v(-6.54, -6.83) * mm, "end": v(-6.58, -6.85) * mm});
            skLineSegment(sketch, "E99.23.27", {"start": v(-6.61, -6.82) * mm, "end": v(-6.64, -6.8) * mm});
            skLineSegment(sketch, "E99.23.28", {"start": v(-6.3, -6.74) * mm, "end": v(-6.35, -6.76) * mm});
            skLineSegment(sketch, "E99.23.29", {"start": v(-5.47, -7.1) * mm, "end": v(-5.48, -7.15) * mm});
            skLineSegment(sketch, "E99.23.30", {"start": v(-5.55, -7.38) * mm, "end": v(-5.56, -7.43) * mm});
            skLineSegment(sketch, "E99.23.31", {"start": v(-5.97, -6.57) * mm, "end": v(-6, -6.6) * mm});
            skLineSegment(sketch, "E99.23.32", {"start": v(-5.52, -7.29) * mm, "end": v(-5.53, -7.34) * mm});
            skLineSegment(sketch, "E99.23.33", {"start": v(-5.42, -6.97) * mm, "end": v(-5.44, -7.02) * mm});
            skLineSegment(sketch, "E99.23.34", {"start": v(-5.58, -7.53) * mm, "end": v(-5.59, -7.57) * mm});
            skLineSegment(sketch, "E99.23.35", {"start": v(-5.48, -7.76) * mm, "end": v(-5.45, -7.78) * mm});
            skLineSegment(sketch, "E99.23.36", {"start": v(-5.5, -7.2) * mm, "end": v(-5.5, -7.24) * mm});
            skLineSegment(sketch, "E99.23.37", {"start": v(-5.51, -7.74) * mm, "end": v(-5.48, -7.76) * mm});
            skLineSegment(sketch, "E99.23.38", {"start": v(-5.59, -7.57) * mm, "end": v(-5.6, -7.62) * mm});
            skLineSegment(sketch, "E99.23.39", {"start": v(-6.58, -6.85) * mm, "end": v(-6.61, -6.82) * mm});
            skLineSegment(sketch, "E99.23.40", {"start": v(-5.6, -7.62) * mm, "end": v(-5.6, -7.67) * mm});
            skLineSegment(sketch, "E99.23.41", {"start": v(-5.54, -7.72) * mm, "end": v(-5.51, -7.74) * mm});
            skLineSegment(sketch, "E99.23.42", {"start": v(-5.57, -7.7) * mm, "end": v(-5.54, -7.72) * mm});
            skLineSegment(sketch, "E99.23.43", {"start": v(-5.37, -6.85) * mm, "end": v(-5.39, -6.89) * mm});
            skLineSegment(sketch, "E99.23.44", {"start": v(-5.6, -7.67) * mm, "end": v(-5.57, -7.7) * mm});
            skLineSegment(sketch, "E99.23.45", {"start": v(-5.81, -6.47) * mm, "end": v(-5.85, -6.5) * mm});
            skLineSegment(sketch, "E99.23.46", {"start": v(-5.29, -6.65) * mm, "end": v(-5.29, -6.66) * mm});
            skLineSegment(sketch, "E99.23.47", {"start": v(-5.33, -6.76) * mm, "end": v(-5.35, -6.8) * mm});
            skLineSegment(sketch, "E99.23.48", {"start": v(-5.35, -6.8) * mm, "end": v(-5.37, -6.85) * mm});
            skLineSegment(sketch, "E99.23.49", {"start": v(-5.66, -6.37) * mm, "end": v(-5.68, -6.38) * mm});
            skLineSegment(sketch, "E99.23.50", {"start": v(-5.3, -6.68) * mm, "end": v(-5.3, -6.7) * mm});
            skLineSegment(sketch, "E99.23.51", {"start": v(-5.61, -6.36) * mm, "end": v(-5.63, -6.36) * mm});
            skLineSegment(sketch, "E99.23.52", {"start": v(-5.77, -6.45) * mm, "end": v(-5.81, -6.47) * mm});
            skLineSegment(sketch, "E99.23.53", {"start": v(-5.7, -6.39) * mm, "end": v(-5.7, -6.4) * mm});
            skLineSegment(sketch, "E99.23.54", {"start": v(-5.72, -6.4) * mm, "end": v(-5.74, -6.42) * mm});
            skLineSegment(sketch, "E99.23.55", {"start": v(-5.3, -6.7) * mm, "end": v(-5.3, -6.71) * mm});
            skLineSegment(sketch, "E99.23.56", {"start": v(-5.32, -6.75) * mm, "end": v(-5.33, -6.76) * mm});
            skLineSegment(sketch, "E99.23.57", {"start": v(-5.68, -6.38) * mm, "end": v(-5.7, -6.39) * mm});
            skLineSegment(sketch, "E99.23.58", {"start": v(-5.28, -6.63) * mm, "end": v(-5.29, -6.65) * mm});
            skLineSegment(sketch, "E99.23.59", {"start": v(-5.74, -6.42) * mm, "end": v(-5.77, -6.45) * mm});
            skLineSegment(sketch, "E99.23.60", {"start": v(-5.31, -6.73) * mm, "end": v(-5.32, -6.75) * mm});
            skLineSegment(sketch, "E99.23.61", {"start": v(-5.29, -6.66) * mm, "end": v(-5.3, -6.68) * mm});
            skLineSegment(sketch, "E99.23.62", {"start": v(-5.7, -6.4) * mm, "end": v(-5.72, -6.4) * mm});
            skLineSegment(sketch, "E99.23.63", {"start": v(-5.3, -6.71) * mm, "end": v(-5.31, -6.73) * mm});
            skLineSegment(sketch, "E99.23.64", {"start": v(-5.28, -6.61) * mm, "end": v(-5.28, -6.63) * mm});
            skLineSegment(sketch, "E99.23.65", {"start": v(-5.6, -6.35) * mm, "end": v(-5.61, -6.36) * mm});
            skLineSegment(sketch, "E99.23.66", {"start": v(-5.63, -6.36) * mm, "end": v(-5.64, -6.37) * mm});
            skLineSegment(sketch, "E99.23.67", {"start": v(-5.28, -6.6) * mm, "end": v(-5.28, -6.61) * mm});
            skLineSegment(sketch, "E99.23.68", {"start": v(-5.64, -6.37) * mm, "end": v(-5.66, -6.37) * mm});
            skLineSegment(sketch, "E99.23.69", {"start": v(-5.58, -6.35) * mm, "end": v(-5.6, -6.35) * mm});
            skLineSegment(sketch, "E99.23.70", {"start": v(-5.53, -6.35) * mm, "end": v(-5.55, -6.35) * mm});
            skLineSegment(sketch, "E99.23.71", {"start": v(-5.56, -6.35) * mm, "end": v(-5.58, -6.35) * mm});
            skLineSegment(sketch, "E99.23.72", {"start": v(-5.55, -6.35) * mm, "end": v(-5.56, -6.35) * mm});
            skLineSegment(sketch, "E99.23.73", {"start": v(-5.5, -6.35) * mm, "end": v(-5.52, -6.35) * mm});
            skLineSegment(sketch, "E99.23.74", {"start": v(-5.28, -6.58) * mm, "end": v(-5.28, -6.6) * mm});
            skLineSegment(sketch, "E99.23.75", {"start": v(-5.52, -6.35) * mm, "end": v(-5.53, -6.35) * mm});
            skLineSegment(sketch, "E99.23.76", {"start": v(-5.38, -6.42) * mm, "end": v(-5.39, -6.41) * mm});
            skLineSegment(sketch, "E99.23.77", {"start": v(-5.43, -6.38) * mm, "end": v(-5.45, -6.37) * mm});
            skLineSegment(sketch, "E99.23.78", {"start": v(-5.4, -6.4) * mm, "end": v(-5.43, -6.38) * mm});
            skLineSegment(sketch, "E99.23.79", {"start": v(-5.36, -6.43) * mm, "end": v(-5.34, -6.45) * mm});
            skLineSegment(sketch, "E99.23.80", {"start": v(-5.3, -6.52) * mm, "end": v(-5.3, -6.53) * mm});
            skLineSegment(sketch, "E99.23.81", {"start": v(-5.29, -6.55) * mm, "end": v(-5.29, -6.57) * mm});
            skLineSegment(sketch, "E99.23.82", {"start": v(-5.48, -6.36) * mm, "end": v(-5.5, -6.35) * mm});
            skLineSegment(sketch, "E99.23.83", {"start": v(-5.33, -6.47) * mm, "end": v(-5.32, -6.49) * mm});
            skLineSegment(sketch, "E99.23.84", {"start": v(-5.29, -6.57) * mm, "end": v(-5.28, -6.58) * mm});
            skLineSegment(sketch, "E99.23.85", {"start": v(-5.45, -6.37) * mm, "end": v(-5.46, -6.36) * mm});
            skLineSegment(sketch, "E99.23.86", {"start": v(-5.3, -6.53) * mm, "end": v(-5.29, -6.55) * mm});
            skLineSegment(sketch, "E99.23.87", {"start": v(-5.34, -6.45) * mm, "end": v(-5.33, -6.47) * mm});
            skLineSegment(sketch, "E99.23.88", {"start": v(-5.3, -6.5) * mm, "end": v(-5.3, -6.52) * mm});
            skLineSegment(sketch, "E99.23.89", {"start": v(-5.4, -6.4) * mm, "end": v(-5.4, -6.4) * mm});
            skLineSegment(sketch, "E99.23.90", {"start": v(-5.4, -6.4) * mm, "end": v(-5.4, -6.4) * mm});
            skLineSegment(sketch, "E99.23.91", {"start": v(-5.46, -6.36) * mm, "end": v(-5.48, -6.36) * mm});
            skLineSegment(sketch, "E99.23.92", {"start": v(-5.32, -6.49) * mm, "end": v(-5.3, -6.5) * mm});
            skLineSegment(sketch, "E99.23.93", {"start": v(-5.36, -6.43) * mm, "end": v(-5.36, -6.43) * mm});
            skLineSegment(sketch, "E99.23.94", {"start": v(-5.37, -6.43) * mm, "end": v(-5.36, -6.43) * mm});
            skLineSegment(sketch, "E99.23.95", {"start": v(-5.37, -6.42) * mm, "end": v(-5.37, -6.43) * mm});
            skLineSegment(sketch, "E99.23.96", {"start": v(-5.38, -6.42) * mm, "end": v(-5.37, -6.42) * mm});
            skLineSegment(sketch, "E99.23.97", {"start": v(-5.38, -6.42) * mm, "end": v(-5.38, -6.42) * mm});
            skLineSegment(sketch, "E99.23.98", {"start": v(-5.4, -6.4) * mm, "end": v(-5.4, -6.4) * mm});
            skLineSegment(sketch, "E99.23.99", {"start": v(-5.39, -6.41) * mm, "end": v(-5.4, -6.4) * mm});
            skLineSegment(sketch, "E99.24.0", {"start": v(-5.12, -7.79) * mm, "end": v(-5.16, -7.81) * mm});
            skLineSegment(sketch, "E99.24.1", {"start": v(-4.18, -8.33) * mm, "end": v(-4.18, -8.38) * mm});
            skLineSegment(sketch, "E99.24.2", {"start": v(-5.42, -7.8) * mm, "end": v(-5.45, -7.78) * mm});
            skLineSegment(sketch, "E99.24.3", {"start": v(-5.39, -7.82) * mm, "end": v(-5.42, -7.8) * mm});
            skLineSegment(sketch, "E99.24.4", {"start": v(-4.96, -7.68) * mm, "end": v(-5, -7.7) * mm});
            skLineSegment(sketch, "E99.24.5", {"start": v(-4.14, -7.9) * mm, "end": v(-4.15, -7.95) * mm});
            skLineSegment(sketch, "E99.24.6", {"start": v(-4.88, -7.63) * mm, "end": v(-4.92, -7.65) * mm});
            skLineSegment(sketch, "E99.24.7", {"start": v(-4.63, -7.42) * mm, "end": v(-4.66, -7.45) * mm});
            skLineSegment(sketch, "E99.24.8", {"start": v(-4.92, -7.65) * mm, "end": v(-4.96, -7.68) * mm});
            skLineSegment(sketch, "E99.24.9", {"start": v(-4.7, -7.48) * mm, "end": v(-4.73, -7.5) * mm});
            skLineSegment(sketch, "E99.24.10", {"start": v(-4.16, -8) * mm, "end": v(-4.16, -8.04) * mm});
            skLineSegment(sketch, "E99.24.11", {"start": v(-4.12, -7.76) * mm, "end": v(-4.13, -7.8) * mm});
            skLineSegment(sketch, "E99.24.12", {"start": v(-4.17, -8.09) * mm, "end": v(-4.17, -8.14) * mm});
            skLineSegment(sketch, "E99.24.13", {"start": v(-4.8, -7.57) * mm, "end": v(-4.84, -7.6) * mm});
            skLineSegment(sketch, "E99.24.14", {"start": v(-5.16, -7.81) * mm, "end": v(-5.2, -7.84) * mm});
            skLineSegment(sketch, "E99.24.15", {"start": v(-4.77, -7.54) * mm, "end": v(-4.8, -7.57) * mm});
            skLineSegment(sketch, "E99.24.16", {"start": v(-5.08, -7.76) * mm, "end": v(-5.12, -7.79) * mm});
            skLineSegment(sketch, "E99.24.17", {"start": v(-4.84, -7.6) * mm, "end": v(-4.88, -7.63) * mm});
            skLineSegment(sketch, "E99.24.18", {"start": v(-4.18, -8.28) * mm, "end": v(-4.18, -8.33) * mm});
            skLineSegment(sketch, "E99.24.19", {"start": v(-5.2, -7.84) * mm, "end": v(-5.25, -7.86) * mm});
            skLineSegment(sketch, "E99.24.20", {"start": v(-5.36, -7.85) * mm, "end": v(-5.39, -7.82) * mm});
            skLineSegment(sketch, "E99.24.21", {"start": v(-4.1, -7.72) * mm, "end": v(-4.12, -7.76) * mm});
            skLineSegment(sketch, "E99.24.22", {"start": v(-4.14, -7.85) * mm, "end": v(-4.14, -7.9) * mm});
            skLineSegment(sketch, "E99.24.23", {"start": v(-4.18, -8.18) * mm, "end": v(-4.18, -8.23) * mm});
            skLineSegment(sketch, "E99.24.24", {"start": v(-5, -7.7) * mm, "end": v(-5.04, -7.74) * mm});
            skLineSegment(sketch, "E99.24.25", {"start": v(-4.66, -7.45) * mm, "end": v(-4.7, -7.48) * mm});
            skLineSegment(sketch, "E99.24.26", {"start": v(-5.25, -7.86) * mm, "end": v(-5.3, -7.89) * mm});
            skLineSegment(sketch, "E99.24.27", {"start": v(-5.32, -7.87) * mm, "end": v(-5.36, -7.85) * mm});
            skLineSegment(sketch, "E99.24.28", {"start": v(-5.04, -7.74) * mm, "end": v(-5.08, -7.76) * mm});
            skLineSegment(sketch, "E99.24.29", {"start": v(-4.15, -7.95) * mm, "end": v(-4.16, -8) * mm});
            skLineSegment(sketch, "E99.24.30", {"start": v(-4.18, -8.23) * mm, "end": v(-4.18, -8.28) * mm});
            skLineSegment(sketch, "E99.24.31", {"start": v(-4.73, -7.5) * mm, "end": v(-4.77, -7.54) * mm});
            skLineSegment(sketch, "E99.24.32", {"start": v(-4.17, -8.14) * mm, "end": v(-4.18, -8.18) * mm});
            skLineSegment(sketch, "E99.24.33", {"start": v(-4.13, -7.8) * mm, "end": v(-4.14, -7.85) * mm});
            skLineSegment(sketch, "E99.24.34", {"start": v(-4.18, -8.38) * mm, "end": v(-4.19, -8.43) * mm});
            skLineSegment(sketch, "E99.24.35", {"start": v(-4.05, -8.6) * mm, "end": v(-4.01, -8.6) * mm});
            skLineSegment(sketch, "E99.24.36", {"start": v(-4.16, -8.04) * mm, "end": v(-4.17, -8.09) * mm});
            skLineSegment(sketch, "E99.24.37", {"start": v(-4.08, -8.58) * mm, "end": v(-4.05, -8.6) * mm});
            skLineSegment(sketch, "E99.24.38", {"start": v(-4.19, -8.43) * mm, "end": v(-4.19, -8.48) * mm});
            skLineSegment(sketch, "E99.24.39", {"start": v(-5.3, -7.89) * mm, "end": v(-5.32, -7.87) * mm});
            skLineSegment(sketch, "E99.24.40", {"start": v(-4.19, -8.48) * mm, "end": v(-4.18, -8.53) * mm});
            skLineSegment(sketch, "E99.24.41", {"start": v(-4.12, -8.56) * mm, "end": v(-4.08, -8.58) * mm});
            skLineSegment(sketch, "E99.24.42", {"start": v(-4.15, -8.55) * mm, "end": v(-4.12, -8.56) * mm});
            skLineSegment(sketch, "E99.24.43", {"start": v(-4.1, -7.67) * mm, "end": v(-4.1, -7.72) * mm});
            skLineSegment(sketch, "E99.24.44", {"start": v(-4.18, -8.53) * mm, "end": v(-4.15, -8.55) * mm});
            skLineSegment(sketch, "E99.24.45", {"start": v(-4.6, -7.39) * mm, "end": v(-4.63, -7.42) * mm});
            skLineSegment(sketch, "E99.24.46", {"start": v(-4.05, -7.46) * mm, "end": v(-4.05, -7.48) * mm});
            skLineSegment(sketch, "E99.24.47", {"start": v(-4.07, -7.59) * mm, "end": v(-4.08, -7.63) * mm});
            skLineSegment(sketch, "E99.24.48", {"start": v(-4.08, -7.63) * mm, "end": v(-4.1, -7.67) * mm});
            skLineSegment(sketch, "E99.24.49", {"start": v(-4.47, -7.26) * mm, "end": v(-4.48, -7.27) * mm});
            skLineSegment(sketch, "E99.24.50", {"start": v(-4.05, -7.5) * mm, "end": v(-4.06, -7.52) * mm});
            skLineSegment(sketch, "E99.24.51", {"start": v(-4.42, -7.23) * mm, "end": v(-4.44, -7.24) * mm});
            skLineSegment(sketch, "E99.24.52", {"start": v(-4.57, -7.35) * mm, "end": v(-4.6, -7.39) * mm});
            skLineSegment(sketch, "E99.24.53", {"start": v(-4.5, -7.28) * mm, "end": v(-4.5, -7.3) * mm});
            skLineSegment(sketch, "E99.24.54", {"start": v(-4.52, -7.3) * mm, "end": v(-4.53, -7.32) * mm});
            skLineSegment(sketch, "E99.24.55", {"start": v(-4.06, -7.52) * mm, "end": v(-4.06, -7.53) * mm});
            skLineSegment(sketch, "E99.24.56", {"start": v(-4.07, -7.57) * mm, "end": v(-4.07, -7.59) * mm});
            skLineSegment(sketch, "E99.24.57", {"start": v(-4.48, -7.27) * mm, "end": v(-4.5, -7.28) * mm});
            skLineSegment(sketch, "E99.24.58", {"start": v(-4.05, -7.45) * mm, "end": v(-4.05, -7.46) * mm});
            skLineSegment(sketch, "E99.24.59", {"start": v(-4.53, -7.32) * mm, "end": v(-4.57, -7.35) * mm});
            skLineSegment(sketch, "E99.24.60", {"start": v(-4.06, -7.55) * mm, "end": v(-4.07, -7.57) * mm});
            skLineSegment(sketch, "E99.24.61", {"start": v(-4.05, -7.48) * mm, "end": v(-4.05, -7.5) * mm});
            skLineSegment(sketch, "E99.24.62", {"start": v(-4.5, -7.3) * mm, "end": v(-4.52, -7.3) * mm});
            skLineSegment(sketch, "E99.24.63", {"start": v(-4.06, -7.53) * mm, "end": v(-4.06, -7.55) * mm});
            skLineSegment(sketch, "E99.24.64", {"start": v(-4.05, -7.43) * mm, "end": v(-4.05, -7.45) * mm});
            skLineSegment(sketch, "E99.24.65", {"start": v(-4.4, -7.23) * mm, "end": v(-4.42, -7.23) * mm});
            skLineSegment(sketch, "E99.24.66", {"start": v(-4.44, -7.24) * mm, "end": v(-4.45, -7.25) * mm});
            skLineSegment(sketch, "E99.24.67", {"start": v(-4.06, -7.42) * mm, "end": v(-4.05, -7.43) * mm});
            skLineSegment(sketch, "E99.24.68", {"start": v(-4.45, -7.25) * mm, "end": v(-4.47, -7.26) * mm});
            skLineSegment(sketch, "E99.24.69", {"start": v(-4.4, -7.22) * mm, "end": v(-4.4, -7.23) * mm});
            skLineSegment(sketch, "E99.24.70", {"start": v(-4.35, -7.21) * mm, "end": v(-4.36, -7.21) * mm});
            skLineSegment(sketch, "E99.24.71", {"start": v(-4.38, -7.22) * mm, "end": v(-4.4, -7.22) * mm});
            skLineSegment(sketch, "E99.24.72", {"start": v(-4.36, -7.21) * mm, "end": v(-4.38, -7.22) * mm});
            skLineSegment(sketch, "E99.24.73", {"start": v(-4.31, -7.2) * mm, "end": v(-4.33, -7.2) * mm});
            skLineSegment(sketch, "E99.24.74", {"start": v(-4.06, -7.4) * mm, "end": v(-4.06, -7.42) * mm});
            skLineSegment(sketch, "E99.24.75", {"start": v(-4.33, -7.2) * mm, "end": v(-4.35, -7.21) * mm});
            skLineSegment(sketch, "E99.24.76", {"start": v(-4.19, -7.25) * mm, "end": v(-4.2, -7.25) * mm});
            skLineSegment(sketch, "E99.24.77", {"start": v(-4.24, -7.23) * mm, "end": v(-4.26, -7.22) * mm});
            skLineSegment(sketch, "E99.24.78", {"start": v(-4.21, -7.24) * mm, "end": v(-4.24, -7.23) * mm});
            skLineSegment(sketch, "E99.24.79", {"start": v(-4.16, -7.27) * mm, "end": v(-4.14, -7.28) * mm});
            skLineSegment(sketch, "E99.24.80", {"start": v(-4.09, -7.34) * mm, "end": v(-4.08, -7.35) * mm});
            skLineSegment(sketch, "E99.24.81", {"start": v(-4.07, -7.37) * mm, "end": v(-4.07, -7.38) * mm});
            skLineSegment(sketch, "E99.24.82", {"start": v(-4.3, -7.21) * mm, "end": v(-4.31, -7.2) * mm});
            skLineSegment(sketch, "E99.24.83", {"start": v(-4.12, -7.3) * mm, "end": v(-4.1, -7.31) * mm});
            skLineSegment(sketch, "E99.24.84", {"start": v(-4.07, -7.38) * mm, "end": v(-4.06, -7.4) * mm});
            skLineSegment(sketch, "E99.24.85", {"start": v(-4.26, -7.22) * mm, "end": v(-4.28, -7.21) * mm});
            skLineSegment(sketch, "E99.24.86", {"start": v(-4.08, -7.35) * mm, "end": v(-4.07, -7.37) * mm});
            skLineSegment(sketch, "E99.24.87", {"start": v(-4.14, -7.28) * mm, "end": v(-4.12, -7.3) * mm});
            skLineSegment(sketch, "E99.24.88", {"start": v(-4.1, -7.32) * mm, "end": v(-4.09, -7.34) * mm});
            skLineSegment(sketch, "E99.24.89", {"start": v(-4.2, -7.25) * mm, "end": v(-4.2, -7.24) * mm});
            skLineSegment(sketch, "E99.24.90", {"start": v(-4.2, -7.24) * mm, "end": v(-4.21, -7.24) * mm});
            skLineSegment(sketch, "E99.24.91", {"start": v(-4.28, -7.21) * mm, "end": v(-4.3, -7.21) * mm});
            skLineSegment(sketch, "E99.24.92", {"start": v(-4.1, -7.31) * mm, "end": v(-4.1, -7.32) * mm});
            skLineSegment(sketch, "E99.24.93", {"start": v(-4.17, -7.26) * mm, "end": v(-4.16, -7.27) * mm});
            skLineSegment(sketch, "E99.24.94", {"start": v(-4.17, -7.26) * mm, "end": v(-4.17, -7.26) * mm});
            skLineSegment(sketch, "E99.24.95", {"start": v(-4.18, -7.26) * mm, "end": v(-4.17, -7.26) * mm});
            skLineSegment(sketch, "E99.24.96", {"start": v(-4.18, -7.26) * mm, "end": v(-4.18, -7.26) * mm});
            skLineSegment(sketch, "E99.24.97", {"start": v(-4.19, -7.25) * mm, "end": v(-4.18, -7.26) * mm});
            skLineSegment(sketch, "E99.24.98", {"start": v(-4.2, -7.24) * mm, "end": v(-4.2, -7.24) * mm});
            skLineSegment(sketch, "E99.24.99", {"start": v(-4.2, -7.25) * mm, "end": v(-4.2, -7.25) * mm});
            skLineSegment(sketch, "E99.25.0", {"start": v(-3.7, -8.56) * mm, "end": v(-3.73, -8.6) * mm});
            skLineSegment(sketch, "E99.25.1", {"start": v(-2.67, -8.93) * mm, "end": v(-2.67, -8.98) * mm});
            skLineSegment(sketch, "E99.25.2", {"start": v(-3.98, -8.63) * mm, "end": v(-4.01, -8.6) * mm});
            skLineSegment(sketch, "E99.25.3", {"start": v(-3.95, -8.64) * mm, "end": v(-3.98, -8.63) * mm});
            skLineSegment(sketch, "E99.25.4", {"start": v(-3.55, -8.43) * mm, "end": v(-3.59, -8.46) * mm});
            skLineSegment(sketch, "E99.25.5", {"start": v(-2.7, -8.5) * mm, "end": v(-2.7, -8.55) * mm});
            skLineSegment(sketch, "E99.25.6", {"start": v(-3.48, -8.36) * mm, "end": v(-3.52, -8.4) * mm});
            skLineSegment(sketch, "E99.25.7", {"start": v(-3.27, -8.1) * mm, "end": v(-3.3, -8.15) * mm});
            skLineSegment(sketch, "E99.25.8", {"start": v(-3.52, -8.4) * mm, "end": v(-3.55, -8.43) * mm});
            skLineSegment(sketch, "E99.25.9", {"start": v(-3.33, -8.18) * mm, "end": v(-3.36, -8.22) * mm});
            skLineSegment(sketch, "E99.25.10", {"start": v(-2.7, -8.6) * mm, "end": v(-2.7, -8.64) * mm});
            skLineSegment(sketch, "E99.25.11", {"start": v(-2.7, -8.36) * mm, "end": v(-2.7, -8.4) * mm});
            skLineSegment(sketch, "E99.25.12", {"start": v(-2.7, -8.69) * mm, "end": v(-2.7, -8.74) * mm});
            skLineSegment(sketch, "E99.25.13", {"start": v(-3.42, -8.29) * mm, "end": v(-3.45, -8.32) * mm});
            skLineSegment(sketch, "E99.25.14", {"start": v(-3.73, -8.6) * mm, "end": v(-3.77, -8.62) * mm});
            skLineSegment(sketch, "E99.25.15", {"start": v(-3.39, -8.25) * mm, "end": v(-3.42, -8.29) * mm});
            skLineSegment(sketch, "E99.25.16", {"start": v(-3.66, -8.53) * mm, "end": v(-3.7, -8.56) * mm});
            skLineSegment(sketch, "E99.25.17", {"start": v(-3.45, -8.32) * mm, "end": v(-3.48, -8.36) * mm});
            skLineSegment(sketch, "E99.25.18", {"start": v(-2.68, -8.88) * mm, "end": v(-2.67, -8.93) * mm});
            skLineSegment(sketch, "E99.25.19", {"start": v(-3.77, -8.62) * mm, "end": v(-3.8, -8.66) * mm});
            skLineSegment(sketch, "E99.25.20", {"start": v(-3.91, -8.66) * mm, "end": v(-3.95, -8.64) * mm});
            skLineSegment(sketch, "E99.25.21", {"start": v(-2.7, -8.31) * mm, "end": v(-2.7, -8.36) * mm});
            skLineSegment(sketch, "E99.25.22", {"start": v(-2.7, -8.45) * mm, "end": v(-2.7, -8.5) * mm});
            skLineSegment(sketch, "E99.25.23", {"start": v(-2.7, -8.79) * mm, "end": v(-2.69, -8.83) * mm});
            skLineSegment(sketch, "E99.25.24", {"start": v(-3.59, -8.46) * mm, "end": v(-3.62, -8.5) * mm});
            skLineSegment(sketch, "E99.25.25", {"start": v(-3.3, -8.15) * mm, "end": v(-3.33, -8.18) * mm});
            skLineSegment(sketch, "E99.25.26", {"start": v(-3.8, -8.66) * mm, "end": v(-3.84, -8.69) * mm});
            skLineSegment(sketch, "E99.25.27", {"start": v(-3.88, -8.67) * mm, "end": v(-3.91, -8.66) * mm});
            skLineSegment(sketch, "E99.25.28", {"start": v(-3.62, -8.5) * mm, "end": v(-3.66, -8.53) * mm});
            skLineSegment(sketch, "E99.25.29", {"start": v(-2.7, -8.55) * mm, "end": v(-2.7, -8.6) * mm});
            skLineSegment(sketch, "E99.25.30", {"start": v(-2.69, -8.83) * mm, "end": v(-2.68, -8.88) * mm});
            skLineSegment(sketch, "E99.25.31", {"start": v(-3.36, -8.22) * mm, "end": v(-3.39, -8.25) * mm});
            skLineSegment(sketch, "E99.25.32", {"start": v(-2.7, -8.74) * mm, "end": v(-2.7, -8.79) * mm});
            skLineSegment(sketch, "E99.25.33", {"start": v(-2.7, -8.4) * mm, "end": v(-2.7, -8.45) * mm});
            skLineSegment(sketch, "E99.25.34", {"start": v(-2.67, -8.98) * mm, "end": v(-2.66, -9.03) * mm});
            skLineSegment(sketch, "E99.25.35", {"start": v(-2.5, -9.17) * mm, "end": v(-2.46, -9.18) * mm});
            skLineSegment(sketch, "E99.25.36", {"start": v(-2.7, -8.64) * mm, "end": v(-2.7, -8.69) * mm});
            skLineSegment(sketch, "E99.25.37", {"start": v(-2.53, -9.16) * mm, "end": v(-2.5, -9.17) * mm});
            skLineSegment(sketch, "E99.25.38", {"start": v(-2.66, -9.03) * mm, "end": v(-2.65, -9.08) * mm});
            skLineSegment(sketch, "E99.25.39", {"start": v(-3.84, -8.69) * mm, "end": v(-3.88, -8.67) * mm});
            skLineSegment(sketch, "E99.25.40", {"start": v(-2.65, -9.08) * mm, "end": v(-2.64, -9.13) * mm});
            skLineSegment(sketch, "E99.25.41", {"start": v(-2.57, -9.15) * mm, "end": v(-2.53, -9.16) * mm});
            skLineSegment(sketch, "E99.25.42", {"start": v(-2.6, -9.14) * mm, "end": v(-2.57, -9.15) * mm});
            skLineSegment(sketch, "E99.25.43", {"start": v(-2.7, -8.27) * mm, "end": v(-2.7, -8.31) * mm});
            skLineSegment(sketch, "E99.25.44", {"start": v(-2.64, -9.13) * mm, "end": v(-2.6, -9.14) * mm});
            skLineSegment(sketch, "E99.25.45", {"start": v(-3.25, -8.07) * mm, "end": v(-3.27, -8.1) * mm});
            skLineSegment(sketch, "E99.25.46", {"start": v(-2.7, -8.05) * mm, "end": v(-2.7, -8.07) * mm});
            skLineSegment(sketch, "E99.25.47", {"start": v(-2.7, -8.18) * mm, "end": v(-2.7, -8.22) * mm});
            skLineSegment(sketch, "E99.25.48", {"start": v(-2.7, -8.22) * mm, "end": v(-2.7, -8.27) * mm});
            skLineSegment(sketch, "E99.25.49", {"start": v(-3.14, -7.92) * mm, "end": v(-3.15, -7.94) * mm});
            skLineSegment(sketch, "E99.25.50", {"start": v(-2.69, -8.09) * mm, "end": v(-2.69, -8.1) * mm});
            skLineSegment(sketch, "E99.25.51", {"start": v(-3.1, -7.9) * mm, "end": v(-3.11, -7.9) * mm});
            skLineSegment(sketch, "E99.25.52", {"start": v(-3.22, -8.03) * mm, "end": v(-3.25, -8.07) * mm});
            skLineSegment(sketch, "E99.25.53", {"start": v(-3.16, -7.95) * mm, "end": v(-3.17, -7.97) * mm});
            skLineSegment(sketch, "E99.25.54", {"start": v(-3.18, -7.98) * mm, "end": v(-3.2, -8) * mm});
            skLineSegment(sketch, "E99.25.55", {"start": v(-2.69, -8.1) * mm, "end": v(-2.69, -8.12) * mm});
            skLineSegment(sketch, "E99.25.56", {"start": v(-2.7, -8.16) * mm, "end": v(-2.7, -8.18) * mm});
            skLineSegment(sketch, "E99.25.57", {"start": v(-3.15, -7.94) * mm, "end": v(-3.16, -7.95) * mm});
            skLineSegment(sketch, "E99.25.58", {"start": v(-2.7, -8.04) * mm, "end": v(-2.7, -8.05) * mm});
            skLineSegment(sketch, "E99.25.59", {"start": v(-3.2, -8) * mm, "end": v(-3.22, -8.03) * mm});
            skLineSegment(sketch, "E99.25.60", {"start": v(-2.69, -8.14) * mm, "end": v(-2.7, -8.16) * mm});
            skLineSegment(sketch, "E99.25.61", {"start": v(-2.7, -8.07) * mm, "end": v(-2.69, -8.09) * mm});
            skLineSegment(sketch, "E99.25.62", {"start": v(-3.17, -7.97) * mm, "end": v(-3.18, -7.98) * mm});
            skLineSegment(sketch, "E99.25.63", {"start": v(-2.69, -8.12) * mm, "end": v(-2.69, -8.14) * mm});
            skLineSegment(sketch, "E99.25.64", {"start": v(-2.7, -8.02) * mm, "end": v(-2.7, -8.04) * mm});
            skLineSegment(sketch, "E99.25.65", {"start": v(-3.09, -7.88) * mm, "end": v(-3.1, -7.9) * mm});
            skLineSegment(sketch, "E99.25.66", {"start": v(-3.11, -7.9) * mm, "end": v(-3.13, -7.91) * mm});
            skLineSegment(sketch, "E99.25.67", {"start": v(-2.7, -8) * mm, "end": v(-2.7, -8.02) * mm});
            skLineSegment(sketch, "E99.25.68", {"start": v(-3.13, -7.91) * mm, "end": v(-3.14, -7.92) * mm});
            skLineSegment(sketch, "E99.25.69", {"start": v(-3.07, -7.87) * mm, "end": v(-3.09, -7.88) * mm});
            skLineSegment(sketch, "E99.25.70", {"start": v(-3.03, -7.86) * mm, "end": v(-3.04, -7.86) * mm});
            skLineSegment(sketch, "E99.25.71", {"start": v(-3.06, -7.87) * mm, "end": v(-3.07, -7.87) * mm});
            skLineSegment(sketch, "E99.25.72", {"start": v(-3.04, -7.86) * mm, "end": v(-3.06, -7.87) * mm});
            skLineSegment(sketch, "E99.25.73", {"start": v(-3, -7.85) * mm, "end": v(-3.01, -7.85) * mm});
            skLineSegment(sketch, "E99.25.74", {"start": v(-2.71, -8) * mm, "end": v(-2.7, -8) * mm});
            skLineSegment(sketch, "E99.25.75", {"start": v(-3.01, -7.85) * mm, "end": v(-3.03, -7.86) * mm});
            skLineSegment(sketch, "E99.25.76", {"start": v(-2.86, -7.87) * mm, "end": v(-2.87, -7.87) * mm});
            skLineSegment(sketch, "E99.25.77", {"start": v(-2.92, -7.85) * mm, "end": v(-2.94, -7.85) * mm});
            skLineSegment(sketch, "E99.25.78", {"start": v(-2.9, -7.86) * mm, "end": v(-2.92, -7.85) * mm});
            skLineSegment(sketch, "E99.25.79", {"start": v(-2.84, -7.88) * mm, "end": v(-2.81, -7.9) * mm});
            skLineSegment(sketch, "E99.25.80", {"start": v(-2.75, -7.94) * mm, "end": v(-2.74, -7.95) * mm});
            skLineSegment(sketch, "E99.25.81", {"start": v(-2.73, -7.96) * mm, "end": v(-2.72, -7.98) * mm});
            skLineSegment(sketch, "E99.25.82", {"start": v(-2.98, -7.85) * mm, "end": v(-3, -7.85) * mm});
            skLineSegment(sketch, "E99.25.83", {"start": v(-2.8, -7.9) * mm, "end": v(-2.78, -7.91) * mm});
            skLineSegment(sketch, "E99.25.84", {"start": v(-2.72, -7.98) * mm, "end": v(-2.71, -8) * mm});
            skLineSegment(sketch, "E99.25.85", {"start": v(-2.94, -7.85) * mm, "end": v(-2.96, -7.85) * mm});
            skLineSegment(sketch, "E99.25.86", {"start": v(-2.74, -7.95) * mm, "end": v(-2.73, -7.96) * mm});
            skLineSegment(sketch, "E99.25.87", {"start": v(-2.81, -7.9) * mm, "end": v(-2.8, -7.9) * mm});
            skLineSegment(sketch, "E99.25.88", {"start": v(-2.76, -7.93) * mm, "end": v(-2.75, -7.94) * mm});
            skLineSegment(sketch, "E99.25.89", {"start": v(-2.88, -7.87) * mm, "end": v(-2.88, -7.86) * mm});
            skLineSegment(sketch, "E99.25.90", {"start": v(-2.89, -7.86) * mm, "end": v(-2.9, -7.86) * mm});
            skLineSegment(sketch, "E99.25.91", {"start": v(-2.96, -7.85) * mm, "end": v(-2.98, -7.85) * mm});
            skLineSegment(sketch, "E99.25.92", {"start": v(-2.78, -7.91) * mm, "end": v(-2.76, -7.93) * mm});
            skLineSegment(sketch, "E99.25.93", {"start": v(-2.84, -7.88) * mm, "end": v(-2.84, -7.88) * mm});
            skLineSegment(sketch, "E99.25.94", {"start": v(-2.85, -7.88) * mm, "end": v(-2.84, -7.88) * mm});
            skLineSegment(sketch, "E99.25.95", {"start": v(-2.85, -7.87) * mm, "end": v(-2.85, -7.88) * mm});
            skLineSegment(sketch, "E99.25.96", {"start": v(-2.86, -7.87) * mm, "end": v(-2.85, -7.87) * mm});
            skLineSegment(sketch, "E99.25.97", {"start": v(-2.86, -7.87) * mm, "end": v(-2.86, -7.87) * mm});
            skLineSegment(sketch, "E99.25.98", {"start": v(-2.88, -7.86) * mm, "end": v(-2.89, -7.86) * mm});
            skLineSegment(sketch, "E99.25.99", {"start": v(-2.87, -7.87) * mm, "end": v(-2.88, -7.87) * mm});
            skLineSegment(sketch, "E99.26.0", {"start": v(-2.15, -9.07) * mm, "end": v(-2.18, -9.1) * mm});
            skLineSegment(sketch, "E99.26.1", {"start": v(-1.08, -9.26) * mm, "end": v(-1.07, -9.3) * mm});
            skLineSegment(sketch, "E99.26.2", {"start": v(-2.42, -9.19) * mm, "end": v(-2.46, -9.18) * mm});
            skLineSegment(sketch, "E99.26.3", {"start": v(-2.39, -9.2) * mm, "end": v(-2.42, -9.19) * mm});
            skLineSegment(sketch, "E99.26.4", {"start": v(-2.03, -8.92) * mm, "end": v(-2.06, -8.95) * mm});
            skLineSegment(sketch, "E99.26.5", {"start": v(-1.2, -8.84) * mm, "end": v(-1.18, -8.89) * mm});
            skLineSegment(sketch, "E99.26.6", {"start": v(-1.98, -8.84) * mm, "end": v(-2, -8.88) * mm});
            skLineSegment(sketch, "E99.26.7", {"start": v(-1.81, -8.55) * mm, "end": v(-1.84, -8.6) * mm});
            skLineSegment(sketch, "E99.26.8", {"start": v(-2, -8.88) * mm, "end": v(-2.03, -8.92) * mm});
            skLineSegment(sketch, "E99.26.9", {"start": v(-1.86, -8.64) * mm, "end": v(-1.88, -8.68) * mm});
            skLineSegment(sketch, "E99.26.10", {"start": v(-1.17, -8.93) * mm, "end": v(-1.16, -8.98) * mm});
            skLineSegment(sketch, "E99.26.11", {"start": v(-1.21, -8.7) * mm, "end": v(-1.2, -8.75) * mm});
            skLineSegment(sketch, "E99.26.12", {"start": v(-1.15, -9.03) * mm, "end": v(-1.14, -9.07) * mm});
            skLineSegment(sketch, "E99.26.13", {"start": v(-1.93, -8.76) * mm, "end": v(-1.95, -8.8) * mm});
            skLineSegment(sketch, "E99.26.14", {"start": v(-2.18, -9.1) * mm, "end": v(-2.21, -9.15) * mm});
            skLineSegment(sketch, "E99.26.15", {"start": v(-1.9, -8.72) * mm, "end": v(-1.93, -8.76) * mm});
            skLineSegment(sketch, "E99.26.16", {"start": v(-2.12, -9.03) * mm, "end": v(-2.15, -9.07) * mm});
            skLineSegment(sketch, "E99.26.17", {"start": v(-1.95, -8.8) * mm, "end": v(-1.98, -8.84) * mm});
            skLineSegment(sketch, "E99.26.18", {"start": v(-1.1, -9.21) * mm, "end": v(-1.08, -9.26) * mm});
            skLineSegment(sketch, "E99.26.19", {"start": v(-2.21, -9.15) * mm, "end": v(-2.24, -9.19) * mm});
            skLineSegment(sketch, "E99.26.20", {"start": v(-2.35, -9.2) * mm, "end": v(-2.39, -9.2) * mm});
            skLineSegment(sketch, "E99.26.21", {"start": v(-1.22, -8.66) * mm, "end": v(-1.21, -8.7) * mm});
            skLineSegment(sketch, "E99.26.22", {"start": v(-1.2, -8.8) * mm, "end": v(-1.2, -8.84) * mm});
            skLineSegment(sketch, "E99.26.23", {"start": v(-1.12, -9.12) * mm, "end": v(-1.11, -9.17) * mm});
            skLineSegment(sketch, "E99.26.24", {"start": v(-2.06, -8.95) * mm, "end": v(-2.1, -9) * mm});
            skLineSegment(sketch, "E99.26.25", {"start": v(-1.84, -8.6) * mm, "end": v(-1.86, -8.64) * mm});
            skLineSegment(sketch, "E99.26.26", {"start": v(-2.24, -9.19) * mm, "end": v(-2.28, -9.22) * mm});
            skLineSegment(sketch, "E99.26.27", {"start": v(-2.31, -9.21) * mm, "end": v(-2.35, -9.2) * mm});
            skLineSegment(sketch, "E99.26.28", {"start": v(-2.1, -9) * mm, "end": v(-2.12, -9.03) * mm});
            skLineSegment(sketch, "E99.26.29", {"start": v(-1.18, -8.89) * mm, "end": v(-1.17, -8.93) * mm});
            skLineSegment(sketch, "E99.26.30", {"start": v(-1.11, -9.17) * mm, "end": v(-1.1, -9.21) * mm});
            skLineSegment(sketch, "E99.26.31", {"start": v(-1.88, -8.68) * mm, "end": v(-1.9, -8.72) * mm});
            skLineSegment(sketch, "E99.26.32", {"start": v(-1.14, -9.07) * mm, "end": v(-1.12, -9.12) * mm});
            skLineSegment(sketch, "E99.26.33", {"start": v(-1.2, -8.75) * mm, "end": v(-1.2, -8.8) * mm});
            skLineSegment(sketch, "E99.26.34", {"start": v(-1.07, -9.3) * mm, "end": v(-1.05, -9.35) * mm});
            skLineSegment(sketch, "E99.26.35", {"start": v(-0.87, -9.46) * mm, "end": v(-0.83, -9.46) * mm});
            skLineSegment(sketch, "E99.26.36", {"start": v(-1.16, -8.98) * mm, "end": v(-1.15, -9.03) * mm});
            skLineSegment(sketch, "E99.26.37", {"start": v(-0.9, -9.46) * mm, "end": v(-0.87, -9.46) * mm});
            skLineSegment(sketch, "E99.26.38", {"start": v(-1.05, -9.35) * mm, "end": v(-1.03, -9.4) * mm});
            skLineSegment(sketch, "E99.26.39", {"start": v(-2.28, -9.22) * mm, "end": v(-2.31, -9.21) * mm});
            skLineSegment(sketch, "E99.26.40", {"start": v(-1.03, -9.4) * mm, "end": v(-1.02, -9.45) * mm});
            skLineSegment(sketch, "E99.26.41", {"start": v(-0.94, -9.45) * mm, "end": v(-0.9, -9.46) * mm});
            skLineSegment(sketch, "E99.26.42", {"start": v(-0.98, -9.45) * mm, "end": v(-0.94, -9.45) * mm});
            skLineSegment(sketch, "E99.26.43", {"start": v(-1.23, -8.61) * mm, "end": v(-1.22, -8.66) * mm});
            skLineSegment(sketch, "E99.26.44", {"start": v(-1.02, -9.45) * mm, "end": v(-0.98, -9.45) * mm});
            skLineSegment(sketch, "E99.26.45", {"start": v(-1.8, -8.51) * mm, "end": v(-1.81, -8.55) * mm});
            skLineSegment(sketch, "E99.26.46", {"start": v(-1.25, -8.4) * mm, "end": v(-1.25, -8.42) * mm});
            skLineSegment(sketch, "E99.26.47", {"start": v(-1.23, -8.52) * mm, "end": v(-1.23, -8.57) * mm});
            skLineSegment(sketch, "E99.26.48", {"start": v(-1.23, -8.57) * mm, "end": v(-1.23, -8.61) * mm});
            skLineSegment(sketch, "E99.26.49", {"start": v(-1.71, -8.35) * mm, "end": v(-1.72, -8.36) * mm});
            skLineSegment(sketch, "E99.26.50", {"start": v(-1.24, -8.43) * mm, "end": v(-1.24, -8.45) * mm});
            skLineSegment(sketch, "E99.26.51", {"start": v(-1.68, -8.31) * mm, "end": v(-1.7, -8.32) * mm});
            skLineSegment(sketch, "E99.26.52", {"start": v(-1.78, -8.47) * mm, "end": v(-1.8, -8.51) * mm});
            skLineSegment(sketch, "E99.26.53", {"start": v(-1.73, -8.38) * mm, "end": v(-1.74, -8.4) * mm});
            skLineSegment(sketch, "E99.26.54", {"start": v(-1.75, -8.41) * mm, "end": v(-1.76, -8.43) * mm});
            skLineSegment(sketch, "E99.26.55", {"start": v(-1.24, -8.45) * mm, "end": v(-1.24, -8.47) * mm});
            skLineSegment(sketch, "E99.26.56", {"start": v(-1.23, -8.5) * mm, "end": v(-1.23, -8.52) * mm});
            skLineSegment(sketch, "E99.26.57", {"start": v(-1.72, -8.36) * mm, "end": v(-1.73, -8.38) * mm});
            skLineSegment(sketch, "E99.26.58", {"start": v(-1.26, -8.38) * mm, "end": v(-1.25, -8.4) * mm});
            skLineSegment(sketch, "E99.26.59", {"start": v(-1.76, -8.43) * mm, "end": v(-1.78, -8.47) * mm});
            skLineSegment(sketch, "E99.26.60", {"start": v(-1.23, -8.48) * mm, "end": v(-1.23, -8.5) * mm});
            skLineSegment(sketch, "E99.26.61", {"start": v(-1.25, -8.42) * mm, "end": v(-1.24, -8.43) * mm});
            skLineSegment(sketch, "E99.26.62", {"start": v(-1.74, -8.4) * mm, "end": v(-1.75, -8.41) * mm});
            skLineSegment(sketch, "E99.26.63", {"start": v(-1.24, -8.47) * mm, "end": v(-1.23, -8.48) * mm});
            skLineSegment(sketch, "E99.26.64", {"start": v(-1.27, -8.37) * mm, "end": v(-1.26, -8.38) * mm});
            skLineSegment(sketch, "E99.26.65", {"start": v(-1.67, -8.3) * mm, "end": v(-1.68, -8.31) * mm});
            skLineSegment(sketch, "E99.26.66", {"start": v(-1.7, -8.32) * mm, "end": v(-1.7, -8.34) * mm});
            skLineSegment(sketch, "E99.26.67", {"start": v(-1.28, -8.36) * mm, "end": v(-1.27, -8.37) * mm});
            skLineSegment(sketch, "E99.26.68", {"start": v(-1.7, -8.34) * mm, "end": v(-1.71, -8.35) * mm});
            skLineSegment(sketch, "E99.26.69", {"start": v(-1.66, -8.29) * mm, "end": v(-1.67, -8.3) * mm});
            skLineSegment(sketch, "E99.26.70", {"start": v(-1.62, -8.26) * mm, "end": v(-1.63, -8.27) * mm});
            skLineSegment(sketch, "E99.26.71", {"start": v(-1.65, -8.28) * mm, "end": v(-1.66, -8.29) * mm});
            skLineSegment(sketch, "E99.26.72", {"start": v(-1.63, -8.27) * mm, "end": v(-1.65, -8.28) * mm});
            skLineSegment(sketch, "E99.26.73", {"start": v(-1.59, -8.25) * mm, "end": v(-1.6, -8.26) * mm});
            skLineSegment(sketch, "E99.26.74", {"start": v(-1.29, -8.34) * mm, "end": v(-1.28, -8.36) * mm});
            skLineSegment(sketch, "E99.26.75", {"start": v(-1.6, -8.26) * mm, "end": v(-1.62, -8.26) * mm});
            skLineSegment(sketch, "E99.26.76", {"start": v(-1.45, -8.25) * mm, "end": v(-1.46, -8.25) * mm});
            skLineSegment(sketch, "E99.26.77", {"start": v(-1.51, -8.24) * mm, "end": v(-1.53, -8.24) * mm});
            skLineSegment(sketch, "E99.26.78", {"start": v(-1.48, -8.24) * mm, "end": v(-1.51, -8.24) * mm});
            skLineSegment(sketch, "E99.26.79", {"start": v(-1.42, -8.25) * mm, "end": v(-1.4, -8.26) * mm});
            skLineSegment(sketch, "E99.26.80", {"start": v(-1.33, -8.3) * mm, "end": v(-1.32, -8.3) * mm});
            skLineSegment(sketch, "E99.26.81", {"start": v(-1.3, -8.32) * mm, "end": v(-1.3, -8.33) * mm});
            skLineSegment(sketch, "E99.26.82", {"start": v(-1.57, -8.24) * mm, "end": v(-1.59, -8.25) * mm});
            skLineSegment(sketch, "E99.26.83", {"start": v(-1.38, -8.27) * mm, "end": v(-1.36, -8.28) * mm});
            skLineSegment(sketch, "E99.26.84", {"start": v(-1.3, -8.33) * mm, "end": v(-1.29, -8.34) * mm});
            skLineSegment(sketch, "E99.26.85", {"start": v(-1.53, -8.24) * mm, "end": v(-1.55, -8.24) * mm});
            skLineSegment(sketch, "E99.26.86", {"start": v(-1.32, -8.3) * mm, "end": v(-1.3, -8.32) * mm});
            skLineSegment(sketch, "E99.26.87", {"start": v(-1.4, -8.26) * mm, "end": v(-1.38, -8.27) * mm});
            skLineSegment(sketch, "E99.26.88", {"start": v(-1.34, -8.28) * mm, "end": v(-1.33, -8.3) * mm});
            skLineSegment(sketch, "E99.26.89", {"start": v(-1.47, -8.25) * mm, "end": v(-1.47, -8.24) * mm});
            skLineSegment(sketch, "E99.26.90", {"start": v(-1.48, -8.24) * mm, "end": v(-1.48, -8.24) * mm});
            skLineSegment(sketch, "E99.26.91", {"start": v(-1.55, -8.24) * mm, "end": v(-1.57, -8.24) * mm});
            skLineSegment(sketch, "E99.26.92", {"start": v(-1.36, -8.28) * mm, "end": v(-1.34, -8.28) * mm});
            skLineSegment(sketch, "E99.26.93", {"start": v(-1.43, -8.25) * mm, "end": v(-1.42, -8.25) * mm});
            skLineSegment(sketch, "E99.26.94", {"start": v(-1.44, -8.25) * mm, "end": v(-1.43, -8.25) * mm});
            skLineSegment(sketch, "E99.26.95", {"start": v(-1.44, -8.25) * mm, "end": v(-1.44, -8.25) * mm});
            skLineSegment(sketch, "E99.26.96", {"start": v(-1.45, -8.25) * mm, "end": v(-1.44, -8.25) * mm});
            skLineSegment(sketch, "E99.26.97", {"start": v(-1.45, -8.25) * mm, "end": v(-1.45, -8.25) * mm});
            skLineSegment(sketch, "E99.26.98", {"start": v(-1.47, -8.24) * mm, "end": v(-1.48, -8.24) * mm});
            skLineSegment(sketch, "E99.26.99", {"start": v(-1.46, -8.25) * mm, "end": v(-1.47, -8.25) * mm});
            skLineSegment(sketch, "E99.27.0", {"start": v(-0.54, -9.3) * mm, "end": v(-0.57, -9.35) * mm});
            skLineSegment(sketch, "E99.27.1", {"start": v(0.54, -9.3) * mm, "end": v(0.57, -9.35) * mm});
            skLineSegment(sketch, "E99.27.2", {"start": v(-0.8, -9.47) * mm, "end": v(-0.83, -9.46) * mm});
            skLineSegment(sketch, "E99.27.3", {"start": v(-0.75, -9.47) * mm, "end": v(-0.8, -9.47) * mm});
            skLineSegment(sketch, "E99.27.4", {"start": v(-0.46, -9.13) * mm, "end": v(-0.48, -9.18) * mm});
            skLineSegment(sketch, "E99.27.5", {"start": v(0.36, -8.91) * mm, "end": v(0.38, -8.96) * mm});
            skLineSegment(sketch, "E99.27.6", {"start": v(-0.42, -9.05) * mm, "end": v(-0.44, -9.09) * mm});
            skLineSegment(sketch, "E99.27.7", {"start": v(-0.3, -8.74) * mm, "end": v(-0.32, -8.78) * mm});
            skLineSegment(sketch, "E99.27.8", {"start": v(-0.44, -9.09) * mm, "end": v(-0.46, -9.13) * mm});
            skLineSegment(sketch, "E99.27.9", {"start": v(-0.33, -8.83) * mm, "end": v(-0.35, -8.87) * mm});
            skLineSegment(sketch, "E99.27.10", {"start": v(0.4, -9) * mm, "end": v(0.42, -9.05) * mm});
            skLineSegment(sketch, "E99.27.11", {"start": v(0.32, -8.78) * mm, "end": v(0.33, -8.83) * mm});
            skLineSegment(sketch, "E99.27.12", {"start": v(0.44, -9.09) * mm, "end": v(0.46, -9.13) * mm});
            skLineSegment(sketch, "E99.27.13", {"start": v(-0.38, -8.96) * mm, "end": v(-0.4, -9) * mm});
            skLineSegment(sketch, "E99.27.14", {"start": v(-0.57, -9.35) * mm, "end": v(-0.6, -9.4) * mm});
            skLineSegment(sketch, "E99.27.15", {"start": v(-0.36, -8.91) * mm, "end": v(-0.38, -8.96) * mm});
            skLineSegment(sketch, "E99.27.16", {"start": v(-0.52, -9.26) * mm, "end": v(-0.54, -9.3) * mm});
            skLineSegment(sketch, "E99.27.17", {"start": v(-0.4, -9) * mm, "end": v(-0.42, -9.05) * mm});
            skLineSegment(sketch, "E99.27.18", {"start": v(0.52, -9.26) * mm, "end": v(0.54, -9.3) * mm});
            skLineSegment(sketch, "E99.27.19", {"start": v(-0.6, -9.4) * mm, "end": v(-0.61, -9.44) * mm});
            skLineSegment(sketch, "E99.27.20", {"start": v(-0.72, -9.47) * mm, "end": v(-0.75, -9.47) * mm});
            skLineSegment(sketch, "E99.27.21", {"start": v(0.3, -8.74) * mm, "end": v(0.32, -8.78) * mm});
            skLineSegment(sketch, "E99.27.22", {"start": v(0.35, -8.87) * mm, "end": v(0.36, -8.91) * mm});
            skLineSegment(sketch, "E99.27.23", {"start": v(0.48, -9.18) * mm, "end": v(0.5, -9.22) * mm});
            skLineSegment(sketch, "E99.27.24", {"start": v(-0.48, -9.18) * mm, "end": v(-0.5, -9.22) * mm});
            skLineSegment(sketch, "E99.27.25", {"start": v(-0.32, -8.78) * mm, "end": v(-0.33, -8.83) * mm});
            skLineSegment(sketch, "E99.27.26", {"start": v(-0.61, -9.44) * mm, "end": v(-0.64, -9.48) * mm});
            skLineSegment(sketch, "E99.27.27", {"start": v(-0.68, -9.48) * mm, "end": v(-0.72, -9.47) * mm});
            skLineSegment(sketch, "E99.27.28", {"start": v(-0.5, -9.22) * mm, "end": v(-0.52, -9.26) * mm});
            skLineSegment(sketch, "E99.27.29", {"start": v(0.38, -8.96) * mm, "end": v(0.4, -9) * mm});
            skLineSegment(sketch, "E99.27.30", {"start": v(0.5, -9.22) * mm, "end": v(0.52, -9.26) * mm});
            skLineSegment(sketch, "E99.27.31", {"start": v(-0.35, -8.87) * mm, "end": v(-0.36, -8.91) * mm});
            skLineSegment(sketch, "E99.27.32", {"start": v(0.46, -9.13) * mm, "end": v(0.48, -9.18) * mm});
            skLineSegment(sketch, "E99.27.33", {"start": v(0.33, -8.83) * mm, "end": v(0.35, -8.87) * mm});
            skLineSegment(sketch, "E99.27.34", {"start": v(0.57, -9.35) * mm, "end": v(0.6, -9.4) * mm});
            skLineSegment(sketch, "E99.27.35", {"start": v(0.8, -9.47) * mm, "end": v(0.83, -9.46) * mm});
            skLineSegment(sketch, "E99.27.36", {"start": v(0.42, -9.05) * mm, "end": v(0.44, -9.09) * mm});
            skLineSegment(sketch, "E99.27.37", {"start": v(0.75, -9.47) * mm, "end": v(0.8, -9.47) * mm});
            skLineSegment(sketch, "E99.27.38", {"start": v(0.6, -9.4) * mm, "end": v(0.61, -9.44) * mm});
            skLineSegment(sketch, "E99.27.39", {"start": v(-0.64, -9.48) * mm, "end": v(-0.68, -9.48) * mm});
            skLineSegment(sketch, "E99.27.40", {"start": v(0.61, -9.44) * mm, "end": v(0.64, -9.48) * mm});
            skLineSegment(sketch, "E99.27.41", {"start": v(0.72, -9.47) * mm, "end": v(0.75, -9.47) * mm});
            skLineSegment(sketch, "E99.27.42", {"start": v(0.68, -9.48) * mm, "end": v(0.72, -9.47) * mm});
            skLineSegment(sketch, "E99.27.43", {"start": v(0.29, -8.7) * mm, "end": v(0.3, -8.74) * mm});
            skLineSegment(sketch, "E99.27.44", {"start": v(0.64, -9.48) * mm, "end": v(0.68, -9.48) * mm});
            skLineSegment(sketch, "E99.27.45", {"start": v(-0.29, -8.7) * mm, "end": v(-0.3, -8.74) * mm});
            skLineSegment(sketch, "E99.27.46", {"start": v(0.22, -8.5) * mm, "end": v(0.23, -8.5) * mm});
            skLineSegment(sketch, "E99.27.47", {"start": v(0.27, -8.6) * mm, "end": v(0.28, -8.65) * mm});
            skLineSegment(sketch, "E99.27.48", {"start": v(0.28, -8.65) * mm, "end": v(0.29, -8.7) * mm});
            skLineSegment(sketch, "E99.27.49", {"start": v(-0.24, -8.52) * mm, "end": v(-0.25, -8.54) * mm});
            skLineSegment(sketch, "E99.27.50", {"start": v(0.24, -8.52) * mm, "end": v(0.25, -8.54) * mm});
            skLineSegment(sketch, "E99.27.51", {"start": v(-0.21, -8.48) * mm, "end": v(-0.22, -8.5) * mm});
            skLineSegment(sketch, "E99.27.52", {"start": v(-0.28, -8.65) * mm, "end": v(-0.29, -8.7) * mm});
            skLineSegment(sketch, "E99.27.53", {"start": v(-0.25, -8.55) * mm, "end": v(-0.26, -8.57) * mm});
            skLineSegment(sketch, "E99.27.54", {"start": v(-0.26, -8.59) * mm, "end": v(-0.27, -8.6) * mm});
            skLineSegment(sketch, "E99.27.55", {"start": v(0.25, -8.54) * mm, "end": v(0.25, -8.55) * mm});
            skLineSegment(sketch, "E99.27.56", {"start": v(0.26, -8.59) * mm, "end": v(0.27, -8.6) * mm});
            skLineSegment(sketch, "E99.27.57", {"start": v(-0.25, -8.54) * mm, "end": v(-0.25, -8.55) * mm});
            skLineSegment(sketch, "E99.27.58", {"start": v(0.21, -8.48) * mm, "end": v(0.22, -8.5) * mm});
            skLineSegment(sketch, "E99.27.59", {"start": v(-0.27, -8.6) * mm, "end": v(-0.28, -8.65) * mm});
            skLineSegment(sketch, "E99.27.60", {"start": v(0.26, -8.57) * mm, "end": v(0.26, -8.59) * mm});
            skLineSegment(sketch, "E99.27.61", {"start": v(0.23, -8.5) * mm, "end": v(0.24, -8.52) * mm});
            skLineSegment(sketch, "E99.27.62", {"start": v(-0.26, -8.57) * mm, "end": v(-0.26, -8.59) * mm});
            skLineSegment(sketch, "E99.27.63", {"start": v(0.25, -8.55) * mm, "end": v(0.26, -8.57) * mm});
            skLineSegment(sketch, "E99.27.64", {"start": v(0.2, -8.46) * mm, "end": v(0.21, -8.48) * mm});
            skLineSegment(sketch, "E99.27.65", {"start": v(-0.2, -8.46) * mm, "end": v(-0.21, -8.48) * mm});
            skLineSegment(sketch, "E99.27.66", {"start": v(-0.22, -8.5) * mm, "end": v(-0.23, -8.5) * mm});
            skLineSegment(sketch, "E99.27.67", {"start": v(0.2, -8.45) * mm, "end": v(0.2, -8.46) * mm});
            skLineSegment(sketch, "E99.27.68", {"start": v(-0.23, -8.5) * mm, "end": v(-0.24, -8.52) * mm});
            skLineSegment(sketch, "E99.27.69", {"start": v(-0.2, -8.45) * mm, "end": v(-0.2, -8.46) * mm});
            skLineSegment(sketch, "E99.27.70", {"start": v(-0.16, -8.42) * mm, "end": v(-0.17, -8.43) * mm});
            skLineSegment(sketch, "E99.27.71", {"start": v(-0.18, -8.44) * mm, "end": v(-0.2, -8.45) * mm});
            skLineSegment(sketch, "E99.27.72", {"start": v(-0.17, -8.43) * mm, "end": v(-0.18, -8.44) * mm});
            skLineSegment(sketch, "E99.27.73", {"start": v(-0.13, -8.4) * mm, "end": v(-0.14, -8.4) * mm});
            skLineSegment(sketch, "E99.27.74", {"start": v(0.18, -8.44) * mm, "end": v(0.2, -8.45) * mm});
            skLineSegment(sketch, "E99.27.75", {"start": v(-0.14, -8.4) * mm, "end": v(-0.16, -8.42) * mm});
            skLineSegment(sketch, "E99.27.76", {"start": v(0, -8.38) * mm, "end": v(0, -8.37) * mm});
            skLineSegment(sketch, "E99.27.77", {"start": v(-0.06, -8.38) * mm, "end": v(-0.08, -8.38) * mm});
            skLineSegment(sketch, "E99.27.78", {"start": v(-0.03, -8.37) * mm, "end": v(-0.06, -8.38) * mm});
            skLineSegment(sketch, "E99.27.79", {"start": v(0.03, -8.37) * mm, "end": v(0.06, -8.38) * mm});
            skLineSegment(sketch, "E99.27.80", {"start": v(0.13, -8.4) * mm, "end": v(0.14, -8.4) * mm});
            skLineSegment(sketch, "E99.27.81", {"start": v(0.16, -8.42) * mm, "end": v(0.17, -8.43) * mm});
            skLineSegment(sketch, "E99.27.82", {"start": v(-0.11, -8.4) * mm, "end": v(-0.13, -8.4) * mm});
            skLineSegment(sketch, "E99.27.83", {"start": v(0.08, -8.38) * mm, "end": v(0.1, -8.39) * mm});
            skLineSegment(sketch, "E99.27.84", {"start": v(0.17, -8.43) * mm, "end": v(0.18, -8.44) * mm});
            skLineSegment(sketch, "E99.27.85", {"start": v(-0.08, -8.38) * mm, "end": v(-0.1, -8.39) * mm});
            skLineSegment(sketch, "E99.27.86", {"start": v(0.14, -8.4) * mm, "end": v(0.16, -8.42) * mm});
            skLineSegment(sketch, "E99.27.87", {"start": v(0.06, -8.38) * mm, "end": v(0.08, -8.38) * mm});
            skLineSegment(sketch, "E99.27.88", {"start": v(0.11, -8.4) * mm, "end": v(0.13, -8.4) * mm});
            skLineSegment(sketch, "E99.27.89", {"start": v(-0.01, -8.37) * mm, "end": v(-0.02, -8.37) * mm});
            skLineSegment(sketch, "E99.27.90", {"start": v(-0.02, -8.37) * mm, "end": v(-0.03, -8.37) * mm});
            skLineSegment(sketch, "E99.27.91", {"start": v(-0.1, -8.39) * mm, "end": v(-0.11, -8.4) * mm});
            skLineSegment(sketch, "E99.27.92", {"start": v(0.1, -8.39) * mm, "end": v(0.11, -8.4) * mm});
            skLineSegment(sketch, "E99.27.93", {"start": v(0.02, -8.37) * mm, "end": v(0.03, -8.37) * mm});
            skLineSegment(sketch, "E99.27.94", {"start": v(0.02, -8.37) * mm, "end": v(0.02, -8.37) * mm});
            skLineSegment(sketch, "E99.27.95", {"start": v(0.01, -8.37) * mm, "end": v(0.02, -8.37) * mm});
            skLineSegment(sketch, "E99.27.96", {"start": v(0, -8.37) * mm, "end": v(0.01, -8.37) * mm});
            skLineSegment(sketch, "E99.27.97", {"start": v(0, -8.38) * mm, "end": v(0, -8.37) * mm});
            skLineSegment(sketch, "E99.27.98", {"start": v(-0.02, -8.37) * mm, "end": v(-0.02, -8.37) * mm});
            skLineSegment(sketch, "E99.27.99", {"start": v(0, -8.37) * mm, "end": v(-0.01, -8.37) * mm});
            skLineSegment(sketch, "E99.28.0", {"start": v(1.08, -9.26) * mm, "end": v(1.07, -9.3) * mm});
            skLineSegment(sketch, "E99.28.1", {"start": v(2.15, -9.07) * mm, "end": v(2.18, -9.1) * mm});
            skLineSegment(sketch, "E99.28.2", {"start": v(0.87, -9.46) * mm, "end": v(0.83, -9.46) * mm});
            skLineSegment(sketch, "E99.28.3", {"start": v(0.9, -9.46) * mm, "end": v(0.87, -9.46) * mm});
            skLineSegment(sketch, "E99.28.4", {"start": v(1.14, -9.07) * mm, "end": v(1.12, -9.12) * mm});
            skLineSegment(sketch, "E99.28.5", {"start": v(1.9, -8.72) * mm, "end": v(1.93, -8.76) * mm});
            skLineSegment(sketch, "E99.28.6", {"start": v(1.16, -8.98) * mm, "end": v(1.15, -9.03) * mm});
            skLineSegment(sketch, "E99.28.7", {"start": v(1.22, -8.66) * mm, "end": v(1.21, -8.7) * mm});
            skLineSegment(sketch, "E99.28.8", {"start": v(1.15, -9.03) * mm, "end": v(1.14, -9.07) * mm});
            skLineSegment(sketch, "E99.28.9", {"start": v(1.2, -8.75) * mm, "end": v(1.2, -8.8) * mm});
            skLineSegment(sketch, "E99.28.10", {"start": v(1.95, -8.8) * mm, "end": v(1.98, -8.84) * mm});
            skLineSegment(sketch, "E99.28.11", {"start": v(1.84, -8.6) * mm, "end": v(1.86, -8.64) * mm});
            skLineSegment(sketch, "E99.28.12", {"start": v(2, -8.88) * mm, "end": v(2.03, -8.92) * mm});
            skLineSegment(sketch, "E99.28.13", {"start": v(1.18, -8.89) * mm, "end": v(1.17, -8.93) * mm});
            skLineSegment(sketch, "E99.28.14", {"start": v(1.07, -9.3) * mm, "end": v(1.05, -9.35) * mm});
            skLineSegment(sketch, "E99.28.15", {"start": v(1.2, -8.84) * mm, "end": v(1.18, -8.89) * mm});
            skLineSegment(sketch, "E99.28.16", {"start": v(1.1, -9.21) * mm, "end": v(1.08, -9.26) * mm});
            skLineSegment(sketch, "E99.28.17", {"start": v(1.17, -8.93) * mm, "end": v(1.16, -8.98) * mm});
            skLineSegment(sketch, "E99.28.18", {"start": v(2.12, -9.03) * mm, "end": v(2.15, -9.07) * mm});
            skLineSegment(sketch, "E99.28.19", {"start": v(1.05, -9.35) * mm, "end": v(1.03, -9.4) * mm});
            skLineSegment(sketch, "E99.28.20", {"start": v(0.94, -9.45) * mm, "end": v(0.9, -9.46) * mm});
            skLineSegment(sketch, "E99.28.21", {"start": v(1.81, -8.55) * mm, "end": v(1.84, -8.6) * mm});
            skLineSegment(sketch, "E99.28.22", {"start": v(1.88, -8.68) * mm, "end": v(1.9, -8.72) * mm});
            skLineSegment(sketch, "E99.28.23", {"start": v(2.06, -8.95) * mm, "end": v(2.1, -9) * mm});
            skLineSegment(sketch, "E99.28.24", {"start": v(1.12, -9.12) * mm, "end": v(1.11, -9.17) * mm});
            skLineSegment(sketch, "E99.28.25", {"start": v(1.21, -8.7) * mm, "end": v(1.2, -8.75) * mm});
            skLineSegment(sketch, "E99.28.26", {"start": v(1.03, -9.4) * mm, "end": v(1.02, -9.45) * mm});
            skLineSegment(sketch, "E99.28.27", {"start": v(0.98, -9.45) * mm, "end": v(0.94, -9.45) * mm});
            skLineSegment(sketch, "E99.28.28", {"start": v(1.11, -9.17) * mm, "end": v(1.1, -9.21) * mm});
            skLineSegment(sketch, "E99.28.29", {"start": v(1.93, -8.76) * mm, "end": v(1.95, -8.8) * mm});
            skLineSegment(sketch, "E99.28.30", {"start": v(2.1, -9) * mm, "end": v(2.12, -9.03) * mm});
            skLineSegment(sketch, "E99.28.31", {"start": v(1.2, -8.8) * mm, "end": v(1.2, -8.84) * mm});
            skLineSegment(sketch, "E99.28.32", {"start": v(2.03, -8.92) * mm, "end": v(2.06, -8.95) * mm});
            skLineSegment(sketch, "E99.28.33", {"start": v(1.86, -8.64) * mm, "end": v(1.88, -8.68) * mm});
            skLineSegment(sketch, "E99.28.34", {"start": v(2.18, -9.1) * mm, "end": v(2.21, -9.15) * mm});
            skLineSegment(sketch, "E99.28.35", {"start": v(2.42, -9.19) * mm, "end": v(2.46, -9.18) * mm});
            skLineSegment(sketch, "E99.28.36", {"start": v(1.98, -8.84) * mm, "end": v(2, -8.88) * mm});
            skLineSegment(sketch, "E99.28.37", {"start": v(2.39, -9.2) * mm, "end": v(2.42, -9.19) * mm});
            skLineSegment(sketch, "E99.28.38", {"start": v(2.21, -9.15) * mm, "end": v(2.24, -9.19) * mm});
            skLineSegment(sketch, "E99.28.39", {"start": v(1.02, -9.45) * mm, "end": v(0.98, -9.45) * mm});
            skLineSegment(sketch, "E99.28.40", {"start": v(2.24, -9.19) * mm, "end": v(2.28, -9.22) * mm});
            skLineSegment(sketch, "E99.28.41", {"start": v(2.35, -9.2) * mm, "end": v(2.39, -9.2) * mm});
            skLineSegment(sketch, "E99.28.42", {"start": v(2.31, -9.21) * mm, "end": v(2.35, -9.2) * mm});
            skLineSegment(sketch, "E99.28.43", {"start": v(1.8, -8.51) * mm, "end": v(1.81, -8.55) * mm});
            skLineSegment(sketch, "E99.28.44", {"start": v(2.28, -9.22) * mm, "end": v(2.31, -9.21) * mm});
            skLineSegment(sketch, "E99.28.45", {"start": v(1.23, -8.61) * mm, "end": v(1.22, -8.66) * mm});
            skLineSegment(sketch, "E99.28.46", {"start": v(1.7, -8.32) * mm, "end": v(1.7, -8.34) * mm});
            skLineSegment(sketch, "E99.28.47", {"start": v(1.76, -8.43) * mm, "end": v(1.78, -8.47) * mm});
            skLineSegment(sketch, "E99.28.48", {"start": v(1.78, -8.47) * mm, "end": v(1.8, -8.51) * mm});
            skLineSegment(sketch, "E99.28.49", {"start": v(1.24, -8.43) * mm, "end": v(1.24, -8.45) * mm});
            skLineSegment(sketch, "E99.28.50", {"start": v(1.71, -8.35) * mm, "end": v(1.72, -8.36) * mm});
            skLineSegment(sketch, "E99.28.51", {"start": v(1.26, -8.38) * mm, "end": v(1.25, -8.4) * mm});
            skLineSegment(sketch, "E99.28.52", {"start": v(1.23, -8.57) * mm, "end": v(1.23, -8.61) * mm});
            skLineSegment(sketch, "E99.28.53", {"start": v(1.24, -8.47) * mm, "end": v(1.23, -8.48) * mm});
            skLineSegment(sketch, "E99.28.54", {"start": v(1.23, -8.5) * mm, "end": v(1.23, -8.52) * mm});
            skLineSegment(sketch, "E99.28.55", {"start": v(1.72, -8.36) * mm, "end": v(1.73, -8.38) * mm});
            skLineSegment(sketch, "E99.28.56", {"start": v(1.75, -8.41) * mm, "end": v(1.76, -8.43) * mm});
            skLineSegment(sketch, "E99.28.57", {"start": v(1.24, -8.45) * mm, "end": v(1.24, -8.47) * mm});
            skLineSegment(sketch, "E99.28.58", {"start": v(1.68, -8.31) * mm, "end": v(1.7, -8.32) * mm});
            skLineSegment(sketch, "E99.28.59", {"start": v(1.23, -8.52) * mm, "end": v(1.23, -8.57) * mm});
            skLineSegment(sketch, "E99.28.60", {"start": v(1.74, -8.4) * mm, "end": v(1.75, -8.41) * mm});
            skLineSegment(sketch, "E99.28.61", {"start": v(1.7, -8.34) * mm, "end": v(1.71, -8.35) * mm});
            skLineSegment(sketch, "E99.28.62", {"start": v(1.23, -8.48) * mm, "end": v(1.23, -8.5) * mm});
            skLineSegment(sketch, "E99.28.63", {"start": v(1.73, -8.38) * mm, "end": v(1.74, -8.4) * mm});
            skLineSegment(sketch, "E99.28.64", {"start": v(1.67, -8.3) * mm, "end": v(1.68, -8.31) * mm});
            skLineSegment(sketch, "E99.28.65", {"start": v(1.27, -8.37) * mm, "end": v(1.26, -8.38) * mm});
            skLineSegment(sketch, "E99.28.66", {"start": v(1.25, -8.4) * mm, "end": v(1.25, -8.42) * mm});
            skLineSegment(sketch, "E99.28.67", {"start": v(1.66, -8.29) * mm, "end": v(1.67, -8.3) * mm});
            skLineSegment(sketch, "E99.28.68", {"start": v(1.25, -8.42) * mm, "end": v(1.24, -8.43) * mm});
            skLineSegment(sketch, "E99.28.69", {"start": v(1.28, -8.36) * mm, "end": v(1.27, -8.37) * mm});
            skLineSegment(sketch, "E99.28.70", {"start": v(1.3, -8.32) * mm, "end": v(1.3, -8.33) * mm});
            skLineSegment(sketch, "E99.28.71", {"start": v(1.29, -8.34) * mm, "end": v(1.28, -8.36) * mm});
            skLineSegment(sketch, "E99.28.72", {"start": v(1.3, -8.33) * mm, "end": v(1.29, -8.34) * mm});
            skLineSegment(sketch, "E99.28.73", {"start": v(1.33, -8.3) * mm, "end": v(1.32, -8.3) * mm});
            skLineSegment(sketch, "E99.28.74", {"start": v(1.65, -8.28) * mm, "end": v(1.66, -8.29) * mm});
            skLineSegment(sketch, "E99.28.75", {"start": v(1.32, -8.3) * mm, "end": v(1.3, -8.32) * mm});
            skLineSegment(sketch, "E99.28.76", {"start": v(1.45, -8.25) * mm, "end": v(1.45, -8.25) * mm});
            skLineSegment(sketch, "E99.28.77", {"start": v(1.4, -8.26) * mm, "end": v(1.38, -8.27) * mm});
            skLineSegment(sketch, "E99.28.78", {"start": v(1.42, -8.25) * mm, "end": v(1.4, -8.26) * mm});
            skLineSegment(sketch, "E99.28.79", {"start": v(1.48, -8.24) * mm, "end": v(1.51, -8.24) * mm});
            skLineSegment(sketch, "E99.28.80", {"start": v(1.59, -8.25) * mm, "end": v(1.6, -8.26) * mm});
            skLineSegment(sketch, "E99.28.81", {"start": v(1.62, -8.26) * mm, "end": v(1.63, -8.27) * mm});
            skLineSegment(sketch, "E99.28.82", {"start": v(1.34, -8.28) * mm, "end": v(1.33, -8.3) * mm});
            skLineSegment(sketch, "E99.28.83", {"start": v(1.53, -8.24) * mm, "end": v(1.55, -8.24) * mm});
            skLineSegment(sketch, "E99.28.84", {"start": v(1.63, -8.27) * mm, "end": v(1.65, -8.28) * mm});
            skLineSegment(sketch, "E99.28.85", {"start": v(1.38, -8.27) * mm, "end": v(1.36, -8.28) * mm});
            skLineSegment(sketch, "E99.28.86", {"start": v(1.6, -8.26) * mm, "end": v(1.62, -8.26) * mm});
            skLineSegment(sketch, "E99.28.87", {"start": v(1.51, -8.24) * mm, "end": v(1.53, -8.24) * mm});
            skLineSegment(sketch, "E99.28.88", {"start": v(1.57, -8.24) * mm, "end": v(1.59, -8.25) * mm});
            skLineSegment(sketch, "E99.28.89", {"start": v(1.44, -8.25) * mm, "end": v(1.44, -8.25) * mm});
            skLineSegment(sketch, "E99.28.90", {"start": v(1.43, -8.25) * mm, "end": v(1.42, -8.25) * mm});
            skLineSegment(sketch, "E99.28.91", {"start": v(1.36, -8.28) * mm, "end": v(1.34, -8.28) * mm});
            skLineSegment(sketch, "E99.28.92", {"start": v(1.55, -8.24) * mm, "end": v(1.57, -8.24) * mm});
            skLineSegment(sketch, "E99.28.93", {"start": v(1.48, -8.24) * mm, "end": v(1.48, -8.24) * mm});
            skLineSegment(sketch, "E99.28.94", {"start": v(1.47, -8.24) * mm, "end": v(1.48, -8.24) * mm});
            skLineSegment(sketch, "E99.28.95", {"start": v(1.47, -8.25) * mm, "end": v(1.47, -8.24) * mm});
            skLineSegment(sketch, "E99.28.96", {"start": v(1.46, -8.25) * mm, "end": v(1.47, -8.25) * mm});
            skLineSegment(sketch, "E99.28.97", {"start": v(1.45, -8.25) * mm, "end": v(1.46, -8.25) * mm});
            skLineSegment(sketch, "E99.28.98", {"start": v(1.44, -8.25) * mm, "end": v(1.43, -8.25) * mm});
            skLineSegment(sketch, "E99.28.99", {"start": v(1.45, -8.25) * mm, "end": v(1.44, -8.25) * mm});
            skLineSegment(sketch, "E99.29.0", {"start": v(2.67, -8.93) * mm, "end": v(2.67, -8.98) * mm});
            skLineSegment(sketch, "E99.29.1", {"start": v(3.7, -8.56) * mm, "end": v(3.73, -8.6) * mm});
            skLineSegment(sketch, "E99.29.2", {"start": v(2.5, -9.17) * mm, "end": v(2.46, -9.18) * mm});
            skLineSegment(sketch, "E99.29.3", {"start": v(2.53, -9.16) * mm, "end": v(2.5, -9.17) * mm});
            skLineSegment(sketch, "E99.29.4", {"start": v(2.7, -8.74) * mm, "end": v(2.7, -8.79) * mm});
            skLineSegment(sketch, "E99.29.5", {"start": v(3.39, -8.25) * mm, "end": v(3.42, -8.29) * mm});
            skLineSegment(sketch, "E99.29.6", {"start": v(2.7, -8.64) * mm, "end": v(2.7, -8.69) * mm});
            skLineSegment(sketch, "E99.29.7", {"start": v(2.7, -8.31) * mm, "end": v(2.7, -8.36) * mm});
            skLineSegment(sketch, "E99.29.8", {"start": v(2.7, -8.69) * mm, "end": v(2.7, -8.74) * mm});
            skLineSegment(sketch, "E99.29.9", {"start": v(2.7, -8.4) * mm, "end": v(2.7, -8.45) * mm});
            skLineSegment(sketch, "E99.29.10", {"start": v(3.45, -8.32) * mm, "end": v(3.48, -8.36) * mm});
            skLineSegment(sketch, "E99.29.11", {"start": v(3.3, -8.15) * mm, "end": v(3.33, -8.18) * mm});
            skLineSegment(sketch, "E99.29.12", {"start": v(3.52, -8.4) * mm, "end": v(3.55, -8.43) * mm});
            skLineSegment(sketch, "E99.29.13", {"start": v(2.7, -8.55) * mm, "end": v(2.7, -8.6) * mm});
            skLineSegment(sketch, "E99.29.14", {"start": v(2.67, -8.98) * mm, "end": v(2.66, -9.03) * mm});
            skLineSegment(sketch, "E99.29.15", {"start": v(2.7, -8.5) * mm, "end": v(2.7, -8.55) * mm});
            skLineSegment(sketch, "E99.29.16", {"start": v(2.68, -8.88) * mm, "end": v(2.67, -8.93) * mm});
            skLineSegment(sketch, "E99.29.17", {"start": v(2.7, -8.6) * mm, "end": v(2.7, -8.64) * mm});
            skLineSegment(sketch, "E99.29.18", {"start": v(3.66, -8.53) * mm, "end": v(3.7, -8.56) * mm});
            skLineSegment(sketch, "E99.29.19", {"start": v(2.66, -9.03) * mm, "end": v(2.65, -9.08) * mm});
            skLineSegment(sketch, "E99.29.20", {"start": v(2.57, -9.15) * mm, "end": v(2.53, -9.16) * mm});
            skLineSegment(sketch, "E99.29.21", {"start": v(3.27, -8.1) * mm, "end": v(3.3, -8.15) * mm});
            skLineSegment(sketch, "E99.29.22", {"start": v(3.36, -8.22) * mm, "end": v(3.39, -8.25) * mm});
            skLineSegment(sketch, "E99.29.23", {"start": v(3.59, -8.46) * mm, "end": v(3.62, -8.5) * mm});
            skLineSegment(sketch, "E99.29.24", {"start": v(2.7, -8.79) * mm, "end": v(2.69, -8.83) * mm});
            skLineSegment(sketch, "E99.29.25", {"start": v(2.7, -8.36) * mm, "end": v(2.7, -8.4) * mm});
            skLineSegment(sketch, "E99.29.26", {"start": v(2.65, -9.08) * mm, "end": v(2.64, -9.13) * mm});
            skLineSegment(sketch, "E99.29.27", {"start": v(2.6, -9.14) * mm, "end": v(2.57, -9.15) * mm});
            skLineSegment(sketch, "E99.29.28", {"start": v(2.69, -8.83) * mm, "end": v(2.68, -8.88) * mm});
            skLineSegment(sketch, "E99.29.29", {"start": v(3.42, -8.29) * mm, "end": v(3.45, -8.32) * mm});
            skLineSegment(sketch, "E99.29.30", {"start": v(3.62, -8.5) * mm, "end": v(3.66, -8.53) * mm});
            skLineSegment(sketch, "E99.29.31", {"start": v(2.7, -8.45) * mm, "end": v(2.7, -8.5) * mm});
            skLineSegment(sketch, "E99.29.32", {"start": v(3.55, -8.43) * mm, "end": v(3.59, -8.46) * mm});
            skLineSegment(sketch, "E99.29.33", {"start": v(3.33, -8.18) * mm, "end": v(3.36, -8.22) * mm});
            skLineSegment(sketch, "E99.29.34", {"start": v(3.73, -8.6) * mm, "end": v(3.77, -8.62) * mm});
            skLineSegment(sketch, "E99.29.35", {"start": v(3.98, -8.63) * mm, "end": v(4.01, -8.6) * mm});
            skLineSegment(sketch, "E99.29.36", {"start": v(3.48, -8.36) * mm, "end": v(3.52, -8.4) * mm});
            skLineSegment(sketch, "E99.29.37", {"start": v(3.95, -8.64) * mm, "end": v(3.98, -8.63) * mm});
            skLineSegment(sketch, "E99.29.38", {"start": v(3.77, -8.62) * mm, "end": v(3.8, -8.66) * mm});
            skLineSegment(sketch, "E99.29.39", {"start": v(2.64, -9.13) * mm, "end": v(2.6, -9.14) * mm});
            skLineSegment(sketch, "E99.29.40", {"start": v(3.8, -8.66) * mm, "end": v(3.84, -8.69) * mm});
            skLineSegment(sketch, "E99.29.41", {"start": v(3.91, -8.66) * mm, "end": v(3.95, -8.64) * mm});
            skLineSegment(sketch, "E99.29.42", {"start": v(3.88, -8.67) * mm, "end": v(3.91, -8.66) * mm});
            skLineSegment(sketch, "E99.29.43", {"start": v(3.25, -8.07) * mm, "end": v(3.27, -8.1) * mm});
            skLineSegment(sketch, "E99.29.44", {"start": v(3.84, -8.69) * mm, "end": v(3.88, -8.67) * mm});
            skLineSegment(sketch, "E99.29.45", {"start": v(2.7, -8.27) * mm, "end": v(2.7, -8.31) * mm});
            skLineSegment(sketch, "E99.29.46", {"start": v(3.11, -7.9) * mm, "end": v(3.13, -7.91) * mm});
            skLineSegment(sketch, "E99.29.47", {"start": v(3.2, -8) * mm, "end": v(3.22, -8.03) * mm});
            skLineSegment(sketch, "E99.29.48", {"start": v(3.22, -8.03) * mm, "end": v(3.25, -8.07) * mm});
            skLineSegment(sketch, "E99.29.49", {"start": v(2.69, -8.09) * mm, "end": v(2.69, -8.1) * mm});
            skLineSegment(sketch, "E99.29.50", {"start": v(3.14, -7.92) * mm, "end": v(3.15, -7.94) * mm});
            skLineSegment(sketch, "E99.29.51", {"start": v(2.7, -8.04) * mm, "end": v(2.7, -8.05) * mm});
            skLineSegment(sketch, "E99.29.52", {"start": v(2.7, -8.22) * mm, "end": v(2.7, -8.27) * mm});
            skLineSegment(sketch, "E99.29.53", {"start": v(2.69, -8.12) * mm, "end": v(2.69, -8.14) * mm});
            skLineSegment(sketch, "E99.29.54", {"start": v(2.7, -8.16) * mm, "end": v(2.7, -8.18) * mm});
            skLineSegment(sketch, "E99.29.55", {"start": v(3.15, -7.94) * mm, "end": v(3.16, -7.95) * mm});
            skLineSegment(sketch, "E99.29.56", {"start": v(3.18, -7.98) * mm, "end": v(3.2, -8) * mm});
            skLineSegment(sketch, "E99.29.57", {"start": v(2.69, -8.1) * mm, "end": v(2.69, -8.12) * mm});
            skLineSegment(sketch, "E99.29.58", {"start": v(3.1, -7.9) * mm, "end": v(3.11, -7.9) * mm});
            skLineSegment(sketch, "E99.29.59", {"start": v(2.7, -8.18) * mm, "end": v(2.7, -8.22) * mm});
            skLineSegment(sketch, "E99.29.60", {"start": v(3.17, -7.97) * mm, "end": v(3.18, -7.98) * mm});
            skLineSegment(sketch, "E99.29.61", {"start": v(3.13, -7.91) * mm, "end": v(3.14, -7.92) * mm});
            skLineSegment(sketch, "E99.29.62", {"start": v(2.69, -8.14) * mm, "end": v(2.7, -8.16) * mm});
            skLineSegment(sketch, "E99.29.63", {"start": v(3.16, -7.95) * mm, "end": v(3.17, -7.97) * mm});
            skLineSegment(sketch, "E99.29.64", {"start": v(3.09, -7.88) * mm, "end": v(3.1, -7.9) * mm});
            skLineSegment(sketch, "E99.29.65", {"start": v(2.7, -8.02) * mm, "end": v(2.7, -8.04) * mm});
            skLineSegment(sketch, "E99.29.66", {"start": v(2.7, -8.05) * mm, "end": v(2.7, -8.07) * mm});
            skLineSegment(sketch, "E99.29.67", {"start": v(3.07, -7.87) * mm, "end": v(3.09, -7.88) * mm});
            skLineSegment(sketch, "E99.29.68", {"start": v(2.7, -8.07) * mm, "end": v(2.69, -8.09) * mm});
            skLineSegment(sketch, "E99.29.69", {"start": v(2.7, -8) * mm, "end": v(2.7, -8.02) * mm});
            skLineSegment(sketch, "E99.29.70", {"start": v(2.73, -7.96) * mm, "end": v(2.72, -7.98) * mm});
            skLineSegment(sketch, "E99.29.71", {"start": v(2.71, -8) * mm, "end": v(2.7, -8) * mm});
            skLineSegment(sketch, "E99.29.72", {"start": v(2.72, -7.98) * mm, "end": v(2.71, -8) * mm});
            skLineSegment(sketch, "E99.29.73", {"start": v(2.75, -7.94) * mm, "end": v(2.74, -7.95) * mm});
            skLineSegment(sketch, "E99.29.74", {"start": v(3.06, -7.87) * mm, "end": v(3.07, -7.87) * mm});
            skLineSegment(sketch, "E99.29.75", {"start": v(2.74, -7.95) * mm, "end": v(2.73, -7.96) * mm});
            skLineSegment(sketch, "E99.29.76", {"start": v(2.86, -7.87) * mm, "end": v(2.86, -7.87) * mm});
            skLineSegment(sketch, "E99.29.77", {"start": v(2.81, -7.9) * mm, "end": v(2.8, -7.9) * mm});
            skLineSegment(sketch, "E99.29.78", {"start": v(2.84, -7.88) * mm, "end": v(2.81, -7.9) * mm});
            skLineSegment(sketch, "E99.29.79", {"start": v(2.9, -7.86) * mm, "end": v(2.92, -7.85) * mm});
            skLineSegment(sketch, "E99.29.80", {"start": v(3, -7.85) * mm, "end": v(3.01, -7.85) * mm});
            skLineSegment(sketch, "E99.29.81", {"start": v(3.03, -7.86) * mm, "end": v(3.04, -7.86) * mm});
            skLineSegment(sketch, "E99.29.82", {"start": v(2.76, -7.93) * mm, "end": v(2.75, -7.94) * mm});
            skLineSegment(sketch, "E99.29.83", {"start": v(2.94, -7.85) * mm, "end": v(2.96, -7.85) * mm});
            skLineSegment(sketch, "E99.29.84", {"start": v(3.04, -7.86) * mm, "end": v(3.06, -7.87) * mm});
            skLineSegment(sketch, "E99.29.85", {"start": v(2.8, -7.9) * mm, "end": v(2.78, -7.91) * mm});
            skLineSegment(sketch, "E99.29.86", {"start": v(3.01, -7.85) * mm, "end": v(3.03, -7.86) * mm});
            skLineSegment(sketch, "E99.29.87", {"start": v(2.92, -7.85) * mm, "end": v(2.94, -7.85) * mm});
            skLineSegment(sketch, "E99.29.88", {"start": v(2.98, -7.85) * mm, "end": v(3, -7.85) * mm});
            skLineSegment(sketch, "E99.29.89", {"start": v(2.85, -7.87) * mm, "end": v(2.85, -7.88) * mm});
            skLineSegment(sketch, "E99.29.90", {"start": v(2.84, -7.88) * mm, "end": v(2.84, -7.88) * mm});
            skLineSegment(sketch, "E99.29.91", {"start": v(2.78, -7.91) * mm, "end": v(2.76, -7.93) * mm});
            skLineSegment(sketch, "E99.29.92", {"start": v(2.96, -7.85) * mm, "end": v(2.98, -7.85) * mm});
            skLineSegment(sketch, "E99.29.93", {"start": v(2.89, -7.86) * mm, "end": v(2.9, -7.86) * mm});
            skLineSegment(sketch, "E99.29.94", {"start": v(2.88, -7.86) * mm, "end": v(2.89, -7.86) * mm});
            skLineSegment(sketch, "E99.29.95", {"start": v(2.88, -7.87) * mm, "end": v(2.88, -7.86) * mm});
            skLineSegment(sketch, "E99.29.96", {"start": v(2.87, -7.87) * mm, "end": v(2.88, -7.87) * mm});
            skLineSegment(sketch, "E99.29.97", {"start": v(2.86, -7.87) * mm, "end": v(2.87, -7.87) * mm});
            skLineSegment(sketch, "E99.29.98", {"start": v(2.85, -7.88) * mm, "end": v(2.84, -7.88) * mm});
            skLineSegment(sketch, "E99.29.99", {"start": v(2.86, -7.87) * mm, "end": v(2.85, -7.87) * mm});
            skLineSegment(sketch, "E99.30.0", {"start": v(4.18, -8.33) * mm, "end": v(4.18, -8.38) * mm});
            skLineSegment(sketch, "E99.30.1", {"start": v(5.12, -7.79) * mm, "end": v(5.16, -7.81) * mm});
            skLineSegment(sketch, "E99.30.2", {"start": v(4.05, -8.6) * mm, "end": v(4.01, -8.6) * mm});
            skLineSegment(sketch, "E99.30.3", {"start": v(4.08, -8.58) * mm, "end": v(4.05, -8.6) * mm});
            skLineSegment(sketch, "E99.30.4", {"start": v(4.17, -8.14) * mm, "end": v(4.18, -8.18) * mm});
            skLineSegment(sketch, "E99.30.5", {"start": v(4.77, -7.54) * mm, "end": v(4.8, -7.57) * mm});
            skLineSegment(sketch, "E99.30.6", {"start": v(4.16, -8.04) * mm, "end": v(4.17, -8.09) * mm});
            skLineSegment(sketch, "E99.30.7", {"start": v(4.1, -7.72) * mm, "end": v(4.12, -7.76) * mm});
            skLineSegment(sketch, "E99.30.8", {"start": v(4.17, -8.09) * mm, "end": v(4.17, -8.14) * mm});
            skLineSegment(sketch, "E99.30.9", {"start": v(4.13, -7.8) * mm, "end": v(4.14, -7.85) * mm});
            skLineSegment(sketch, "E99.30.10", {"start": v(4.84, -7.6) * mm, "end": v(4.88, -7.63) * mm});
            skLineSegment(sketch, "E99.30.11", {"start": v(4.66, -7.45) * mm, "end": v(4.7, -7.48) * mm});
            skLineSegment(sketch, "E99.30.12", {"start": v(4.92, -7.65) * mm, "end": v(4.96, -7.68) * mm});
            skLineSegment(sketch, "E99.30.13", {"start": v(4.15, -7.95) * mm, "end": v(4.16, -8) * mm});
            skLineSegment(sketch, "E99.30.14", {"start": v(4.18, -8.38) * mm, "end": v(4.19, -8.43) * mm});
            skLineSegment(sketch, "E99.30.15", {"start": v(4.14, -7.9) * mm, "end": v(4.15, -7.95) * mm});
            skLineSegment(sketch, "E99.30.16", {"start": v(4.18, -8.28) * mm, "end": v(4.18, -8.33) * mm});
            skLineSegment(sketch, "E99.30.17", {"start": v(4.16, -8) * mm, "end": v(4.16, -8.04) * mm});
            skLineSegment(sketch, "E99.30.18", {"start": v(5.08, -7.76) * mm, "end": v(5.12, -7.79) * mm});
            skLineSegment(sketch, "E99.30.19", {"start": v(4.19, -8.43) * mm, "end": v(4.19, -8.48) * mm});
            skLineSegment(sketch, "E99.30.20", {"start": v(4.12, -8.56) * mm, "end": v(4.08, -8.58) * mm});
            skLineSegment(sketch, "E99.30.21", {"start": v(4.63, -7.42) * mm, "end": v(4.66, -7.45) * mm});
            skLineSegment(sketch, "E99.30.22", {"start": v(4.73, -7.5) * mm, "end": v(4.77, -7.54) * mm});
            skLineSegment(sketch, "E99.30.23", {"start": v(5, -7.7) * mm, "end": v(5.04, -7.74) * mm});
            skLineSegment(sketch, "E99.30.24", {"start": v(4.18, -8.18) * mm, "end": v(4.18, -8.23) * mm});
            skLineSegment(sketch, "E99.30.25", {"start": v(4.12, -7.76) * mm, "end": v(4.13, -7.8) * mm});
            skLineSegment(sketch, "E99.30.26", {"start": v(4.19, -8.48) * mm, "end": v(4.18, -8.53) * mm});
            skLineSegment(sketch, "E99.30.27", {"start": v(4.15, -8.55) * mm, "end": v(4.12, -8.56) * mm});
            skLineSegment(sketch, "E99.30.28", {"start": v(4.18, -8.23) * mm, "end": v(4.18, -8.28) * mm});
            skLineSegment(sketch, "E99.30.29", {"start": v(4.8, -7.57) * mm, "end": v(4.84, -7.6) * mm});
            skLineSegment(sketch, "E99.30.30", {"start": v(5.04, -7.74) * mm, "end": v(5.08, -7.76) * mm});
            skLineSegment(sketch, "E99.30.31", {"start": v(4.14, -7.85) * mm, "end": v(4.14, -7.9) * mm});
            skLineSegment(sketch, "E99.30.32", {"start": v(4.96, -7.68) * mm, "end": v(5, -7.7) * mm});
            skLineSegment(sketch, "E99.30.33", {"start": v(4.7, -7.48) * mm, "end": v(4.73, -7.5) * mm});
            skLineSegment(sketch, "E99.30.34", {"start": v(5.16, -7.81) * mm, "end": v(5.2, -7.84) * mm});
            skLineSegment(sketch, "E99.30.35", {"start": v(5.42, -7.8) * mm, "end": v(5.45, -7.78) * mm});
            skLineSegment(sketch, "E99.30.36", {"start": v(4.88, -7.63) * mm, "end": v(4.92, -7.65) * mm});
            skLineSegment(sketch, "E99.30.37", {"start": v(5.39, -7.82) * mm, "end": v(5.42, -7.8) * mm});
            skLineSegment(sketch, "E99.30.38", {"start": v(5.2, -7.84) * mm, "end": v(5.25, -7.86) * mm});
            skLineSegment(sketch, "E99.30.39", {"start": v(4.18, -8.53) * mm, "end": v(4.15, -8.55) * mm});
            skLineSegment(sketch, "E99.30.40", {"start": v(5.25, -7.86) * mm, "end": v(5.3, -7.89) * mm});
            skLineSegment(sketch, "E99.30.41", {"start": v(5.36, -7.85) * mm, "end": v(5.39, -7.82) * mm});
            skLineSegment(sketch, "E99.30.42", {"start": v(5.32, -7.87) * mm, "end": v(5.36, -7.85) * mm});
            skLineSegment(sketch, "E99.30.43", {"start": v(4.6, -7.39) * mm, "end": v(4.63, -7.42) * mm});
            skLineSegment(sketch, "E99.30.44", {"start": v(5.3, -7.89) * mm, "end": v(5.32, -7.87) * mm});
            skLineSegment(sketch, "E99.30.45", {"start": v(4.1, -7.67) * mm, "end": v(4.1, -7.72) * mm});
            skLineSegment(sketch, "E99.30.46", {"start": v(4.44, -7.24) * mm, "end": v(4.45, -7.25) * mm});
            skLineSegment(sketch, "E99.30.47", {"start": v(4.53, -7.32) * mm, "end": v(4.57, -7.35) * mm});
            skLineSegment(sketch, "E99.30.48", {"start": v(4.57, -7.35) * mm, "end": v(4.6, -7.39) * mm});
            skLineSegment(sketch, "E99.30.49", {"start": v(4.05, -7.5) * mm, "end": v(4.06, -7.52) * mm});
            skLineSegment(sketch, "E99.30.50", {"start": v(4.47, -7.26) * mm, "end": v(4.48, -7.27) * mm});
            skLineSegment(sketch, "E99.30.51", {"start": v(4.05, -7.45) * mm, "end": v(4.05, -7.46) * mm});
            skLineSegment(sketch, "E99.30.52", {"start": v(4.08, -7.63) * mm, "end": v(4.1, -7.67) * mm});
            skLineSegment(sketch, "E99.30.53", {"start": v(4.06, -7.53) * mm, "end": v(4.06, -7.55) * mm});
            skLineSegment(sketch, "E99.30.54", {"start": v(4.07, -7.57) * mm, "end": v(4.07, -7.59) * mm});
            skLineSegment(sketch, "E99.30.55", {"start": v(4.48, -7.27) * mm, "end": v(4.5, -7.28) * mm});
            skLineSegment(sketch, "E99.30.56", {"start": v(4.52, -7.3) * mm, "end": v(4.53, -7.32) * mm});
            skLineSegment(sketch, "E99.30.57", {"start": v(4.06, -7.52) * mm, "end": v(4.06, -7.53) * mm});
            skLineSegment(sketch, "E99.30.58", {"start": v(4.42, -7.23) * mm, "end": v(4.44, -7.24) * mm});
            skLineSegment(sketch, "E99.30.59", {"start": v(4.07, -7.59) * mm, "end": v(4.08, -7.63) * mm});
            skLineSegment(sketch, "E99.30.60", {"start": v(4.5, -7.3) * mm, "end": v(4.52, -7.3) * mm});
            skLineSegment(sketch, "E99.30.61", {"start": v(4.45, -7.25) * mm, "end": v(4.47, -7.26) * mm});
            skLineSegment(sketch, "E99.30.62", {"start": v(4.06, -7.55) * mm, "end": v(4.07, -7.57) * mm});
            skLineSegment(sketch, "E99.30.63", {"start": v(4.5, -7.28) * mm, "end": v(4.5, -7.3) * mm});
            skLineSegment(sketch, "E99.30.64", {"start": v(4.4, -7.23) * mm, "end": v(4.42, -7.23) * mm});
            skLineSegment(sketch, "E99.30.65", {"start": v(4.05, -7.43) * mm, "end": v(4.05, -7.45) * mm});
            skLineSegment(sketch, "E99.30.66", {"start": v(4.05, -7.46) * mm, "end": v(4.05, -7.48) * mm});
            skLineSegment(sketch, "E99.30.67", {"start": v(4.4, -7.22) * mm, "end": v(4.4, -7.23) * mm});
            skLineSegment(sketch, "E99.30.68", {"start": v(4.05, -7.48) * mm, "end": v(4.05, -7.5) * mm});
            skLineSegment(sketch, "E99.30.69", {"start": v(4.06, -7.42) * mm, "end": v(4.05, -7.43) * mm});
            skLineSegment(sketch, "E99.30.70", {"start": v(4.07, -7.37) * mm, "end": v(4.07, -7.38) * mm});
            skLineSegment(sketch, "E99.30.71", {"start": v(4.06, -7.4) * mm, "end": v(4.06, -7.42) * mm});
            skLineSegment(sketch, "E99.30.72", {"start": v(4.07, -7.38) * mm, "end": v(4.06, -7.4) * mm});
            skLineSegment(sketch, "E99.30.73", {"start": v(4.09, -7.34) * mm, "end": v(4.08, -7.35) * mm});
            skLineSegment(sketch, "E99.30.74", {"start": v(4.38, -7.22) * mm, "end": v(4.4, -7.22) * mm});
            skLineSegment(sketch, "E99.30.75", {"start": v(4.08, -7.35) * mm, "end": v(4.07, -7.37) * mm});
            skLineSegment(sketch, "E99.30.76", {"start": v(4.19, -7.25) * mm, "end": v(4.18, -7.26) * mm});
            skLineSegment(sketch, "E99.30.77", {"start": v(4.14, -7.28) * mm, "end": v(4.12, -7.3) * mm});
            skLineSegment(sketch, "E99.30.78", {"start": v(4.16, -7.27) * mm, "end": v(4.14, -7.28) * mm});
            skLineSegment(sketch, "E99.30.79", {"start": v(4.21, -7.24) * mm, "end": v(4.24, -7.23) * mm});
            skLineSegment(sketch, "E99.30.80", {"start": v(4.31, -7.2) * mm, "end": v(4.33, -7.2) * mm});
            skLineSegment(sketch, "E99.30.81", {"start": v(4.35, -7.21) * mm, "end": v(4.36, -7.21) * mm});
            skLineSegment(sketch, "E99.30.82", {"start": v(4.1, -7.32) * mm, "end": v(4.09, -7.34) * mm});
            skLineSegment(sketch, "E99.30.83", {"start": v(4.26, -7.22) * mm, "end": v(4.28, -7.21) * mm});
            skLineSegment(sketch, "E99.30.84", {"start": v(4.36, -7.21) * mm, "end": v(4.38, -7.22) * mm});
            skLineSegment(sketch, "E99.30.85", {"start": v(4.12, -7.3) * mm, "end": v(4.1, -7.31) * mm});
            skLineSegment(sketch, "E99.30.86", {"start": v(4.33, -7.2) * mm, "end": v(4.35, -7.21) * mm});
            skLineSegment(sketch, "E99.30.87", {"start": v(4.24, -7.23) * mm, "end": v(4.26, -7.22) * mm});
            skLineSegment(sketch, "E99.30.88", {"start": v(4.3, -7.21) * mm, "end": v(4.31, -7.2) * mm});
            skLineSegment(sketch, "E99.30.89", {"start": v(4.18, -7.26) * mm, "end": v(4.17, -7.26) * mm});
            skLineSegment(sketch, "E99.30.90", {"start": v(4.17, -7.26) * mm, "end": v(4.16, -7.27) * mm});
            skLineSegment(sketch, "E99.30.91", {"start": v(4.1, -7.31) * mm, "end": v(4.1, -7.32) * mm});
            skLineSegment(sketch, "E99.30.92", {"start": v(4.28, -7.21) * mm, "end": v(4.3, -7.21) * mm});
            skLineSegment(sketch, "E99.30.93", {"start": v(4.2, -7.24) * mm, "end": v(4.21, -7.24) * mm});
            skLineSegment(sketch, "E99.30.94", {"start": v(4.2, -7.24) * mm, "end": v(4.2, -7.24) * mm});
            skLineSegment(sketch, "E99.30.95", {"start": v(4.2, -7.25) * mm, "end": v(4.2, -7.24) * mm});
            skLineSegment(sketch, "E99.30.96", {"start": v(4.2, -7.25) * mm, "end": v(4.2, -7.25) * mm});
            skLineSegment(sketch, "E99.30.97", {"start": v(4.19, -7.25) * mm, "end": v(4.2, -7.25) * mm});
            skLineSegment(sketch, "E99.30.98", {"start": v(4.17, -7.26) * mm, "end": v(4.17, -7.26) * mm});
            skLineSegment(sketch, "E99.30.99", {"start": v(4.18, -7.26) * mm, "end": v(4.18, -7.26) * mm});
            skLineSegment(sketch, "E99.31.0", {"start": v(5.57, -7.48) * mm, "end": v(5.58, -7.53) * mm});
            skLineSegment(sketch, "E99.31.1", {"start": v(6.4, -6.78) * mm, "end": v(6.44, -6.8) * mm});
            skLineSegment(sketch, "E99.31.2", {"start": v(5.48, -7.76) * mm, "end": v(5.45, -7.78) * mm});
            skLineSegment(sketch, "E99.31.3", {"start": v(5.51, -7.74) * mm, "end": v(5.48, -7.76) * mm});
            skLineSegment(sketch, "E99.31.4", {"start": v(5.52, -7.29) * mm, "end": v(5.53, -7.34) * mm});
            skLineSegment(sketch, "E99.31.5", {"start": v(6, -6.6) * mm, "end": v(6.05, -6.62) * mm});
            skLineSegment(sketch, "E99.31.6", {"start": v(5.5, -7.2) * mm, "end": v(5.5, -7.24) * mm});
            skLineSegment(sketch, "E99.31.7", {"start": v(5.39, -6.89) * mm, "end": v(5.4, -6.93) * mm});
            skLineSegment(sketch, "E99.31.8", {"start": v(5.5, -7.24) * mm, "end": v(5.52, -7.29) * mm});
            skLineSegment(sketch, "E99.31.9", {"start": v(5.42, -6.97) * mm, "end": v(5.44, -7.02) * mm});
            skLineSegment(sketch, "E99.31.10", {"start": v(6.1, -6.64) * mm, "end": v(6.13, -6.66) * mm});
            skLineSegment(sketch, "E99.31.11", {"start": v(5.89, -6.53) * mm, "end": v(5.93, -6.55) * mm});
            skLineSegment(sketch, "E99.31.12", {"start": v(6.18, -6.68) * mm, "end": v(6.22, -6.7) * mm});
            skLineSegment(sketch, "E99.31.13", {"start": v(5.47, -7.1) * mm, "end": v(5.48, -7.15) * mm});
            skLineSegment(sketch, "E99.31.14", {"start": v(5.58, -7.53) * mm, "end": v(5.59, -7.57) * mm});
            skLineSegment(sketch, "E99.31.15", {"start": v(5.45, -7.06) * mm, "end": v(5.47, -7.1) * mm});
            skLineSegment(sketch, "E99.31.16", {"start": v(5.56, -7.43) * mm, "end": v(5.57, -7.48) * mm});
            skLineSegment(sketch, "E99.31.17", {"start": v(5.48, -7.15) * mm, "end": v(5.5, -7.2) * mm});
            skLineSegment(sketch, "E99.31.18", {"start": v(6.35, -6.76) * mm, "end": v(6.4, -6.78) * mm});
            skLineSegment(sketch, "E99.31.19", {"start": v(5.59, -7.57) * mm, "end": v(5.6, -7.62) * mm});
            skLineSegment(sketch, "E99.31.20", {"start": v(5.54, -7.72) * mm, "end": v(5.51, -7.74) * mm});
            skLineSegment(sketch, "E99.31.21", {"start": v(5.85, -6.5) * mm, "end": v(5.89, -6.53) * mm});
            skLineSegment(sketch, "E99.31.22", {"start": v(5.97, -6.57) * mm, "end": v(6, -6.6) * mm});
            skLineSegment(sketch, "E99.31.23", {"start": v(6.26, -6.72) * mm, "end": v(6.3, -6.74) * mm});
            skLineSegment(sketch, "E99.31.24", {"start": v(5.53, -7.34) * mm, "end": v(5.55, -7.38) * mm});
            skLineSegment(sketch, "E99.31.25", {"start": v(5.4, -6.93) * mm, "end": v(5.42, -6.97) * mm});
            skLineSegment(sketch, "E99.31.26", {"start": v(5.6, -7.62) * mm, "end": v(5.6, -7.67) * mm});
            skLineSegment(sketch, "E99.31.27", {"start": v(5.57, -7.7) * mm, "end": v(5.54, -7.72) * mm});
            skLineSegment(sketch, "E99.31.28", {"start": v(5.55, -7.38) * mm, "end": v(5.56, -7.43) * mm});
            skLineSegment(sketch, "E99.31.29", {"start": v(6.05, -6.62) * mm, "end": v(6.1, -6.64) * mm});
            skLineSegment(sketch, "E99.31.30", {"start": v(6.3, -6.74) * mm, "end": v(6.35, -6.76) * mm});
            skLineSegment(sketch, "E99.31.31", {"start": v(5.44, -7.02) * mm, "end": v(5.45, -7.06) * mm});
            skLineSegment(sketch, "E99.31.32", {"start": v(6.22, -6.7) * mm, "end": v(6.26, -6.72) * mm});
            skLineSegment(sketch, "E99.31.33", {"start": v(5.93, -6.55) * mm, "end": v(5.97, -6.57) * mm});
            skLineSegment(sketch, "E99.31.34", {"start": v(6.44, -6.8) * mm, "end": v(6.49, -6.82) * mm});
            skLineSegment(sketch, "E99.31.35", {"start": v(6.7, -6.74) * mm, "end": v(6.72, -6.72) * mm});
            skLineSegment(sketch, "E99.31.36", {"start": v(6.13, -6.66) * mm, "end": v(6.18, -6.68) * mm});
            skLineSegment(sketch, "E99.31.37", {"start": v(6.66, -6.77) * mm, "end": v(6.7, -6.74) * mm});
            skLineSegment(sketch, "E99.31.38", {"start": v(6.49, -6.82) * mm, "end": v(6.54, -6.83) * mm});
            skLineSegment(sketch, "E99.31.39", {"start": v(5.6, -7.67) * mm, "end": v(5.57, -7.7) * mm});
            skLineSegment(sketch, "E99.31.40", {"start": v(6.54, -6.83) * mm, "end": v(6.58, -6.85) * mm});
            skLineSegment(sketch, "E99.31.41", {"start": v(6.64, -6.8) * mm, "end": v(6.66, -6.77) * mm});
            skLineSegment(sketch, "E99.31.42", {"start": v(6.61, -6.82) * mm, "end": v(6.64, -6.8) * mm});
            skLineSegment(sketch, "E99.31.43", {"start": v(5.81, -6.47) * mm, "end": v(5.85, -6.5) * mm});
            skLineSegment(sketch, "E99.31.44", {"start": v(6.58, -6.85) * mm, "end": v(6.61, -6.82) * mm});
            skLineSegment(sketch, "E99.31.45", {"start": v(5.37, -6.85) * mm, "end": v(5.39, -6.89) * mm});
            skLineSegment(sketch, "E99.31.46", {"start": v(5.63, -6.36) * mm, "end": v(5.64, -6.37) * mm});
            skLineSegment(sketch, "E99.31.47", {"start": v(5.74, -6.42) * mm, "end": v(5.77, -6.45) * mm});
            skLineSegment(sketch, "E99.31.48", {"start": v(5.77, -6.45) * mm, "end": v(5.81, -6.47) * mm});
            skLineSegment(sketch, "E99.31.49", {"start": v(5.3, -6.68) * mm, "end": v(5.3, -6.7) * mm});
            skLineSegment(sketch, "E99.31.50", {"start": v(5.66, -6.37) * mm, "end": v(5.68, -6.38) * mm});
            skLineSegment(sketch, "E99.31.51", {"start": v(5.28, -6.63) * mm, "end": v(5.29, -6.65) * mm});
            skLineSegment(sketch, "E99.31.52", {"start": v(5.35, -6.8) * mm, "end": v(5.37, -6.85) * mm});
            skLineSegment(sketch, "E99.31.53", {"start": v(5.3, -6.71) * mm, "end": v(5.31, -6.73) * mm});
            skLineSegment(sketch, "E99.31.54", {"start": v(5.32, -6.75) * mm, "end": v(5.33, -6.76) * mm});
            skLineSegment(sketch, "E99.31.55", {"start": v(5.68, -6.38) * mm, "end": v(5.7, -6.39) * mm});
            skLineSegment(sketch, "E99.31.56", {"start": v(5.72, -6.4) * mm, "end": v(5.74, -6.42) * mm});
            skLineSegment(sketch, "E99.31.57", {"start": v(5.3, -6.7) * mm, "end": v(5.3, -6.71) * mm});
            skLineSegment(sketch, "E99.31.58", {"start": v(5.61, -6.36) * mm, "end": v(5.63, -6.36) * mm});
            skLineSegment(sketch, "E99.31.59", {"start": v(5.33, -6.76) * mm, "end": v(5.35, -6.8) * mm});
            skLineSegment(sketch, "E99.31.60", {"start": v(5.7, -6.4) * mm, "end": v(5.72, -6.4) * mm});
            skLineSegment(sketch, "E99.31.61", {"start": v(5.64, -6.37) * mm, "end": v(5.66, -6.37) * mm});
            skLineSegment(sketch, "E99.31.62", {"start": v(5.31, -6.73) * mm, "end": v(5.32, -6.75) * mm});
            skLineSegment(sketch, "E99.31.63", {"start": v(5.7, -6.39) * mm, "end": v(5.7, -6.4) * mm});
            skLineSegment(sketch, "E99.31.64", {"start": v(5.6, -6.35) * mm, "end": v(5.61, -6.36) * mm});
            skLineSegment(sketch, "E99.31.65", {"start": v(5.28, -6.61) * mm, "end": v(5.28, -6.63) * mm});
            skLineSegment(sketch, "E99.31.66", {"start": v(5.29, -6.65) * mm, "end": v(5.29, -6.66) * mm});
            skLineSegment(sketch, "E99.31.67", {"start": v(5.58, -6.35) * mm, "end": v(5.6, -6.35) * mm});
            skLineSegment(sketch, "E99.31.68", {"start": v(5.29, -6.66) * mm, "end": v(5.3, -6.68) * mm});
            skLineSegment(sketch, "E99.31.69", {"start": v(5.28, -6.6) * mm, "end": v(5.28, -6.61) * mm});
            skLineSegment(sketch, "E99.31.70", {"start": v(5.29, -6.55) * mm, "end": v(5.29, -6.57) * mm});
            skLineSegment(sketch, "E99.31.71", {"start": v(5.28, -6.58) * mm, "end": v(5.28, -6.6) * mm});
            skLineSegment(sketch, "E99.31.72", {"start": v(5.29, -6.57) * mm, "end": v(5.28, -6.58) * mm});
            skLineSegment(sketch, "E99.31.73", {"start": v(5.3, -6.52) * mm, "end": v(5.3, -6.53) * mm});
            skLineSegment(sketch, "E99.31.74", {"start": v(5.56, -6.35) * mm, "end": v(5.58, -6.35) * mm});
            skLineSegment(sketch, "E99.31.75", {"start": v(5.3, -6.53) * mm, "end": v(5.29, -6.55) * mm});
            skLineSegment(sketch, "E99.31.76", {"start": v(5.38, -6.42) * mm, "end": v(5.38, -6.42) * mm});
            skLineSegment(sketch, "E99.31.77", {"start": v(5.34, -6.45) * mm, "end": v(5.33, -6.47) * mm});
            skLineSegment(sketch, "E99.31.78", {"start": v(5.36, -6.43) * mm, "end": v(5.34, -6.45) * mm});
            skLineSegment(sketch, "E99.31.79", {"start": v(5.4, -6.4) * mm, "end": v(5.43, -6.38) * mm});
            skLineSegment(sketch, "E99.31.80", {"start": v(5.5, -6.35) * mm, "end": v(5.52, -6.35) * mm});
            skLineSegment(sketch, "E99.31.81", {"start": v(5.53, -6.35) * mm, "end": v(5.55, -6.35) * mm});
            skLineSegment(sketch, "E99.31.82", {"start": v(5.3, -6.5) * mm, "end": v(5.3, -6.52) * mm});
            skLineSegment(sketch, "E99.31.83", {"start": v(5.45, -6.37) * mm, "end": v(5.46, -6.36) * mm});
            skLineSegment(sketch, "E99.31.84", {"start": v(5.55, -6.35) * mm, "end": v(5.56, -6.35) * mm});
            skLineSegment(sketch, "E99.31.85", {"start": v(5.33, -6.47) * mm, "end": v(5.32, -6.49) * mm});
            skLineSegment(sketch, "E99.31.86", {"start": v(5.52, -6.35) * mm, "end": v(5.53, -6.35) * mm});
            skLineSegment(sketch, "E99.31.87", {"start": v(5.43, -6.38) * mm, "end": v(5.45, -6.37) * mm});
            skLineSegment(sketch, "E99.31.88", {"start": v(5.48, -6.36) * mm, "end": v(5.5, -6.35) * mm});
            skLineSegment(sketch, "E99.31.89", {"start": v(5.37, -6.42) * mm, "end": v(5.37, -6.43) * mm});
            skLineSegment(sketch, "E99.31.90", {"start": v(5.36, -6.43) * mm, "end": v(5.36, -6.43) * mm});
            skLineSegment(sketch, "E99.31.91", {"start": v(5.32, -6.49) * mm, "end": v(5.3, -6.5) * mm});
            skLineSegment(sketch, "E99.31.92", {"start": v(5.46, -6.36) * mm, "end": v(5.48, -6.36) * mm});
            skLineSegment(sketch, "E99.31.93", {"start": v(5.4, -6.4) * mm, "end": v(5.4, -6.4) * mm});
            skLineSegment(sketch, "E99.31.94", {"start": v(5.4, -6.4) * mm, "end": v(5.4, -6.4) * mm});
            skLineSegment(sketch, "E99.31.95", {"start": v(5.4, -6.4) * mm, "end": v(5.4, -6.4) * mm});
            skLineSegment(sketch, "E99.31.96", {"start": v(5.39, -6.41) * mm, "end": v(5.4, -6.4) * mm});
            skLineSegment(sketch, "E99.31.97", {"start": v(5.38, -6.42) * mm, "end": v(5.39, -6.41) * mm});
            skLineSegment(sketch, "E99.31.98", {"start": v(5.37, -6.43) * mm, "end": v(5.36, -6.43) * mm});
            skLineSegment(sketch, "E99.31.99", {"start": v(5.38, -6.42) * mm, "end": v(5.37, -6.42) * mm});
            skLineSegment(sketch, "E99.32.0", {"start": v(6.78, -6.4) * mm, "end": v(6.8, -6.44) * mm});
            skLineSegment(sketch, "E99.32.1", {"start": v(7.48, -5.57) * mm, "end": v(7.53, -5.58) * mm});
            skLineSegment(sketch, "E99.32.2", {"start": v(6.74, -6.7) * mm, "end": v(6.72, -6.72) * mm});
            skLineSegment(sketch, "E99.32.3", {"start": v(6.77, -6.66) * mm, "end": v(6.74, -6.7) * mm});
            skLineSegment(sketch, "E99.32.4", {"start": v(6.7, -6.22) * mm, "end": v(6.72, -6.26) * mm});
            skLineSegment(sketch, "E99.32.5", {"start": v(7.06, -5.45) * mm, "end": v(7.1, -5.47) * mm});
            skLineSegment(sketch, "E99.32.6", {"start": v(6.66, -6.13) * mm, "end": v(6.68, -6.18) * mm});
            skLineSegment(sketch, "E99.32.7", {"start": v(6.5, -5.85) * mm, "end": v(6.53, -5.89) * mm});
            skLineSegment(sketch, "E99.32.8", {"start": v(6.68, -6.18) * mm, "end": v(6.7, -6.22) * mm});
            skLineSegment(sketch, "E99.32.9", {"start": v(6.55, -5.93) * mm, "end": v(6.57, -5.97) * mm});
            skLineSegment(sketch, "E99.32.10", {"start": v(7.15, -5.48) * mm, "end": v(7.2, -5.5) * mm});
            skLineSegment(sketch, "E99.32.11", {"start": v(6.93, -5.4) * mm, "end": v(6.97, -5.42) * mm});
            skLineSegment(sketch, "E99.32.12", {"start": v(7.24, -5.5) * mm, "end": v(7.29, -5.52) * mm});
            skLineSegment(sketch, "E99.32.13", {"start": v(6.62, -6.05) * mm, "end": v(6.64, -6.1) * mm});
            skLineSegment(sketch, "E99.32.14", {"start": v(6.8, -6.44) * mm, "end": v(6.82, -6.49) * mm});
            skLineSegment(sketch, "E99.32.15", {"start": v(6.6, -6) * mm, "end": v(6.62, -6.05) * mm});
            skLineSegment(sketch, "E99.32.16", {"start": v(6.76, -6.35) * mm, "end": v(6.78, -6.4) * mm});
            skLineSegment(sketch, "E99.32.17", {"start": v(6.64, -6.1) * mm, "end": v(6.66, -6.13) * mm});
            skLineSegment(sketch, "E99.32.18", {"start": v(7.43, -5.56) * mm, "end": v(7.48, -5.57) * mm});
            skLineSegment(sketch, "E99.32.19", {"start": v(6.82, -6.49) * mm, "end": v(6.83, -6.54) * mm});
            skLineSegment(sketch, "E99.32.20", {"start": v(6.8, -6.64) * mm, "end": v(6.77, -6.66) * mm});
            skLineSegment(sketch, "E99.32.21", {"start": v(6.89, -5.39) * mm, "end": v(6.93, -5.4) * mm});
            skLineSegment(sketch, "E99.32.22", {"start": v(7.02, -5.44) * mm, "end": v(7.06, -5.45) * mm});
            skLineSegment(sketch, "E99.32.23", {"start": v(7.34, -5.53) * mm, "end": v(7.38, -5.55) * mm});
            skLineSegment(sketch, "E99.32.24", {"start": v(6.72, -6.26) * mm, "end": v(6.74, -6.3) * mm});
            skLineSegment(sketch, "E99.32.25", {"start": v(6.53, -5.89) * mm, "end": v(6.55, -5.93) * mm});
            skLineSegment(sketch, "E99.32.26", {"start": v(6.83, -6.54) * mm, "end": v(6.85, -6.58) * mm});
            skLineSegment(sketch, "E99.32.27", {"start": v(6.82, -6.61) * mm, "end": v(6.8, -6.64) * mm});
            skLineSegment(sketch, "E99.32.28", {"start": v(6.74, -6.3) * mm, "end": v(6.76, -6.35) * mm});
            skLineSegment(sketch, "E99.32.29", {"start": v(7.1, -5.47) * mm, "end": v(7.15, -5.48) * mm});
            skLineSegment(sketch, "E99.32.30", {"start": v(7.38, -5.55) * mm, "end": v(7.43, -5.56) * mm});
            skLineSegment(sketch, "E99.32.31", {"start": v(6.57, -5.97) * mm, "end": v(6.6, -6) * mm});
            skLineSegment(sketch, "E99.32.32", {"start": v(7.29, -5.52) * mm, "end": v(7.34, -5.53) * mm});
            skLineSegment(sketch, "E99.32.33", {"start": v(6.97, -5.42) * mm, "end": v(7.02, -5.44) * mm});
            skLineSegment(sketch, "E99.32.34", {"start": v(7.53, -5.58) * mm, "end": v(7.57, -5.59) * mm});
            skLineSegment(sketch, "E99.32.35", {"start": v(7.76, -5.48) * mm, "end": v(7.78, -5.45) * mm});
            skLineSegment(sketch, "E99.32.36", {"start": v(7.2, -5.5) * mm, "end": v(7.24, -5.5) * mm});
            skLineSegment(sketch, "E99.32.37", {"start": v(7.74, -5.51) * mm, "end": v(7.76, -5.48) * mm});
            skLineSegment(sketch, "E99.32.38", {"start": v(7.57, -5.59) * mm, "end": v(7.62, -5.6) * mm});
            skLineSegment(sketch, "E99.32.39", {"start": v(6.85, -6.58) * mm, "end": v(6.82, -6.61) * mm});
            skLineSegment(sketch, "E99.32.40", {"start": v(7.62, -5.6) * mm, "end": v(7.67, -5.6) * mm});
            skLineSegment(sketch, "E99.32.41", {"start": v(7.72, -5.54) * mm, "end": v(7.74, -5.51) * mm});
            skLineSegment(sketch, "E99.32.42", {"start": v(7.7, -5.57) * mm, "end": v(7.72, -5.54) * mm});
            skLineSegment(sketch, "E99.32.43", {"start": v(6.85, -5.37) * mm, "end": v(6.89, -5.39) * mm});
            skLineSegment(sketch, "E99.32.44", {"start": v(7.67, -5.6) * mm, "end": v(7.7, -5.57) * mm});
            skLineSegment(sketch, "E99.32.45", {"start": v(6.47, -5.81) * mm, "end": v(6.5, -5.85) * mm});
            skLineSegment(sketch, "E99.32.46", {"start": v(6.65, -5.29) * mm, "end": v(6.66, -5.29) * mm});
            skLineSegment(sketch, "E99.32.47", {"start": v(6.76, -5.33) * mm, "end": v(6.8, -5.35) * mm});
            skLineSegment(sketch, "E99.32.48", {"start": v(6.8, -5.35) * mm, "end": v(6.85, -5.37) * mm});
            skLineSegment(sketch, "E99.32.49", {"start": v(6.37, -5.66) * mm, "end": v(6.38, -5.68) * mm});
            skLineSegment(sketch, "E99.32.50", {"start": v(6.68, -5.3) * mm, "end": v(6.7, -5.3) * mm});
            skLineSegment(sketch, "E99.32.51", {"start": v(6.36, -5.61) * mm, "end": v(6.36, -5.63) * mm});
            skLineSegment(sketch, "E99.32.52", {"start": v(6.45, -5.77) * mm, "end": v(6.47, -5.81) * mm});
            skLineSegment(sketch, "E99.32.53", {"start": v(6.39, -5.7) * mm, "end": v(6.4, -5.7) * mm});
            skLineSegment(sketch, "E99.32.54", {"start": v(6.4, -5.72) * mm, "end": v(6.42, -5.74) * mm});
            skLineSegment(sketch, "E99.32.55", {"start": v(6.7, -5.3) * mm, "end": v(6.71, -5.3) * mm});
            skLineSegment(sketch, "E99.32.56", {"start": v(6.75, -5.32) * mm, "end": v(6.76, -5.33) * mm});
            skLineSegment(sketch, "E99.32.57", {"start": v(6.38, -5.68) * mm, "end": v(6.39, -5.7) * mm});
            skLineSegment(sketch, "E99.32.58", {"start": v(6.63, -5.28) * mm, "end": v(6.65, -5.29) * mm});
            skLineSegment(sketch, "E99.32.59", {"start": v(6.42, -5.74) * mm, "end": v(6.45, -5.77) * mm});
            skLineSegment(sketch, "E99.32.60", {"start": v(6.73, -5.31) * mm, "end": v(6.75, -5.32) * mm});
            skLineSegment(sketch, "E99.32.61", {"start": v(6.66, -5.29) * mm, "end": v(6.68, -5.3) * mm});
            skLineSegment(sketch, "E99.32.62", {"start": v(6.4, -5.7) * mm, "end": v(6.4, -5.72) * mm});
            skLineSegment(sketch, "E99.32.63", {"start": v(6.71, -5.3) * mm, "end": v(6.73, -5.31) * mm});
            skLineSegment(sketch, "E99.32.64", {"start": v(6.61, -5.28) * mm, "end": v(6.63, -5.28) * mm});
            skLineSegment(sketch, "E99.32.65", {"start": v(6.35, -5.6) * mm, "end": v(6.36, -5.61) * mm});
            skLineSegment(sketch, "E99.32.66", {"start": v(6.36, -5.63) * mm, "end": v(6.37, -5.64) * mm});
            skLineSegment(sketch, "E99.32.67", {"start": v(6.6, -5.28) * mm, "end": v(6.61, -5.28) * mm});
            skLineSegment(sketch, "E99.32.68", {"start": v(6.37, -5.64) * mm, "end": v(6.37, -5.66) * mm});
            skLineSegment(sketch, "E99.32.69", {"start": v(6.35, -5.58) * mm, "end": v(6.35, -5.6) * mm});
            skLineSegment(sketch, "E99.32.70", {"start": v(6.35, -5.53) * mm, "end": v(6.35, -5.55) * mm});
            skLineSegment(sketch, "E99.32.71", {"start": v(6.35, -5.56) * mm, "end": v(6.35, -5.58) * mm});
            skLineSegment(sketch, "E99.32.72", {"start": v(6.35, -5.55) * mm, "end": v(6.35, -5.56) * mm});
            skLineSegment(sketch, "E99.32.73", {"start": v(6.35, -5.5) * mm, "end": v(6.35, -5.52) * mm});
            skLineSegment(sketch, "E99.32.74", {"start": v(6.58, -5.28) * mm, "end": v(6.6, -5.28) * mm});
            skLineSegment(sketch, "E99.32.75", {"start": v(6.35, -5.52) * mm, "end": v(6.35, -5.53) * mm});
            skLineSegment(sketch, "E99.32.76", {"start": v(6.42, -5.38) * mm, "end": v(6.41, -5.39) * mm});
            skLineSegment(sketch, "E99.32.77", {"start": v(6.38, -5.43) * mm, "end": v(6.37, -5.45) * mm});
            skLineSegment(sketch, "E99.32.78", {"start": v(6.4, -5.4) * mm, "end": v(6.38, -5.43) * mm});
            skLineSegment(sketch, "E99.32.79", {"start": v(6.43, -5.36) * mm, "end": v(6.45, -5.34) * mm});
            skLineSegment(sketch, "E99.32.80", {"start": v(6.52, -5.3) * mm, "end": v(6.53, -5.3) * mm});
            skLineSegment(sketch, "E99.32.81", {"start": v(6.55, -5.29) * mm, "end": v(6.57, -5.29) * mm});
            skLineSegment(sketch, "E99.32.82", {"start": v(6.36, -5.48) * mm, "end": v(6.35, -5.5) * mm});
            skLineSegment(sketch, "E99.32.83", {"start": v(6.47, -5.33) * mm, "end": v(6.49, -5.32) * mm});
            skLineSegment(sketch, "E99.32.84", {"start": v(6.57, -5.29) * mm, "end": v(6.58, -5.28) * mm});
            skLineSegment(sketch, "E99.32.85", {"start": v(6.37, -5.45) * mm, "end": v(6.36, -5.46) * mm});
            skLineSegment(sketch, "E99.32.86", {"start": v(6.53, -5.3) * mm, "end": v(6.55, -5.29) * mm});
            skLineSegment(sketch, "E99.32.87", {"start": v(6.45, -5.34) * mm, "end": v(6.47, -5.33) * mm});
            skLineSegment(sketch, "E99.32.88", {"start": v(6.5, -5.3) * mm, "end": v(6.52, -5.3) * mm});
            skLineSegment(sketch, "E99.32.89", {"start": v(6.4, -5.4) * mm, "end": v(6.4, -5.4) * mm});
            skLineSegment(sketch, "E99.32.90", {"start": v(6.4, -5.4) * mm, "end": v(6.4, -5.4) * mm});
            skLineSegment(sketch, "E99.32.91", {"start": v(6.36, -5.46) * mm, "end": v(6.36, -5.48) * mm});
            skLineSegment(sketch, "E99.32.92", {"start": v(6.49, -5.32) * mm, "end": v(6.5, -5.3) * mm});
            skLineSegment(sketch, "E99.32.93", {"start": v(6.43, -5.36) * mm, "end": v(6.43, -5.36) * mm});
            skLineSegment(sketch, "E99.32.94", {"start": v(6.43, -5.37) * mm, "end": v(6.43, -5.36) * mm});
            skLineSegment(sketch, "E99.32.95", {"start": v(6.42, -5.37) * mm, "end": v(6.43, -5.37) * mm});
            skLineSegment(sketch, "E99.32.96", {"start": v(6.42, -5.38) * mm, "end": v(6.42, -5.37) * mm});
            skLineSegment(sketch, "E99.32.97", {"start": v(6.42, -5.38) * mm, "end": v(6.42, -5.38) * mm});
            skLineSegment(sketch, "E99.32.98", {"start": v(6.4, -5.4) * mm, "end": v(6.4, -5.4) * mm});
            skLineSegment(sketch, "E99.32.99", {"start": v(6.41, -5.39) * mm, "end": v(6.4, -5.4) * mm});
            skLineSegment(sketch, "E99.33.0", {"start": v(7.79, -5.12) * mm, "end": v(7.81, -5.16) * mm});
            skLineSegment(sketch, "E99.33.1", {"start": v(8.33, -4.18) * mm, "end": v(8.38, -4.18) * mm});
            skLineSegment(sketch, "E99.33.2", {"start": v(7.8, -5.42) * mm, "end": v(7.78, -5.45) * mm});
            skLineSegment(sketch, "E99.33.3", {"start": v(7.82, -5.39) * mm, "end": v(7.8, -5.42) * mm});
            skLineSegment(sketch, "E99.33.4", {"start": v(7.68, -4.96) * mm, "end": v(7.7, -5) * mm});
            skLineSegment(sketch, "E99.33.5", {"start": v(7.9, -4.14) * mm, "end": v(7.95, -4.15) * mm});
            skLineSegment(sketch, "E99.33.6", {"start": v(7.63, -4.88) * mm, "end": v(7.65, -4.92) * mm});
            skLineSegment(sketch, "E99.33.7", {"start": v(7.42, -4.63) * mm, "end": v(7.45, -4.66) * mm});
            skLineSegment(sketch, "E99.33.8", {"start": v(7.65, -4.92) * mm, "end": v(7.68, -4.96) * mm});
            skLineSegment(sketch, "E99.33.9", {"start": v(7.48, -4.7) * mm, "end": v(7.5, -4.73) * mm});
            skLineSegment(sketch, "E99.33.10", {"start": v(8, -4.16) * mm, "end": v(8.04, -4.16) * mm});
            skLineSegment(sketch, "E99.33.11", {"start": v(7.76, -4.12) * mm, "end": v(7.8, -4.13) * mm});
            skLineSegment(sketch, "E99.33.12", {"start": v(8.09, -4.17) * mm, "end": v(8.14, -4.17) * mm});
            skLineSegment(sketch, "E99.33.13", {"start": v(7.57, -4.8) * mm, "end": v(7.6, -4.84) * mm});
            skLineSegment(sketch, "E99.33.14", {"start": v(7.81, -5.16) * mm, "end": v(7.84, -5.2) * mm});
            skLineSegment(sketch, "E99.33.15", {"start": v(7.54, -4.77) * mm, "end": v(7.57, -4.8) * mm});
            skLineSegment(sketch, "E99.33.16", {"start": v(7.76, -5.08) * mm, "end": v(7.79, -5.12) * mm});
            skLineSegment(sketch, "E99.33.17", {"start": v(7.6, -4.84) * mm, "end": v(7.63, -4.88) * mm});
            skLineSegment(sketch, "E99.33.18", {"start": v(8.28, -4.18) * mm, "end": v(8.33, -4.18) * mm});
            skLineSegment(sketch, "E99.33.19", {"start": v(7.84, -5.2) * mm, "end": v(7.86, -5.25) * mm});
            skLineSegment(sketch, "E99.33.20", {"start": v(7.85, -5.36) * mm, "end": v(7.82, -5.39) * mm});
            skLineSegment(sketch, "E99.33.21", {"start": v(7.72, -4.1) * mm, "end": v(7.76, -4.12) * mm});
            skLineSegment(sketch, "E99.33.22", {"start": v(7.85, -4.14) * mm, "end": v(7.9, -4.14) * mm});
            skLineSegment(sketch, "E99.33.23", {"start": v(8.18, -4.18) * mm, "end": v(8.23, -4.18) * mm});
            skLineSegment(sketch, "E99.33.24", {"start": v(7.7, -5) * mm, "end": v(7.74, -5.04) * mm});
            skLineSegment(sketch, "E99.33.25", {"start": v(7.45, -4.66) * mm, "end": v(7.48, -4.7) * mm});
            skLineSegment(sketch, "E99.33.26", {"start": v(7.86, -5.25) * mm, "end": v(7.89, -5.3) * mm});
            skLineSegment(sketch, "E99.33.27", {"start": v(7.87, -5.32) * mm, "end": v(7.85, -5.36) * mm});
            skLineSegment(sketch, "E99.33.28", {"start": v(7.74, -5.04) * mm, "end": v(7.76, -5.08) * mm});
            skLineSegment(sketch, "E99.33.29", {"start": v(7.95, -4.15) * mm, "end": v(8, -4.16) * mm});
            skLineSegment(sketch, "E99.33.30", {"start": v(8.23, -4.18) * mm, "end": v(8.28, -4.18) * mm});
            skLineSegment(sketch, "E99.33.31", {"start": v(7.5, -4.73) * mm, "end": v(7.54, -4.77) * mm});
            skLineSegment(sketch, "E99.33.32", {"start": v(8.14, -4.17) * mm, "end": v(8.18, -4.18) * mm});
            skLineSegment(sketch, "E99.33.33", {"start": v(7.8, -4.13) * mm, "end": v(7.85, -4.14) * mm});
            skLineSegment(sketch, "E99.33.34", {"start": v(8.38, -4.18) * mm, "end": v(8.43, -4.19) * mm});
            skLineSegment(sketch, "E99.33.35", {"start": v(8.6, -4.05) * mm, "end": v(8.6, -4.01) * mm});
            skLineSegment(sketch, "E99.33.36", {"start": v(8.04, -4.16) * mm, "end": v(8.09, -4.17) * mm});
            skLineSegment(sketch, "E99.33.37", {"start": v(8.58, -4.08) * mm, "end": v(8.6, -4.05) * mm});
            skLineSegment(sketch, "E99.33.38", {"start": v(8.43, -4.19) * mm, "end": v(8.48, -4.19) * mm});
            skLineSegment(sketch, "E99.33.39", {"start": v(7.89, -5.3) * mm, "end": v(7.87, -5.32) * mm});
            skLineSegment(sketch, "E99.33.40", {"start": v(8.48, -4.19) * mm, "end": v(8.53, -4.18) * mm});
            skLineSegment(sketch, "E99.33.41", {"start": v(8.56, -4.12) * mm, "end": v(8.58, -4.08) * mm});
            skLineSegment(sketch, "E99.33.42", {"start": v(8.55, -4.15) * mm, "end": v(8.56, -4.12) * mm});
            skLineSegment(sketch, "E99.33.43", {"start": v(7.67, -4.1) * mm, "end": v(7.72, -4.1) * mm});
            skLineSegment(sketch, "E99.33.44", {"start": v(8.53, -4.18) * mm, "end": v(8.55, -4.15) * mm});
            skLineSegment(sketch, "E99.33.45", {"start": v(7.39, -4.6) * mm, "end": v(7.42, -4.63) * mm});
            skLineSegment(sketch, "E99.33.46", {"start": v(7.46, -4.05) * mm, "end": v(7.48, -4.05) * mm});
            skLineSegment(sketch, "E99.33.47", {"start": v(7.59, -4.07) * mm, "end": v(7.63, -4.08) * mm});
            skLineSegment(sketch, "E99.33.48", {"start": v(7.63, -4.08) * mm, "end": v(7.67, -4.1) * mm});
            skLineSegment(sketch, "E99.33.49", {"start": v(7.26, -4.47) * mm, "end": v(7.27, -4.48) * mm});
            skLineSegment(sketch, "E99.33.50", {"start": v(7.5, -4.05) * mm, "end": v(7.52, -4.06) * mm});
            skLineSegment(sketch, "E99.33.51", {"start": v(7.23, -4.42) * mm, "end": v(7.24, -4.44) * mm});
            skLineSegment(sketch, "E99.33.52", {"start": v(7.35, -4.57) * mm, "end": v(7.39, -4.6) * mm});
            skLineSegment(sketch, "E99.33.53", {"start": v(7.28, -4.5) * mm, "end": v(7.3, -4.5) * mm});
            skLineSegment(sketch, "E99.33.54", {"start": v(7.3, -4.52) * mm, "end": v(7.32, -4.53) * mm});
            skLineSegment(sketch, "E99.33.55", {"start": v(7.52, -4.06) * mm, "end": v(7.53, -4.06) * mm});
            skLineSegment(sketch, "E99.33.56", {"start": v(7.57, -4.07) * mm, "end": v(7.59, -4.07) * mm});
            skLineSegment(sketch, "E99.33.57", {"start": v(7.27, -4.48) * mm, "end": v(7.28, -4.5) * mm});
            skLineSegment(sketch, "E99.33.58", {"start": v(7.45, -4.05) * mm, "end": v(7.46, -4.05) * mm});
            skLineSegment(sketch, "E99.33.59", {"start": v(7.32, -4.53) * mm, "end": v(7.35, -4.57) * mm});
            skLineSegment(sketch, "E99.33.60", {"start": v(7.55, -4.06) * mm, "end": v(7.57, -4.07) * mm});
            skLineSegment(sketch, "E99.33.61", {"start": v(7.48, -4.05) * mm, "end": v(7.5, -4.05) * mm});
            skLineSegment(sketch, "E99.33.62", {"start": v(7.3, -4.5) * mm, "end": v(7.3, -4.52) * mm});
            skLineSegment(sketch, "E99.33.63", {"start": v(7.53, -4.06) * mm, "end": v(7.55, -4.06) * mm});
            skLineSegment(sketch, "E99.33.64", {"start": v(7.43, -4.05) * mm, "end": v(7.45, -4.05) * mm});
            skLineSegment(sketch, "E99.33.65", {"start": v(7.23, -4.4) * mm, "end": v(7.23, -4.42) * mm});
            skLineSegment(sketch, "E99.33.66", {"start": v(7.24, -4.44) * mm, "end": v(7.25, -4.45) * mm});
            skLineSegment(sketch, "E99.33.67", {"start": v(7.42, -4.06) * mm, "end": v(7.43, -4.05) * mm});
            skLineSegment(sketch, "E99.33.68", {"start": v(7.25, -4.45) * mm, "end": v(7.26, -4.47) * mm});
            skLineSegment(sketch, "E99.33.69", {"start": v(7.22, -4.4) * mm, "end": v(7.23, -4.4) * mm});
            skLineSegment(sketch, "E99.33.70", {"start": v(7.21, -4.35) * mm, "end": v(7.21, -4.36) * mm});
            skLineSegment(sketch, "E99.33.71", {"start": v(7.22, -4.38) * mm, "end": v(7.22, -4.4) * mm});
            skLineSegment(sketch, "E99.33.72", {"start": v(7.21, -4.36) * mm, "end": v(7.22, -4.38) * mm});
            skLineSegment(sketch, "E99.33.73", {"start": v(7.2, -4.31) * mm, "end": v(7.2, -4.33) * mm});
            skLineSegment(sketch, "E99.33.74", {"start": v(7.4, -4.06) * mm, "end": v(7.42, -4.06) * mm});
            skLineSegment(sketch, "E99.33.75", {"start": v(7.2, -4.33) * mm, "end": v(7.21, -4.35) * mm});
            skLineSegment(sketch, "E99.33.76", {"start": v(7.25, -4.19) * mm, "end": v(7.25, -4.2) * mm});
            skLineSegment(sketch, "E99.33.77", {"start": v(7.23, -4.24) * mm, "end": v(7.22, -4.26) * mm});
            skLineSegment(sketch, "E99.33.78", {"start": v(7.24, -4.21) * mm, "end": v(7.23, -4.24) * mm});
            skLineSegment(sketch, "E99.33.79", {"start": v(7.27, -4.16) * mm, "end": v(7.28, -4.14) * mm});
            skLineSegment(sketch, "E99.33.80", {"start": v(7.34, -4.09) * mm, "end": v(7.35, -4.08) * mm});
            skLineSegment(sketch, "E99.33.81", {"start": v(7.37, -4.07) * mm, "end": v(7.38, -4.07) * mm});
            skLineSegment(sketch, "E99.33.82", {"start": v(7.21, -4.3) * mm, "end": v(7.2, -4.31) * mm});
            skLineSegment(sketch, "E99.33.83", {"start": v(7.3, -4.12) * mm, "end": v(7.31, -4.1) * mm});
            skLineSegment(sketch, "E99.33.84", {"start": v(7.38, -4.07) * mm, "end": v(7.4, -4.06) * mm});
            skLineSegment(sketch, "E99.33.85", {"start": v(7.22, -4.26) * mm, "end": v(7.21, -4.28) * mm});
            skLineSegment(sketch, "E99.33.86", {"start": v(7.35, -4.08) * mm, "end": v(7.37, -4.07) * mm});
            skLineSegment(sketch, "E99.33.87", {"start": v(7.28, -4.14) * mm, "end": v(7.3, -4.12) * mm});
            skLineSegment(sketch, "E99.33.88", {"start": v(7.32, -4.1) * mm, "end": v(7.34, -4.09) * mm});
            skLineSegment(sketch, "E99.33.89", {"start": v(7.25, -4.2) * mm, "end": v(7.24, -4.2) * mm});
            skLineSegment(sketch, "E99.33.90", {"start": v(7.24, -4.2) * mm, "end": v(7.24, -4.21) * mm});
            skLineSegment(sketch, "E99.33.91", {"start": v(7.21, -4.28) * mm, "end": v(7.21, -4.3) * mm});
            skLineSegment(sketch, "E99.33.92", {"start": v(7.31, -4.1) * mm, "end": v(7.32, -4.1) * mm});
            skLineSegment(sketch, "E99.33.93", {"start": v(7.26, -4.17) * mm, "end": v(7.27, -4.16) * mm});
            skLineSegment(sketch, "E99.33.94", {"start": v(7.26, -4.17) * mm, "end": v(7.26, -4.17) * mm});
            skLineSegment(sketch, "E99.33.95", {"start": v(7.26, -4.18) * mm, "end": v(7.26, -4.17) * mm});
            skLineSegment(sketch, "E99.33.96", {"start": v(7.26, -4.18) * mm, "end": v(7.26, -4.18) * mm});
            skLineSegment(sketch, "E99.33.97", {"start": v(7.25, -4.19) * mm, "end": v(7.26, -4.18) * mm});
            skLineSegment(sketch, "E99.33.98", {"start": v(7.24, -4.2) * mm, "end": v(7.24, -4.2) * mm});
            skLineSegment(sketch, "E99.33.99", {"start": v(7.25, -4.2) * mm, "end": v(7.25, -4.2) * mm});
            skLineSegment(sketch, "E99.34.0", {"start": v(8.56, -3.7) * mm, "end": v(8.6, -3.73) * mm});
            skLineSegment(sketch, "E99.34.1", {"start": v(8.93, -2.67) * mm, "end": v(8.98, -2.67) * mm});
            skLineSegment(sketch, "E99.34.2", {"start": v(8.63, -3.98) * mm, "end": v(8.6, -4.01) * mm});
            skLineSegment(sketch, "E99.34.3", {"start": v(8.64, -3.95) * mm, "end": v(8.63, -3.98) * mm});
            skLineSegment(sketch, "E99.34.4", {"start": v(8.43, -3.55) * mm, "end": v(8.46, -3.59) * mm});
            skLineSegment(sketch, "E99.34.5", {"start": v(8.5, -2.7) * mm, "end": v(8.55, -2.7) * mm});
            skLineSegment(sketch, "E99.34.6", {"start": v(8.36, -3.48) * mm, "end": v(8.4, -3.52) * mm});
            skLineSegment(sketch, "E99.34.7", {"start": v(8.1, -3.27) * mm, "end": v(8.15, -3.3) * mm});
            skLineSegment(sketch, "E99.34.8", {"start": v(8.4, -3.52) * mm, "end": v(8.43, -3.55) * mm});
            skLineSegment(sketch, "E99.34.9", {"start": v(8.18, -3.33) * mm, "end": v(8.22, -3.36) * mm});
            skLineSegment(sketch, "E99.34.10", {"start": v(8.6, -2.7) * mm, "end": v(8.64, -2.7) * mm});
            skLineSegment(sketch, "E99.34.11", {"start": v(8.36, -2.7) * mm, "end": v(8.4, -2.7) * mm});
            skLineSegment(sketch, "E99.34.12", {"start": v(8.69, -2.7) * mm, "end": v(8.74, -2.7) * mm});
            skLineSegment(sketch, "E99.34.13", {"start": v(8.29, -3.42) * mm, "end": v(8.32, -3.45) * mm});
            skLineSegment(sketch, "E99.34.14", {"start": v(8.6, -3.73) * mm, "end": v(8.62, -3.77) * mm});
            skLineSegment(sketch, "E99.34.15", {"start": v(8.25, -3.39) * mm, "end": v(8.29, -3.42) * mm});
            skLineSegment(sketch, "E99.34.16", {"start": v(8.53, -3.66) * mm, "end": v(8.56, -3.7) * mm});
            skLineSegment(sketch, "E99.34.17", {"start": v(8.32, -3.45) * mm, "end": v(8.36, -3.48) * mm});
            skLineSegment(sketch, "E99.34.18", {"start": v(8.88, -2.68) * mm, "end": v(8.93, -2.67) * mm});
            skLineSegment(sketch, "E99.34.19", {"start": v(8.62, -3.77) * mm, "end": v(8.66, -3.8) * mm});
            skLineSegment(sketch, "E99.34.20", {"start": v(8.66, -3.91) * mm, "end": v(8.64, -3.95) * mm});
            skLineSegment(sketch, "E99.34.21", {"start": v(8.31, -2.7) * mm, "end": v(8.36, -2.7) * mm});
            skLineSegment(sketch, "E99.34.22", {"start": v(8.45, -2.7) * mm, "end": v(8.5, -2.7) * mm});
            skLineSegment(sketch, "E99.34.23", {"start": v(8.79, -2.7) * mm, "end": v(8.83, -2.69) * mm});
            skLineSegment(sketch, "E99.34.24", {"start": v(8.46, -3.59) * mm, "end": v(8.5, -3.62) * mm});
            skLineSegment(sketch, "E99.34.25", {"start": v(8.15, -3.3) * mm, "end": v(8.18, -3.33) * mm});
            skLineSegment(sketch, "E99.34.26", {"start": v(8.66, -3.8) * mm, "end": v(8.69, -3.84) * mm});
            skLineSegment(sketch, "E99.34.27", {"start": v(8.67, -3.88) * mm, "end": v(8.66, -3.91) * mm});
            skLineSegment(sketch, "E99.34.28", {"start": v(8.5, -3.62) * mm, "end": v(8.53, -3.66) * mm});
            skLineSegment(sketch, "E99.34.29", {"start": v(8.55, -2.7) * mm, "end": v(8.6, -2.7) * mm});
            skLineSegment(sketch, "E99.34.30", {"start": v(8.83, -2.69) * mm, "end": v(8.88, -2.68) * mm});
            skLineSegment(sketch, "E99.34.31", {"start": v(8.22, -3.36) * mm, "end": v(8.25, -3.39) * mm});
            skLineSegment(sketch, "E99.34.32", {"start": v(8.74, -2.7) * mm, "end": v(8.79, -2.7) * mm});
            skLineSegment(sketch, "E99.34.33", {"start": v(8.4, -2.7) * mm, "end": v(8.45, -2.7) * mm});
            skLineSegment(sketch, "E99.34.34", {"start": v(8.98, -2.67) * mm, "end": v(9.03, -2.66) * mm});
            skLineSegment(sketch, "E99.34.35", {"start": v(9.17, -2.5) * mm, "end": v(9.18, -2.46) * mm});
            skLineSegment(sketch, "E99.34.36", {"start": v(8.64, -2.7) * mm, "end": v(8.69, -2.7) * mm});
            skLineSegment(sketch, "E99.34.37", {"start": v(9.16, -2.53) * mm, "end": v(9.17, -2.5) * mm});
            skLineSegment(sketch, "E99.34.38", {"start": v(9.03, -2.66) * mm, "end": v(9.08, -2.65) * mm});
            skLineSegment(sketch, "E99.34.39", {"start": v(8.69, -3.84) * mm, "end": v(8.67, -3.88) * mm});
            skLineSegment(sketch, "E99.34.40", {"start": v(9.08, -2.65) * mm, "end": v(9.13, -2.64) * mm});
            skLineSegment(sketch, "E99.34.41", {"start": v(9.15, -2.57) * mm, "end": v(9.16, -2.53) * mm});
            skLineSegment(sketch, "E99.34.42", {"start": v(9.14, -2.6) * mm, "end": v(9.15, -2.57) * mm});
            skLineSegment(sketch, "E99.34.43", {"start": v(8.27, -2.7) * mm, "end": v(8.31, -2.7) * mm});
            skLineSegment(sketch, "E99.34.44", {"start": v(9.13, -2.64) * mm, "end": v(9.14, -2.6) * mm});
            skLineSegment(sketch, "E99.34.45", {"start": v(8.07, -3.25) * mm, "end": v(8.1, -3.27) * mm});
            skLineSegment(sketch, "E99.34.46", {"start": v(8.05, -2.7) * mm, "end": v(8.07, -2.7) * mm});
            skLineSegment(sketch, "E99.34.47", {"start": v(8.18, -2.7) * mm, "end": v(8.22, -2.7) * mm});
            skLineSegment(sketch, "E99.34.48", {"start": v(8.22, -2.7) * mm, "end": v(8.27, -2.7) * mm});
            skLineSegment(sketch, "E99.34.49", {"start": v(7.92, -3.14) * mm, "end": v(7.94, -3.15) * mm});
            skLineSegment(sketch, "E99.34.50", {"start": v(8.09, -2.69) * mm, "end": v(8.1, -2.69) * mm});
            skLineSegment(sketch, "E99.34.51", {"start": v(7.9, -3.1) * mm, "end": v(7.9, -3.11) * mm});
            skLineSegment(sketch, "E99.34.52", {"start": v(8.03, -3.22) * mm, "end": v(8.07, -3.25) * mm});
            skLineSegment(sketch, "E99.34.53", {"start": v(7.95, -3.16) * mm, "end": v(7.97, -3.17) * mm});
            skLineSegment(sketch, "E99.34.54", {"start": v(7.98, -3.18) * mm, "end": v(8, -3.2) * mm});
            skLineSegment(sketch, "E99.34.55", {"start": v(8.1, -2.69) * mm, "end": v(8.12, -2.69) * mm});
            skLineSegment(sketch, "E99.34.56", {"start": v(8.16, -2.7) * mm, "end": v(8.18, -2.7) * mm});
            skLineSegment(sketch, "E99.34.57", {"start": v(7.94, -3.15) * mm, "end": v(7.95, -3.16) * mm});
            skLineSegment(sketch, "E99.34.58", {"start": v(8.04, -2.7) * mm, "end": v(8.05, -2.7) * mm});
            skLineSegment(sketch, "E99.34.59", {"start": v(8, -3.2) * mm, "end": v(8.03, -3.22) * mm});
            skLineSegment(sketch, "E99.34.60", {"start": v(8.14, -2.69) * mm, "end": v(8.16, -2.7) * mm});
            skLineSegment(sketch, "E99.34.61", {"start": v(8.07, -2.7) * mm, "end": v(8.09, -2.69) * mm});
            skLineSegment(sketch, "E99.34.62", {"start": v(7.97, -3.17) * mm, "end": v(7.98, -3.18) * mm});
            skLineSegment(sketch, "E99.34.63", {"start": v(8.12, -2.69) * mm, "end": v(8.14, -2.69) * mm});
            skLineSegment(sketch, "E99.34.64", {"start": v(8.02, -2.7) * mm, "end": v(8.04, -2.7) * mm});
            skLineSegment(sketch, "E99.34.65", {"start": v(7.88, -3.09) * mm, "end": v(7.9, -3.1) * mm});
            skLineSegment(sketch, "E99.34.66", {"start": v(7.9, -3.11) * mm, "end": v(7.91, -3.13) * mm});
            skLineSegment(sketch, "E99.34.67", {"start": v(8, -2.7) * mm, "end": v(8.02, -2.7) * mm});
            skLineSegment(sketch, "E99.34.68", {"start": v(7.91, -3.13) * mm, "end": v(7.92, -3.14) * mm});
            skLineSegment(sketch, "E99.34.69", {"start": v(7.87, -3.07) * mm, "end": v(7.88, -3.09) * mm});
            skLineSegment(sketch, "E99.34.70", {"start": v(7.86, -3.03) * mm, "end": v(7.86, -3.04) * mm});
            skLineSegment(sketch, "E99.34.71", {"start": v(7.87, -3.06) * mm, "end": v(7.87, -3.07) * mm});
            skLineSegment(sketch, "E99.34.72", {"start": v(7.86, -3.04) * mm, "end": v(7.87, -3.06) * mm});
            skLineSegment(sketch, "E99.34.73", {"start": v(7.85, -3) * mm, "end": v(7.85, -3.01) * mm});
            skLineSegment(sketch, "E99.34.74", {"start": v(8, -2.71) * mm, "end": v(8, -2.7) * mm});
            skLineSegment(sketch, "E99.34.75", {"start": v(7.85, -3.01) * mm, "end": v(7.86, -3.03) * mm});
            skLineSegment(sketch, "E99.34.76", {"start": v(7.87, -2.86) * mm, "end": v(7.87, -2.87) * mm});
            skLineSegment(sketch, "E99.34.77", {"start": v(7.85, -2.92) * mm, "end": v(7.85, -2.94) * mm});
            skLineSegment(sketch, "E99.34.78", {"start": v(7.86, -2.9) * mm, "end": v(7.85, -2.92) * mm});
            skLineSegment(sketch, "E99.34.79", {"start": v(7.88, -2.84) * mm, "end": v(7.9, -2.81) * mm});
            skLineSegment(sketch, "E99.34.80", {"start": v(7.94, -2.75) * mm, "end": v(7.95, -2.74) * mm});
            skLineSegment(sketch, "E99.34.81", {"start": v(7.96, -2.73) * mm, "end": v(7.98, -2.72) * mm});
            skLineSegment(sketch, "E99.34.82", {"start": v(7.85, -2.98) * mm, "end": v(7.85, -3) * mm});
            skLineSegment(sketch, "E99.34.83", {"start": v(7.9, -2.8) * mm, "end": v(7.91, -2.78) * mm});
            skLineSegment(sketch, "E99.34.84", {"start": v(7.98, -2.72) * mm, "end": v(8, -2.71) * mm});
            skLineSegment(sketch, "E99.34.85", {"start": v(7.85, -2.94) * mm, "end": v(7.85, -2.96) * mm});
            skLineSegment(sketch, "E99.34.86", {"start": v(7.95, -2.74) * mm, "end": v(7.96, -2.73) * mm});
            skLineSegment(sketch, "E99.34.87", {"start": v(7.9, -2.81) * mm, "end": v(7.9, -2.8) * mm});
            skLineSegment(sketch, "E99.34.88", {"start": v(7.93, -2.76) * mm, "end": v(7.94, -2.75) * mm});
            skLineSegment(sketch, "E99.34.89", {"start": v(7.87, -2.88) * mm, "end": v(7.86, -2.88) * mm});
            skLineSegment(sketch, "E99.34.90", {"start": v(7.86, -2.89) * mm, "end": v(7.86, -2.9) * mm});
            skLineSegment(sketch, "E99.34.91", {"start": v(7.85, -2.96) * mm, "end": v(7.85, -2.98) * mm});
            skLineSegment(sketch, "E99.34.92", {"start": v(7.91, -2.78) * mm, "end": v(7.93, -2.76) * mm});
            skLineSegment(sketch, "E99.34.93", {"start": v(7.88, -2.84) * mm, "end": v(7.88, -2.84) * mm});
            skLineSegment(sketch, "E99.34.94", {"start": v(7.88, -2.85) * mm, "end": v(7.88, -2.84) * mm});
            skLineSegment(sketch, "E99.34.95", {"start": v(7.87, -2.85) * mm, "end": v(7.88, -2.85) * mm});
            skLineSegment(sketch, "E99.34.96", {"start": v(7.87, -2.86) * mm, "end": v(7.87, -2.85) * mm});
            skLineSegment(sketch, "E99.34.97", {"start": v(7.87, -2.86) * mm, "end": v(7.87, -2.86) * mm});
            skLineSegment(sketch, "E99.34.98", {"start": v(7.86, -2.88) * mm, "end": v(7.86, -2.89) * mm});
            skLineSegment(sketch, "E99.34.99", {"start": v(7.87, -2.87) * mm, "end": v(7.87, -2.88) * mm});
            skLineSegment(sketch, "E99.35.0", {"start": v(9.07, -2.15) * mm, "end": v(9.1, -2.18) * mm});
            skLineSegment(sketch, "E99.35.1", {"start": v(9.26, -1.08) * mm, "end": v(9.3, -1.07) * mm});
            skLineSegment(sketch, "E99.35.2", {"start": v(9.19, -2.42) * mm, "end": v(9.18, -2.46) * mm});
            skLineSegment(sketch, "E99.35.3", {"start": v(9.2, -2.39) * mm, "end": v(9.19, -2.42) * mm});
            skLineSegment(sketch, "E99.35.4", {"start": v(8.92, -2.03) * mm, "end": v(8.95, -2.06) * mm});
            skLineSegment(sketch, "E99.35.5", {"start": v(8.84, -1.2) * mm, "end": v(8.89, -1.18) * mm});
            skLineSegment(sketch, "E99.35.6", {"start": v(8.84, -1.98) * mm, "end": v(8.88, -2) * mm});
            skLineSegment(sketch, "E99.35.7", {"start": v(8.55, -1.81) * mm, "end": v(8.6, -1.84) * mm});
            skLineSegment(sketch, "E99.35.8", {"start": v(8.88, -2) * mm, "end": v(8.92, -2.03) * mm});
            skLineSegment(sketch, "E99.35.9", {"start": v(8.64, -1.86) * mm, "end": v(8.68, -1.88) * mm});
            skLineSegment(sketch, "E99.35.10", {"start": v(8.93, -1.17) * mm, "end": v(8.98, -1.16) * mm});
            skLineSegment(sketch, "E99.35.11", {"start": v(8.7, -1.21) * mm, "end": v(8.75, -1.2) * mm});
            skLineSegment(sketch, "E99.35.12", {"start": v(9.03, -1.15) * mm, "end": v(9.07, -1.14) * mm});
            skLineSegment(sketch, "E99.35.13", {"start": v(8.76, -1.93) * mm, "end": v(8.8, -1.95) * mm});
            skLineSegment(sketch, "E99.35.14", {"start": v(9.1, -2.18) * mm, "end": v(9.15, -2.21) * mm});
            skLineSegment(sketch, "E99.35.15", {"start": v(8.72, -1.9) * mm, "end": v(8.76, -1.93) * mm});
            skLineSegment(sketch, "E99.35.16", {"start": v(9.03, -2.12) * mm, "end": v(9.07, -2.15) * mm});
            skLineSegment(sketch, "E99.35.17", {"start": v(8.8, -1.95) * mm, "end": v(8.84, -1.98) * mm});
            skLineSegment(sketch, "E99.35.18", {"start": v(9.21, -1.1) * mm, "end": v(9.26, -1.08) * mm});
            skLineSegment(sketch, "E99.35.19", {"start": v(9.15, -2.21) * mm, "end": v(9.19, -2.24) * mm});
            skLineSegment(sketch, "E99.35.20", {"start": v(9.2, -2.35) * mm, "end": v(9.2, -2.39) * mm});
            skLineSegment(sketch, "E99.35.21", {"start": v(8.66, -1.22) * mm, "end": v(8.7, -1.21) * mm});
            skLineSegment(sketch, "E99.35.22", {"start": v(8.8, -1.2) * mm, "end": v(8.84, -1.2) * mm});
            skLineSegment(sketch, "E99.35.23", {"start": v(9.12, -1.12) * mm, "end": v(9.17, -1.11) * mm});
            skLineSegment(sketch, "E99.35.24", {"start": v(8.95, -2.06) * mm, "end": v(9, -2.1) * mm});
            skLineSegment(sketch, "E99.35.25", {"start": v(8.6, -1.84) * mm, "end": v(8.64, -1.86) * mm});
            skLineSegment(sketch, "E99.35.26", {"start": v(9.19, -2.24) * mm, "end": v(9.22, -2.28) * mm});
            skLineSegment(sketch, "E99.35.27", {"start": v(9.21, -2.31) * mm, "end": v(9.2, -2.35) * mm});
            skLineSegment(sketch, "E99.35.28", {"start": v(9, -2.1) * mm, "end": v(9.03, -2.12) * mm});
            skLineSegment(sketch, "E99.35.29", {"start": v(8.89, -1.18) * mm, "end": v(8.93, -1.17) * mm});
            skLineSegment(sketch, "E99.35.30", {"start": v(9.17, -1.11) * mm, "end": v(9.21, -1.1) * mm});
            skLineSegment(sketch, "E99.35.31", {"start": v(8.68, -1.88) * mm, "end": v(8.72, -1.9) * mm});
            skLineSegment(sketch, "E99.35.32", {"start": v(9.07, -1.14) * mm, "end": v(9.12, -1.12) * mm});
            skLineSegment(sketch, "E99.35.33", {"start": v(8.75, -1.2) * mm, "end": v(8.8, -1.2) * mm});
            skLineSegment(sketch, "E99.35.34", {"start": v(9.3, -1.07) * mm, "end": v(9.35, -1.05) * mm});
            skLineSegment(sketch, "E99.35.35", {"start": v(9.46, -0.87) * mm, "end": v(9.46, -0.83) * mm});
            skLineSegment(sketch, "E99.35.36", {"start": v(8.98, -1.16) * mm, "end": v(9.03, -1.15) * mm});
            skLineSegment(sketch, "E99.35.37", {"start": v(9.46, -0.9) * mm, "end": v(9.46, -0.87) * mm});
            skLineSegment(sketch, "E99.35.38", {"start": v(9.35, -1.05) * mm, "end": v(9.4, -1.03) * mm});
            skLineSegment(sketch, "E99.35.39", {"start": v(9.22, -2.28) * mm, "end": v(9.21, -2.31) * mm});
            skLineSegment(sketch, "E99.35.40", {"start": v(9.4, -1.03) * mm, "end": v(9.45, -1.02) * mm});
            skLineSegment(sketch, "E99.35.41", {"start": v(9.45, -0.94) * mm, "end": v(9.46, -0.9) * mm});
            skLineSegment(sketch, "E99.35.42", {"start": v(9.45, -0.98) * mm, "end": v(9.45, -0.94) * mm});
            skLineSegment(sketch, "E99.35.43", {"start": v(8.61, -1.23) * mm, "end": v(8.66, -1.22) * mm});
            skLineSegment(sketch, "E99.35.44", {"start": v(9.45, -1.02) * mm, "end": v(9.45, -0.98) * mm});
            skLineSegment(sketch, "E99.35.45", {"start": v(8.51, -1.8) * mm, "end": v(8.55, -1.81) * mm});
            skLineSegment(sketch, "E99.35.46", {"start": v(8.4, -1.25) * mm, "end": v(8.42, -1.25) * mm});
            skLineSegment(sketch, "E99.35.47", {"start": v(8.52, -1.23) * mm, "end": v(8.57, -1.23) * mm});
            skLineSegment(sketch, "E99.35.48", {"start": v(8.57, -1.23) * mm, "end": v(8.61, -1.23) * mm});
            skLineSegment(sketch, "E99.35.49", {"start": v(8.35, -1.71) * mm, "end": v(8.36, -1.72) * mm});
            skLineSegment(sketch, "E99.35.50", {"start": v(8.43, -1.24) * mm, "end": v(8.45, -1.24) * mm});
            skLineSegment(sketch, "E99.35.51", {"start": v(8.31, -1.68) * mm, "end": v(8.32, -1.7) * mm});
            skLineSegment(sketch, "E99.35.52", {"start": v(8.47, -1.78) * mm, "end": v(8.51, -1.8) * mm});
            skLineSegment(sketch, "E99.35.53", {"start": v(8.38, -1.73) * mm, "end": v(8.4, -1.74) * mm});
            skLineSegment(sketch, "E99.35.54", {"start": v(8.41, -1.75) * mm, "end": v(8.43, -1.76) * mm});
            skLineSegment(sketch, "E99.35.55", {"start": v(8.45, -1.24) * mm, "end": v(8.47, -1.24) * mm});
            skLineSegment(sketch, "E99.35.56", {"start": v(8.5, -1.23) * mm, "end": v(8.52, -1.23) * mm});
            skLineSegment(sketch, "E99.35.57", {"start": v(8.36, -1.72) * mm, "end": v(8.38, -1.73) * mm});
            skLineSegment(sketch, "E99.35.58", {"start": v(8.38, -1.26) * mm, "end": v(8.4, -1.25) * mm});
            skLineSegment(sketch, "E99.35.59", {"start": v(8.43, -1.76) * mm, "end": v(8.47, -1.78) * mm});
            skLineSegment(sketch, "E99.35.60", {"start": v(8.48, -1.23) * mm, "end": v(8.5, -1.23) * mm});
            skLineSegment(sketch, "E99.35.61", {"start": v(8.42, -1.25) * mm, "end": v(8.43, -1.24) * mm});
            skLineSegment(sketch, "E99.35.62", {"start": v(8.4, -1.74) * mm, "end": v(8.41, -1.75) * mm});
            skLineSegment(sketch, "E99.35.63", {"start": v(8.47, -1.24) * mm, "end": v(8.48, -1.23) * mm});
            skLineSegment(sketch, "E99.35.64", {"start": v(8.37, -1.27) * mm, "end": v(8.38, -1.26) * mm});
            skLineSegment(sketch, "E99.35.65", {"start": v(8.3, -1.67) * mm, "end": v(8.31, -1.68) * mm});
            skLineSegment(sketch, "E99.35.66", {"start": v(8.32, -1.7) * mm, "end": v(8.34, -1.7) * mm});
            skLineSegment(sketch, "E99.35.67", {"start": v(8.36, -1.28) * mm, "end": v(8.37, -1.27) * mm});
            skLineSegment(sketch, "E99.35.68", {"start": v(8.34, -1.7) * mm, "end": v(8.35, -1.71) * mm});
            skLineSegment(sketch, "E99.35.69", {"start": v(8.29, -1.66) * mm, "end": v(8.3, -1.67) * mm});
            skLineSegment(sketch, "E99.35.70", {"start": v(8.26, -1.62) * mm, "end": v(8.27, -1.63) * mm});
            skLineSegment(sketch, "E99.35.71", {"start": v(8.28, -1.65) * mm, "end": v(8.29, -1.66) * mm});
            skLineSegment(sketch, "E99.35.72", {"start": v(8.27, -1.63) * mm, "end": v(8.28, -1.65) * mm});
            skLineSegment(sketch, "E99.35.73", {"start": v(8.25, -1.59) * mm, "end": v(8.26, -1.6) * mm});
            skLineSegment(sketch, "E99.35.74", {"start": v(8.34, -1.29) * mm, "end": v(8.36, -1.28) * mm});
            skLineSegment(sketch, "E99.35.75", {"start": v(8.26, -1.6) * mm, "end": v(8.26, -1.62) * mm});
            skLineSegment(sketch, "E99.35.76", {"start": v(8.25, -1.45) * mm, "end": v(8.25, -1.46) * mm});
            skLineSegment(sketch, "E99.35.77", {"start": v(8.24, -1.51) * mm, "end": v(8.24, -1.53) * mm});
            skLineSegment(sketch, "E99.35.78", {"start": v(8.24, -1.48) * mm, "end": v(8.24, -1.51) * mm});
            skLineSegment(sketch, "E99.35.79", {"start": v(8.25, -1.42) * mm, "end": v(8.26, -1.4) * mm});
            skLineSegment(sketch, "E99.35.80", {"start": v(8.3, -1.33) * mm, "end": v(8.3, -1.32) * mm});
            skLineSegment(sketch, "E99.35.81", {"start": v(8.32, -1.3) * mm, "end": v(8.33, -1.3) * mm});
            skLineSegment(sketch, "E99.35.82", {"start": v(8.24, -1.57) * mm, "end": v(8.25, -1.59) * mm});
            skLineSegment(sketch, "E99.35.83", {"start": v(8.27, -1.38) * mm, "end": v(8.28, -1.36) * mm});
            skLineSegment(sketch, "E99.35.84", {"start": v(8.33, -1.3) * mm, "end": v(8.34, -1.29) * mm});
            skLineSegment(sketch, "E99.35.85", {"start": v(8.24, -1.53) * mm, "end": v(8.24, -1.55) * mm});
            skLineSegment(sketch, "E99.35.86", {"start": v(8.3, -1.32) * mm, "end": v(8.32, -1.3) * mm});
            skLineSegment(sketch, "E99.35.87", {"start": v(8.26, -1.4) * mm, "end": v(8.27, -1.38) * mm});
            skLineSegment(sketch, "E99.35.88", {"start": v(8.28, -1.34) * mm, "end": v(8.3, -1.33) * mm});
            skLineSegment(sketch, "E99.35.89", {"start": v(8.25, -1.47) * mm, "end": v(8.24, -1.47) * mm});
            skLineSegment(sketch, "E99.35.90", {"start": v(8.24, -1.48) * mm, "end": v(8.24, -1.48) * mm});
            skLineSegment(sketch, "E99.35.91", {"start": v(8.24, -1.55) * mm, "end": v(8.24, -1.57) * mm});
            skLineSegment(sketch, "E99.35.92", {"start": v(8.28, -1.36) * mm, "end": v(8.28, -1.34) * mm});
            skLineSegment(sketch, "E99.35.93", {"start": v(8.25, -1.43) * mm, "end": v(8.25, -1.42) * mm});
            skLineSegment(sketch, "E99.35.94", {"start": v(8.25, -1.44) * mm, "end": v(8.25, -1.43) * mm});
            skLineSegment(sketch, "E99.35.95", {"start": v(8.25, -1.44) * mm, "end": v(8.25, -1.44) * mm});
            skLineSegment(sketch, "E99.35.96", {"start": v(8.25, -1.45) * mm, "end": v(8.25, -1.44) * mm});
            skLineSegment(sketch, "E99.35.97", {"start": v(8.25, -1.45) * mm, "end": v(8.25, -1.45) * mm});
            skLineSegment(sketch, "E99.35.98", {"start": v(8.24, -1.47) * mm, "end": v(8.24, -1.48) * mm});
            skLineSegment(sketch, "E99.35.99", {"start": v(8.25, -1.46) * mm, "end": v(8.25, -1.47) * mm});
            skPoint(sketch, "E99.center", {"position": v(0, 0) * mm});
            skSolve(sketch);
        }
        {
            var Q0;
            Q0=makeQuery(id+"F0.imprint","IMPRINT",FACE,{"disambiguationData":[TD([[makeQuery(id+"F0.imprint","IMPRINT",EDGE,{"derivedFrom":sQuery(id+"F0.wireOp",EDGE,"E0")}),1.0]])]});
            extrude(context, id + "F1", {"entities" : qUnion([Q0]), "offsetDistance" : 25 * mm, "depth" : 3 * mm});
        }
        {
            var Q0;
            Q0=qCreatedBy(makeId("Top.planeOp"),FACE);
            var sketch = newSketch(context, id + "F2", { "sketchPlane" : qUnion([Q0])});
            skLineSegment(sketch, "E100.bottom", {"start": v(0, 0) * mm, "end": v(10.5, 0) * mm});
            skLineSegment(sketch, "E100.top", {"start": v(0, 1) * mm, "end": v(10.5, 1) * mm});
            skLineSegment(sketch, "E100.left", {"start": v(0, 0) * mm, "end": v(0, 1) * mm});
            skLineSegment(sketch, "E100.right", {"start": v(10.5, 0) * mm, "end": v(10.5, 1) * mm});
            skLineSegment(sketch, "E101.bottom", {"start": v(0, 1) * mm, "end": v(10, 1) * mm});
            skLineSegment(sketch, "E101.top", {"start": v(0, 8.5) * mm, "end": v(10, 8.5) * mm});
            skLineSegment(sketch, "E101.left", {"start": v(0, 1) * mm, "end": v(0, 8.5) * mm});
            skLineSegment(sketch, "E101.right", {"start": v(10, 1) * mm, "end": v(10, 8.5) * mm});
            skLineSegment(sketch, "E102", {"start": v(10, 1) * mm, "end": v(10, 0) * mm});
            skLineSegment(sketch, "E103", {"start": v(3.05, 8.5) * mm, "end": v(3.05, 0) * mm});
            skLineSegment(sketch, "E104", {"start": v(0, 3) * mm, "end": v(3.05, 3) * mm});
            skLineSegment(sketch, "E105", {"start": v(2.7, 3) * mm, "end": v(2.7, 0) * mm});
            skSolve(sketch);
        }
        {
            var Q0;
            {var subQ0=sQuery(id+"F2.wireOp",EDGE,"E101.right");Q0=makeQuery(id+"F2.imprint","IMPRINT",FACE,{"disambiguationData":[TD([[makeQuery(id+"F2.imprint","IMPRINT",EDGE,{"derivedFrom":subQ0}),1.0]])]});}
            var Q1;
            {var subQ0=sQuery(id+"F2.wireOp",EDGE,"E102");Q1=makeQuery(id+"F2.imprint","IMPRINT",FACE,{"disambiguationData":[TD([[makeQuery(id+"F2.imprint","IMPRINT",EDGE,{"derivedFrom":subQ0}),-1.0]])]});}
            var Q2;
            Q2=makeQuery(id+"F2.imprint","IMPRINT",FACE,{"disambiguationData":[TD([[makeQuery(id+"F2.imprint","IMPRINT",EDGE,{"derivedFrom":sQuery(id+"F2.wireOp",EDGE,"E100.top")}),-1.0]])]});
            var Q3;
            {var subQ0=sQuery(id+"F2.wireOp",EDGE,"E103");var subQ1=sQuery(id+"F2.wireOp",EDGE,"E100.bottom");var subQ2=makeQuery(id+"F2.imprint","INTERSECT",VERTEX,{"derivedFrom":[subQ1,subQ0]});Q3=makeQuery(id+"F2.imprint","IMPRINT",FACE,{"disambiguationData":[TD([[makeQuery(id+"F2.imprint","IMPRINT",EDGE,{"disambiguationData":[TD([[subQ2,1.0]])],"derivedFrom":subQ1}),1.0]])]});}
            var Q4;
            {var subQ0=sQuery(id+"F2.wireOp",EDGE,"E105");var subQ1=sQuery(id+"F2.wireOp",EDGE,"E101.bottom");var subQ2=makeQuery(id+"F2.imprint","INTERSECT",VERTEX,{"derivedFrom":[subQ1,subQ0]});Q4=makeQuery(id+"F2.imprint","IMPRINT",FACE,{"disambiguationData":[TD([[makeQuery(id+"F2.imprint","IMPRINT",EDGE,{"disambiguationData":[TD([[subQ2,-1.0]])],"derivedFrom":subQ1}),1.0]])]});}
            var Q5;
            Q5=sQuery(id+"F2.wireOp",EDGE,"E101.left");
            revolve(context, id + "F3", {"operationType" : NewBodyOperationType.ADD, "surfaceOperationType" : NewSurfaceOperationType.NEW, "entities" : qUnion([Q0, Q1, Q2, Q3, Q4]), "axis" : qUnion([Q5]), "revolveType" : RevolveType.FULL});
        }
        {
            var Q0;
            Q0=makeQuery(id+"F3.opRevolve","SWEPT_FACE",FACE,{"disambiguationData":[OSD([sQuery(id+"F2.wireOp",EDGE,"E100.bottom")])]});
            var sketch = newSketch(context, id + "F4", { "sketchPlane" : qUnion([Q0])});
            skCircle(sketch, "E106", {"center": v(0, 0) * mm, "radius": 3.05 * mm});
            skSolve(sketch);
        }
        {
            var Q0;
            Q0=qSketchRegion(id+"F4",true);
            extrude(context, id + "F5", {"entities" : qUnion([Q0]), "operationType" : NewBodyOperationType.REMOVE, "depth" : 3 * mm});
        }
        {
            var Q0;
            Q0=makeQuery(id+"F3.opRevolve","SWEPT_FACE",FACE,{"disambiguationData":[OSD([sQuery(id+"F2.wireOp",EDGE,"E101.top")])]});
            var sketch = newSketch(context, id + "F6", { "sketchPlane" : qUnion([Q0])});
            skCircle(sketch, "E107", {"center": v(0, 0) * mm, "radius": 4.25 * mm});
            skCircle(sketch, "E108", {"center": v(0, 0) * mm, "radius": 7.5 * mm});
            skLineSegment(sketch, "E109.bottom", {"start": v(1, 3.15) * mm, "end": v(-1, 3.15) * mm});
            skLineSegment(sketch, "E109.top", {"start": v(1, 8.08) * mm, "end": v(-1, 8.08) * mm});
            skLineSegment(sketch, "E109.left", {"start": v(1, 3.15) * mm, "end": v(1, 8.08) * mm});
            skLineSegment(sketch, "E109.right", {"start": v(-1, 3.15) * mm, "end": v(-1, 8.08) * mm});
            skPoint(sketch, "E109.middle", {"position": v(0, 5.62) * mm});
            skLineSegment(sketch, "E110.1.0", {"start": v(-2.23, -2.44) * mm, "end": v(-6.5, -4.9) * mm});
            skLineSegment(sketch, "E110.1.1", {"start": v(-3.23, -0.7) * mm, "end": v(-7.5, -3.17) * mm});
            skLineSegment(sketch, "E110.1.2", {"start": v(-7.5, -3.17) * mm, "end": v(-6.5, -4.9) * mm});
            skLineSegment(sketch, "E110.1.3", {"start": v(-3.23, -0.7) * mm, "end": v(-2.23, -2.44) * mm});
            skLineSegment(sketch, "E110.2.0", {"start": v(3.23, -0.7) * mm, "end": v(7.5, -3.17) * mm});
            skLineSegment(sketch, "E110.2.1", {"start": v(2.23, -2.44) * mm, "end": v(6.5, -4.9) * mm});
            skLineSegment(sketch, "E110.2.2", {"start": v(6.5, -4.9) * mm, "end": v(7.5, -3.17) * mm});
            skLineSegment(sketch, "E110.2.3", {"start": v(2.23, -2.44) * mm, "end": v(3.23, -0.7) * mm});
            skSolve(sketch);
        }
        {
            var Q0;
            {var subQ0=sQuery(id+"F6.wireOp",EDGE,"E109.right");var subQ1=sQuery(id+"F6.wireOp",EDGE,"E107");var subQ2=makeQuery(id+"F6.imprint","INTERSECT",VERTEX,{"derivedFrom":[subQ1,subQ0]});Q0=makeQuery(id+"F6.imprint","IMPRINT",FACE,{"disambiguationData":[TD([[makeQuery(id+"F6.imprint","IMPRINT",EDGE,{"disambiguationData":[TD([[subQ2,-1.0]])],"derivedFrom":subQ1}),-1.0]])]});}
            var Q1;
            {var subQ0=sQuery(id+"F6.wireOp",EDGE,"E109.left");var subQ1=sQuery(id+"F6.wireOp",EDGE,"E107");var subQ2=makeQuery(id+"F6.imprint","INTERSECT",VERTEX,{"derivedFrom":[subQ1,subQ0]});Q1=makeQuery(id+"F6.imprint","IMPRINT",FACE,{"disambiguationData":[TD([[makeQuery(id+"F6.imprint","IMPRINT",EDGE,{"disambiguationData":[TD([[subQ2,1.0]])],"derivedFrom":subQ1}),-1.0]])]});}
            var Q2;
            {var subQ0=sQuery(id+"F6.wireOp",EDGE,"E110.1.0");var subQ1=sQuery(id+"F6.wireOp",EDGE,"E107");var subQ2=makeQuery(id+"F6.imprint","INTERSECT",VERTEX,{"derivedFrom":[subQ1,subQ0]});Q2=makeQuery(id+"F6.imprint","IMPRINT",FACE,{"disambiguationData":[TD([[makeQuery(id+"F6.imprint","IMPRINT",EDGE,{"disambiguationData":[TD([[subQ2,-1.0]])],"derivedFrom":subQ1}),-1.0]])]});}
            extrude(context, id + "F7", {"entities" : qUnion([Q0, Q1, Q2]), "operationType" : NewBodyOperationType.REMOVE, "oppositeDirection" : true, "depth" : 25 * mm});
        }
    });
